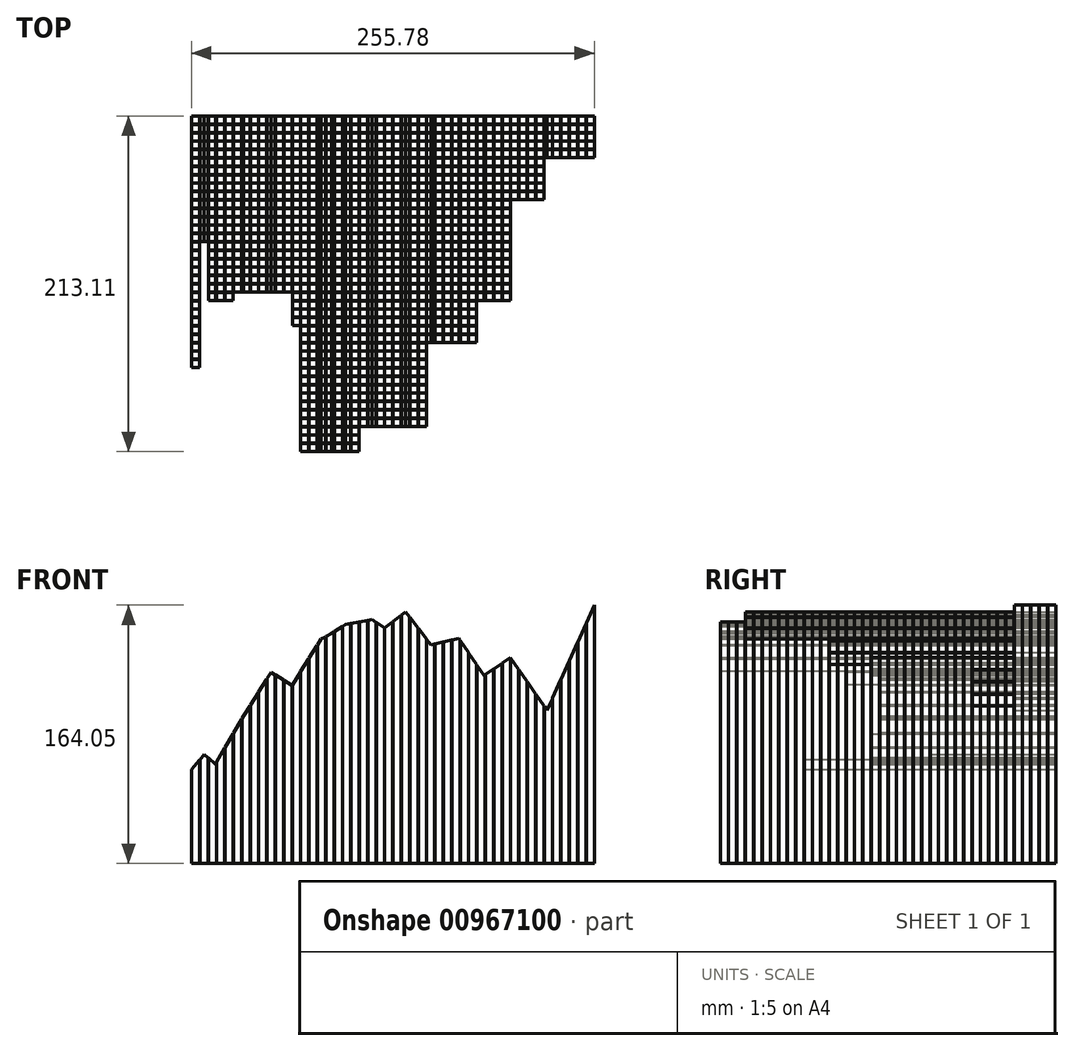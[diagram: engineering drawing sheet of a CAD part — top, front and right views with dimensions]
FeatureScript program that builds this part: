
annotation { "Feature Type Name" : "Feature", "Feature Type Description" : "" }
export const myFeature = defineFeature(function(context is Context, id is Id, definition is map)
    precondition{}
    {
        {
            var Q0;
            Q0=qCreatedBy(makeId("Top.planeOp"),FACE);
            var sketch = newSketch(context, id + "F0", { "sketchPlane" : qUnion([Q0])});
            skLineSegment(sketch, "E0.bottom", {"start": v(0, 0) * mm, "end": v(5.08, 0) * mm});
            skLineSegment(sketch, "E0.top", {"start": v(0, -5.08) * mm, "end": v(5.08, -5.08) * mm});
            skLineSegment(sketch, "E0.left", {"start": v(0, 0) * mm, "end": v(0, -5.08) * mm});
            skLineSegment(sketch, "E0.right", {"start": v(5.08, 0) * mm, "end": v(5.08, -5.08) * mm});
            skLineSegment(sketch, "E1.1.0.0", {"start": v(5.33, -5.08) * mm, "end": v(10.41, -5.08) * mm});
            skLineSegment(sketch, "E1.1.0.1", {"start": v(5.33, 0) * mm, "end": v(5.33, -5.08) * mm});
            skLineSegment(sketch, "E1.1.0.2", {"start": v(5.33, 0) * mm, "end": v(10.41, 0) * mm});
            skLineSegment(sketch, "E1.1.0.3", {"start": v(10.41, 0) * mm, "end": v(10.41, -5.08) * mm});
            skLineSegment(sketch, "E1.2.0.0", {"start": v(10.67, -5.08) * mm, "end": v(15.75, -5.08) * mm});
            skLineSegment(sketch, "E1.2.0.1", {"start": v(10.67, 0) * mm, "end": v(10.67, -5.08) * mm});
            skLineSegment(sketch, "E1.2.0.2", {"start": v(10.67, 0) * mm, "end": v(15.75, 0) * mm});
            skLineSegment(sketch, "E1.2.0.3", {"start": v(15.75, 0) * mm, "end": v(15.75, -5.08) * mm});
            skLineSegment(sketch, "E1.3.0.0", {"start": v(16, -5.08) * mm, "end": v(21.08, -5.08) * mm});
            skLineSegment(sketch, "E1.3.0.1", {"start": v(16, 0) * mm, "end": v(16, -5.08) * mm});
            skLineSegment(sketch, "E1.3.0.2", {"start": v(16, 0) * mm, "end": v(21.08, 0) * mm});
            skLineSegment(sketch, "E1.3.0.3", {"start": v(21.08, 0) * mm, "end": v(21.08, -5.08) * mm});
            skLineSegment(sketch, "E1.4.0.0", {"start": v(21.34, -5.08) * mm, "end": v(26.42, -5.08) * mm});
            skLineSegment(sketch, "E1.4.0.1", {"start": v(21.34, 0) * mm, "end": v(21.34, -5.08) * mm});
            skLineSegment(sketch, "E1.4.0.2", {"start": v(21.34, 0) * mm, "end": v(26.42, 0) * mm});
            skLineSegment(sketch, "E1.4.0.3", {"start": v(26.42, 0) * mm, "end": v(26.42, -5.08) * mm});
            skLineSegment(sketch, "E1.5.0.0", {"start": v(26.67, -5.08) * mm, "end": v(31.75, -5.08) * mm});
            skLineSegment(sketch, "E1.5.0.1", {"start": v(26.67, 0) * mm, "end": v(26.67, -5.08) * mm});
            skLineSegment(sketch, "E1.5.0.2", {"start": v(26.67, 0) * mm, "end": v(31.75, 0) * mm});
            skLineSegment(sketch, "E1.5.0.3", {"start": v(31.75, 0) * mm, "end": v(31.75, -5.08) * mm});
            skLineSegment(sketch, "E1.6.0.0", {"start": v(32, -5.08) * mm, "end": v(37.08, -5.08) * mm});
            skLineSegment(sketch, "E1.6.0.1", {"start": v(32, 0) * mm, "end": v(32, -5.08) * mm});
            skLineSegment(sketch, "E1.6.0.2", {"start": v(32, 0) * mm, "end": v(37.08, 0) * mm});
            skLineSegment(sketch, "E1.6.0.3", {"start": v(37.08, 0) * mm, "end": v(37.08, -5.08) * mm});
            skLineSegment(sketch, "E1.7.0.0", {"start": v(37.34, -5.08) * mm, "end": v(42.42, -5.08) * mm});
            skLineSegment(sketch, "E1.7.0.1", {"start": v(37.34, 0) * mm, "end": v(37.34, -5.08) * mm});
            skLineSegment(sketch, "E1.7.0.2", {"start": v(37.34, 0) * mm, "end": v(42.42, 0) * mm});
            skLineSegment(sketch, "E1.7.0.3", {"start": v(42.42, 0) * mm, "end": v(42.42, -5.08) * mm});
            skLineSegment(sketch, "E1.8.0.0", {"start": v(42.67, -5.08) * mm, "end": v(47.75, -5.08) * mm});
            skLineSegment(sketch, "E1.8.0.1", {"start": v(42.67, 0) * mm, "end": v(42.67, -5.08) * mm});
            skLineSegment(sketch, "E1.8.0.2", {"start": v(42.67, 0) * mm, "end": v(47.75, 0) * mm});
            skLineSegment(sketch, "E1.8.0.3", {"start": v(47.75, 0) * mm, "end": v(47.75, -5.08) * mm});
            skLineSegment(sketch, "E1.9.0.0", {"start": v(48, -5.08) * mm, "end": v(53.09, -5.08) * mm});
            skLineSegment(sketch, "E1.9.0.1", {"start": v(48, 0) * mm, "end": v(48, -5.08) * mm});
            skLineSegment(sketch, "E1.9.0.2", {"start": v(48, 0) * mm, "end": v(53.09, 0) * mm});
            skLineSegment(sketch, "E1.9.0.3", {"start": v(53.09, 0) * mm, "end": v(53.09, -5.08) * mm});
            skLineSegment(sketch, "E1.10.0.0", {"start": v(53.34, -5.08) * mm, "end": v(58.42, -5.08) * mm});
            skLineSegment(sketch, "E1.10.0.1", {"start": v(53.34, 0) * mm, "end": v(53.34, -5.08) * mm});
            skLineSegment(sketch, "E1.10.0.2", {"start": v(53.34, 0) * mm, "end": v(58.42, 0) * mm});
            skLineSegment(sketch, "E1.10.0.3", {"start": v(58.42, 0) * mm, "end": v(58.42, -5.08) * mm});
            skLineSegment(sketch, "E1.11.0.0", {"start": v(58.67, -5.08) * mm, "end": v(63.75, -5.08) * mm});
            skLineSegment(sketch, "E1.11.0.1", {"start": v(58.67, 0) * mm, "end": v(58.67, -5.08) * mm});
            skLineSegment(sketch, "E1.11.0.2", {"start": v(58.67, 0) * mm, "end": v(63.75, 0) * mm});
            skLineSegment(sketch, "E1.11.0.3", {"start": v(63.75, 0) * mm, "end": v(63.75, -5.08) * mm});
            skLineSegment(sketch, "E1.12.0.0", {"start": v(64, -5.08) * mm, "end": v(69.09, -5.08) * mm});
            skLineSegment(sketch, "E1.12.0.1", {"start": v(64, 0) * mm, "end": v(64, -5.08) * mm});
            skLineSegment(sketch, "E1.12.0.2", {"start": v(64, 0) * mm, "end": v(69.09, 0) * mm});
            skLineSegment(sketch, "E1.12.0.3", {"start": v(69.09, 0) * mm, "end": v(69.09, -5.08) * mm});
            skLineSegment(sketch, "E1.13.0.0", {"start": v(69.34, -5.08) * mm, "end": v(74.42, -5.08) * mm});
            skLineSegment(sketch, "E1.13.0.1", {"start": v(69.34, 0) * mm, "end": v(69.34, -5.08) * mm});
            skLineSegment(sketch, "E1.13.0.2", {"start": v(69.34, 0) * mm, "end": v(74.42, 0) * mm});
            skLineSegment(sketch, "E1.13.0.3", {"start": v(74.42, 0) * mm, "end": v(74.42, -5.08) * mm});
            skLineSegment(sketch, "E1.14.0.0", {"start": v(74.68, -5.08) * mm, "end": v(79.76, -5.08) * mm});
            skLineSegment(sketch, "E1.14.0.1", {"start": v(74.68, 0) * mm, "end": v(74.68, -5.08) * mm});
            skLineSegment(sketch, "E1.14.0.2", {"start": v(74.68, 0) * mm, "end": v(79.76, 0) * mm});
            skLineSegment(sketch, "E1.14.0.3", {"start": v(79.76, 0) * mm, "end": v(79.76, -5.08) * mm});
            skLineSegment(sketch, "E1.15.0.0", {"start": v(80, -5.08) * mm, "end": v(85.1, -5.08) * mm});
            skLineSegment(sketch, "E1.15.0.1", {"start": v(80, 0) * mm, "end": v(80, -5.08) * mm});
            skLineSegment(sketch, "E1.15.0.2", {"start": v(80, 0) * mm, "end": v(85.1, 0) * mm});
            skLineSegment(sketch, "E1.15.0.3", {"start": v(85.1, 0) * mm, "end": v(85.1, -5.08) * mm});
            skLineSegment(sketch, "E1.16.0.0", {"start": v(85.34, -5.08) * mm, "end": v(90.42, -5.08) * mm});
            skLineSegment(sketch, "E1.16.0.1", {"start": v(85.34, 0) * mm, "end": v(85.34, -5.08) * mm});
            skLineSegment(sketch, "E1.16.0.2", {"start": v(85.34, 0) * mm, "end": v(90.42, 0) * mm});
            skLineSegment(sketch, "E1.16.0.3", {"start": v(90.42, 0) * mm, "end": v(90.42, -5.08) * mm});
            skLineSegment(sketch, "E1.17.0.0", {"start": v(90.68, -5.08) * mm, "end": v(95.76, -5.08) * mm});
            skLineSegment(sketch, "E1.17.0.1", {"start": v(90.68, 0) * mm, "end": v(90.68, -5.08) * mm});
            skLineSegment(sketch, "E1.17.0.2", {"start": v(90.68, 0) * mm, "end": v(95.76, 0) * mm});
            skLineSegment(sketch, "E1.17.0.3", {"start": v(95.76, 0) * mm, "end": v(95.76, -5.08) * mm});
            skLineSegment(sketch, "E1.18.0.0", {"start": v(96.01, -5.08) * mm, "end": v(101.1, -5.08) * mm});
            skLineSegment(sketch, "E1.18.0.1", {"start": v(96.01, 0) * mm, "end": v(96.01, -5.08) * mm});
            skLineSegment(sketch, "E1.18.0.2", {"start": v(96.01, 0) * mm, "end": v(101.1, 0) * mm});
            skLineSegment(sketch, "E1.18.0.3", {"start": v(101.1, 0) * mm, "end": v(101.1, -5.08) * mm});
            skLineSegment(sketch, "E1.19.0.0", {"start": v(101.35, -5.08) * mm, "end": v(106.43, -5.08) * mm});
            skLineSegment(sketch, "E1.19.0.1", {"start": v(101.35, 0) * mm, "end": v(101.35, -5.08) * mm});
            skLineSegment(sketch, "E1.19.0.2", {"start": v(101.35, 0) * mm, "end": v(106.43, 0) * mm});
            skLineSegment(sketch, "E1.19.0.3", {"start": v(106.43, 0) * mm, "end": v(106.43, -5.08) * mm});
            skLineSegment(sketch, "E1.20.0.0", {"start": v(106.68, -5.08) * mm, "end": v(111.76, -5.08) * mm});
            skLineSegment(sketch, "E1.20.0.1", {"start": v(106.68, 0) * mm, "end": v(106.68, -5.08) * mm});
            skLineSegment(sketch, "E1.20.0.2", {"start": v(106.68, 0) * mm, "end": v(111.76, 0) * mm});
            skLineSegment(sketch, "E1.20.0.3", {"start": v(111.76, 0) * mm, "end": v(111.76, -5.08) * mm});
            skLineSegment(sketch, "E1.21.0.0", {"start": v(112.01, -5.08) * mm, "end": v(117.1, -5.08) * mm});
            skLineSegment(sketch, "E1.21.0.1", {"start": v(112.01, 0) * mm, "end": v(112.01, -5.08) * mm});
            skLineSegment(sketch, "E1.21.0.2", {"start": v(112.01, 0) * mm, "end": v(117.1, 0) * mm});
            skLineSegment(sketch, "E1.21.0.3", {"start": v(117.1, 0) * mm, "end": v(117.1, -5.08) * mm});
            skLineSegment(sketch, "E1.22.0.0", {"start": v(117.35, -5.08) * mm, "end": v(122.43, -5.08) * mm});
            skLineSegment(sketch, "E1.22.0.1", {"start": v(117.35, 0) * mm, "end": v(117.35, -5.08) * mm});
            skLineSegment(sketch, "E1.22.0.2", {"start": v(117.35, 0) * mm, "end": v(122.43, 0) * mm});
            skLineSegment(sketch, "E1.22.0.3", {"start": v(122.43, 0) * mm, "end": v(122.43, -5.08) * mm});
            skLineSegment(sketch, "E1.23.0.0", {"start": v(122.68, -5.08) * mm, "end": v(127.76, -5.08) * mm});
            skLineSegment(sketch, "E1.23.0.1", {"start": v(122.68, 0) * mm, "end": v(122.68, -5.08) * mm});
            skLineSegment(sketch, "E1.23.0.2", {"start": v(122.68, 0) * mm, "end": v(127.76, 0) * mm});
            skLineSegment(sketch, "E1.23.0.3", {"start": v(127.76, 0) * mm, "end": v(127.76, -5.08) * mm});
            skLineSegment(sketch, "E1.24.0.0", {"start": v(128.02, -5.08) * mm, "end": v(133.1, -5.08) * mm});
            skLineSegment(sketch, "E1.24.0.1", {"start": v(128.02, 0) * mm, "end": v(128.02, -5.08) * mm});
            skLineSegment(sketch, "E1.24.0.2", {"start": v(128.02, 0) * mm, "end": v(133.1, 0) * mm});
            skLineSegment(sketch, "E1.24.0.3", {"start": v(133.1, 0) * mm, "end": v(133.1, -5.08) * mm});
            skLineSegment(sketch, "E1.25.0.0", {"start": v(133.35, -5.08) * mm, "end": v(138.43, -5.08) * mm});
            skLineSegment(sketch, "E1.25.0.1", {"start": v(133.35, 0) * mm, "end": v(133.35, -5.08) * mm});
            skLineSegment(sketch, "E1.25.0.2", {"start": v(133.35, 0) * mm, "end": v(138.43, 0) * mm});
            skLineSegment(sketch, "E1.25.0.3", {"start": v(138.43, 0) * mm, "end": v(138.43, -5.08) * mm});
            skLineSegment(sketch, "E1.26.0.0", {"start": v(138.68, -5.08) * mm, "end": v(143.76, -5.08) * mm});
            skLineSegment(sketch, "E1.26.0.1", {"start": v(138.68, 0) * mm, "end": v(138.68, -5.08) * mm});
            skLineSegment(sketch, "E1.26.0.2", {"start": v(138.68, 0) * mm, "end": v(143.76, 0) * mm});
            skLineSegment(sketch, "E1.26.0.3", {"start": v(143.76, 0) * mm, "end": v(143.76, -5.08) * mm});
            skLineSegment(sketch, "E1.27.0.0", {"start": v(144.02, -5.08) * mm, "end": v(149.1, -5.08) * mm});
            skLineSegment(sketch, "E1.27.0.1", {"start": v(144.02, 0) * mm, "end": v(144.02, -5.08) * mm});
            skLineSegment(sketch, "E1.27.0.2", {"start": v(144.02, 0) * mm, "end": v(149.1, 0) * mm});
            skLineSegment(sketch, "E1.27.0.3", {"start": v(149.1, 0) * mm, "end": v(149.1, -5.08) * mm});
            skLineSegment(sketch, "E1.28.0.0", {"start": v(149.35, -5.08) * mm, "end": v(154.43, -5.08) * mm});
            skLineSegment(sketch, "E1.28.0.1", {"start": v(149.35, 0) * mm, "end": v(149.35, -5.08) * mm});
            skLineSegment(sketch, "E1.28.0.2", {"start": v(149.35, 0) * mm, "end": v(154.43, 0) * mm});
            skLineSegment(sketch, "E1.28.0.3", {"start": v(154.43, 0) * mm, "end": v(154.43, -5.08) * mm});
            skLineSegment(sketch, "E1.29.0.0", {"start": v(154.69, -5.08) * mm, "end": v(159.77, -5.08) * mm});
            skLineSegment(sketch, "E1.29.0.1", {"start": v(154.69, 0) * mm, "end": v(154.69, -5.08) * mm});
            skLineSegment(sketch, "E1.29.0.2", {"start": v(154.69, 0) * mm, "end": v(159.77, 0) * mm});
            skLineSegment(sketch, "E1.29.0.3", {"start": v(159.77, 0) * mm, "end": v(159.77, -5.08) * mm});
            skLineSegment(sketch, "E1.30.0.0", {"start": v(160.02, -5.08) * mm, "end": v(165.1, -5.08) * mm});
            skLineSegment(sketch, "E1.30.0.1", {"start": v(160.02, 0) * mm, "end": v(160.02, -5.08) * mm});
            skLineSegment(sketch, "E1.30.0.2", {"start": v(160.02, 0) * mm, "end": v(165.1, 0) * mm});
            skLineSegment(sketch, "E1.30.0.3", {"start": v(165.1, 0) * mm, "end": v(165.1, -5.08) * mm});
            skLineSegment(sketch, "E1.31.0.0", {"start": v(165.35, -5.08) * mm, "end": v(170.43, -5.08) * mm});
            skLineSegment(sketch, "E1.31.0.1", {"start": v(165.35, 0) * mm, "end": v(165.35, -5.08) * mm});
            skLineSegment(sketch, "E1.31.0.2", {"start": v(165.35, 0) * mm, "end": v(170.43, 0) * mm});
            skLineSegment(sketch, "E1.31.0.3", {"start": v(170.43, 0) * mm, "end": v(170.43, -5.08) * mm});
            skLineSegment(sketch, "E1.32.0.0", {"start": v(170.69, -5.08) * mm, "end": v(175.77, -5.08) * mm});
            skLineSegment(sketch, "E1.32.0.1", {"start": v(170.69, 0) * mm, "end": v(170.69, -5.08) * mm});
            skLineSegment(sketch, "E1.32.0.2", {"start": v(170.69, 0) * mm, "end": v(175.77, 0) * mm});
            skLineSegment(sketch, "E1.32.0.3", {"start": v(175.77, 0) * mm, "end": v(175.77, -5.08) * mm});
            skLineSegment(sketch, "E1.33.0.0", {"start": v(176.02, -5.08) * mm, "end": v(181.1, -5.08) * mm});
            skLineSegment(sketch, "E1.33.0.1", {"start": v(176.02, 0) * mm, "end": v(176.02, -5.08) * mm});
            skLineSegment(sketch, "E1.33.0.2", {"start": v(176.02, 0) * mm, "end": v(181.1, 0) * mm});
            skLineSegment(sketch, "E1.33.0.3", {"start": v(181.1, 0) * mm, "end": v(181.1, -5.08) * mm});
            skLineSegment(sketch, "E1.34.0.0", {"start": v(181.36, -5.08) * mm, "end": v(186.44, -5.08) * mm});
            skLineSegment(sketch, "E1.34.0.1", {"start": v(181.36, 0) * mm, "end": v(181.36, -5.08) * mm});
            skLineSegment(sketch, "E1.34.0.2", {"start": v(181.36, 0) * mm, "end": v(186.44, 0) * mm});
            skLineSegment(sketch, "E1.34.0.3", {"start": v(186.44, 0) * mm, "end": v(186.44, -5.08) * mm});
            skLineSegment(sketch, "E1.35.0.0", {"start": v(186.7, -5.08) * mm, "end": v(191.77, -5.08) * mm});
            skLineSegment(sketch, "E1.35.0.1", {"start": v(186.7, 0) * mm, "end": v(186.7, -5.08) * mm});
            skLineSegment(sketch, "E1.35.0.2", {"start": v(186.7, 0) * mm, "end": v(191.77, 0) * mm});
            skLineSegment(sketch, "E1.35.0.3", {"start": v(191.77, 0) * mm, "end": v(191.77, -5.08) * mm});
            skLineSegment(sketch, "E1.direction1", {"start": v(0, -5.08) * mm, "end": v(5.33, -5.08) * mm, "construction": true});
            skLineSegment(sketch, "E2.0.36.0", {"start": v(192.02, -5.08) * mm, "end": v(197.1, -5.08) * mm});
            skLineSegment(sketch, "E2.3.36.0", {"start": v(192.02, 0) * mm, "end": v(192.02, -5.08) * mm});
            skLineSegment(sketch, "E2.6.36.0", {"start": v(192.02, 0) * mm, "end": v(197.1, 0) * mm});
            skLineSegment(sketch, "E2.9.36.0", {"start": v(197.1, 0) * mm, "end": v(197.1, -5.08) * mm});
            skLineSegment(sketch, "E2.0.37.0", {"start": v(197.36, -5.08) * mm, "end": v(202.44, -5.08) * mm});
            skLineSegment(sketch, "E2.3.37.0", {"start": v(197.36, 0) * mm, "end": v(197.36, -5.08) * mm});
            skLineSegment(sketch, "E2.6.37.0", {"start": v(197.36, 0) * mm, "end": v(202.44, 0) * mm});
            skLineSegment(sketch, "E2.9.37.0", {"start": v(202.44, 0) * mm, "end": v(202.44, -5.08) * mm});
            skLineSegment(sketch, "E2.0.38.0", {"start": v(202.7, -5.08) * mm, "end": v(207.77, -5.08) * mm});
            skLineSegment(sketch, "E2.3.38.0", {"start": v(202.7, 0) * mm, "end": v(202.7, -5.08) * mm});
            skLineSegment(sketch, "E2.6.38.0", {"start": v(202.7, 0) * mm, "end": v(207.77, 0) * mm});
            skLineSegment(sketch, "E2.9.38.0", {"start": v(207.77, 0) * mm, "end": v(207.77, -5.08) * mm});
            skLineSegment(sketch, "E2.0.39.0", {"start": v(208.03, -5.08) * mm, "end": v(213.1, -5.08) * mm});
            skLineSegment(sketch, "E2.3.39.0", {"start": v(208.03, 0) * mm, "end": v(208.03, -5.08) * mm});
            skLineSegment(sketch, "E2.6.39.0", {"start": v(208.03, 0) * mm, "end": v(213.1, 0) * mm});
            skLineSegment(sketch, "E2.9.39.0", {"start": v(213.1, 0) * mm, "end": v(213.1, -5.08) * mm});
            skLineSegment(sketch, "E2.0.40.0", {"start": v(213.36, -5.08) * mm, "end": v(218.44, -5.08) * mm});
            skLineSegment(sketch, "E2.3.40.0", {"start": v(213.36, 0) * mm, "end": v(213.36, -5.08) * mm});
            skLineSegment(sketch, "E2.6.40.0", {"start": v(213.36, 0) * mm, "end": v(218.44, 0) * mm});
            skLineSegment(sketch, "E2.9.40.0", {"start": v(218.44, 0) * mm, "end": v(218.44, -5.08) * mm});
            skLineSegment(sketch, "E2.0.41.0", {"start": v(218.7, -5.08) * mm, "end": v(223.77, -5.08) * mm});
            skLineSegment(sketch, "E2.3.41.0", {"start": v(218.7, 0) * mm, "end": v(218.7, -5.08) * mm});
            skLineSegment(sketch, "E2.6.41.0", {"start": v(218.7, 0) * mm, "end": v(223.77, 0) * mm});
            skLineSegment(sketch, "E2.9.41.0", {"start": v(223.77, 0) * mm, "end": v(223.77, -5.08) * mm});
            skLineSegment(sketch, "E2.0.42.0", {"start": v(224.03, -5.08) * mm, "end": v(229.1, -5.08) * mm});
            skLineSegment(sketch, "E2.3.42.0", {"start": v(224.03, 0) * mm, "end": v(224.03, -5.08) * mm});
            skLineSegment(sketch, "E2.6.42.0", {"start": v(224.03, 0) * mm, "end": v(229.1, 0) * mm});
            skLineSegment(sketch, "E2.9.42.0", {"start": v(229.1, 0) * mm, "end": v(229.1, -5.08) * mm});
            skLineSegment(sketch, "E2.0.43.0", {"start": v(229.36, -5.08) * mm, "end": v(234.44, -5.08) * mm});
            skLineSegment(sketch, "E2.3.43.0", {"start": v(229.36, 0) * mm, "end": v(229.36, -5.08) * mm});
            skLineSegment(sketch, "E2.6.43.0", {"start": v(229.36, 0) * mm, "end": v(234.44, 0) * mm});
            skLineSegment(sketch, "E2.9.43.0", {"start": v(234.44, 0) * mm, "end": v(234.44, -5.08) * mm});
            skLineSegment(sketch, "E2.0.44.0", {"start": v(234.7, -5.08) * mm, "end": v(239.78, -5.08) * mm});
            skLineSegment(sketch, "E2.3.44.0", {"start": v(234.7, 0) * mm, "end": v(234.7, -5.08) * mm});
            skLineSegment(sketch, "E2.6.44.0", {"start": v(234.7, 0) * mm, "end": v(239.78, 0) * mm});
            skLineSegment(sketch, "E2.9.44.0", {"start": v(239.78, 0) * mm, "end": v(239.78, -5.08) * mm});
            skLineSegment(sketch, "E2.0.45.0", {"start": v(240.03, -5.08) * mm, "end": v(245.11, -5.08) * mm});
            skLineSegment(sketch, "E2.3.45.0", {"start": v(240.03, 0) * mm, "end": v(240.03, -5.08) * mm});
            skLineSegment(sketch, "E2.6.45.0", {"start": v(240.03, 0) * mm, "end": v(245.11, 0) * mm});
            skLineSegment(sketch, "E2.9.45.0", {"start": v(245.11, 0) * mm, "end": v(245.11, -5.08) * mm});
            skLineSegment(sketch, "E2.0.46.0", {"start": v(245.36, -5.08) * mm, "end": v(250.44, -5.08) * mm});
            skLineSegment(sketch, "E2.3.46.0", {"start": v(245.36, 0) * mm, "end": v(245.36, -5.08) * mm});
            skLineSegment(sketch, "E2.6.46.0", {"start": v(245.36, 0) * mm, "end": v(250.44, 0) * mm});
            skLineSegment(sketch, "E2.9.46.0", {"start": v(250.44, 0) * mm, "end": v(250.44, -5.08) * mm});
            skLineSegment(sketch, "E2.0.47.0", {"start": v(250.7, -5.08) * mm, "end": v(255.78, -5.08) * mm});
            skLineSegment(sketch, "E2.3.47.0", {"start": v(250.7, 0) * mm, "end": v(250.7, -5.08) * mm});
            skLineSegment(sketch, "E2.6.47.0", {"start": v(250.7, 0) * mm, "end": v(255.78, 0) * mm});
            skLineSegment(sketch, "E2.9.47.0", {"start": v(255.78, 0) * mm, "end": v(255.78, -5.08) * mm});
            skSolve(sketch);
        }
        {
            var Q0;
            Q0=qCreatedBy(makeId("Top.planeOp"),FACE);
            var sketch = newSketch(context, id + "F1", { "sketchPlane" : qUnion([Q0])});
            skLineSegment(sketch, "E3.0", {"start": v(5.08, 0) * mm, "end": v(5.08, -5.08) * mm});
            skLineSegment(sketch, "E3.1", {"start": v(0, 0) * mm, "end": v(5.08, 0) * mm});
            skLineSegment(sketch, "E3.2", {"start": v(0, -5.08) * mm, "end": v(5.08, -5.08) * mm});
            skLineSegment(sketch, "E3.3", {"start": v(0, 0) * mm, "end": v(0, -5.08) * mm});
            skLineSegment(sketch, "E4.0.1.0", {"start": v(5.08, -5.33) * mm, "end": v(5.08, -10.41) * mm});
            skLineSegment(sketch, "E4.0.1.1", {"start": v(0, -5.33) * mm, "end": v(0, -10.41) * mm});
            skLineSegment(sketch, "E4.0.1.2", {"start": v(0, -5.33) * mm, "end": v(5.08, -5.33) * mm});
            skLineSegment(sketch, "E4.0.1.3", {"start": v(0, -10.41) * mm, "end": v(5.08, -10.41) * mm});
            skLineSegment(sketch, "E4.0.2.0", {"start": v(5.08, -10.67) * mm, "end": v(5.08, -15.75) * mm});
            skLineSegment(sketch, "E4.0.2.1", {"start": v(0, -10.67) * mm, "end": v(0, -15.75) * mm});
            skLineSegment(sketch, "E4.0.2.2", {"start": v(0, -10.67) * mm, "end": v(5.08, -10.67) * mm});
            skLineSegment(sketch, "E4.0.2.3", {"start": v(0, -15.75) * mm, "end": v(5.08, -15.75) * mm});
            skLineSegment(sketch, "E4.0.3.0", {"start": v(5.08, -16) * mm, "end": v(5.08, -21.08) * mm});
            skLineSegment(sketch, "E4.0.3.1", {"start": v(0, -16) * mm, "end": v(0, -21.08) * mm});
            skLineSegment(sketch, "E4.0.3.2", {"start": v(0, -16) * mm, "end": v(5.08, -16) * mm});
            skLineSegment(sketch, "E4.0.3.3", {"start": v(0, -21.08) * mm, "end": v(5.08, -21.08) * mm});
            skLineSegment(sketch, "E4.0.4.0", {"start": v(5.08, -21.34) * mm, "end": v(5.08, -26.42) * mm});
            skLineSegment(sketch, "E4.0.4.1", {"start": v(0, -21.34) * mm, "end": v(0, -26.42) * mm});
            skLineSegment(sketch, "E4.0.4.2", {"start": v(0, -21.34) * mm, "end": v(5.08, -21.34) * mm});
            skLineSegment(sketch, "E4.0.4.3", {"start": v(0, -26.42) * mm, "end": v(5.08, -26.42) * mm});
            skLineSegment(sketch, "E4.0.5.0", {"start": v(5.08, -26.67) * mm, "end": v(5.08, -31.75) * mm});
            skLineSegment(sketch, "E4.0.5.1", {"start": v(0, -26.67) * mm, "end": v(0, -31.75) * mm});
            skLineSegment(sketch, "E4.0.5.2", {"start": v(0, -26.67) * mm, "end": v(5.08, -26.67) * mm});
            skLineSegment(sketch, "E4.0.5.3", {"start": v(0, -31.75) * mm, "end": v(5.08, -31.75) * mm});
            skLineSegment(sketch, "E4.0.6.0", {"start": v(5.08, -32) * mm, "end": v(5.08, -37.08) * mm});
            skLineSegment(sketch, "E4.0.6.1", {"start": v(0, -32) * mm, "end": v(0, -37.08) * mm});
            skLineSegment(sketch, "E4.0.6.2", {"start": v(0, -32) * mm, "end": v(5.08, -32) * mm});
            skLineSegment(sketch, "E4.0.6.3", {"start": v(0, -37.08) * mm, "end": v(5.08, -37.08) * mm});
            skLineSegment(sketch, "E4.0.7.0", {"start": v(5.08, -37.34) * mm, "end": v(5.08, -42.42) * mm});
            skLineSegment(sketch, "E4.0.7.1", {"start": v(0, -37.34) * mm, "end": v(0, -42.42) * mm});
            skLineSegment(sketch, "E4.0.7.2", {"start": v(0, -37.34) * mm, "end": v(5.08, -37.34) * mm});
            skLineSegment(sketch, "E4.0.7.3", {"start": v(0, -42.42) * mm, "end": v(5.08, -42.42) * mm});
            skLineSegment(sketch, "E4.0.8.0", {"start": v(5.08, -42.67) * mm, "end": v(5.08, -47.75) * mm});
            skLineSegment(sketch, "E4.0.8.1", {"start": v(0, -42.67) * mm, "end": v(0, -47.75) * mm});
            skLineSegment(sketch, "E4.0.8.2", {"start": v(0, -42.67) * mm, "end": v(5.08, -42.67) * mm});
            skLineSegment(sketch, "E4.0.8.3", {"start": v(0, -47.75) * mm, "end": v(5.08, -47.75) * mm});
            skLineSegment(sketch, "E4.0.9.0", {"start": v(5.08, -48) * mm, "end": v(5.08, -53.09) * mm});
            skLineSegment(sketch, "E4.0.9.1", {"start": v(0, -48) * mm, "end": v(0, -53.09) * mm});
            skLineSegment(sketch, "E4.0.9.2", {"start": v(0, -48) * mm, "end": v(5.08, -48) * mm});
            skLineSegment(sketch, "E4.0.9.3", {"start": v(0, -53.09) * mm, "end": v(5.08, -53.09) * mm});
            skLineSegment(sketch, "E4.0.10.0", {"start": v(5.08, -53.34) * mm, "end": v(5.08, -58.42) * mm});
            skLineSegment(sketch, "E4.0.10.1", {"start": v(0, -53.34) * mm, "end": v(0, -58.42) * mm});
            skLineSegment(sketch, "E4.0.10.2", {"start": v(0, -53.34) * mm, "end": v(5.08, -53.34) * mm});
            skLineSegment(sketch, "E4.0.10.3", {"start": v(0, -58.42) * mm, "end": v(5.08, -58.42) * mm});
            skLineSegment(sketch, "E4.0.11.0", {"start": v(5.08, -58.67) * mm, "end": v(5.08, -63.75) * mm});
            skLineSegment(sketch, "E4.0.11.1", {"start": v(0, -58.67) * mm, "end": v(0, -63.75) * mm});
            skLineSegment(sketch, "E4.0.11.2", {"start": v(0, -58.67) * mm, "end": v(5.08, -58.67) * mm});
            skLineSegment(sketch, "E4.0.11.3", {"start": v(0, -63.75) * mm, "end": v(5.08, -63.75) * mm});
            skLineSegment(sketch, "E4.0.12.0", {"start": v(5.08, -64) * mm, "end": v(5.08, -69.09) * mm});
            skLineSegment(sketch, "E4.0.12.1", {"start": v(0, -64) * mm, "end": v(0, -69.09) * mm});
            skLineSegment(sketch, "E4.0.12.2", {"start": v(0, -64) * mm, "end": v(5.08, -64) * mm});
            skLineSegment(sketch, "E4.0.12.3", {"start": v(0, -69.09) * mm, "end": v(5.08, -69.09) * mm});
            skLineSegment(sketch, "E4.0.13.0", {"start": v(5.08, -69.34) * mm, "end": v(5.08, -74.42) * mm});
            skLineSegment(sketch, "E4.0.13.1", {"start": v(0, -69.34) * mm, "end": v(0, -74.42) * mm});
            skLineSegment(sketch, "E4.0.13.2", {"start": v(0, -69.34) * mm, "end": v(5.08, -69.34) * mm});
            skLineSegment(sketch, "E4.0.13.3", {"start": v(0, -74.42) * mm, "end": v(5.08, -74.42) * mm});
            skLineSegment(sketch, "E4.0.14.0", {"start": v(5.08, -74.68) * mm, "end": v(5.08, -79.76) * mm});
            skLineSegment(sketch, "E4.0.14.1", {"start": v(0, -74.68) * mm, "end": v(0, -79.76) * mm});
            skLineSegment(sketch, "E4.0.14.2", {"start": v(0, -74.68) * mm, "end": v(5.08, -74.68) * mm});
            skLineSegment(sketch, "E4.0.14.3", {"start": v(0, -79.76) * mm, "end": v(5.08, -79.76) * mm});
            skLineSegment(sketch, "E4.0.15.0", {"start": v(5.08, -80.01) * mm, "end": v(5.08, -85.1) * mm});
            skLineSegment(sketch, "E4.0.15.1", {"start": v(0, -80.01) * mm, "end": v(0, -85.1) * mm});
            skLineSegment(sketch, "E4.0.15.2", {"start": v(0, -80.01) * mm, "end": v(5.08, -80.01) * mm});
            skLineSegment(sketch, "E4.0.15.3", {"start": v(0, -85.1) * mm, "end": v(5.08, -85.1) * mm});
            skLineSegment(sketch, "E4.0.16.0", {"start": v(5.08, -85.34) * mm, "end": v(5.08, -90.42) * mm});
            skLineSegment(sketch, "E4.0.16.1", {"start": v(0, -85.34) * mm, "end": v(0, -90.42) * mm});
            skLineSegment(sketch, "E4.0.16.2", {"start": v(0, -85.34) * mm, "end": v(5.08, -85.34) * mm});
            skLineSegment(sketch, "E4.0.16.3", {"start": v(0, -90.42) * mm, "end": v(5.08, -90.42) * mm});
            skLineSegment(sketch, "E4.0.17.0", {"start": v(5.08, -90.68) * mm, "end": v(5.08, -95.76) * mm});
            skLineSegment(sketch, "E4.0.17.1", {"start": v(0, -90.68) * mm, "end": v(0, -95.76) * mm});
            skLineSegment(sketch, "E4.0.17.2", {"start": v(0, -90.68) * mm, "end": v(5.08, -90.68) * mm});
            skLineSegment(sketch, "E4.0.17.3", {"start": v(0, -95.76) * mm, "end": v(5.08, -95.76) * mm});
            skLineSegment(sketch, "E4.0.18.0", {"start": v(5.08, -96.01) * mm, "end": v(5.08, -101.1) * mm});
            skLineSegment(sketch, "E4.0.18.1", {"start": v(0, -96.01) * mm, "end": v(0, -101.1) * mm});
            skLineSegment(sketch, "E4.0.18.2", {"start": v(0, -96.01) * mm, "end": v(5.08, -96.01) * mm});
            skLineSegment(sketch, "E4.0.18.3", {"start": v(0, -101.1) * mm, "end": v(5.08, -101.1) * mm});
            skLineSegment(sketch, "E4.0.19.0", {"start": v(5.08, -101.35) * mm, "end": v(5.08, -106.43) * mm});
            skLineSegment(sketch, "E4.0.19.1", {"start": v(0, -101.35) * mm, "end": v(0, -106.43) * mm});
            skLineSegment(sketch, "E4.0.19.2", {"start": v(0, -101.35) * mm, "end": v(5.08, -101.35) * mm});
            skLineSegment(sketch, "E4.0.19.3", {"start": v(0, -106.43) * mm, "end": v(5.08, -106.43) * mm});
            skLineSegment(sketch, "E4.0.20.0", {"start": v(5.08, -106.68) * mm, "end": v(5.08, -111.76) * mm});
            skLineSegment(sketch, "E4.0.20.1", {"start": v(0, -106.68) * mm, "end": v(0, -111.76) * mm});
            skLineSegment(sketch, "E4.0.20.2", {"start": v(0, -106.68) * mm, "end": v(5.08, -106.68) * mm});
            skLineSegment(sketch, "E4.0.20.3", {"start": v(0, -111.76) * mm, "end": v(5.08, -111.76) * mm});
            skLineSegment(sketch, "E4.0.21.0", {"start": v(5.08, -112.01) * mm, "end": v(5.08, -117.1) * mm});
            skLineSegment(sketch, "E4.0.21.1", {"start": v(0, -112.01) * mm, "end": v(0, -117.1) * mm});
            skLineSegment(sketch, "E4.0.21.2", {"start": v(0, -112.01) * mm, "end": v(5.08, -112.01) * mm});
            skLineSegment(sketch, "E4.0.21.3", {"start": v(0, -117.1) * mm, "end": v(5.08, -117.1) * mm});
            skLineSegment(sketch, "E4.0.22.0", {"start": v(5.08, -117.35) * mm, "end": v(5.08, -122.43) * mm});
            skLineSegment(sketch, "E4.0.22.1", {"start": v(0, -117.35) * mm, "end": v(0, -122.43) * mm});
            skLineSegment(sketch, "E4.0.22.2", {"start": v(0, -117.35) * mm, "end": v(5.08, -117.35) * mm});
            skLineSegment(sketch, "E4.0.22.3", {"start": v(0, -122.43) * mm, "end": v(5.08, -122.43) * mm});
            skLineSegment(sketch, "E4.0.23.0", {"start": v(5.08, -122.68) * mm, "end": v(5.08, -127.76) * mm});
            skLineSegment(sketch, "E4.0.23.1", {"start": v(0, -122.68) * mm, "end": v(0, -127.76) * mm});
            skLineSegment(sketch, "E4.0.23.2", {"start": v(0, -122.68) * mm, "end": v(5.08, -122.68) * mm});
            skLineSegment(sketch, "E4.0.23.3", {"start": v(0, -127.76) * mm, "end": v(5.08, -127.76) * mm});
            skLineSegment(sketch, "E4.0.24.0", {"start": v(5.08, -128.02) * mm, "end": v(5.08, -133.1) * mm});
            skLineSegment(sketch, "E4.0.24.1", {"start": v(0, -128.02) * mm, "end": v(0, -133.1) * mm});
            skLineSegment(sketch, "E4.0.24.2", {"start": v(0, -128.02) * mm, "end": v(5.08, -128.02) * mm});
            skLineSegment(sketch, "E4.0.24.3", {"start": v(0, -133.1) * mm, "end": v(5.08, -133.1) * mm});
            skLineSegment(sketch, "E4.0.25.0", {"start": v(5.08, -133.35) * mm, "end": v(5.08, -138.43) * mm});
            skLineSegment(sketch, "E4.0.25.1", {"start": v(0, -133.35) * mm, "end": v(0, -138.43) * mm});
            skLineSegment(sketch, "E4.0.25.2", {"start": v(0, -133.35) * mm, "end": v(5.08, -133.35) * mm});
            skLineSegment(sketch, "E4.0.25.3", {"start": v(0, -138.43) * mm, "end": v(5.08, -138.43) * mm});
            skLineSegment(sketch, "E4.0.26.0", {"start": v(5.08, -138.68) * mm, "end": v(5.08, -143.76) * mm});
            skLineSegment(sketch, "E4.0.26.1", {"start": v(0, -138.68) * mm, "end": v(0, -143.76) * mm});
            skLineSegment(sketch, "E4.0.26.2", {"start": v(0, -138.68) * mm, "end": v(5.08, -138.68) * mm});
            skLineSegment(sketch, "E4.0.26.3", {"start": v(0, -143.76) * mm, "end": v(5.08, -143.76) * mm});
            skLineSegment(sketch, "E4.0.27.0", {"start": v(5.08, -144.02) * mm, "end": v(5.08, -149.1) * mm});
            skLineSegment(sketch, "E4.0.27.1", {"start": v(0, -144.02) * mm, "end": v(0, -149.1) * mm});
            skLineSegment(sketch, "E4.0.27.2", {"start": v(0, -144.02) * mm, "end": v(5.08, -144.02) * mm});
            skLineSegment(sketch, "E4.0.27.3", {"start": v(0, -149.1) * mm, "end": v(5.08, -149.1) * mm});
            skLineSegment(sketch, "E4.0.28.0", {"start": v(5.08, -149.35) * mm, "end": v(5.08, -154.43) * mm});
            skLineSegment(sketch, "E4.0.28.1", {"start": v(0, -149.35) * mm, "end": v(0, -154.43) * mm});
            skLineSegment(sketch, "E4.0.28.2", {"start": v(0, -149.35) * mm, "end": v(5.08, -149.35) * mm});
            skLineSegment(sketch, "E4.0.28.3", {"start": v(0, -154.43) * mm, "end": v(5.08, -154.43) * mm});
            skLineSegment(sketch, "E4.0.29.0", {"start": v(5.08, -154.69) * mm, "end": v(5.08, -159.77) * mm});
            skLineSegment(sketch, "E4.0.29.1", {"start": v(0, -154.69) * mm, "end": v(0, -159.77) * mm});
            skLineSegment(sketch, "E4.0.29.2", {"start": v(0, -154.69) * mm, "end": v(5.08, -154.69) * mm});
            skLineSegment(sketch, "E4.0.29.3", {"start": v(0, -159.77) * mm, "end": v(5.08, -159.77) * mm});
            skLineSegment(sketch, "E4.direction1", {"start": v(0, -5.08) * mm, "end": v(25.4, -5.08) * mm, "construction": true});
            skLineSegment(sketch, "E4.direction2", {"start": v(0, -5.08) * mm, "end": v(0, -10.41) * mm, "construction": true});
            skSolve(sketch);
        }
        {
            var Q0;
            Q0=qCreatedBy(makeId("Top.planeOp"),FACE);
            var sketch = newSketch(context, id + "F2", { "sketchPlane" : qUnion([Q0])});
            skLineSegment(sketch, "E5.0", {"start": v(5.33, 0) * mm, "end": v(10.41, 0) * mm});
            skLineSegment(sketch, "E5.1", {"start": v(10.41, 0) * mm, "end": v(10.41, -5.08) * mm});
            skLineSegment(sketch, "E5.2", {"start": v(5.33, -5.08) * mm, "end": v(10.41, -5.08) * mm});
            skLineSegment(sketch, "E5.3", {"start": v(5.33, 0) * mm, "end": v(5.33, -5.08) * mm});
            skLineSegment(sketch, "E6.0.1.0", {"start": v(5.33, -5.33) * mm, "end": v(10.41, -5.33) * mm});
            skLineSegment(sketch, "E6.0.1.1", {"start": v(10.41, -5.33) * mm, "end": v(10.41, -10.41) * mm});
            skLineSegment(sketch, "E6.0.1.2", {"start": v(5.33, -10.41) * mm, "end": v(10.41, -10.41) * mm});
            skLineSegment(sketch, "E6.0.1.3", {"start": v(5.33, -5.33) * mm, "end": v(5.33, -10.41) * mm});
            skLineSegment(sketch, "E6.0.2.0", {"start": v(5.33, -10.67) * mm, "end": v(10.41, -10.67) * mm});
            skLineSegment(sketch, "E6.0.2.1", {"start": v(10.41, -10.67) * mm, "end": v(10.41, -15.75) * mm});
            skLineSegment(sketch, "E6.0.2.2", {"start": v(5.33, -15.75) * mm, "end": v(10.41, -15.75) * mm});
            skLineSegment(sketch, "E6.0.2.3", {"start": v(5.33, -10.67) * mm, "end": v(5.33, -15.75) * mm});
            skLineSegment(sketch, "E6.0.3.0", {"start": v(5.33, -16) * mm, "end": v(10.41, -16) * mm});
            skLineSegment(sketch, "E6.0.3.1", {"start": v(10.41, -16) * mm, "end": v(10.41, -21.08) * mm});
            skLineSegment(sketch, "E6.0.3.2", {"start": v(5.33, -21.08) * mm, "end": v(10.41, -21.08) * mm});
            skLineSegment(sketch, "E6.0.3.3", {"start": v(5.33, -16) * mm, "end": v(5.33, -21.08) * mm});
            skLineSegment(sketch, "E6.0.4.0", {"start": v(5.33, -21.34) * mm, "end": v(10.41, -21.34) * mm});
            skLineSegment(sketch, "E6.0.4.1", {"start": v(10.41, -21.34) * mm, "end": v(10.41, -26.42) * mm});
            skLineSegment(sketch, "E6.0.4.2", {"start": v(5.33, -26.42) * mm, "end": v(10.41, -26.42) * mm});
            skLineSegment(sketch, "E6.0.4.3", {"start": v(5.33, -21.34) * mm, "end": v(5.33, -26.42) * mm});
            skLineSegment(sketch, "E6.0.5.0", {"start": v(5.33, -26.67) * mm, "end": v(10.41, -26.67) * mm});
            skLineSegment(sketch, "E6.0.5.1", {"start": v(10.41, -26.67) * mm, "end": v(10.41, -31.75) * mm});
            skLineSegment(sketch, "E6.0.5.2", {"start": v(5.33, -31.75) * mm, "end": v(10.41, -31.75) * mm});
            skLineSegment(sketch, "E6.0.5.3", {"start": v(5.33, -26.67) * mm, "end": v(5.33, -31.75) * mm});
            skLineSegment(sketch, "E6.0.6.0", {"start": v(5.33, -32) * mm, "end": v(10.41, -32) * mm});
            skLineSegment(sketch, "E6.0.6.1", {"start": v(10.41, -32) * mm, "end": v(10.41, -37.08) * mm});
            skLineSegment(sketch, "E6.0.6.2", {"start": v(5.33, -37.08) * mm, "end": v(10.41, -37.08) * mm});
            skLineSegment(sketch, "E6.0.6.3", {"start": v(5.33, -32) * mm, "end": v(5.33, -37.08) * mm});
            skLineSegment(sketch, "E6.0.7.0", {"start": v(5.33, -37.34) * mm, "end": v(10.41, -37.34) * mm});
            skLineSegment(sketch, "E6.0.7.1", {"start": v(10.41, -37.34) * mm, "end": v(10.41, -42.42) * mm});
            skLineSegment(sketch, "E6.0.7.2", {"start": v(5.33, -42.42) * mm, "end": v(10.41, -42.42) * mm});
            skLineSegment(sketch, "E6.0.7.3", {"start": v(5.33, -37.34) * mm, "end": v(5.33, -42.42) * mm});
            skLineSegment(sketch, "E6.0.8.0", {"start": v(5.33, -42.67) * mm, "end": v(10.41, -42.67) * mm});
            skLineSegment(sketch, "E6.0.8.1", {"start": v(10.41, -42.67) * mm, "end": v(10.41, -47.75) * mm});
            skLineSegment(sketch, "E6.0.8.2", {"start": v(5.33, -47.75) * mm, "end": v(10.41, -47.75) * mm});
            skLineSegment(sketch, "E6.0.8.3", {"start": v(5.33, -42.67) * mm, "end": v(5.33, -47.75) * mm});
            skLineSegment(sketch, "E6.0.9.0", {"start": v(5.33, -48) * mm, "end": v(10.41, -48) * mm});
            skLineSegment(sketch, "E6.0.9.1", {"start": v(10.41, -48) * mm, "end": v(10.41, -53.09) * mm});
            skLineSegment(sketch, "E6.0.9.2", {"start": v(5.33, -53.09) * mm, "end": v(10.41, -53.09) * mm});
            skLineSegment(sketch, "E6.0.9.3", {"start": v(5.33, -48) * mm, "end": v(5.33, -53.09) * mm});
            skLineSegment(sketch, "E6.0.10.0", {"start": v(5.33, -53.34) * mm, "end": v(10.41, -53.34) * mm});
            skLineSegment(sketch, "E6.0.10.1", {"start": v(10.41, -53.34) * mm, "end": v(10.41, -58.42) * mm});
            skLineSegment(sketch, "E6.0.10.2", {"start": v(5.33, -58.42) * mm, "end": v(10.41, -58.42) * mm});
            skLineSegment(sketch, "E6.0.10.3", {"start": v(5.33, -53.34) * mm, "end": v(5.33, -58.42) * mm});
            skLineSegment(sketch, "E6.0.11.0", {"start": v(5.33, -58.67) * mm, "end": v(10.41, -58.67) * mm});
            skLineSegment(sketch, "E6.0.11.1", {"start": v(10.41, -58.67) * mm, "end": v(10.41, -63.75) * mm});
            skLineSegment(sketch, "E6.0.11.2", {"start": v(5.33, -63.75) * mm, "end": v(10.41, -63.75) * mm});
            skLineSegment(sketch, "E6.0.11.3", {"start": v(5.33, -58.67) * mm, "end": v(5.33, -63.75) * mm});
            skLineSegment(sketch, "E6.0.12.0", {"start": v(5.33, -64) * mm, "end": v(10.41, -64) * mm});
            skLineSegment(sketch, "E6.0.12.1", {"start": v(10.41, -64) * mm, "end": v(10.41, -69.09) * mm});
            skLineSegment(sketch, "E6.0.12.2", {"start": v(5.33, -69.09) * mm, "end": v(10.41, -69.09) * mm});
            skLineSegment(sketch, "E6.0.12.3", {"start": v(5.33, -64) * mm, "end": v(5.33, -69.09) * mm});
            skLineSegment(sketch, "E6.0.13.0", {"start": v(5.33, -69.34) * mm, "end": v(10.41, -69.34) * mm});
            skLineSegment(sketch, "E6.0.13.1", {"start": v(10.41, -69.34) * mm, "end": v(10.41, -74.42) * mm});
            skLineSegment(sketch, "E6.0.13.2", {"start": v(5.33, -74.42) * mm, "end": v(10.41, -74.42) * mm});
            skLineSegment(sketch, "E6.0.13.3", {"start": v(5.33, -69.34) * mm, "end": v(5.33, -74.42) * mm});
            skLineSegment(sketch, "E6.0.14.0", {"start": v(5.33, -74.68) * mm, "end": v(10.41, -74.68) * mm});
            skLineSegment(sketch, "E6.0.14.1", {"start": v(10.41, -74.68) * mm, "end": v(10.41, -79.76) * mm});
            skLineSegment(sketch, "E6.0.14.2", {"start": v(5.33, -79.76) * mm, "end": v(10.41, -79.76) * mm});
            skLineSegment(sketch, "E6.0.14.3", {"start": v(5.33, -74.68) * mm, "end": v(5.33, -79.76) * mm});
            skLineSegment(sketch, "E6.direction1", {"start": v(5.33, 0) * mm, "end": v(30.73, 0) * mm, "construction": true});
            skLineSegment(sketch, "E6.direction2", {"start": v(5.33, 0) * mm, "end": v(5.33, -5.33) * mm, "construction": true});
            skSolve(sketch);
        }
        {
            var Q0;
            Q0=qCreatedBy(makeId("Top.planeOp"),FACE);
            var sketch = newSketch(context, id + "F3", { "sketchPlane" : qUnion([Q0])});
            skLineSegment(sketch, "E7.0.0", {"start": v(15.75, -5.08) * mm, "end": v(15.75, 0) * mm});
            skLineSegment(sketch, "E7.0.1", {"start": v(15.75, 0) * mm, "end": v(10.67, 0) * mm});
            skLineSegment(sketch, "E7.0.2", {"start": v(10.67, 0) * mm, "end": v(10.67, -5.08) * mm});
            skLineSegment(sketch, "E7.0.3", {"start": v(10.67, -5.08) * mm, "end": v(15.75, -5.08) * mm});
            skLineSegment(sketch, "E8.0.0", {"start": v(21.08, -5.08) * mm, "end": v(21.08, 0) * mm});
            skLineSegment(sketch, "E8.0.1", {"start": v(21.08, 0) * mm, "end": v(16, 0) * mm});
            skLineSegment(sketch, "E8.0.2", {"start": v(16, 0) * mm, "end": v(16, -5.08) * mm});
            skLineSegment(sketch, "E8.0.3", {"start": v(16, -5.08) * mm, "end": v(21.08, -5.08) * mm});
            skLineSegment(sketch, "E9.0.0", {"start": v(26.42, -5.08) * mm, "end": v(26.42, 0) * mm});
            skLineSegment(sketch, "E9.0.1", {"start": v(26.42, 0) * mm, "end": v(21.34, 0) * mm});
            skLineSegment(sketch, "E9.0.2", {"start": v(21.34, 0) * mm, "end": v(21.34, -5.08) * mm});
            skLineSegment(sketch, "E9.0.3", {"start": v(21.34, -5.08) * mm, "end": v(26.42, -5.08) * mm});
            skLineSegment(sketch, "E10.0.1.0", {"start": v(21.08, -10.41) * mm, "end": v(21.08, -5.33) * mm});
            skLineSegment(sketch, "E10.0.1.1", {"start": v(21.34, -5.33) * mm, "end": v(21.34, -10.41) * mm});
            skLineSegment(sketch, "E10.0.1.2", {"start": v(16, -5.33) * mm, "end": v(16, -10.41) * mm});
            skLineSegment(sketch, "E10.0.1.3", {"start": v(15.75, -5.33) * mm, "end": v(10.67, -5.33) * mm});
            skLineSegment(sketch, "E10.0.1.4", {"start": v(15.75, -10.41) * mm, "end": v(15.75, -5.33) * mm});
            skLineSegment(sketch, "E10.0.1.5", {"start": v(10.67, -10.41) * mm, "end": v(15.75, -10.41) * mm});
            skLineSegment(sketch, "E10.0.1.6", {"start": v(26.42, -10.41) * mm, "end": v(26.42, -5.33) * mm});
            skLineSegment(sketch, "E10.0.1.7", {"start": v(10.67, -5.33) * mm, "end": v(10.67, -10.41) * mm});
            skLineSegment(sketch, "E10.0.1.8", {"start": v(21.34, -10.41) * mm, "end": v(26.42, -10.41) * mm});
            skLineSegment(sketch, "E10.0.1.9", {"start": v(16, -10.41) * mm, "end": v(21.08, -10.41) * mm});
            skLineSegment(sketch, "E10.0.1.10", {"start": v(21.08, -5.33) * mm, "end": v(16, -5.33) * mm});
            skLineSegment(sketch, "E10.0.1.11", {"start": v(26.42, -5.33) * mm, "end": v(21.34, -5.33) * mm});
            skLineSegment(sketch, "E10.0.2.0", {"start": v(21.08, -15.75) * mm, "end": v(21.08, -10.67) * mm});
            skLineSegment(sketch, "E10.0.2.1", {"start": v(21.34, -10.67) * mm, "end": v(21.34, -15.75) * mm});
            skLineSegment(sketch, "E10.0.2.2", {"start": v(16, -10.67) * mm, "end": v(16, -15.75) * mm});
            skLineSegment(sketch, "E10.0.2.3", {"start": v(15.75, -10.67) * mm, "end": v(10.67, -10.67) * mm});
            skLineSegment(sketch, "E10.0.2.4", {"start": v(15.75, -15.75) * mm, "end": v(15.75, -10.67) * mm});
            skLineSegment(sketch, "E10.0.2.5", {"start": v(10.67, -15.75) * mm, "end": v(15.75, -15.75) * mm});
            skLineSegment(sketch, "E10.0.2.6", {"start": v(26.42, -15.75) * mm, "end": v(26.42, -10.67) * mm});
            skLineSegment(sketch, "E10.0.2.7", {"start": v(10.67, -10.67) * mm, "end": v(10.67, -15.75) * mm});
            skLineSegment(sketch, "E10.0.2.8", {"start": v(21.34, -15.75) * mm, "end": v(26.42, -15.75) * mm});
            skLineSegment(sketch, "E10.0.2.9", {"start": v(16, -15.75) * mm, "end": v(21.08, -15.75) * mm});
            skLineSegment(sketch, "E10.0.2.10", {"start": v(21.08, -10.67) * mm, "end": v(16, -10.67) * mm});
            skLineSegment(sketch, "E10.0.2.11", {"start": v(26.42, -10.67) * mm, "end": v(21.34, -10.67) * mm});
            skLineSegment(sketch, "E10.0.3.0", {"start": v(21.08, -21.08) * mm, "end": v(21.08, -16) * mm});
            skLineSegment(sketch, "E10.0.3.1", {"start": v(21.34, -16) * mm, "end": v(21.34, -21.08) * mm});
            skLineSegment(sketch, "E10.0.3.2", {"start": v(16, -16) * mm, "end": v(16, -21.08) * mm});
            skLineSegment(sketch, "E10.0.3.3", {"start": v(15.75, -16) * mm, "end": v(10.67, -16) * mm});
            skLineSegment(sketch, "E10.0.3.4", {"start": v(15.75, -21.08) * mm, "end": v(15.75, -16) * mm});
            skLineSegment(sketch, "E10.0.3.5", {"start": v(10.67, -21.08) * mm, "end": v(15.75, -21.08) * mm});
            skLineSegment(sketch, "E10.0.3.6", {"start": v(26.42, -21.08) * mm, "end": v(26.42, -16) * mm});
            skLineSegment(sketch, "E10.0.3.7", {"start": v(10.67, -16) * mm, "end": v(10.67, -21.08) * mm});
            skLineSegment(sketch, "E10.0.3.8", {"start": v(21.34, -21.08) * mm, "end": v(26.42, -21.08) * mm});
            skLineSegment(sketch, "E10.0.3.9", {"start": v(16, -21.08) * mm, "end": v(21.08, -21.08) * mm});
            skLineSegment(sketch, "E10.0.3.10", {"start": v(21.08, -16) * mm, "end": v(16, -16) * mm});
            skLineSegment(sketch, "E10.0.3.11", {"start": v(26.42, -16) * mm, "end": v(21.34, -16) * mm});
            skLineSegment(sketch, "E10.0.4.0", {"start": v(21.08, -26.42) * mm, "end": v(21.08, -21.34) * mm});
            skLineSegment(sketch, "E10.0.4.1", {"start": v(21.34, -21.34) * mm, "end": v(21.34, -26.42) * mm});
            skLineSegment(sketch, "E10.0.4.2", {"start": v(16, -21.34) * mm, "end": v(16, -26.42) * mm});
            skLineSegment(sketch, "E10.0.4.3", {"start": v(15.75, -21.34) * mm, "end": v(10.67, -21.34) * mm});
            skLineSegment(sketch, "E10.0.4.4", {"start": v(15.75, -26.42) * mm, "end": v(15.75, -21.34) * mm});
            skLineSegment(sketch, "E10.0.4.5", {"start": v(10.67, -26.42) * mm, "end": v(15.75, -26.42) * mm});
            skLineSegment(sketch, "E10.0.4.6", {"start": v(26.42, -26.42) * mm, "end": v(26.42, -21.34) * mm});
            skLineSegment(sketch, "E10.0.4.7", {"start": v(10.67, -21.34) * mm, "end": v(10.67, -26.42) * mm});
            skLineSegment(sketch, "E10.0.4.8", {"start": v(21.34, -26.42) * mm, "end": v(26.42, -26.42) * mm});
            skLineSegment(sketch, "E10.0.4.9", {"start": v(16, -26.42) * mm, "end": v(21.08, -26.42) * mm});
            skLineSegment(sketch, "E10.0.4.10", {"start": v(21.08, -21.34) * mm, "end": v(16, -21.34) * mm});
            skLineSegment(sketch, "E10.0.4.11", {"start": v(26.42, -21.34) * mm, "end": v(21.34, -21.34) * mm});
            skLineSegment(sketch, "E10.0.5.0", {"start": v(21.08, -31.75) * mm, "end": v(21.08, -26.67) * mm});
            skLineSegment(sketch, "E10.0.5.1", {"start": v(21.34, -26.67) * mm, "end": v(21.34, -31.75) * mm});
            skLineSegment(sketch, "E10.0.5.2", {"start": v(16, -26.67) * mm, "end": v(16, -31.75) * mm});
            skLineSegment(sketch, "E10.0.5.3", {"start": v(15.75, -26.67) * mm, "end": v(10.67, -26.67) * mm});
            skLineSegment(sketch, "E10.0.5.4", {"start": v(15.75, -31.75) * mm, "end": v(15.75, -26.67) * mm});
            skLineSegment(sketch, "E10.0.5.5", {"start": v(10.67, -31.75) * mm, "end": v(15.75, -31.75) * mm});
            skLineSegment(sketch, "E10.0.5.6", {"start": v(26.42, -31.75) * mm, "end": v(26.42, -26.67) * mm});
            skLineSegment(sketch, "E10.0.5.7", {"start": v(10.67, -26.67) * mm, "end": v(10.67, -31.75) * mm});
            skLineSegment(sketch, "E10.0.5.8", {"start": v(21.34, -31.75) * mm, "end": v(26.42, -31.75) * mm});
            skLineSegment(sketch, "E10.0.5.9", {"start": v(16, -31.75) * mm, "end": v(21.08, -31.75) * mm});
            skLineSegment(sketch, "E10.0.5.10", {"start": v(21.08, -26.67) * mm, "end": v(16, -26.67) * mm});
            skLineSegment(sketch, "E10.0.5.11", {"start": v(26.42, -26.67) * mm, "end": v(21.34, -26.67) * mm});
            skLineSegment(sketch, "E10.0.6.0", {"start": v(21.08, -37.08) * mm, "end": v(21.08, -32) * mm});
            skLineSegment(sketch, "E10.0.6.1", {"start": v(21.34, -32) * mm, "end": v(21.34, -37.08) * mm});
            skLineSegment(sketch, "E10.0.6.2", {"start": v(16, -32) * mm, "end": v(16, -37.08) * mm});
            skLineSegment(sketch, "E10.0.6.3", {"start": v(15.75, -32) * mm, "end": v(10.67, -32) * mm});
            skLineSegment(sketch, "E10.0.6.4", {"start": v(15.75, -37.08) * mm, "end": v(15.75, -32) * mm});
            skLineSegment(sketch, "E10.0.6.5", {"start": v(10.67, -37.08) * mm, "end": v(15.75, -37.08) * mm});
            skLineSegment(sketch, "E10.0.6.6", {"start": v(26.42, -37.08) * mm, "end": v(26.42, -32) * mm});
            skLineSegment(sketch, "E10.0.6.7", {"start": v(10.67, -32) * mm, "end": v(10.67, -37.08) * mm});
            skLineSegment(sketch, "E10.0.6.8", {"start": v(21.34, -37.08) * mm, "end": v(26.42, -37.08) * mm});
            skLineSegment(sketch, "E10.0.6.9", {"start": v(16, -37.08) * mm, "end": v(21.08, -37.08) * mm});
            skLineSegment(sketch, "E10.0.6.10", {"start": v(21.08, -32) * mm, "end": v(16, -32) * mm});
            skLineSegment(sketch, "E10.0.6.11", {"start": v(26.42, -32) * mm, "end": v(21.34, -32) * mm});
            skLineSegment(sketch, "E10.0.7.0", {"start": v(21.08, -42.42) * mm, "end": v(21.08, -37.34) * mm});
            skLineSegment(sketch, "E10.0.7.1", {"start": v(21.34, -37.34) * mm, "end": v(21.34, -42.42) * mm});
            skLineSegment(sketch, "E10.0.7.2", {"start": v(16, -37.34) * mm, "end": v(16, -42.42) * mm});
            skLineSegment(sketch, "E10.0.7.3", {"start": v(15.75, -37.34) * mm, "end": v(10.67, -37.34) * mm});
            skLineSegment(sketch, "E10.0.7.4", {"start": v(15.75, -42.42) * mm, "end": v(15.75, -37.34) * mm});
            skLineSegment(sketch, "E10.0.7.5", {"start": v(10.67, -42.42) * mm, "end": v(15.75, -42.42) * mm});
            skLineSegment(sketch, "E10.0.7.6", {"start": v(26.42, -42.42) * mm, "end": v(26.42, -37.34) * mm});
            skLineSegment(sketch, "E10.0.7.7", {"start": v(10.67, -37.34) * mm, "end": v(10.67, -42.42) * mm});
            skLineSegment(sketch, "E10.0.7.8", {"start": v(21.34, -42.42) * mm, "end": v(26.42, -42.42) * mm});
            skLineSegment(sketch, "E10.0.7.9", {"start": v(16, -42.42) * mm, "end": v(21.08, -42.42) * mm});
            skLineSegment(sketch, "E10.0.7.10", {"start": v(21.08, -37.34) * mm, "end": v(16, -37.34) * mm});
            skLineSegment(sketch, "E10.0.7.11", {"start": v(26.42, -37.34) * mm, "end": v(21.34, -37.34) * mm});
            skLineSegment(sketch, "E10.0.8.0", {"start": v(21.08, -47.75) * mm, "end": v(21.08, -42.67) * mm});
            skLineSegment(sketch, "E10.0.8.1", {"start": v(21.34, -42.67) * mm, "end": v(21.34, -47.75) * mm});
            skLineSegment(sketch, "E10.0.8.2", {"start": v(16, -42.67) * mm, "end": v(16, -47.75) * mm});
            skLineSegment(sketch, "E10.0.8.3", {"start": v(15.75, -42.67) * mm, "end": v(10.67, -42.67) * mm});
            skLineSegment(sketch, "E10.0.8.4", {"start": v(15.75, -47.75) * mm, "end": v(15.75, -42.67) * mm});
            skLineSegment(sketch, "E10.0.8.5", {"start": v(10.67, -47.75) * mm, "end": v(15.75, -47.75) * mm});
            skLineSegment(sketch, "E10.0.8.6", {"start": v(26.42, -47.75) * mm, "end": v(26.42, -42.67) * mm});
            skLineSegment(sketch, "E10.0.8.7", {"start": v(10.67, -42.67) * mm, "end": v(10.67, -47.75) * mm});
            skLineSegment(sketch, "E10.0.8.8", {"start": v(21.34, -47.75) * mm, "end": v(26.42, -47.75) * mm});
            skLineSegment(sketch, "E10.0.8.9", {"start": v(16, -47.75) * mm, "end": v(21.08, -47.75) * mm});
            skLineSegment(sketch, "E10.0.8.10", {"start": v(21.08, -42.67) * mm, "end": v(16, -42.67) * mm});
            skLineSegment(sketch, "E10.0.8.11", {"start": v(26.42, -42.67) * mm, "end": v(21.34, -42.67) * mm});
            skLineSegment(sketch, "E10.0.9.0", {"start": v(21.08, -53.09) * mm, "end": v(21.08, -48) * mm});
            skLineSegment(sketch, "E10.0.9.1", {"start": v(21.34, -48) * mm, "end": v(21.34, -53.09) * mm});
            skLineSegment(sketch, "E10.0.9.2", {"start": v(16, -48) * mm, "end": v(16, -53.09) * mm});
            skLineSegment(sketch, "E10.0.9.3", {"start": v(15.75, -48) * mm, "end": v(10.67, -48) * mm});
            skLineSegment(sketch, "E10.0.9.4", {"start": v(15.75, -53.09) * mm, "end": v(15.75, -48) * mm});
            skLineSegment(sketch, "E10.0.9.5", {"start": v(10.67, -53.09) * mm, "end": v(15.75, -53.09) * mm});
            skLineSegment(sketch, "E10.0.9.6", {"start": v(26.42, -53.09) * mm, "end": v(26.42, -48) * mm});
            skLineSegment(sketch, "E10.0.9.7", {"start": v(10.67, -48) * mm, "end": v(10.67, -53.09) * mm});
            skLineSegment(sketch, "E10.0.9.8", {"start": v(21.34, -53.09) * mm, "end": v(26.42, -53.09) * mm});
            skLineSegment(sketch, "E10.0.9.9", {"start": v(16, -53.09) * mm, "end": v(21.08, -53.09) * mm});
            skLineSegment(sketch, "E10.0.9.10", {"start": v(21.08, -48) * mm, "end": v(16, -48) * mm});
            skLineSegment(sketch, "E10.0.9.11", {"start": v(26.42, -48) * mm, "end": v(21.34, -48) * mm});
            skLineSegment(sketch, "E10.0.10.0", {"start": v(21.08, -58.42) * mm, "end": v(21.08, -53.34) * mm});
            skLineSegment(sketch, "E10.0.10.1", {"start": v(21.34, -53.34) * mm, "end": v(21.34, -58.42) * mm});
            skLineSegment(sketch, "E10.0.10.2", {"start": v(16, -53.34) * mm, "end": v(16, -58.42) * mm});
            skLineSegment(sketch, "E10.0.10.3", {"start": v(15.75, -53.34) * mm, "end": v(10.67, -53.34) * mm});
            skLineSegment(sketch, "E10.0.10.4", {"start": v(15.75, -58.42) * mm, "end": v(15.75, -53.34) * mm});
            skLineSegment(sketch, "E10.0.10.5", {"start": v(10.67, -58.42) * mm, "end": v(15.75, -58.42) * mm});
            skLineSegment(sketch, "E10.0.10.6", {"start": v(26.42, -58.42) * mm, "end": v(26.42, -53.34) * mm});
            skLineSegment(sketch, "E10.0.10.7", {"start": v(10.67, -53.34) * mm, "end": v(10.67, -58.42) * mm});
            skLineSegment(sketch, "E10.0.10.8", {"start": v(21.34, -58.42) * mm, "end": v(26.42, -58.42) * mm});
            skLineSegment(sketch, "E10.0.10.9", {"start": v(16, -58.42) * mm, "end": v(21.08, -58.42) * mm});
            skLineSegment(sketch, "E10.0.10.10", {"start": v(21.08, -53.34) * mm, "end": v(16, -53.34) * mm});
            skLineSegment(sketch, "E10.0.10.11", {"start": v(26.42, -53.34) * mm, "end": v(21.34, -53.34) * mm});
            skLineSegment(sketch, "E10.0.11.0", {"start": v(21.08, -63.75) * mm, "end": v(21.08, -58.67) * mm});
            skLineSegment(sketch, "E10.0.11.1", {"start": v(21.34, -58.67) * mm, "end": v(21.34, -63.75) * mm});
            skLineSegment(sketch, "E10.0.11.2", {"start": v(16, -58.67) * mm, "end": v(16, -63.75) * mm});
            skLineSegment(sketch, "E10.0.11.3", {"start": v(15.75, -58.67) * mm, "end": v(10.67, -58.67) * mm});
            skLineSegment(sketch, "E10.0.11.4", {"start": v(15.75, -63.75) * mm, "end": v(15.75, -58.67) * mm});
            skLineSegment(sketch, "E10.0.11.5", {"start": v(10.67, -63.75) * mm, "end": v(15.75, -63.75) * mm});
            skLineSegment(sketch, "E10.0.11.6", {"start": v(26.42, -63.75) * mm, "end": v(26.42, -58.67) * mm});
            skLineSegment(sketch, "E10.0.11.7", {"start": v(10.67, -58.67) * mm, "end": v(10.67, -63.75) * mm});
            skLineSegment(sketch, "E10.0.11.8", {"start": v(21.34, -63.75) * mm, "end": v(26.42, -63.75) * mm});
            skLineSegment(sketch, "E10.0.11.9", {"start": v(16, -63.75) * mm, "end": v(21.08, -63.75) * mm});
            skLineSegment(sketch, "E10.0.11.10", {"start": v(21.08, -58.67) * mm, "end": v(16, -58.67) * mm});
            skLineSegment(sketch, "E10.0.11.11", {"start": v(26.42, -58.67) * mm, "end": v(21.34, -58.67) * mm});
            skLineSegment(sketch, "E10.0.12.0", {"start": v(21.08, -69.09) * mm, "end": v(21.08, -64) * mm});
            skLineSegment(sketch, "E10.0.12.1", {"start": v(21.34, -64) * mm, "end": v(21.34, -69.09) * mm});
            skLineSegment(sketch, "E10.0.12.2", {"start": v(16, -64) * mm, "end": v(16, -69.09) * mm});
            skLineSegment(sketch, "E10.0.12.3", {"start": v(15.75, -64) * mm, "end": v(10.67, -64) * mm});
            skLineSegment(sketch, "E10.0.12.4", {"start": v(15.75, -69.09) * mm, "end": v(15.75, -64) * mm});
            skLineSegment(sketch, "E10.0.12.5", {"start": v(10.67, -69.09) * mm, "end": v(15.75, -69.09) * mm});
            skLineSegment(sketch, "E10.0.12.6", {"start": v(26.42, -69.09) * mm, "end": v(26.42, -64) * mm});
            skLineSegment(sketch, "E10.0.12.7", {"start": v(10.67, -64) * mm, "end": v(10.67, -69.09) * mm});
            skLineSegment(sketch, "E10.0.12.8", {"start": v(21.34, -69.09) * mm, "end": v(26.42, -69.09) * mm});
            skLineSegment(sketch, "E10.0.12.9", {"start": v(16, -69.09) * mm, "end": v(21.08, -69.09) * mm});
            skLineSegment(sketch, "E10.0.12.10", {"start": v(21.08, -64) * mm, "end": v(16, -64) * mm});
            skLineSegment(sketch, "E10.0.12.11", {"start": v(26.42, -64) * mm, "end": v(21.34, -64) * mm});
            skLineSegment(sketch, "E10.0.13.0", {"start": v(21.08, -74.42) * mm, "end": v(21.08, -69.34) * mm});
            skLineSegment(sketch, "E10.0.13.1", {"start": v(21.34, -69.34) * mm, "end": v(21.34, -74.42) * mm});
            skLineSegment(sketch, "E10.0.13.2", {"start": v(16, -69.34) * mm, "end": v(16, -74.42) * mm});
            skLineSegment(sketch, "E10.0.13.3", {"start": v(15.75, -69.34) * mm, "end": v(10.67, -69.34) * mm});
            skLineSegment(sketch, "E10.0.13.4", {"start": v(15.75, -74.42) * mm, "end": v(15.75, -69.34) * mm});
            skLineSegment(sketch, "E10.0.13.5", {"start": v(10.67, -74.42) * mm, "end": v(15.75, -74.42) * mm});
            skLineSegment(sketch, "E10.0.13.6", {"start": v(26.42, -74.42) * mm, "end": v(26.42, -69.34) * mm});
            skLineSegment(sketch, "E10.0.13.7", {"start": v(10.67, -69.34) * mm, "end": v(10.67, -74.42) * mm});
            skLineSegment(sketch, "E10.0.13.8", {"start": v(21.34, -74.42) * mm, "end": v(26.42, -74.42) * mm});
            skLineSegment(sketch, "E10.0.13.9", {"start": v(16, -74.42) * mm, "end": v(21.08, -74.42) * mm});
            skLineSegment(sketch, "E10.0.13.10", {"start": v(21.08, -69.34) * mm, "end": v(16, -69.34) * mm});
            skLineSegment(sketch, "E10.0.13.11", {"start": v(26.42, -69.34) * mm, "end": v(21.34, -69.34) * mm});
            skLineSegment(sketch, "E10.0.14.0", {"start": v(21.08, -79.76) * mm, "end": v(21.08, -74.68) * mm});
            skLineSegment(sketch, "E10.0.14.1", {"start": v(21.34, -74.68) * mm, "end": v(21.34, -79.76) * mm});
            skLineSegment(sketch, "E10.0.14.2", {"start": v(16, -74.68) * mm, "end": v(16, -79.76) * mm});
            skLineSegment(sketch, "E10.0.14.3", {"start": v(15.75, -74.68) * mm, "end": v(10.67, -74.68) * mm});
            skLineSegment(sketch, "E10.0.14.4", {"start": v(15.75, -79.76) * mm, "end": v(15.75, -74.68) * mm});
            skLineSegment(sketch, "E10.0.14.5", {"start": v(10.67, -79.76) * mm, "end": v(15.75, -79.76) * mm});
            skLineSegment(sketch, "E10.0.14.6", {"start": v(26.42, -79.76) * mm, "end": v(26.42, -74.68) * mm});
            skLineSegment(sketch, "E10.0.14.7", {"start": v(10.67, -74.68) * mm, "end": v(10.67, -79.76) * mm});
            skLineSegment(sketch, "E10.0.14.8", {"start": v(21.34, -79.76) * mm, "end": v(26.42, -79.76) * mm});
            skLineSegment(sketch, "E10.0.14.9", {"start": v(16, -79.76) * mm, "end": v(21.08, -79.76) * mm});
            skLineSegment(sketch, "E10.0.14.10", {"start": v(21.08, -74.68) * mm, "end": v(16, -74.68) * mm});
            skLineSegment(sketch, "E10.0.14.11", {"start": v(26.42, -74.68) * mm, "end": v(21.34, -74.68) * mm});
            skLineSegment(sketch, "E10.0.15.0", {"start": v(21.08, -85.1) * mm, "end": v(21.08, -80.01) * mm});
            skLineSegment(sketch, "E10.0.15.1", {"start": v(21.34, -80.01) * mm, "end": v(21.34, -85.1) * mm});
            skLineSegment(sketch, "E10.0.15.2", {"start": v(16, -80.01) * mm, "end": v(16, -85.1) * mm});
            skLineSegment(sketch, "E10.0.15.3", {"start": v(15.75, -80.01) * mm, "end": v(10.67, -80.01) * mm});
            skLineSegment(sketch, "E10.0.15.4", {"start": v(15.75, -85.1) * mm, "end": v(15.75, -80.01) * mm});
            skLineSegment(sketch, "E10.0.15.5", {"start": v(10.67, -85.1) * mm, "end": v(15.75, -85.1) * mm});
            skLineSegment(sketch, "E10.0.15.6", {"start": v(26.42, -85.1) * mm, "end": v(26.42, -80.01) * mm});
            skLineSegment(sketch, "E10.0.15.7", {"start": v(10.67, -80.01) * mm, "end": v(10.67, -85.1) * mm});
            skLineSegment(sketch, "E10.0.15.8", {"start": v(21.34, -85.1) * mm, "end": v(26.42, -85.1) * mm});
            skLineSegment(sketch, "E10.0.15.9", {"start": v(16, -85.1) * mm, "end": v(21.08, -85.1) * mm});
            skLineSegment(sketch, "E10.0.15.10", {"start": v(21.08, -80.01) * mm, "end": v(16, -80.01) * mm});
            skLineSegment(sketch, "E10.0.15.11", {"start": v(26.42, -80.01) * mm, "end": v(21.34, -80.01) * mm});
            skLineSegment(sketch, "E10.0.16.0", {"start": v(21.08, -90.42) * mm, "end": v(21.08, -85.34) * mm});
            skLineSegment(sketch, "E10.0.16.1", {"start": v(21.34, -85.34) * mm, "end": v(21.34, -90.42) * mm});
            skLineSegment(sketch, "E10.0.16.2", {"start": v(16, -85.34) * mm, "end": v(16, -90.42) * mm});
            skLineSegment(sketch, "E10.0.16.3", {"start": v(15.75, -85.34) * mm, "end": v(10.67, -85.34) * mm});
            skLineSegment(sketch, "E10.0.16.4", {"start": v(15.75, -90.42) * mm, "end": v(15.75, -85.34) * mm});
            skLineSegment(sketch, "E10.0.16.5", {"start": v(10.67, -90.42) * mm, "end": v(15.75, -90.42) * mm});
            skLineSegment(sketch, "E10.0.16.6", {"start": v(26.42, -90.42) * mm, "end": v(26.42, -85.34) * mm});
            skLineSegment(sketch, "E10.0.16.7", {"start": v(10.67, -85.34) * mm, "end": v(10.67, -90.42) * mm});
            skLineSegment(sketch, "E10.0.16.8", {"start": v(21.34, -90.42) * mm, "end": v(26.42, -90.42) * mm});
            skLineSegment(sketch, "E10.0.16.9", {"start": v(16, -90.42) * mm, "end": v(21.08, -90.42) * mm});
            skLineSegment(sketch, "E10.0.16.10", {"start": v(21.08, -85.34) * mm, "end": v(16, -85.34) * mm});
            skLineSegment(sketch, "E10.0.16.11", {"start": v(26.42, -85.34) * mm, "end": v(21.34, -85.34) * mm});
            skLineSegment(sketch, "E10.0.17.0", {"start": v(21.08, -95.76) * mm, "end": v(21.08, -90.68) * mm});
            skLineSegment(sketch, "E10.0.17.1", {"start": v(21.34, -90.68) * mm, "end": v(21.34, -95.76) * mm});
            skLineSegment(sketch, "E10.0.17.2", {"start": v(16, -90.68) * mm, "end": v(16, -95.76) * mm});
            skLineSegment(sketch, "E10.0.17.3", {"start": v(15.75, -90.68) * mm, "end": v(10.67, -90.68) * mm});
            skLineSegment(sketch, "E10.0.17.4", {"start": v(15.75, -95.76) * mm, "end": v(15.75, -90.68) * mm});
            skLineSegment(sketch, "E10.0.17.5", {"start": v(10.67, -95.76) * mm, "end": v(15.75, -95.76) * mm});
            skLineSegment(sketch, "E10.0.17.6", {"start": v(26.42, -95.76) * mm, "end": v(26.42, -90.68) * mm});
            skLineSegment(sketch, "E10.0.17.7", {"start": v(10.67, -90.68) * mm, "end": v(10.67, -95.76) * mm});
            skLineSegment(sketch, "E10.0.17.8", {"start": v(21.34, -95.76) * mm, "end": v(26.42, -95.76) * mm});
            skLineSegment(sketch, "E10.0.17.9", {"start": v(16, -95.76) * mm, "end": v(21.08, -95.76) * mm});
            skLineSegment(sketch, "E10.0.17.10", {"start": v(21.08, -90.68) * mm, "end": v(16, -90.68) * mm});
            skLineSegment(sketch, "E10.0.17.11", {"start": v(26.42, -90.68) * mm, "end": v(21.34, -90.68) * mm});
            skLineSegment(sketch, "E10.0.18.0", {"start": v(21.08, -101.1) * mm, "end": v(21.08, -96.01) * mm});
            skLineSegment(sketch, "E10.0.18.1", {"start": v(21.34, -96.01) * mm, "end": v(21.34, -101.1) * mm});
            skLineSegment(sketch, "E10.0.18.2", {"start": v(16, -96.01) * mm, "end": v(16, -101.1) * mm});
            skLineSegment(sketch, "E10.0.18.3", {"start": v(15.75, -96.01) * mm, "end": v(10.67, -96.01) * mm});
            skLineSegment(sketch, "E10.0.18.4", {"start": v(15.75, -101.1) * mm, "end": v(15.75, -96.01) * mm});
            skLineSegment(sketch, "E10.0.18.5", {"start": v(10.67, -101.1) * mm, "end": v(15.75, -101.1) * mm});
            skLineSegment(sketch, "E10.0.18.6", {"start": v(26.42, -101.1) * mm, "end": v(26.42, -96.01) * mm});
            skLineSegment(sketch, "E10.0.18.7", {"start": v(10.67, -96.01) * mm, "end": v(10.67, -101.1) * mm});
            skLineSegment(sketch, "E10.0.18.8", {"start": v(21.34, -101.1) * mm, "end": v(26.42, -101.1) * mm});
            skLineSegment(sketch, "E10.0.18.9", {"start": v(16, -101.1) * mm, "end": v(21.08, -101.1) * mm});
            skLineSegment(sketch, "E10.0.18.10", {"start": v(21.08, -96.01) * mm, "end": v(16, -96.01) * mm});
            skLineSegment(sketch, "E10.0.18.11", {"start": v(26.42, -96.01) * mm, "end": v(21.34, -96.01) * mm});
            skLineSegment(sketch, "E10.0.19.0", {"start": v(21.08, -106.43) * mm, "end": v(21.08, -101.35) * mm});
            skLineSegment(sketch, "E10.0.19.1", {"start": v(21.34, -101.35) * mm, "end": v(21.34, -106.43) * mm});
            skLineSegment(sketch, "E10.0.19.2", {"start": v(16, -101.35) * mm, "end": v(16, -106.43) * mm});
            skLineSegment(sketch, "E10.0.19.3", {"start": v(15.75, -101.35) * mm, "end": v(10.67, -101.35) * mm});
            skLineSegment(sketch, "E10.0.19.4", {"start": v(15.75, -106.43) * mm, "end": v(15.75, -101.35) * mm});
            skLineSegment(sketch, "E10.0.19.5", {"start": v(10.67, -106.43) * mm, "end": v(15.75, -106.43) * mm});
            skLineSegment(sketch, "E10.0.19.6", {"start": v(26.42, -106.43) * mm, "end": v(26.42, -101.35) * mm});
            skLineSegment(sketch, "E10.0.19.7", {"start": v(10.67, -101.35) * mm, "end": v(10.67, -106.43) * mm});
            skLineSegment(sketch, "E10.0.19.8", {"start": v(21.34, -106.43) * mm, "end": v(26.42, -106.43) * mm});
            skLineSegment(sketch, "E10.0.19.9", {"start": v(16, -106.43) * mm, "end": v(21.08, -106.43) * mm});
            skLineSegment(sketch, "E10.0.19.10", {"start": v(21.08, -101.35) * mm, "end": v(16, -101.35) * mm});
            skLineSegment(sketch, "E10.0.19.11", {"start": v(26.42, -101.35) * mm, "end": v(21.34, -101.35) * mm});
            skLineSegment(sketch, "E10.0.20.0", {"start": v(21.08, -111.76) * mm, "end": v(21.08, -106.68) * mm});
            skLineSegment(sketch, "E10.0.20.1", {"start": v(21.34, -106.68) * mm, "end": v(21.34, -111.76) * mm});
            skLineSegment(sketch, "E10.0.20.2", {"start": v(16, -106.68) * mm, "end": v(16, -111.76) * mm});
            skLineSegment(sketch, "E10.0.20.3", {"start": v(15.75, -106.68) * mm, "end": v(10.67, -106.68) * mm});
            skLineSegment(sketch, "E10.0.20.4", {"start": v(15.75, -111.76) * mm, "end": v(15.75, -106.68) * mm});
            skLineSegment(sketch, "E10.0.20.5", {"start": v(10.67, -111.76) * mm, "end": v(15.75, -111.76) * mm});
            skLineSegment(sketch, "E10.0.20.6", {"start": v(26.42, -111.76) * mm, "end": v(26.42, -106.68) * mm});
            skLineSegment(sketch, "E10.0.20.7", {"start": v(10.67, -106.68) * mm, "end": v(10.67, -111.76) * mm});
            skLineSegment(sketch, "E10.0.20.8", {"start": v(21.34, -111.76) * mm, "end": v(26.42, -111.76) * mm});
            skLineSegment(sketch, "E10.0.20.9", {"start": v(16, -111.76) * mm, "end": v(21.08, -111.76) * mm});
            skLineSegment(sketch, "E10.0.20.10", {"start": v(21.08, -106.68) * mm, "end": v(16, -106.68) * mm});
            skLineSegment(sketch, "E10.0.20.11", {"start": v(26.42, -106.68) * mm, "end": v(21.34, -106.68) * mm});
            skLineSegment(sketch, "E10.0.21.0", {"start": v(21.08, -117.1) * mm, "end": v(21.08, -112.01) * mm});
            skLineSegment(sketch, "E10.0.21.1", {"start": v(21.34, -112.01) * mm, "end": v(21.34, -117.1) * mm});
            skLineSegment(sketch, "E10.0.21.2", {"start": v(16, -112.01) * mm, "end": v(16, -117.1) * mm});
            skLineSegment(sketch, "E10.0.21.3", {"start": v(15.75, -112.01) * mm, "end": v(10.67, -112.01) * mm});
            skLineSegment(sketch, "E10.0.21.4", {"start": v(15.75, -117.1) * mm, "end": v(15.75, -112.01) * mm});
            skLineSegment(sketch, "E10.0.21.5", {"start": v(10.67, -117.1) * mm, "end": v(15.75, -117.1) * mm});
            skLineSegment(sketch, "E10.0.21.6", {"start": v(26.42, -117.1) * mm, "end": v(26.42, -112.01) * mm});
            skLineSegment(sketch, "E10.0.21.7", {"start": v(10.67, -112.01) * mm, "end": v(10.67, -117.1) * mm});
            skLineSegment(sketch, "E10.0.21.8", {"start": v(21.34, -117.1) * mm, "end": v(26.42, -117.1) * mm});
            skLineSegment(sketch, "E10.0.21.9", {"start": v(16, -117.1) * mm, "end": v(21.08, -117.1) * mm});
            skLineSegment(sketch, "E10.0.21.10", {"start": v(21.08, -112.01) * mm, "end": v(16, -112.01) * mm});
            skLineSegment(sketch, "E10.0.21.11", {"start": v(26.42, -112.01) * mm, "end": v(21.34, -112.01) * mm});
            skLineSegment(sketch, "E10.direction1", {"start": v(10.67, -5.08) * mm, "end": v(36.07, -5.08) * mm, "construction": true});
            skLineSegment(sketch, "E10.direction2", {"start": v(10.67, -5.08) * mm, "end": v(10.67, -10.41) * mm, "construction": true});
            skSolve(sketch);
        }
        {
            var Q0;
            Q0=qCreatedBy(makeId("Top.planeOp"),FACE);
            var sketch = newSketch(context, id + "F4", { "sketchPlane" : qUnion([Q0])});
            skLineSegment(sketch, "E11.0.0", {"start": v(31.75, -5.08) * mm, "end": v(31.75, 0) * mm});
            skLineSegment(sketch, "E11.0.1", {"start": v(31.75, 0) * mm, "end": v(26.67, 0) * mm});
            skLineSegment(sketch, "E11.0.2", {"start": v(26.67, 0) * mm, "end": v(26.67, -5.08) * mm});
            skLineSegment(sketch, "E11.0.3", {"start": v(26.67, -5.08) * mm, "end": v(31.75, -5.08) * mm});
            skLineSegment(sketch, "E12.0.0", {"start": v(37.08, -5.08) * mm, "end": v(37.08, 0) * mm});
            skLineSegment(sketch, "E12.0.1", {"start": v(37.08, 0) * mm, "end": v(32, 0) * mm});
            skLineSegment(sketch, "E12.0.2", {"start": v(32, 0) * mm, "end": v(32, -5.08) * mm});
            skLineSegment(sketch, "E12.0.3", {"start": v(32, -5.08) * mm, "end": v(37.08, -5.08) * mm});
            skLineSegment(sketch, "E13.0.0", {"start": v(42.42, -5.08) * mm, "end": v(42.42, 0) * mm});
            skLineSegment(sketch, "E13.0.1", {"start": v(42.42, 0) * mm, "end": v(37.34, 0) * mm});
            skLineSegment(sketch, "E13.0.2", {"start": v(37.34, 0) * mm, "end": v(37.34, -5.08) * mm});
            skLineSegment(sketch, "E13.0.3", {"start": v(37.34, -5.08) * mm, "end": v(42.42, -5.08) * mm});
            skLineSegment(sketch, "E14.0.0", {"start": v(47.75, -5.08) * mm, "end": v(47.75, 0) * mm});
            skLineSegment(sketch, "E14.0.1", {"start": v(47.75, 0) * mm, "end": v(42.67, 0) * mm});
            skLineSegment(sketch, "E14.0.2", {"start": v(42.67, 0) * mm, "end": v(42.67, -5.08) * mm});
            skLineSegment(sketch, "E14.0.3", {"start": v(42.67, -5.08) * mm, "end": v(47.75, -5.08) * mm});
            skLineSegment(sketch, "E15.0.0", {"start": v(53.09, -5.08) * mm, "end": v(53.09, 0) * mm});
            skLineSegment(sketch, "E15.0.1", {"start": v(53.09, 0) * mm, "end": v(48, 0) * mm});
            skLineSegment(sketch, "E15.0.2", {"start": v(48, 0) * mm, "end": v(48, -5.08) * mm});
            skLineSegment(sketch, "E15.0.3", {"start": v(48, -5.08) * mm, "end": v(53.09, -5.08) * mm});
            skLineSegment(sketch, "E16.0.0", {"start": v(58.42, -5.08) * mm, "end": v(58.42, 0) * mm});
            skLineSegment(sketch, "E16.0.1", {"start": v(58.42, 0) * mm, "end": v(53.34, 0) * mm});
            skLineSegment(sketch, "E16.0.2", {"start": v(53.34, 0) * mm, "end": v(53.34, -5.08) * mm});
            skLineSegment(sketch, "E16.0.3", {"start": v(53.34, -5.08) * mm, "end": v(58.42, -5.08) * mm});
            skLineSegment(sketch, "E17.0.0", {"start": v(63.75, -5.08) * mm, "end": v(63.75, 0) * mm});
            skLineSegment(sketch, "E17.0.1", {"start": v(63.75, 0) * mm, "end": v(58.67, 0) * mm});
            skLineSegment(sketch, "E17.0.2", {"start": v(58.67, 0) * mm, "end": v(58.67, -5.08) * mm});
            skLineSegment(sketch, "E17.0.3", {"start": v(58.67, -5.08) * mm, "end": v(63.75, -5.08) * mm});
            skLineSegment(sketch, "E18.0.1.0", {"start": v(53.09, -10.41) * mm, "end": v(53.09, -5.33) * mm});
            skLineSegment(sketch, "E18.0.1.1", {"start": v(58.42, -10.41) * mm, "end": v(58.42, -5.33) * mm});
            skLineSegment(sketch, "E18.0.1.2", {"start": v(42.42, -10.41) * mm, "end": v(42.42, -5.33) * mm});
            skLineSegment(sketch, "E18.0.1.3", {"start": v(32, -5.33) * mm, "end": v(32, -10.41) * mm});
            skLineSegment(sketch, "E18.0.1.4", {"start": v(63.75, -5.33) * mm, "end": v(58.67, -5.33) * mm});
            skLineSegment(sketch, "E18.0.1.5", {"start": v(58.67, -5.33) * mm, "end": v(58.67, -10.41) * mm});
            skLineSegment(sketch, "E18.0.1.6", {"start": v(53.34, -10.41) * mm, "end": v(58.42, -10.41) * mm});
            skLineSegment(sketch, "E18.0.1.7", {"start": v(42.42, -5.33) * mm, "end": v(37.34, -5.33) * mm});
            skLineSegment(sketch, "E18.0.1.8", {"start": v(58.42, -5.33) * mm, "end": v(53.34, -5.33) * mm});
            skLineSegment(sketch, "E18.0.1.9", {"start": v(37.08, -10.41) * mm, "end": v(37.08, -5.33) * mm});
            skLineSegment(sketch, "E18.0.1.10", {"start": v(42.67, -5.33) * mm, "end": v(42.67, -10.41) * mm});
            skLineSegment(sketch, "E18.0.1.11", {"start": v(37.08, -5.33) * mm, "end": v(32, -5.33) * mm});
            skLineSegment(sketch, "E18.0.1.12", {"start": v(53.34, -5.33) * mm, "end": v(53.34, -10.41) * mm});
            skLineSegment(sketch, "E18.0.1.13", {"start": v(32, -10.41) * mm, "end": v(37.08, -10.41) * mm});
            skLineSegment(sketch, "E18.0.1.14", {"start": v(31.75, -5.33) * mm, "end": v(26.67, -5.33) * mm});
            skLineSegment(sketch, "E18.0.1.15", {"start": v(42.67, -10.41) * mm, "end": v(47.75, -10.41) * mm});
            skLineSegment(sketch, "E18.0.1.16", {"start": v(37.34, -5.33) * mm, "end": v(37.34, -10.41) * mm});
            skLineSegment(sketch, "E18.0.1.17", {"start": v(26.67, -10.41) * mm, "end": v(31.75, -10.41) * mm});
            skLineSegment(sketch, "E18.0.1.18", {"start": v(26.67, -5.33) * mm, "end": v(26.67, -10.41) * mm});
            skLineSegment(sketch, "E18.0.1.19", {"start": v(47.75, -5.33) * mm, "end": v(42.67, -5.33) * mm});
            skLineSegment(sketch, "E18.0.1.20", {"start": v(58.67, -10.41) * mm, "end": v(63.75, -10.41) * mm});
            skLineSegment(sketch, "E18.0.1.21", {"start": v(37.34, -10.41) * mm, "end": v(42.42, -10.41) * mm});
            skLineSegment(sketch, "E18.0.1.22", {"start": v(63.75, -10.41) * mm, "end": v(63.75, -5.33) * mm});
            skLineSegment(sketch, "E18.0.1.23", {"start": v(48, -10.41) * mm, "end": v(53.09, -10.41) * mm});
            skLineSegment(sketch, "E18.0.1.24", {"start": v(47.75, -10.41) * mm, "end": v(47.75, -5.33) * mm});
            skLineSegment(sketch, "E18.0.1.25", {"start": v(48, -5.33) * mm, "end": v(48, -10.41) * mm});
            skLineSegment(sketch, "E18.0.1.26", {"start": v(53.09, -5.33) * mm, "end": v(48, -5.33) * mm});
            skLineSegment(sketch, "E18.0.1.27", {"start": v(31.75, -10.41) * mm, "end": v(31.75, -5.33) * mm});
            skLineSegment(sketch, "E18.0.2.0", {"start": v(53.09, -15.75) * mm, "end": v(53.09, -10.67) * mm});
            skLineSegment(sketch, "E18.0.2.1", {"start": v(58.42, -15.75) * mm, "end": v(58.42, -10.67) * mm});
            skLineSegment(sketch, "E18.0.2.2", {"start": v(42.42, -15.75) * mm, "end": v(42.42, -10.67) * mm});
            skLineSegment(sketch, "E18.0.2.3", {"start": v(32, -10.67) * mm, "end": v(32, -15.75) * mm});
            skLineSegment(sketch, "E18.0.2.4", {"start": v(63.75, -10.67) * mm, "end": v(58.67, -10.67) * mm});
            skLineSegment(sketch, "E18.0.2.5", {"start": v(58.67, -10.67) * mm, "end": v(58.67, -15.75) * mm});
            skLineSegment(sketch, "E18.0.2.6", {"start": v(53.34, -15.75) * mm, "end": v(58.42, -15.75) * mm});
            skLineSegment(sketch, "E18.0.2.7", {"start": v(42.42, -10.67) * mm, "end": v(37.34, -10.67) * mm});
            skLineSegment(sketch, "E18.0.2.8", {"start": v(58.42, -10.67) * mm, "end": v(53.34, -10.67) * mm});
            skLineSegment(sketch, "E18.0.2.9", {"start": v(37.08, -15.75) * mm, "end": v(37.08, -10.67) * mm});
            skLineSegment(sketch, "E18.0.2.10", {"start": v(42.67, -10.67) * mm, "end": v(42.67, -15.75) * mm});
            skLineSegment(sketch, "E18.0.2.11", {"start": v(37.08, -10.67) * mm, "end": v(32, -10.67) * mm});
            skLineSegment(sketch, "E18.0.2.12", {"start": v(53.34, -10.67) * mm, "end": v(53.34, -15.75) * mm});
            skLineSegment(sketch, "E18.0.2.13", {"start": v(32, -15.75) * mm, "end": v(37.08, -15.75) * mm});
            skLineSegment(sketch, "E18.0.2.14", {"start": v(31.75, -10.67) * mm, "end": v(26.67, -10.67) * mm});
            skLineSegment(sketch, "E18.0.2.15", {"start": v(42.67, -15.75) * mm, "end": v(47.75, -15.75) * mm});
            skLineSegment(sketch, "E18.0.2.16", {"start": v(37.34, -10.67) * mm, "end": v(37.34, -15.75) * mm});
            skLineSegment(sketch, "E18.0.2.17", {"start": v(26.67, -15.75) * mm, "end": v(31.75, -15.75) * mm});
            skLineSegment(sketch, "E18.0.2.18", {"start": v(26.67, -10.67) * mm, "end": v(26.67, -15.75) * mm});
            skLineSegment(sketch, "E18.0.2.19", {"start": v(47.75, -10.67) * mm, "end": v(42.67, -10.67) * mm});
            skLineSegment(sketch, "E18.0.2.20", {"start": v(58.67, -15.75) * mm, "end": v(63.75, -15.75) * mm});
            skLineSegment(sketch, "E18.0.2.21", {"start": v(37.34, -15.75) * mm, "end": v(42.42, -15.75) * mm});
            skLineSegment(sketch, "E18.0.2.22", {"start": v(63.75, -15.75) * mm, "end": v(63.75, -10.67) * mm});
            skLineSegment(sketch, "E18.0.2.23", {"start": v(48, -15.75) * mm, "end": v(53.09, -15.75) * mm});
            skLineSegment(sketch, "E18.0.2.24", {"start": v(47.75, -15.75) * mm, "end": v(47.75, -10.67) * mm});
            skLineSegment(sketch, "E18.0.2.25", {"start": v(48, -10.67) * mm, "end": v(48, -15.75) * mm});
            skLineSegment(sketch, "E18.0.2.26", {"start": v(53.09, -10.67) * mm, "end": v(48, -10.67) * mm});
            skLineSegment(sketch, "E18.0.2.27", {"start": v(31.75, -15.75) * mm, "end": v(31.75, -10.67) * mm});
            skLineSegment(sketch, "E18.0.3.0", {"start": v(53.09, -21.08) * mm, "end": v(53.09, -16) * mm});
            skLineSegment(sketch, "E18.0.3.1", {"start": v(58.42, -21.08) * mm, "end": v(58.42, -16) * mm});
            skLineSegment(sketch, "E18.0.3.2", {"start": v(42.42, -21.08) * mm, "end": v(42.42, -16) * mm});
            skLineSegment(sketch, "E18.0.3.3", {"start": v(32, -16) * mm, "end": v(32, -21.08) * mm});
            skLineSegment(sketch, "E18.0.3.4", {"start": v(63.75, -16) * mm, "end": v(58.67, -16) * mm});
            skLineSegment(sketch, "E18.0.3.5", {"start": v(58.67, -16) * mm, "end": v(58.67, -21.08) * mm});
            skLineSegment(sketch, "E18.0.3.6", {"start": v(53.34, -21.08) * mm, "end": v(58.42, -21.08) * mm});
            skLineSegment(sketch, "E18.0.3.7", {"start": v(42.42, -16) * mm, "end": v(37.34, -16) * mm});
            skLineSegment(sketch, "E18.0.3.8", {"start": v(58.42, -16) * mm, "end": v(53.34, -16) * mm});
            skLineSegment(sketch, "E18.0.3.9", {"start": v(37.08, -21.08) * mm, "end": v(37.08, -16) * mm});
            skLineSegment(sketch, "E18.0.3.10", {"start": v(42.67, -16) * mm, "end": v(42.67, -21.08) * mm});
            skLineSegment(sketch, "E18.0.3.11", {"start": v(37.08, -16) * mm, "end": v(32, -16) * mm});
            skLineSegment(sketch, "E18.0.3.12", {"start": v(53.34, -16) * mm, "end": v(53.34, -21.08) * mm});
            skLineSegment(sketch, "E18.0.3.13", {"start": v(32, -21.08) * mm, "end": v(37.08, -21.08) * mm});
            skLineSegment(sketch, "E18.0.3.14", {"start": v(31.75, -16) * mm, "end": v(26.67, -16) * mm});
            skLineSegment(sketch, "E18.0.3.15", {"start": v(42.67, -21.08) * mm, "end": v(47.75, -21.08) * mm});
            skLineSegment(sketch, "E18.0.3.16", {"start": v(37.34, -16) * mm, "end": v(37.34, -21.08) * mm});
            skLineSegment(sketch, "E18.0.3.17", {"start": v(26.67, -21.08) * mm, "end": v(31.75, -21.08) * mm});
            skLineSegment(sketch, "E18.0.3.18", {"start": v(26.67, -16) * mm, "end": v(26.67, -21.08) * mm});
            skLineSegment(sketch, "E18.0.3.19", {"start": v(47.75, -16) * mm, "end": v(42.67, -16) * mm});
            skLineSegment(sketch, "E18.0.3.20", {"start": v(58.67, -21.08) * mm, "end": v(63.75, -21.08) * mm});
            skLineSegment(sketch, "E18.0.3.21", {"start": v(37.34, -21.08) * mm, "end": v(42.42, -21.08) * mm});
            skLineSegment(sketch, "E18.0.3.22", {"start": v(63.75, -21.08) * mm, "end": v(63.75, -16) * mm});
            skLineSegment(sketch, "E18.0.3.23", {"start": v(48, -21.08) * mm, "end": v(53.09, -21.08) * mm});
            skLineSegment(sketch, "E18.0.3.24", {"start": v(47.75, -21.08) * mm, "end": v(47.75, -16) * mm});
            skLineSegment(sketch, "E18.0.3.25", {"start": v(48, -16) * mm, "end": v(48, -21.08) * mm});
            skLineSegment(sketch, "E18.0.3.26", {"start": v(53.09, -16) * mm, "end": v(48, -16) * mm});
            skLineSegment(sketch, "E18.0.3.27", {"start": v(31.75, -21.08) * mm, "end": v(31.75, -16) * mm});
            skLineSegment(sketch, "E18.0.4.0", {"start": v(53.09, -26.42) * mm, "end": v(53.09, -21.34) * mm});
            skLineSegment(sketch, "E18.0.4.1", {"start": v(58.42, -26.42) * mm, "end": v(58.42, -21.34) * mm});
            skLineSegment(sketch, "E18.0.4.2", {"start": v(42.42, -26.42) * mm, "end": v(42.42, -21.34) * mm});
            skLineSegment(sketch, "E18.0.4.3", {"start": v(32, -21.34) * mm, "end": v(32, -26.42) * mm});
            skLineSegment(sketch, "E18.0.4.4", {"start": v(63.75, -21.34) * mm, "end": v(58.67, -21.34) * mm});
            skLineSegment(sketch, "E18.0.4.5", {"start": v(58.67, -21.34) * mm, "end": v(58.67, -26.42) * mm});
            skLineSegment(sketch, "E18.0.4.6", {"start": v(53.34, -26.42) * mm, "end": v(58.42, -26.42) * mm});
            skLineSegment(sketch, "E18.0.4.7", {"start": v(42.42, -21.34) * mm, "end": v(37.34, -21.34) * mm});
            skLineSegment(sketch, "E18.0.4.8", {"start": v(58.42, -21.34) * mm, "end": v(53.34, -21.34) * mm});
            skLineSegment(sketch, "E18.0.4.9", {"start": v(37.08, -26.42) * mm, "end": v(37.08, -21.34) * mm});
            skLineSegment(sketch, "E18.0.4.10", {"start": v(42.67, -21.34) * mm, "end": v(42.67, -26.42) * mm});
            skLineSegment(sketch, "E18.0.4.11", {"start": v(37.08, -21.34) * mm, "end": v(32, -21.34) * mm});
            skLineSegment(sketch, "E18.0.4.12", {"start": v(53.34, -21.34) * mm, "end": v(53.34, -26.42) * mm});
            skLineSegment(sketch, "E18.0.4.13", {"start": v(32, -26.42) * mm, "end": v(37.08, -26.42) * mm});
            skLineSegment(sketch, "E18.0.4.14", {"start": v(31.75, -21.34) * mm, "end": v(26.67, -21.34) * mm});
            skLineSegment(sketch, "E18.0.4.15", {"start": v(42.67, -26.42) * mm, "end": v(47.75, -26.42) * mm});
            skLineSegment(sketch, "E18.0.4.16", {"start": v(37.34, -21.34) * mm, "end": v(37.34, -26.42) * mm});
            skLineSegment(sketch, "E18.0.4.17", {"start": v(26.67, -26.42) * mm, "end": v(31.75, -26.42) * mm});
            skLineSegment(sketch, "E18.0.4.18", {"start": v(26.67, -21.34) * mm, "end": v(26.67, -26.42) * mm});
            skLineSegment(sketch, "E18.0.4.19", {"start": v(47.75, -21.34) * mm, "end": v(42.67, -21.34) * mm});
            skLineSegment(sketch, "E18.0.4.20", {"start": v(58.67, -26.42) * mm, "end": v(63.75, -26.42) * mm});
            skLineSegment(sketch, "E18.0.4.21", {"start": v(37.34, -26.42) * mm, "end": v(42.42, -26.42) * mm});
            skLineSegment(sketch, "E18.0.4.22", {"start": v(63.75, -26.42) * mm, "end": v(63.75, -21.34) * mm});
            skLineSegment(sketch, "E18.0.4.23", {"start": v(48, -26.42) * mm, "end": v(53.09, -26.42) * mm});
            skLineSegment(sketch, "E18.0.4.24", {"start": v(47.75, -26.42) * mm, "end": v(47.75, -21.34) * mm});
            skLineSegment(sketch, "E18.0.4.25", {"start": v(48, -21.34) * mm, "end": v(48, -26.42) * mm});
            skLineSegment(sketch, "E18.0.4.26", {"start": v(53.09, -21.34) * mm, "end": v(48, -21.34) * mm});
            skLineSegment(sketch, "E18.0.4.27", {"start": v(31.75, -26.42) * mm, "end": v(31.75, -21.34) * mm});
            skLineSegment(sketch, "E18.0.5.0", {"start": v(53.09, -31.75) * mm, "end": v(53.09, -26.67) * mm});
            skLineSegment(sketch, "E18.0.5.1", {"start": v(58.42, -31.75) * mm, "end": v(58.42, -26.67) * mm});
            skLineSegment(sketch, "E18.0.5.2", {"start": v(42.42, -31.75) * mm, "end": v(42.42, -26.67) * mm});
            skLineSegment(sketch, "E18.0.5.3", {"start": v(32, -26.67) * mm, "end": v(32, -31.75) * mm});
            skLineSegment(sketch, "E18.0.5.4", {"start": v(63.75, -26.67) * mm, "end": v(58.67, -26.67) * mm});
            skLineSegment(sketch, "E18.0.5.5", {"start": v(58.67, -26.67) * mm, "end": v(58.67, -31.75) * mm});
            skLineSegment(sketch, "E18.0.5.6", {"start": v(53.34, -31.75) * mm, "end": v(58.42, -31.75) * mm});
            skLineSegment(sketch, "E18.0.5.7", {"start": v(42.42, -26.67) * mm, "end": v(37.34, -26.67) * mm});
            skLineSegment(sketch, "E18.0.5.8", {"start": v(58.42, -26.67) * mm, "end": v(53.34, -26.67) * mm});
            skLineSegment(sketch, "E18.0.5.9", {"start": v(37.08, -31.75) * mm, "end": v(37.08, -26.67) * mm});
            skLineSegment(sketch, "E18.0.5.10", {"start": v(42.67, -26.67) * mm, "end": v(42.67, -31.75) * mm});
            skLineSegment(sketch, "E18.0.5.11", {"start": v(37.08, -26.67) * mm, "end": v(32, -26.67) * mm});
            skLineSegment(sketch, "E18.0.5.12", {"start": v(53.34, -26.67) * mm, "end": v(53.34, -31.75) * mm});
            skLineSegment(sketch, "E18.0.5.13", {"start": v(32, -31.75) * mm, "end": v(37.08, -31.75) * mm});
            skLineSegment(sketch, "E18.0.5.14", {"start": v(31.75, -26.67) * mm, "end": v(26.67, -26.67) * mm});
            skLineSegment(sketch, "E18.0.5.15", {"start": v(42.67, -31.75) * mm, "end": v(47.75, -31.75) * mm});
            skLineSegment(sketch, "E18.0.5.16", {"start": v(37.34, -26.67) * mm, "end": v(37.34, -31.75) * mm});
            skLineSegment(sketch, "E18.0.5.17", {"start": v(26.67, -31.75) * mm, "end": v(31.75, -31.75) * mm});
            skLineSegment(sketch, "E18.0.5.18", {"start": v(26.67, -26.67) * mm, "end": v(26.67, -31.75) * mm});
            skLineSegment(sketch, "E18.0.5.19", {"start": v(47.75, -26.67) * mm, "end": v(42.67, -26.67) * mm});
            skLineSegment(sketch, "E18.0.5.20", {"start": v(58.67, -31.75) * mm, "end": v(63.75, -31.75) * mm});
            skLineSegment(sketch, "E18.0.5.21", {"start": v(37.34, -31.75) * mm, "end": v(42.42, -31.75) * mm});
            skLineSegment(sketch, "E18.0.5.22", {"start": v(63.75, -31.75) * mm, "end": v(63.75, -26.67) * mm});
            skLineSegment(sketch, "E18.0.5.23", {"start": v(48, -31.75) * mm, "end": v(53.09, -31.75) * mm});
            skLineSegment(sketch, "E18.0.5.24", {"start": v(47.75, -31.75) * mm, "end": v(47.75, -26.67) * mm});
            skLineSegment(sketch, "E18.0.5.25", {"start": v(48, -26.67) * mm, "end": v(48, -31.75) * mm});
            skLineSegment(sketch, "E18.0.5.26", {"start": v(53.09, -26.67) * mm, "end": v(48, -26.67) * mm});
            skLineSegment(sketch, "E18.0.5.27", {"start": v(31.75, -31.75) * mm, "end": v(31.75, -26.67) * mm});
            skLineSegment(sketch, "E18.0.6.0", {"start": v(53.09, -37.08) * mm, "end": v(53.09, -32) * mm});
            skLineSegment(sketch, "E18.0.6.1", {"start": v(58.42, -37.08) * mm, "end": v(58.42, -32) * mm});
            skLineSegment(sketch, "E18.0.6.2", {"start": v(42.42, -37.08) * mm, "end": v(42.42, -32) * mm});
            skLineSegment(sketch, "E18.0.6.3", {"start": v(32, -32) * mm, "end": v(32, -37.08) * mm});
            skLineSegment(sketch, "E18.0.6.4", {"start": v(63.75, -32) * mm, "end": v(58.67, -32) * mm});
            skLineSegment(sketch, "E18.0.6.5", {"start": v(58.67, -32) * mm, "end": v(58.67, -37.08) * mm});
            skLineSegment(sketch, "E18.0.6.6", {"start": v(53.34, -37.08) * mm, "end": v(58.42, -37.08) * mm});
            skLineSegment(sketch, "E18.0.6.7", {"start": v(42.42, -32) * mm, "end": v(37.34, -32) * mm});
            skLineSegment(sketch, "E18.0.6.8", {"start": v(58.42, -32) * mm, "end": v(53.34, -32) * mm});
            skLineSegment(sketch, "E18.0.6.9", {"start": v(37.08, -37.08) * mm, "end": v(37.08, -32) * mm});
            skLineSegment(sketch, "E18.0.6.10", {"start": v(42.67, -32) * mm, "end": v(42.67, -37.08) * mm});
            skLineSegment(sketch, "E18.0.6.11", {"start": v(37.08, -32) * mm, "end": v(32, -32) * mm});
            skLineSegment(sketch, "E18.0.6.12", {"start": v(53.34, -32) * mm, "end": v(53.34, -37.08) * mm});
            skLineSegment(sketch, "E18.0.6.13", {"start": v(32, -37.08) * mm, "end": v(37.08, -37.08) * mm});
            skLineSegment(sketch, "E18.0.6.14", {"start": v(31.75, -32) * mm, "end": v(26.67, -32) * mm});
            skLineSegment(sketch, "E18.0.6.15", {"start": v(42.67, -37.08) * mm, "end": v(47.75, -37.08) * mm});
            skLineSegment(sketch, "E18.0.6.16", {"start": v(37.34, -32) * mm, "end": v(37.34, -37.08) * mm});
            skLineSegment(sketch, "E18.0.6.17", {"start": v(26.67, -37.08) * mm, "end": v(31.75, -37.08) * mm});
            skLineSegment(sketch, "E18.0.6.18", {"start": v(26.67, -32) * mm, "end": v(26.67, -37.08) * mm});
            skLineSegment(sketch, "E18.0.6.19", {"start": v(47.75, -32) * mm, "end": v(42.67, -32) * mm});
            skLineSegment(sketch, "E18.0.6.20", {"start": v(58.67, -37.08) * mm, "end": v(63.75, -37.08) * mm});
            skLineSegment(sketch, "E18.0.6.21", {"start": v(37.34, -37.08) * mm, "end": v(42.42, -37.08) * mm});
            skLineSegment(sketch, "E18.0.6.22", {"start": v(63.75, -37.08) * mm, "end": v(63.75, -32) * mm});
            skLineSegment(sketch, "E18.0.6.23", {"start": v(48, -37.08) * mm, "end": v(53.09, -37.08) * mm});
            skLineSegment(sketch, "E18.0.6.24", {"start": v(47.75, -37.08) * mm, "end": v(47.75, -32) * mm});
            skLineSegment(sketch, "E18.0.6.25", {"start": v(48, -32) * mm, "end": v(48, -37.08) * mm});
            skLineSegment(sketch, "E18.0.6.26", {"start": v(53.09, -32) * mm, "end": v(48, -32) * mm});
            skLineSegment(sketch, "E18.0.6.27", {"start": v(31.75, -37.08) * mm, "end": v(31.75, -32) * mm});
            skLineSegment(sketch, "E18.0.7.0", {"start": v(53.09, -42.42) * mm, "end": v(53.09, -37.34) * mm});
            skLineSegment(sketch, "E18.0.7.1", {"start": v(58.42, -42.42) * mm, "end": v(58.42, -37.34) * mm});
            skLineSegment(sketch, "E18.0.7.2", {"start": v(42.42, -42.42) * mm, "end": v(42.42, -37.34) * mm});
            skLineSegment(sketch, "E18.0.7.3", {"start": v(32, -37.34) * mm, "end": v(32, -42.42) * mm});
            skLineSegment(sketch, "E18.0.7.4", {"start": v(63.75, -37.34) * mm, "end": v(58.67, -37.34) * mm});
            skLineSegment(sketch, "E18.0.7.5", {"start": v(58.67, -37.34) * mm, "end": v(58.67, -42.42) * mm});
            skLineSegment(sketch, "E18.0.7.6", {"start": v(53.34, -42.42) * mm, "end": v(58.42, -42.42) * mm});
            skLineSegment(sketch, "E18.0.7.7", {"start": v(42.42, -37.34) * mm, "end": v(37.34, -37.34) * mm});
            skLineSegment(sketch, "E18.0.7.8", {"start": v(58.42, -37.34) * mm, "end": v(53.34, -37.34) * mm});
            skLineSegment(sketch, "E18.0.7.9", {"start": v(37.08, -42.42) * mm, "end": v(37.08, -37.34) * mm});
            skLineSegment(sketch, "E18.0.7.10", {"start": v(42.67, -37.34) * mm, "end": v(42.67, -42.42) * mm});
            skLineSegment(sketch, "E18.0.7.11", {"start": v(37.08, -37.34) * mm, "end": v(32, -37.34) * mm});
            skLineSegment(sketch, "E18.0.7.12", {"start": v(53.34, -37.34) * mm, "end": v(53.34, -42.42) * mm});
            skLineSegment(sketch, "E18.0.7.13", {"start": v(32, -42.42) * mm, "end": v(37.08, -42.42) * mm});
            skLineSegment(sketch, "E18.0.7.14", {"start": v(31.75, -37.34) * mm, "end": v(26.67, -37.34) * mm});
            skLineSegment(sketch, "E18.0.7.15", {"start": v(42.67, -42.42) * mm, "end": v(47.75, -42.42) * mm});
            skLineSegment(sketch, "E18.0.7.16", {"start": v(37.34, -37.34) * mm, "end": v(37.34, -42.42) * mm});
            skLineSegment(sketch, "E18.0.7.17", {"start": v(26.67, -42.42) * mm, "end": v(31.75, -42.42) * mm});
            skLineSegment(sketch, "E18.0.7.18", {"start": v(26.67, -37.34) * mm, "end": v(26.67, -42.42) * mm});
            skLineSegment(sketch, "E18.0.7.19", {"start": v(47.75, -37.34) * mm, "end": v(42.67, -37.34) * mm});
            skLineSegment(sketch, "E18.0.7.20", {"start": v(58.67, -42.42) * mm, "end": v(63.75, -42.42) * mm});
            skLineSegment(sketch, "E18.0.7.21", {"start": v(37.34, -42.42) * mm, "end": v(42.42, -42.42) * mm});
            skLineSegment(sketch, "E18.0.7.22", {"start": v(63.75, -42.42) * mm, "end": v(63.75, -37.34) * mm});
            skLineSegment(sketch, "E18.0.7.23", {"start": v(48, -42.42) * mm, "end": v(53.09, -42.42) * mm});
            skLineSegment(sketch, "E18.0.7.24", {"start": v(47.75, -42.42) * mm, "end": v(47.75, -37.34) * mm});
            skLineSegment(sketch, "E18.0.7.25", {"start": v(48, -37.34) * mm, "end": v(48, -42.42) * mm});
            skLineSegment(sketch, "E18.0.7.26", {"start": v(53.09, -37.34) * mm, "end": v(48, -37.34) * mm});
            skLineSegment(sketch, "E18.0.7.27", {"start": v(31.75, -42.42) * mm, "end": v(31.75, -37.34) * mm});
            skLineSegment(sketch, "E18.0.8.0", {"start": v(53.09, -47.75) * mm, "end": v(53.09, -42.67) * mm});
            skLineSegment(sketch, "E18.0.8.1", {"start": v(58.42, -47.75) * mm, "end": v(58.42, -42.67) * mm});
            skLineSegment(sketch, "E18.0.8.2", {"start": v(42.42, -47.75) * mm, "end": v(42.42, -42.67) * mm});
            skLineSegment(sketch, "E18.0.8.3", {"start": v(32, -42.67) * mm, "end": v(32, -47.75) * mm});
            skLineSegment(sketch, "E18.0.8.4", {"start": v(63.75, -42.67) * mm, "end": v(58.67, -42.67) * mm});
            skLineSegment(sketch, "E18.0.8.5", {"start": v(58.67, -42.67) * mm, "end": v(58.67, -47.75) * mm});
            skLineSegment(sketch, "E18.0.8.6", {"start": v(53.34, -47.75) * mm, "end": v(58.42, -47.75) * mm});
            skLineSegment(sketch, "E18.0.8.7", {"start": v(42.42, -42.67) * mm, "end": v(37.34, -42.67) * mm});
            skLineSegment(sketch, "E18.0.8.8", {"start": v(58.42, -42.67) * mm, "end": v(53.34, -42.67) * mm});
            skLineSegment(sketch, "E18.0.8.9", {"start": v(37.08, -47.75) * mm, "end": v(37.08, -42.67) * mm});
            skLineSegment(sketch, "E18.0.8.10", {"start": v(42.67, -42.67) * mm, "end": v(42.67, -47.75) * mm});
            skLineSegment(sketch, "E18.0.8.11", {"start": v(37.08, -42.67) * mm, "end": v(32, -42.67) * mm});
            skLineSegment(sketch, "E18.0.8.12", {"start": v(53.34, -42.67) * mm, "end": v(53.34, -47.75) * mm});
            skLineSegment(sketch, "E18.0.8.13", {"start": v(32, -47.75) * mm, "end": v(37.08, -47.75) * mm});
            skLineSegment(sketch, "E18.0.8.14", {"start": v(31.75, -42.67) * mm, "end": v(26.67, -42.67) * mm});
            skLineSegment(sketch, "E18.0.8.15", {"start": v(42.67, -47.75) * mm, "end": v(47.75, -47.75) * mm});
            skLineSegment(sketch, "E18.0.8.16", {"start": v(37.34, -42.67) * mm, "end": v(37.34, -47.75) * mm});
            skLineSegment(sketch, "E18.0.8.17", {"start": v(26.67, -47.75) * mm, "end": v(31.75, -47.75) * mm});
            skLineSegment(sketch, "E18.0.8.18", {"start": v(26.67, -42.67) * mm, "end": v(26.67, -47.75) * mm});
            skLineSegment(sketch, "E18.0.8.19", {"start": v(47.75, -42.67) * mm, "end": v(42.67, -42.67) * mm});
            skLineSegment(sketch, "E18.0.8.20", {"start": v(58.67, -47.75) * mm, "end": v(63.75, -47.75) * mm});
            skLineSegment(sketch, "E18.0.8.21", {"start": v(37.34, -47.75) * mm, "end": v(42.42, -47.75) * mm});
            skLineSegment(sketch, "E18.0.8.22", {"start": v(63.75, -47.75) * mm, "end": v(63.75, -42.67) * mm});
            skLineSegment(sketch, "E18.0.8.23", {"start": v(48, -47.75) * mm, "end": v(53.09, -47.75) * mm});
            skLineSegment(sketch, "E18.0.8.24", {"start": v(47.75, -47.75) * mm, "end": v(47.75, -42.67) * mm});
            skLineSegment(sketch, "E18.0.8.25", {"start": v(48, -42.67) * mm, "end": v(48, -47.75) * mm});
            skLineSegment(sketch, "E18.0.8.26", {"start": v(53.09, -42.67) * mm, "end": v(48, -42.67) * mm});
            skLineSegment(sketch, "E18.0.8.27", {"start": v(31.75, -47.75) * mm, "end": v(31.75, -42.67) * mm});
            skLineSegment(sketch, "E18.0.9.0", {"start": v(53.09, -53.09) * mm, "end": v(53.09, -48) * mm});
            skLineSegment(sketch, "E18.0.9.1", {"start": v(58.42, -53.09) * mm, "end": v(58.42, -48) * mm});
            skLineSegment(sketch, "E18.0.9.2", {"start": v(42.42, -53.09) * mm, "end": v(42.42, -48) * mm});
            skLineSegment(sketch, "E18.0.9.3", {"start": v(32, -48) * mm, "end": v(32, -53.09) * mm});
            skLineSegment(sketch, "E18.0.9.4", {"start": v(63.75, -48) * mm, "end": v(58.67, -48) * mm});
            skLineSegment(sketch, "E18.0.9.5", {"start": v(58.67, -48) * mm, "end": v(58.67, -53.09) * mm});
            skLineSegment(sketch, "E18.0.9.6", {"start": v(53.34, -53.09) * mm, "end": v(58.42, -53.09) * mm});
            skLineSegment(sketch, "E18.0.9.7", {"start": v(42.42, -48) * mm, "end": v(37.34, -48) * mm});
            skLineSegment(sketch, "E18.0.9.8", {"start": v(58.42, -48) * mm, "end": v(53.34, -48) * mm});
            skLineSegment(sketch, "E18.0.9.9", {"start": v(37.08, -53.09) * mm, "end": v(37.08, -48) * mm});
            skLineSegment(sketch, "E18.0.9.10", {"start": v(42.67, -48) * mm, "end": v(42.67, -53.09) * mm});
            skLineSegment(sketch, "E18.0.9.11", {"start": v(37.08, -48) * mm, "end": v(32, -48) * mm});
            skLineSegment(sketch, "E18.0.9.12", {"start": v(53.34, -48) * mm, "end": v(53.34, -53.09) * mm});
            skLineSegment(sketch, "E18.0.9.13", {"start": v(32, -53.09) * mm, "end": v(37.08, -53.09) * mm});
            skLineSegment(sketch, "E18.0.9.14", {"start": v(31.75, -48) * mm, "end": v(26.67, -48) * mm});
            skLineSegment(sketch, "E18.0.9.15", {"start": v(42.67, -53.09) * mm, "end": v(47.75, -53.09) * mm});
            skLineSegment(sketch, "E18.0.9.16", {"start": v(37.34, -48) * mm, "end": v(37.34, -53.09) * mm});
            skLineSegment(sketch, "E18.0.9.17", {"start": v(26.67, -53.09) * mm, "end": v(31.75, -53.09) * mm});
            skLineSegment(sketch, "E18.0.9.18", {"start": v(26.67, -48) * mm, "end": v(26.67, -53.09) * mm});
            skLineSegment(sketch, "E18.0.9.19", {"start": v(47.75, -48) * mm, "end": v(42.67, -48) * mm});
            skLineSegment(sketch, "E18.0.9.20", {"start": v(58.67, -53.09) * mm, "end": v(63.75, -53.09) * mm});
            skLineSegment(sketch, "E18.0.9.21", {"start": v(37.34, -53.09) * mm, "end": v(42.42, -53.09) * mm});
            skLineSegment(sketch, "E18.0.9.22", {"start": v(63.75, -53.09) * mm, "end": v(63.75, -48) * mm});
            skLineSegment(sketch, "E18.0.9.23", {"start": v(48, -53.09) * mm, "end": v(53.09, -53.09) * mm});
            skLineSegment(sketch, "E18.0.9.24", {"start": v(47.75, -53.09) * mm, "end": v(47.75, -48) * mm});
            skLineSegment(sketch, "E18.0.9.25", {"start": v(48, -48) * mm, "end": v(48, -53.09) * mm});
            skLineSegment(sketch, "E18.0.9.26", {"start": v(53.09, -48) * mm, "end": v(48, -48) * mm});
            skLineSegment(sketch, "E18.0.9.27", {"start": v(31.75, -53.09) * mm, "end": v(31.75, -48) * mm});
            skLineSegment(sketch, "E18.0.10.0", {"start": v(53.09, -58.42) * mm, "end": v(53.09, -53.34) * mm});
            skLineSegment(sketch, "E18.0.10.1", {"start": v(58.42, -58.42) * mm, "end": v(58.42, -53.34) * mm});
            skLineSegment(sketch, "E18.0.10.2", {"start": v(42.42, -58.42) * mm, "end": v(42.42, -53.34) * mm});
            skLineSegment(sketch, "E18.0.10.3", {"start": v(32, -53.34) * mm, "end": v(32, -58.42) * mm});
            skLineSegment(sketch, "E18.0.10.4", {"start": v(63.75, -53.34) * mm, "end": v(58.67, -53.34) * mm});
            skLineSegment(sketch, "E18.0.10.5", {"start": v(58.67, -53.34) * mm, "end": v(58.67, -58.42) * mm});
            skLineSegment(sketch, "E18.0.10.6", {"start": v(53.34, -58.42) * mm, "end": v(58.42, -58.42) * mm});
            skLineSegment(sketch, "E18.0.10.7", {"start": v(42.42, -53.34) * mm, "end": v(37.34, -53.34) * mm});
            skLineSegment(sketch, "E18.0.10.8", {"start": v(58.42, -53.34) * mm, "end": v(53.34, -53.34) * mm});
            skLineSegment(sketch, "E18.0.10.9", {"start": v(37.08, -58.42) * mm, "end": v(37.08, -53.34) * mm});
            skLineSegment(sketch, "E18.0.10.10", {"start": v(42.67, -53.34) * mm, "end": v(42.67, -58.42) * mm});
            skLineSegment(sketch, "E18.0.10.11", {"start": v(37.08, -53.34) * mm, "end": v(32, -53.34) * mm});
            skLineSegment(sketch, "E18.0.10.12", {"start": v(53.34, -53.34) * mm, "end": v(53.34, -58.42) * mm});
            skLineSegment(sketch, "E18.0.10.13", {"start": v(32, -58.42) * mm, "end": v(37.08, -58.42) * mm});
            skLineSegment(sketch, "E18.0.10.14", {"start": v(31.75, -53.34) * mm, "end": v(26.67, -53.34) * mm});
            skLineSegment(sketch, "E18.0.10.15", {"start": v(42.67, -58.42) * mm, "end": v(47.75, -58.42) * mm});
            skLineSegment(sketch, "E18.0.10.16", {"start": v(37.34, -53.34) * mm, "end": v(37.34, -58.42) * mm});
            skLineSegment(sketch, "E18.0.10.17", {"start": v(26.67, -58.42) * mm, "end": v(31.75, -58.42) * mm});
            skLineSegment(sketch, "E18.0.10.18", {"start": v(26.67, -53.34) * mm, "end": v(26.67, -58.42) * mm});
            skLineSegment(sketch, "E18.0.10.19", {"start": v(47.75, -53.34) * mm, "end": v(42.67, -53.34) * mm});
            skLineSegment(sketch, "E18.0.10.20", {"start": v(58.67, -58.42) * mm, "end": v(63.75, -58.42) * mm});
            skLineSegment(sketch, "E18.0.10.21", {"start": v(37.34, -58.42) * mm, "end": v(42.42, -58.42) * mm});
            skLineSegment(sketch, "E18.0.10.22", {"start": v(63.75, -58.42) * mm, "end": v(63.75, -53.34) * mm});
            skLineSegment(sketch, "E18.0.10.23", {"start": v(48, -58.42) * mm, "end": v(53.09, -58.42) * mm});
            skLineSegment(sketch, "E18.0.10.24", {"start": v(47.75, -58.42) * mm, "end": v(47.75, -53.34) * mm});
            skLineSegment(sketch, "E18.0.10.25", {"start": v(48, -53.34) * mm, "end": v(48, -58.42) * mm});
            skLineSegment(sketch, "E18.0.10.26", {"start": v(53.09, -53.34) * mm, "end": v(48, -53.34) * mm});
            skLineSegment(sketch, "E18.0.10.27", {"start": v(31.75, -58.42) * mm, "end": v(31.75, -53.34) * mm});
            skLineSegment(sketch, "E18.0.11.0", {"start": v(53.09, -63.75) * mm, "end": v(53.09, -58.67) * mm});
            skLineSegment(sketch, "E18.0.11.1", {"start": v(58.42, -63.75) * mm, "end": v(58.42, -58.67) * mm});
            skLineSegment(sketch, "E18.0.11.2", {"start": v(42.42, -63.75) * mm, "end": v(42.42, -58.67) * mm});
            skLineSegment(sketch, "E18.0.11.3", {"start": v(32, -58.67) * mm, "end": v(32, -63.75) * mm});
            skLineSegment(sketch, "E18.0.11.4", {"start": v(63.75, -58.67) * mm, "end": v(58.67, -58.67) * mm});
            skLineSegment(sketch, "E18.0.11.5", {"start": v(58.67, -58.67) * mm, "end": v(58.67, -63.75) * mm});
            skLineSegment(sketch, "E18.0.11.6", {"start": v(53.34, -63.75) * mm, "end": v(58.42, -63.75) * mm});
            skLineSegment(sketch, "E18.0.11.7", {"start": v(42.42, -58.67) * mm, "end": v(37.34, -58.67) * mm});
            skLineSegment(sketch, "E18.0.11.8", {"start": v(58.42, -58.67) * mm, "end": v(53.34, -58.67) * mm});
            skLineSegment(sketch, "E18.0.11.9", {"start": v(37.08, -63.75) * mm, "end": v(37.08, -58.67) * mm});
            skLineSegment(sketch, "E18.0.11.10", {"start": v(42.67, -58.67) * mm, "end": v(42.67, -63.75) * mm});
            skLineSegment(sketch, "E18.0.11.11", {"start": v(37.08, -58.67) * mm, "end": v(32, -58.67) * mm});
            skLineSegment(sketch, "E18.0.11.12", {"start": v(53.34, -58.67) * mm, "end": v(53.34, -63.75) * mm});
            skLineSegment(sketch, "E18.0.11.13", {"start": v(32, -63.75) * mm, "end": v(37.08, -63.75) * mm});
            skLineSegment(sketch, "E18.0.11.14", {"start": v(31.75, -58.67) * mm, "end": v(26.67, -58.67) * mm});
            skLineSegment(sketch, "E18.0.11.15", {"start": v(42.67, -63.75) * mm, "end": v(47.75, -63.75) * mm});
            skLineSegment(sketch, "E18.0.11.16", {"start": v(37.34, -58.67) * mm, "end": v(37.34, -63.75) * mm});
            skLineSegment(sketch, "E18.0.11.17", {"start": v(26.67, -63.75) * mm, "end": v(31.75, -63.75) * mm});
            skLineSegment(sketch, "E18.0.11.18", {"start": v(26.67, -58.67) * mm, "end": v(26.67, -63.75) * mm});
            skLineSegment(sketch, "E18.0.11.19", {"start": v(47.75, -58.67) * mm, "end": v(42.67, -58.67) * mm});
            skLineSegment(sketch, "E18.0.11.20", {"start": v(58.67, -63.75) * mm, "end": v(63.75, -63.75) * mm});
            skLineSegment(sketch, "E18.0.11.21", {"start": v(37.34, -63.75) * mm, "end": v(42.42, -63.75) * mm});
            skLineSegment(sketch, "E18.0.11.22", {"start": v(63.75, -63.75) * mm, "end": v(63.75, -58.67) * mm});
            skLineSegment(sketch, "E18.0.11.23", {"start": v(48, -63.75) * mm, "end": v(53.09, -63.75) * mm});
            skLineSegment(sketch, "E18.0.11.24", {"start": v(47.75, -63.75) * mm, "end": v(47.75, -58.67) * mm});
            skLineSegment(sketch, "E18.0.11.25", {"start": v(48, -58.67) * mm, "end": v(48, -63.75) * mm});
            skLineSegment(sketch, "E18.0.11.26", {"start": v(53.09, -58.67) * mm, "end": v(48, -58.67) * mm});
            skLineSegment(sketch, "E18.0.11.27", {"start": v(31.75, -63.75) * mm, "end": v(31.75, -58.67) * mm});
            skLineSegment(sketch, "E18.0.12.0", {"start": v(53.09, -69.09) * mm, "end": v(53.09, -64) * mm});
            skLineSegment(sketch, "E18.0.12.1", {"start": v(58.42, -69.09) * mm, "end": v(58.42, -64) * mm});
            skLineSegment(sketch, "E18.0.12.2", {"start": v(42.42, -69.09) * mm, "end": v(42.42, -64) * mm});
            skLineSegment(sketch, "E18.0.12.3", {"start": v(32, -64) * mm, "end": v(32, -69.09) * mm});
            skLineSegment(sketch, "E18.0.12.4", {"start": v(63.75, -64) * mm, "end": v(58.67, -64) * mm});
            skLineSegment(sketch, "E18.0.12.5", {"start": v(58.67, -64) * mm, "end": v(58.67, -69.09) * mm});
            skLineSegment(sketch, "E18.0.12.6", {"start": v(53.34, -69.09) * mm, "end": v(58.42, -69.09) * mm});
            skLineSegment(sketch, "E18.0.12.7", {"start": v(42.42, -64) * mm, "end": v(37.34, -64) * mm});
            skLineSegment(sketch, "E18.0.12.8", {"start": v(58.42, -64) * mm, "end": v(53.34, -64) * mm});
            skLineSegment(sketch, "E18.0.12.9", {"start": v(37.08, -69.09) * mm, "end": v(37.08, -64) * mm});
            skLineSegment(sketch, "E18.0.12.10", {"start": v(42.67, -64) * mm, "end": v(42.67, -69.09) * mm});
            skLineSegment(sketch, "E18.0.12.11", {"start": v(37.08, -64) * mm, "end": v(32, -64) * mm});
            skLineSegment(sketch, "E18.0.12.12", {"start": v(53.34, -64) * mm, "end": v(53.34, -69.09) * mm});
            skLineSegment(sketch, "E18.0.12.13", {"start": v(32, -69.09) * mm, "end": v(37.08, -69.09) * mm});
            skLineSegment(sketch, "E18.0.12.14", {"start": v(31.75, -64) * mm, "end": v(26.67, -64) * mm});
            skLineSegment(sketch, "E18.0.12.15", {"start": v(42.67, -69.09) * mm, "end": v(47.75, -69.09) * mm});
            skLineSegment(sketch, "E18.0.12.16", {"start": v(37.34, -64) * mm, "end": v(37.34, -69.09) * mm});
            skLineSegment(sketch, "E18.0.12.17", {"start": v(26.67, -69.09) * mm, "end": v(31.75, -69.09) * mm});
            skLineSegment(sketch, "E18.0.12.18", {"start": v(26.67, -64) * mm, "end": v(26.67, -69.09) * mm});
            skLineSegment(sketch, "E18.0.12.19", {"start": v(47.75, -64) * mm, "end": v(42.67, -64) * mm});
            skLineSegment(sketch, "E18.0.12.20", {"start": v(58.67, -69.09) * mm, "end": v(63.75, -69.09) * mm});
            skLineSegment(sketch, "E18.0.12.21", {"start": v(37.34, -69.09) * mm, "end": v(42.42, -69.09) * mm});
            skLineSegment(sketch, "E18.0.12.22", {"start": v(63.75, -69.09) * mm, "end": v(63.75, -64) * mm});
            skLineSegment(sketch, "E18.0.12.23", {"start": v(48, -69.09) * mm, "end": v(53.09, -69.09) * mm});
            skLineSegment(sketch, "E18.0.12.24", {"start": v(47.75, -69.09) * mm, "end": v(47.75, -64) * mm});
            skLineSegment(sketch, "E18.0.12.25", {"start": v(48, -64) * mm, "end": v(48, -69.09) * mm});
            skLineSegment(sketch, "E18.0.12.26", {"start": v(53.09, -64) * mm, "end": v(48, -64) * mm});
            skLineSegment(sketch, "E18.0.12.27", {"start": v(31.75, -69.09) * mm, "end": v(31.75, -64) * mm});
            skLineSegment(sketch, "E18.0.13.0", {"start": v(53.09, -74.42) * mm, "end": v(53.09, -69.34) * mm});
            skLineSegment(sketch, "E18.0.13.1", {"start": v(58.42, -74.42) * mm, "end": v(58.42, -69.34) * mm});
            skLineSegment(sketch, "E18.0.13.2", {"start": v(42.42, -74.42) * mm, "end": v(42.42, -69.34) * mm});
            skLineSegment(sketch, "E18.0.13.3", {"start": v(32, -69.34) * mm, "end": v(32, -74.42) * mm});
            skLineSegment(sketch, "E18.0.13.4", {"start": v(63.75, -69.34) * mm, "end": v(58.67, -69.34) * mm});
            skLineSegment(sketch, "E18.0.13.5", {"start": v(58.67, -69.34) * mm, "end": v(58.67, -74.42) * mm});
            skLineSegment(sketch, "E18.0.13.6", {"start": v(53.34, -74.42) * mm, "end": v(58.42, -74.42) * mm});
            skLineSegment(sketch, "E18.0.13.7", {"start": v(42.42, -69.34) * mm, "end": v(37.34, -69.34) * mm});
            skLineSegment(sketch, "E18.0.13.8", {"start": v(58.42, -69.34) * mm, "end": v(53.34, -69.34) * mm});
            skLineSegment(sketch, "E18.0.13.9", {"start": v(37.08, -74.42) * mm, "end": v(37.08, -69.34) * mm});
            skLineSegment(sketch, "E18.0.13.10", {"start": v(42.67, -69.34) * mm, "end": v(42.67, -74.42) * mm});
            skLineSegment(sketch, "E18.0.13.11", {"start": v(37.08, -69.34) * mm, "end": v(32, -69.34) * mm});
            skLineSegment(sketch, "E18.0.13.12", {"start": v(53.34, -69.34) * mm, "end": v(53.34, -74.42) * mm});
            skLineSegment(sketch, "E18.0.13.13", {"start": v(32, -74.42) * mm, "end": v(37.08, -74.42) * mm});
            skLineSegment(sketch, "E18.0.13.14", {"start": v(31.75, -69.34) * mm, "end": v(26.67, -69.34) * mm});
            skLineSegment(sketch, "E18.0.13.15", {"start": v(42.67, -74.42) * mm, "end": v(47.75, -74.42) * mm});
            skLineSegment(sketch, "E18.0.13.16", {"start": v(37.34, -69.34) * mm, "end": v(37.34, -74.42) * mm});
            skLineSegment(sketch, "E18.0.13.17", {"start": v(26.67, -74.42) * mm, "end": v(31.75, -74.42) * mm});
            skLineSegment(sketch, "E18.0.13.18", {"start": v(26.67, -69.34) * mm, "end": v(26.67, -74.42) * mm});
            skLineSegment(sketch, "E18.0.13.19", {"start": v(47.75, -69.34) * mm, "end": v(42.67, -69.34) * mm});
            skLineSegment(sketch, "E18.0.13.20", {"start": v(58.67, -74.42) * mm, "end": v(63.75, -74.42) * mm});
            skLineSegment(sketch, "E18.0.13.21", {"start": v(37.34, -74.42) * mm, "end": v(42.42, -74.42) * mm});
            skLineSegment(sketch, "E18.0.13.22", {"start": v(63.75, -74.42) * mm, "end": v(63.75, -69.34) * mm});
            skLineSegment(sketch, "E18.0.13.23", {"start": v(48, -74.42) * mm, "end": v(53.09, -74.42) * mm});
            skLineSegment(sketch, "E18.0.13.24", {"start": v(47.75, -74.42) * mm, "end": v(47.75, -69.34) * mm});
            skLineSegment(sketch, "E18.0.13.25", {"start": v(48, -69.34) * mm, "end": v(48, -74.42) * mm});
            skLineSegment(sketch, "E18.0.13.26", {"start": v(53.09, -69.34) * mm, "end": v(48, -69.34) * mm});
            skLineSegment(sketch, "E18.0.13.27", {"start": v(31.75, -74.42) * mm, "end": v(31.75, -69.34) * mm});
            skLineSegment(sketch, "E18.0.14.0", {"start": v(53.09, -79.76) * mm, "end": v(53.09, -74.68) * mm});
            skLineSegment(sketch, "E18.0.14.1", {"start": v(58.42, -79.76) * mm, "end": v(58.42, -74.68) * mm});
            skLineSegment(sketch, "E18.0.14.2", {"start": v(42.42, -79.76) * mm, "end": v(42.42, -74.68) * mm});
            skLineSegment(sketch, "E18.0.14.3", {"start": v(32, -74.68) * mm, "end": v(32, -79.76) * mm});
            skLineSegment(sketch, "E18.0.14.4", {"start": v(63.75, -74.68) * mm, "end": v(58.67, -74.68) * mm});
            skLineSegment(sketch, "E18.0.14.5", {"start": v(58.67, -74.68) * mm, "end": v(58.67, -79.76) * mm});
            skLineSegment(sketch, "E18.0.14.6", {"start": v(53.34, -79.76) * mm, "end": v(58.42, -79.76) * mm});
            skLineSegment(sketch, "E18.0.14.7", {"start": v(42.42, -74.68) * mm, "end": v(37.34, -74.68) * mm});
            skLineSegment(sketch, "E18.0.14.8", {"start": v(58.42, -74.68) * mm, "end": v(53.34, -74.68) * mm});
            skLineSegment(sketch, "E18.0.14.9", {"start": v(37.08, -79.76) * mm, "end": v(37.08, -74.68) * mm});
            skLineSegment(sketch, "E18.0.14.10", {"start": v(42.67, -74.68) * mm, "end": v(42.67, -79.76) * mm});
            skLineSegment(sketch, "E18.0.14.11", {"start": v(37.08, -74.68) * mm, "end": v(32, -74.68) * mm});
            skLineSegment(sketch, "E18.0.14.12", {"start": v(53.34, -74.68) * mm, "end": v(53.34, -79.76) * mm});
            skLineSegment(sketch, "E18.0.14.13", {"start": v(32, -79.76) * mm, "end": v(37.08, -79.76) * mm});
            skLineSegment(sketch, "E18.0.14.14", {"start": v(31.75, -74.68) * mm, "end": v(26.67, -74.68) * mm});
            skLineSegment(sketch, "E18.0.14.15", {"start": v(42.67, -79.76) * mm, "end": v(47.75, -79.76) * mm});
            skLineSegment(sketch, "E18.0.14.16", {"start": v(37.34, -74.68) * mm, "end": v(37.34, -79.76) * mm});
            skLineSegment(sketch, "E18.0.14.17", {"start": v(26.67, -79.76) * mm, "end": v(31.75, -79.76) * mm});
            skLineSegment(sketch, "E18.0.14.18", {"start": v(26.67, -74.68) * mm, "end": v(26.67, -79.76) * mm});
            skLineSegment(sketch, "E18.0.14.19", {"start": v(47.75, -74.68) * mm, "end": v(42.67, -74.68) * mm});
            skLineSegment(sketch, "E18.0.14.20", {"start": v(58.67, -79.76) * mm, "end": v(63.75, -79.76) * mm});
            skLineSegment(sketch, "E18.0.14.21", {"start": v(37.34, -79.76) * mm, "end": v(42.42, -79.76) * mm});
            skLineSegment(sketch, "E18.0.14.22", {"start": v(63.75, -79.76) * mm, "end": v(63.75, -74.68) * mm});
            skLineSegment(sketch, "E18.0.14.23", {"start": v(48, -79.76) * mm, "end": v(53.09, -79.76) * mm});
            skLineSegment(sketch, "E18.0.14.24", {"start": v(47.75, -79.76) * mm, "end": v(47.75, -74.68) * mm});
            skLineSegment(sketch, "E18.0.14.25", {"start": v(48, -74.68) * mm, "end": v(48, -79.76) * mm});
            skLineSegment(sketch, "E18.0.14.26", {"start": v(53.09, -74.68) * mm, "end": v(48, -74.68) * mm});
            skLineSegment(sketch, "E18.0.14.27", {"start": v(31.75, -79.76) * mm, "end": v(31.75, -74.68) * mm});
            skLineSegment(sketch, "E18.0.15.0", {"start": v(53.09, -85.1) * mm, "end": v(53.09, -80.01) * mm});
            skLineSegment(sketch, "E18.0.15.1", {"start": v(58.42, -85.1) * mm, "end": v(58.42, -80.01) * mm});
            skLineSegment(sketch, "E18.0.15.2", {"start": v(42.42, -85.1) * mm, "end": v(42.42, -80.01) * mm});
            skLineSegment(sketch, "E18.0.15.3", {"start": v(32, -80.01) * mm, "end": v(32, -85.1) * mm});
            skLineSegment(sketch, "E18.0.15.4", {"start": v(63.75, -80.01) * mm, "end": v(58.67, -80.01) * mm});
            skLineSegment(sketch, "E18.0.15.5", {"start": v(58.67, -80.01) * mm, "end": v(58.67, -85.1) * mm});
            skLineSegment(sketch, "E18.0.15.6", {"start": v(53.34, -85.1) * mm, "end": v(58.42, -85.1) * mm});
            skLineSegment(sketch, "E18.0.15.7", {"start": v(42.42, -80.01) * mm, "end": v(37.34, -80.01) * mm});
            skLineSegment(sketch, "E18.0.15.8", {"start": v(58.42, -80.01) * mm, "end": v(53.34, -80.01) * mm});
            skLineSegment(sketch, "E18.0.15.9", {"start": v(37.08, -85.1) * mm, "end": v(37.08, -80.01) * mm});
            skLineSegment(sketch, "E18.0.15.10", {"start": v(42.67, -80.01) * mm, "end": v(42.67, -85.1) * mm});
            skLineSegment(sketch, "E18.0.15.11", {"start": v(37.08, -80.01) * mm, "end": v(32, -80.01) * mm});
            skLineSegment(sketch, "E18.0.15.12", {"start": v(53.34, -80.01) * mm, "end": v(53.34, -85.1) * mm});
            skLineSegment(sketch, "E18.0.15.13", {"start": v(32, -85.1) * mm, "end": v(37.08, -85.1) * mm});
            skLineSegment(sketch, "E18.0.15.14", {"start": v(31.75, -80.01) * mm, "end": v(26.67, -80.01) * mm});
            skLineSegment(sketch, "E18.0.15.15", {"start": v(42.67, -85.1) * mm, "end": v(47.75, -85.1) * mm});
            skLineSegment(sketch, "E18.0.15.16", {"start": v(37.34, -80.01) * mm, "end": v(37.34, -85.1) * mm});
            skLineSegment(sketch, "E18.0.15.17", {"start": v(26.67, -85.1) * mm, "end": v(31.75, -85.1) * mm});
            skLineSegment(sketch, "E18.0.15.18", {"start": v(26.67, -80.01) * mm, "end": v(26.67, -85.1) * mm});
            skLineSegment(sketch, "E18.0.15.19", {"start": v(47.75, -80.01) * mm, "end": v(42.67, -80.01) * mm});
            skLineSegment(sketch, "E18.0.15.20", {"start": v(58.67, -85.1) * mm, "end": v(63.75, -85.1) * mm});
            skLineSegment(sketch, "E18.0.15.21", {"start": v(37.34, -85.1) * mm, "end": v(42.42, -85.1) * mm});
            skLineSegment(sketch, "E18.0.15.22", {"start": v(63.75, -85.1) * mm, "end": v(63.75, -80.01) * mm});
            skLineSegment(sketch, "E18.0.15.23", {"start": v(48, -85.1) * mm, "end": v(53.09, -85.1) * mm});
            skLineSegment(sketch, "E18.0.15.24", {"start": v(47.75, -85.1) * mm, "end": v(47.75, -80.01) * mm});
            skLineSegment(sketch, "E18.0.15.25", {"start": v(48, -80.01) * mm, "end": v(48, -85.1) * mm});
            skLineSegment(sketch, "E18.0.15.26", {"start": v(53.09, -80.01) * mm, "end": v(48, -80.01) * mm});
            skLineSegment(sketch, "E18.0.15.27", {"start": v(31.75, -85.1) * mm, "end": v(31.75, -80.01) * mm});
            skLineSegment(sketch, "E18.0.16.0", {"start": v(53.09, -90.42) * mm, "end": v(53.09, -85.34) * mm});
            skLineSegment(sketch, "E18.0.16.1", {"start": v(58.42, -90.42) * mm, "end": v(58.42, -85.34) * mm});
            skLineSegment(sketch, "E18.0.16.2", {"start": v(42.42, -90.42) * mm, "end": v(42.42, -85.34) * mm});
            skLineSegment(sketch, "E18.0.16.3", {"start": v(32, -85.34) * mm, "end": v(32, -90.42) * mm});
            skLineSegment(sketch, "E18.0.16.4", {"start": v(63.75, -85.34) * mm, "end": v(58.67, -85.34) * mm});
            skLineSegment(sketch, "E18.0.16.5", {"start": v(58.67, -85.34) * mm, "end": v(58.67, -90.42) * mm});
            skLineSegment(sketch, "E18.0.16.6", {"start": v(53.34, -90.42) * mm, "end": v(58.42, -90.42) * mm});
            skLineSegment(sketch, "E18.0.16.7", {"start": v(42.42, -85.34) * mm, "end": v(37.34, -85.34) * mm});
            skLineSegment(sketch, "E18.0.16.8", {"start": v(58.42, -85.34) * mm, "end": v(53.34, -85.34) * mm});
            skLineSegment(sketch, "E18.0.16.9", {"start": v(37.08, -90.42) * mm, "end": v(37.08, -85.34) * mm});
            skLineSegment(sketch, "E18.0.16.10", {"start": v(42.67, -85.34) * mm, "end": v(42.67, -90.42) * mm});
            skLineSegment(sketch, "E18.0.16.11", {"start": v(37.08, -85.34) * mm, "end": v(32, -85.34) * mm});
            skLineSegment(sketch, "E18.0.16.12", {"start": v(53.34, -85.34) * mm, "end": v(53.34, -90.42) * mm});
            skLineSegment(sketch, "E18.0.16.13", {"start": v(32, -90.42) * mm, "end": v(37.08, -90.42) * mm});
            skLineSegment(sketch, "E18.0.16.14", {"start": v(31.75, -85.34) * mm, "end": v(26.67, -85.34) * mm});
            skLineSegment(sketch, "E18.0.16.15", {"start": v(42.67, -90.42) * mm, "end": v(47.75, -90.42) * mm});
            skLineSegment(sketch, "E18.0.16.16", {"start": v(37.34, -85.34) * mm, "end": v(37.34, -90.42) * mm});
            skLineSegment(sketch, "E18.0.16.17", {"start": v(26.67, -90.42) * mm, "end": v(31.75, -90.42) * mm});
            skLineSegment(sketch, "E18.0.16.18", {"start": v(26.67, -85.34) * mm, "end": v(26.67, -90.42) * mm});
            skLineSegment(sketch, "E18.0.16.19", {"start": v(47.75, -85.34) * mm, "end": v(42.67, -85.34) * mm});
            skLineSegment(sketch, "E18.0.16.20", {"start": v(58.67, -90.42) * mm, "end": v(63.75, -90.42) * mm});
            skLineSegment(sketch, "E18.0.16.21", {"start": v(37.34, -90.42) * mm, "end": v(42.42, -90.42) * mm});
            skLineSegment(sketch, "E18.0.16.22", {"start": v(63.75, -90.42) * mm, "end": v(63.75, -85.34) * mm});
            skLineSegment(sketch, "E18.0.16.23", {"start": v(48, -90.42) * mm, "end": v(53.09, -90.42) * mm});
            skLineSegment(sketch, "E18.0.16.24", {"start": v(47.75, -90.42) * mm, "end": v(47.75, -85.34) * mm});
            skLineSegment(sketch, "E18.0.16.25", {"start": v(48, -85.34) * mm, "end": v(48, -90.42) * mm});
            skLineSegment(sketch, "E18.0.16.26", {"start": v(53.09, -85.34) * mm, "end": v(48, -85.34) * mm});
            skLineSegment(sketch, "E18.0.16.27", {"start": v(31.75, -90.42) * mm, "end": v(31.75, -85.34) * mm});
            skLineSegment(sketch, "E18.0.17.0", {"start": v(53.09, -95.76) * mm, "end": v(53.09, -90.68) * mm});
            skLineSegment(sketch, "E18.0.17.1", {"start": v(58.42, -95.76) * mm, "end": v(58.42, -90.68) * mm});
            skLineSegment(sketch, "E18.0.17.2", {"start": v(42.42, -95.76) * mm, "end": v(42.42, -90.68) * mm});
            skLineSegment(sketch, "E18.0.17.3", {"start": v(32, -90.68) * mm, "end": v(32, -95.76) * mm});
            skLineSegment(sketch, "E18.0.17.4", {"start": v(63.75, -90.68) * mm, "end": v(58.67, -90.68) * mm});
            skLineSegment(sketch, "E18.0.17.5", {"start": v(58.67, -90.68) * mm, "end": v(58.67, -95.76) * mm});
            skLineSegment(sketch, "E18.0.17.6", {"start": v(53.34, -95.76) * mm, "end": v(58.42, -95.76) * mm});
            skLineSegment(sketch, "E18.0.17.7", {"start": v(42.42, -90.68) * mm, "end": v(37.34, -90.68) * mm});
            skLineSegment(sketch, "E18.0.17.8", {"start": v(58.42, -90.68) * mm, "end": v(53.34, -90.68) * mm});
            skLineSegment(sketch, "E18.0.17.9", {"start": v(37.08, -95.76) * mm, "end": v(37.08, -90.68) * mm});
            skLineSegment(sketch, "E18.0.17.10", {"start": v(42.67, -90.68) * mm, "end": v(42.67, -95.76) * mm});
            skLineSegment(sketch, "E18.0.17.11", {"start": v(37.08, -90.68) * mm, "end": v(32, -90.68) * mm});
            skLineSegment(sketch, "E18.0.17.12", {"start": v(53.34, -90.68) * mm, "end": v(53.34, -95.76) * mm});
            skLineSegment(sketch, "E18.0.17.13", {"start": v(32, -95.76) * mm, "end": v(37.08, -95.76) * mm});
            skLineSegment(sketch, "E18.0.17.14", {"start": v(31.75, -90.68) * mm, "end": v(26.67, -90.68) * mm});
            skLineSegment(sketch, "E18.0.17.15", {"start": v(42.67, -95.76) * mm, "end": v(47.75, -95.76) * mm});
            skLineSegment(sketch, "E18.0.17.16", {"start": v(37.34, -90.68) * mm, "end": v(37.34, -95.76) * mm});
            skLineSegment(sketch, "E18.0.17.17", {"start": v(26.67, -95.76) * mm, "end": v(31.75, -95.76) * mm});
            skLineSegment(sketch, "E18.0.17.18", {"start": v(26.67, -90.68) * mm, "end": v(26.67, -95.76) * mm});
            skLineSegment(sketch, "E18.0.17.19", {"start": v(47.75, -90.68) * mm, "end": v(42.67, -90.68) * mm});
            skLineSegment(sketch, "E18.0.17.20", {"start": v(58.67, -95.76) * mm, "end": v(63.75, -95.76) * mm});
            skLineSegment(sketch, "E18.0.17.21", {"start": v(37.34, -95.76) * mm, "end": v(42.42, -95.76) * mm});
            skLineSegment(sketch, "E18.0.17.22", {"start": v(63.75, -95.76) * mm, "end": v(63.75, -90.68) * mm});
            skLineSegment(sketch, "E18.0.17.23", {"start": v(48, -95.76) * mm, "end": v(53.09, -95.76) * mm});
            skLineSegment(sketch, "E18.0.17.24", {"start": v(47.75, -95.76) * mm, "end": v(47.75, -90.68) * mm});
            skLineSegment(sketch, "E18.0.17.25", {"start": v(48, -90.68) * mm, "end": v(48, -95.76) * mm});
            skLineSegment(sketch, "E18.0.17.26", {"start": v(53.09, -90.68) * mm, "end": v(48, -90.68) * mm});
            skLineSegment(sketch, "E18.0.17.27", {"start": v(31.75, -95.76) * mm, "end": v(31.75, -90.68) * mm});
            skLineSegment(sketch, "E18.0.18.0", {"start": v(53.09, -101.1) * mm, "end": v(53.09, -96.01) * mm});
            skLineSegment(sketch, "E18.0.18.1", {"start": v(58.42, -101.1) * mm, "end": v(58.42, -96.01) * mm});
            skLineSegment(sketch, "E18.0.18.2", {"start": v(42.42, -101.1) * mm, "end": v(42.42, -96.01) * mm});
            skLineSegment(sketch, "E18.0.18.3", {"start": v(32, -96.01) * mm, "end": v(32, -101.1) * mm});
            skLineSegment(sketch, "E18.0.18.4", {"start": v(63.75, -96.01) * mm, "end": v(58.67, -96.01) * mm});
            skLineSegment(sketch, "E18.0.18.5", {"start": v(58.67, -96.01) * mm, "end": v(58.67, -101.1) * mm});
            skLineSegment(sketch, "E18.0.18.6", {"start": v(53.34, -101.1) * mm, "end": v(58.42, -101.1) * mm});
            skLineSegment(sketch, "E18.0.18.7", {"start": v(42.42, -96.01) * mm, "end": v(37.34, -96.01) * mm});
            skLineSegment(sketch, "E18.0.18.8", {"start": v(58.42, -96.01) * mm, "end": v(53.34, -96.01) * mm});
            skLineSegment(sketch, "E18.0.18.9", {"start": v(37.08, -101.1) * mm, "end": v(37.08, -96.01) * mm});
            skLineSegment(sketch, "E18.0.18.10", {"start": v(42.67, -96.01) * mm, "end": v(42.67, -101.1) * mm});
            skLineSegment(sketch, "E18.0.18.11", {"start": v(37.08, -96.01) * mm, "end": v(32, -96.01) * mm});
            skLineSegment(sketch, "E18.0.18.12", {"start": v(53.34, -96.01) * mm, "end": v(53.34, -101.1) * mm});
            skLineSegment(sketch, "E18.0.18.13", {"start": v(32, -101.1) * mm, "end": v(37.08, -101.1) * mm});
            skLineSegment(sketch, "E18.0.18.14", {"start": v(31.75, -96.01) * mm, "end": v(26.67, -96.01) * mm});
            skLineSegment(sketch, "E18.0.18.15", {"start": v(42.67, -101.1) * mm, "end": v(47.75, -101.1) * mm});
            skLineSegment(sketch, "E18.0.18.16", {"start": v(37.34, -96.01) * mm, "end": v(37.34, -101.1) * mm});
            skLineSegment(sketch, "E18.0.18.17", {"start": v(26.67, -101.1) * mm, "end": v(31.75, -101.1) * mm});
            skLineSegment(sketch, "E18.0.18.18", {"start": v(26.67, -96.01) * mm, "end": v(26.67, -101.1) * mm});
            skLineSegment(sketch, "E18.0.18.19", {"start": v(47.75, -96.01) * mm, "end": v(42.67, -96.01) * mm});
            skLineSegment(sketch, "E18.0.18.20", {"start": v(58.67, -101.1) * mm, "end": v(63.75, -101.1) * mm});
            skLineSegment(sketch, "E18.0.18.21", {"start": v(37.34, -101.1) * mm, "end": v(42.42, -101.1) * mm});
            skLineSegment(sketch, "E18.0.18.22", {"start": v(63.75, -101.1) * mm, "end": v(63.75, -96.01) * mm});
            skLineSegment(sketch, "E18.0.18.23", {"start": v(48, -101.1) * mm, "end": v(53.09, -101.1) * mm});
            skLineSegment(sketch, "E18.0.18.24", {"start": v(47.75, -101.1) * mm, "end": v(47.75, -96.01) * mm});
            skLineSegment(sketch, "E18.0.18.25", {"start": v(48, -96.01) * mm, "end": v(48, -101.1) * mm});
            skLineSegment(sketch, "E18.0.18.26", {"start": v(53.09, -96.01) * mm, "end": v(48, -96.01) * mm});
            skLineSegment(sketch, "E18.0.18.27", {"start": v(31.75, -101.1) * mm, "end": v(31.75, -96.01) * mm});
            skLineSegment(sketch, "E18.0.19.0", {"start": v(53.09, -106.43) * mm, "end": v(53.09, -101.35) * mm});
            skLineSegment(sketch, "E18.0.19.1", {"start": v(58.42, -106.43) * mm, "end": v(58.42, -101.35) * mm});
            skLineSegment(sketch, "E18.0.19.2", {"start": v(42.42, -106.43) * mm, "end": v(42.42, -101.35) * mm});
            skLineSegment(sketch, "E18.0.19.3", {"start": v(32, -101.35) * mm, "end": v(32, -106.43) * mm});
            skLineSegment(sketch, "E18.0.19.4", {"start": v(63.75, -101.35) * mm, "end": v(58.67, -101.35) * mm});
            skLineSegment(sketch, "E18.0.19.5", {"start": v(58.67, -101.35) * mm, "end": v(58.67, -106.43) * mm});
            skLineSegment(sketch, "E18.0.19.6", {"start": v(53.34, -106.43) * mm, "end": v(58.42, -106.43) * mm});
            skLineSegment(sketch, "E18.0.19.7", {"start": v(42.42, -101.35) * mm, "end": v(37.34, -101.35) * mm});
            skLineSegment(sketch, "E18.0.19.8", {"start": v(58.42, -101.35) * mm, "end": v(53.34, -101.35) * mm});
            skLineSegment(sketch, "E18.0.19.9", {"start": v(37.08, -106.43) * mm, "end": v(37.08, -101.35) * mm});
            skLineSegment(sketch, "E18.0.19.10", {"start": v(42.67, -101.35) * mm, "end": v(42.67, -106.43) * mm});
            skLineSegment(sketch, "E18.0.19.11", {"start": v(37.08, -101.35) * mm, "end": v(32, -101.35) * mm});
            skLineSegment(sketch, "E18.0.19.12", {"start": v(53.34, -101.35) * mm, "end": v(53.34, -106.43) * mm});
            skLineSegment(sketch, "E18.0.19.13", {"start": v(32, -106.43) * mm, "end": v(37.08, -106.43) * mm});
            skLineSegment(sketch, "E18.0.19.14", {"start": v(31.75, -101.35) * mm, "end": v(26.67, -101.35) * mm});
            skLineSegment(sketch, "E18.0.19.15", {"start": v(42.67, -106.43) * mm, "end": v(47.75, -106.43) * mm});
            skLineSegment(sketch, "E18.0.19.16", {"start": v(37.34, -101.35) * mm, "end": v(37.34, -106.43) * mm});
            skLineSegment(sketch, "E18.0.19.17", {"start": v(26.67, -106.43) * mm, "end": v(31.75, -106.43) * mm});
            skLineSegment(sketch, "E18.0.19.18", {"start": v(26.67, -101.35) * mm, "end": v(26.67, -106.43) * mm});
            skLineSegment(sketch, "E18.0.19.19", {"start": v(47.75, -101.35) * mm, "end": v(42.67, -101.35) * mm});
            skLineSegment(sketch, "E18.0.19.20", {"start": v(58.67, -106.43) * mm, "end": v(63.75, -106.43) * mm});
            skLineSegment(sketch, "E18.0.19.21", {"start": v(37.34, -106.43) * mm, "end": v(42.42, -106.43) * mm});
            skLineSegment(sketch, "E18.0.19.22", {"start": v(63.75, -106.43) * mm, "end": v(63.75, -101.35) * mm});
            skLineSegment(sketch, "E18.0.19.23", {"start": v(48, -106.43) * mm, "end": v(53.09, -106.43) * mm});
            skLineSegment(sketch, "E18.0.19.24", {"start": v(47.75, -106.43) * mm, "end": v(47.75, -101.35) * mm});
            skLineSegment(sketch, "E18.0.19.25", {"start": v(48, -101.35) * mm, "end": v(48, -106.43) * mm});
            skLineSegment(sketch, "E18.0.19.26", {"start": v(53.09, -101.35) * mm, "end": v(48, -101.35) * mm});
            skLineSegment(sketch, "E18.0.19.27", {"start": v(31.75, -106.43) * mm, "end": v(31.75, -101.35) * mm});
            skLineSegment(sketch, "E18.0.20.0", {"start": v(53.09, -111.76) * mm, "end": v(53.09, -106.68) * mm});
            skLineSegment(sketch, "E18.0.20.1", {"start": v(58.42, -111.76) * mm, "end": v(58.42, -106.68) * mm});
            skLineSegment(sketch, "E18.0.20.2", {"start": v(42.42, -111.76) * mm, "end": v(42.42, -106.68) * mm});
            skLineSegment(sketch, "E18.0.20.3", {"start": v(32, -106.68) * mm, "end": v(32, -111.76) * mm});
            skLineSegment(sketch, "E18.0.20.4", {"start": v(63.75, -106.68) * mm, "end": v(58.67, -106.68) * mm});
            skLineSegment(sketch, "E18.0.20.5", {"start": v(58.67, -106.68) * mm, "end": v(58.67, -111.76) * mm});
            skLineSegment(sketch, "E18.0.20.6", {"start": v(53.34, -111.76) * mm, "end": v(58.42, -111.76) * mm});
            skLineSegment(sketch, "E18.0.20.7", {"start": v(42.42, -106.68) * mm, "end": v(37.34, -106.68) * mm});
            skLineSegment(sketch, "E18.0.20.8", {"start": v(58.42, -106.68) * mm, "end": v(53.34, -106.68) * mm});
            skLineSegment(sketch, "E18.0.20.9", {"start": v(37.08, -111.76) * mm, "end": v(37.08, -106.68) * mm});
            skLineSegment(sketch, "E18.0.20.10", {"start": v(42.67, -106.68) * mm, "end": v(42.67, -111.76) * mm});
            skLineSegment(sketch, "E18.0.20.11", {"start": v(37.08, -106.68) * mm, "end": v(32, -106.68) * mm});
            skLineSegment(sketch, "E18.0.20.12", {"start": v(53.34, -106.68) * mm, "end": v(53.34, -111.76) * mm});
            skLineSegment(sketch, "E18.0.20.13", {"start": v(32, -111.76) * mm, "end": v(37.08, -111.76) * mm});
            skLineSegment(sketch, "E18.0.20.14", {"start": v(31.75, -106.68) * mm, "end": v(26.67, -106.68) * mm});
            skLineSegment(sketch, "E18.0.20.15", {"start": v(42.67, -111.76) * mm, "end": v(47.75, -111.76) * mm});
            skLineSegment(sketch, "E18.0.20.16", {"start": v(37.34, -106.68) * mm, "end": v(37.34, -111.76) * mm});
            skLineSegment(sketch, "E18.0.20.17", {"start": v(26.67, -111.76) * mm, "end": v(31.75, -111.76) * mm});
            skLineSegment(sketch, "E18.0.20.18", {"start": v(26.67, -106.68) * mm, "end": v(26.67, -111.76) * mm});
            skLineSegment(sketch, "E18.0.20.19", {"start": v(47.75, -106.68) * mm, "end": v(42.67, -106.68) * mm});
            skLineSegment(sketch, "E18.0.20.20", {"start": v(58.67, -111.76) * mm, "end": v(63.75, -111.76) * mm});
            skLineSegment(sketch, "E18.0.20.21", {"start": v(37.34, -111.76) * mm, "end": v(42.42, -111.76) * mm});
            skLineSegment(sketch, "E18.0.20.22", {"start": v(63.75, -111.76) * mm, "end": v(63.75, -106.68) * mm});
            skLineSegment(sketch, "E18.0.20.23", {"start": v(48, -111.76) * mm, "end": v(53.09, -111.76) * mm});
            skLineSegment(sketch, "E18.0.20.24", {"start": v(47.75, -111.76) * mm, "end": v(47.75, -106.68) * mm});
            skLineSegment(sketch, "E18.0.20.25", {"start": v(48, -106.68) * mm, "end": v(48, -111.76) * mm});
            skLineSegment(sketch, "E18.0.20.26", {"start": v(53.09, -106.68) * mm, "end": v(48, -106.68) * mm});
            skLineSegment(sketch, "E18.0.20.27", {"start": v(31.75, -111.76) * mm, "end": v(31.75, -106.68) * mm});
            skLineSegment(sketch, "E18.direction1", {"start": v(26.67, -5.08) * mm, "end": v(52.07, -5.08) * mm, "construction": true});
            skLineSegment(sketch, "E18.direction2", {"start": v(26.67, -5.08) * mm, "end": v(26.67, -10.41) * mm, "construction": true});
            skSolve(sketch);
        }
        {
            var Q0;
            Q0=qCreatedBy(makeId("Top.planeOp"),FACE);
            var sketch = newSketch(context, id + "F5", { "sketchPlane" : qUnion([Q0])});
            skLineSegment(sketch, "E19.0.0", {"start": v(69.09, -5.08) * mm, "end": v(69.09, 0) * mm});
            skLineSegment(sketch, "E19.0.1", {"start": v(69.09, 0) * mm, "end": v(64, 0) * mm});
            skLineSegment(sketch, "E19.0.2", {"start": v(64, 0) * mm, "end": v(64, -5.08) * mm});
            skLineSegment(sketch, "E19.0.3", {"start": v(64, -5.08) * mm, "end": v(69.09, -5.08) * mm});
            skLineSegment(sketch, "E20.0.1.0", {"start": v(69.09, -5.33) * mm, "end": v(64, -5.33) * mm});
            skLineSegment(sketch, "E20.0.1.1", {"start": v(64, -10.41) * mm, "end": v(69.09, -10.41) * mm});
            skLineSegment(sketch, "E20.0.1.2", {"start": v(64, -5.33) * mm, "end": v(64, -10.41) * mm});
            skLineSegment(sketch, "E20.0.1.3", {"start": v(69.09, -10.41) * mm, "end": v(69.09, -5.33) * mm});
            skLineSegment(sketch, "E20.0.2.0", {"start": v(69.09, -10.67) * mm, "end": v(64, -10.67) * mm});
            skLineSegment(sketch, "E20.0.2.1", {"start": v(64, -15.75) * mm, "end": v(69.09, -15.75) * mm});
            skLineSegment(sketch, "E20.0.2.2", {"start": v(64, -10.67) * mm, "end": v(64, -15.75) * mm});
            skLineSegment(sketch, "E20.0.2.3", {"start": v(69.09, -15.75) * mm, "end": v(69.09, -10.67) * mm});
            skLineSegment(sketch, "E20.0.3.0", {"start": v(69.09, -16) * mm, "end": v(64, -16) * mm});
            skLineSegment(sketch, "E20.0.3.1", {"start": v(64, -21.08) * mm, "end": v(69.09, -21.08) * mm});
            skLineSegment(sketch, "E20.0.3.2", {"start": v(64, -16) * mm, "end": v(64, -21.08) * mm});
            skLineSegment(sketch, "E20.0.3.3", {"start": v(69.09, -21.08) * mm, "end": v(69.09, -16) * mm});
            skLineSegment(sketch, "E20.0.4.0", {"start": v(69.09, -21.34) * mm, "end": v(64, -21.34) * mm});
            skLineSegment(sketch, "E20.0.4.1", {"start": v(64, -26.42) * mm, "end": v(69.09, -26.42) * mm});
            skLineSegment(sketch, "E20.0.4.2", {"start": v(64, -21.34) * mm, "end": v(64, -26.42) * mm});
            skLineSegment(sketch, "E20.0.4.3", {"start": v(69.09, -26.42) * mm, "end": v(69.09, -21.34) * mm});
            skLineSegment(sketch, "E20.0.5.0", {"start": v(69.09, -26.67) * mm, "end": v(64, -26.67) * mm});
            skLineSegment(sketch, "E20.0.5.1", {"start": v(64, -31.75) * mm, "end": v(69.09, -31.75) * mm});
            skLineSegment(sketch, "E20.0.5.2", {"start": v(64, -26.67) * mm, "end": v(64, -31.75) * mm});
            skLineSegment(sketch, "E20.0.5.3", {"start": v(69.09, -31.75) * mm, "end": v(69.09, -26.67) * mm});
            skLineSegment(sketch, "E20.0.6.0", {"start": v(69.09, -32) * mm, "end": v(64, -32) * mm});
            skLineSegment(sketch, "E20.0.6.1", {"start": v(64, -37.08) * mm, "end": v(69.09, -37.08) * mm});
            skLineSegment(sketch, "E20.0.6.2", {"start": v(64, -32) * mm, "end": v(64, -37.08) * mm});
            skLineSegment(sketch, "E20.0.6.3", {"start": v(69.09, -37.08) * mm, "end": v(69.09, -32) * mm});
            skLineSegment(sketch, "E20.0.7.0", {"start": v(69.09, -37.34) * mm, "end": v(64, -37.34) * mm});
            skLineSegment(sketch, "E20.0.7.1", {"start": v(64, -42.42) * mm, "end": v(69.09, -42.42) * mm});
            skLineSegment(sketch, "E20.0.7.2", {"start": v(64, -37.34) * mm, "end": v(64, -42.42) * mm});
            skLineSegment(sketch, "E20.0.7.3", {"start": v(69.09, -42.42) * mm, "end": v(69.09, -37.34) * mm});
            skLineSegment(sketch, "E20.0.8.0", {"start": v(69.09, -42.67) * mm, "end": v(64, -42.67) * mm});
            skLineSegment(sketch, "E20.0.8.1", {"start": v(64, -47.75) * mm, "end": v(69.09, -47.75) * mm});
            skLineSegment(sketch, "E20.0.8.2", {"start": v(64, -42.67) * mm, "end": v(64, -47.75) * mm});
            skLineSegment(sketch, "E20.0.8.3", {"start": v(69.09, -47.75) * mm, "end": v(69.09, -42.67) * mm});
            skLineSegment(sketch, "E20.0.9.0", {"start": v(69.09, -48) * mm, "end": v(64, -48) * mm});
            skLineSegment(sketch, "E20.0.9.1", {"start": v(64, -53.09) * mm, "end": v(69.09, -53.09) * mm});
            skLineSegment(sketch, "E20.0.9.2", {"start": v(64, -48) * mm, "end": v(64, -53.09) * mm});
            skLineSegment(sketch, "E20.0.9.3", {"start": v(69.09, -53.09) * mm, "end": v(69.09, -48) * mm});
            skLineSegment(sketch, "E20.0.10.0", {"start": v(69.09, -53.34) * mm, "end": v(64, -53.34) * mm});
            skLineSegment(sketch, "E20.0.10.1", {"start": v(64, -58.42) * mm, "end": v(69.09, -58.42) * mm});
            skLineSegment(sketch, "E20.0.10.2", {"start": v(64, -53.34) * mm, "end": v(64, -58.42) * mm});
            skLineSegment(sketch, "E20.0.10.3", {"start": v(69.09, -58.42) * mm, "end": v(69.09, -53.34) * mm});
            skLineSegment(sketch, "E20.0.11.0", {"start": v(69.09, -58.67) * mm, "end": v(64, -58.67) * mm});
            skLineSegment(sketch, "E20.0.11.1", {"start": v(64, -63.75) * mm, "end": v(69.09, -63.75) * mm});
            skLineSegment(sketch, "E20.0.11.2", {"start": v(64, -58.67) * mm, "end": v(64, -63.75) * mm});
            skLineSegment(sketch, "E20.0.11.3", {"start": v(69.09, -63.75) * mm, "end": v(69.09, -58.67) * mm});
            skLineSegment(sketch, "E20.0.12.0", {"start": v(69.09, -64) * mm, "end": v(64, -64) * mm});
            skLineSegment(sketch, "E20.0.12.1", {"start": v(64, -69.09) * mm, "end": v(69.09, -69.09) * mm});
            skLineSegment(sketch, "E20.0.12.2", {"start": v(64, -64) * mm, "end": v(64, -69.09) * mm});
            skLineSegment(sketch, "E20.0.12.3", {"start": v(69.09, -69.09) * mm, "end": v(69.09, -64) * mm});
            skLineSegment(sketch, "E20.0.13.0", {"start": v(69.09, -69.34) * mm, "end": v(64, -69.34) * mm});
            skLineSegment(sketch, "E20.0.13.1", {"start": v(64, -74.42) * mm, "end": v(69.09, -74.42) * mm});
            skLineSegment(sketch, "E20.0.13.2", {"start": v(64, -69.34) * mm, "end": v(64, -74.42) * mm});
            skLineSegment(sketch, "E20.0.13.3", {"start": v(69.09, -74.42) * mm, "end": v(69.09, -69.34) * mm});
            skLineSegment(sketch, "E20.0.14.0", {"start": v(69.09, -74.68) * mm, "end": v(64, -74.68) * mm});
            skLineSegment(sketch, "E20.0.14.1", {"start": v(64, -79.76) * mm, "end": v(69.09, -79.76) * mm});
            skLineSegment(sketch, "E20.0.14.2", {"start": v(64, -74.68) * mm, "end": v(64, -79.76) * mm});
            skLineSegment(sketch, "E20.0.14.3", {"start": v(69.09, -79.76) * mm, "end": v(69.09, -74.68) * mm});
            skLineSegment(sketch, "E20.0.15.0", {"start": v(69.09, -80.01) * mm, "end": v(64, -80.01) * mm});
            skLineSegment(sketch, "E20.0.15.1", {"start": v(64, -85.1) * mm, "end": v(69.09, -85.1) * mm});
            skLineSegment(sketch, "E20.0.15.2", {"start": v(64, -80.01) * mm, "end": v(64, -85.1) * mm});
            skLineSegment(sketch, "E20.0.15.3", {"start": v(69.09, -85.1) * mm, "end": v(69.09, -80.01) * mm});
            skLineSegment(sketch, "E20.0.16.0", {"start": v(69.09, -85.34) * mm, "end": v(64, -85.34) * mm});
            skLineSegment(sketch, "E20.0.16.1", {"start": v(64, -90.42) * mm, "end": v(69.09, -90.42) * mm});
            skLineSegment(sketch, "E20.0.16.2", {"start": v(64, -85.34) * mm, "end": v(64, -90.42) * mm});
            skLineSegment(sketch, "E20.0.16.3", {"start": v(69.09, -90.42) * mm, "end": v(69.09, -85.34) * mm});
            skLineSegment(sketch, "E20.0.17.0", {"start": v(69.09, -90.68) * mm, "end": v(64, -90.68) * mm});
            skLineSegment(sketch, "E20.0.17.1", {"start": v(64, -95.76) * mm, "end": v(69.09, -95.76) * mm});
            skLineSegment(sketch, "E20.0.17.2", {"start": v(64, -90.68) * mm, "end": v(64, -95.76) * mm});
            skLineSegment(sketch, "E20.0.17.3", {"start": v(69.09, -95.76) * mm, "end": v(69.09, -90.68) * mm});
            skLineSegment(sketch, "E20.0.18.0", {"start": v(69.09, -96.01) * mm, "end": v(64, -96.01) * mm});
            skLineSegment(sketch, "E20.0.18.1", {"start": v(64, -101.1) * mm, "end": v(69.09, -101.1) * mm});
            skLineSegment(sketch, "E20.0.18.2", {"start": v(64, -96.01) * mm, "end": v(64, -101.1) * mm});
            skLineSegment(sketch, "E20.0.18.3", {"start": v(69.09, -101.1) * mm, "end": v(69.09, -96.01) * mm});
            skLineSegment(sketch, "E20.0.19.0", {"start": v(69.09, -101.35) * mm, "end": v(64, -101.35) * mm});
            skLineSegment(sketch, "E20.0.19.1", {"start": v(64, -106.43) * mm, "end": v(69.09, -106.43) * mm});
            skLineSegment(sketch, "E20.0.19.2", {"start": v(64, -101.35) * mm, "end": v(64, -106.43) * mm});
            skLineSegment(sketch, "E20.0.19.3", {"start": v(69.09, -106.43) * mm, "end": v(69.09, -101.35) * mm});
            skLineSegment(sketch, "E20.0.20.0", {"start": v(69.09, -106.68) * mm, "end": v(64, -106.68) * mm});
            skLineSegment(sketch, "E20.0.20.1", {"start": v(64, -111.76) * mm, "end": v(69.09, -111.76) * mm});
            skLineSegment(sketch, "E20.0.20.2", {"start": v(64, -106.68) * mm, "end": v(64, -111.76) * mm});
            skLineSegment(sketch, "E20.0.20.3", {"start": v(69.09, -111.76) * mm, "end": v(69.09, -106.68) * mm});
            skLineSegment(sketch, "E20.0.21.0", {"start": v(69.09, -112.01) * mm, "end": v(64, -112.01) * mm});
            skLineSegment(sketch, "E20.0.21.1", {"start": v(64, -117.1) * mm, "end": v(69.09, -117.1) * mm});
            skLineSegment(sketch, "E20.0.21.2", {"start": v(64, -112.01) * mm, "end": v(64, -117.1) * mm});
            skLineSegment(sketch, "E20.0.21.3", {"start": v(69.09, -117.1) * mm, "end": v(69.09, -112.01) * mm});
            skLineSegment(sketch, "E20.0.22.0", {"start": v(69.09, -117.35) * mm, "end": v(64, -117.35) * mm});
            skLineSegment(sketch, "E20.0.22.1", {"start": v(64, -122.43) * mm, "end": v(69.09, -122.43) * mm});
            skLineSegment(sketch, "E20.0.22.2", {"start": v(64, -117.35) * mm, "end": v(64, -122.43) * mm});
            skLineSegment(sketch, "E20.0.22.3", {"start": v(69.09, -122.43) * mm, "end": v(69.09, -117.35) * mm});
            skLineSegment(sketch, "E20.0.23.0", {"start": v(69.09, -122.68) * mm, "end": v(64, -122.68) * mm});
            skLineSegment(sketch, "E20.0.23.1", {"start": v(64, -127.76) * mm, "end": v(69.09, -127.76) * mm});
            skLineSegment(sketch, "E20.0.23.2", {"start": v(64, -122.68) * mm, "end": v(64, -127.76) * mm});
            skLineSegment(sketch, "E20.0.23.3", {"start": v(69.09, -127.76) * mm, "end": v(69.09, -122.68) * mm});
            skLineSegment(sketch, "E20.0.24.0", {"start": v(69.09, -128.02) * mm, "end": v(64, -128.02) * mm});
            skLineSegment(sketch, "E20.0.24.1", {"start": v(64, -133.1) * mm, "end": v(69.09, -133.1) * mm});
            skLineSegment(sketch, "E20.0.24.2", {"start": v(64, -128.02) * mm, "end": v(64, -133.1) * mm});
            skLineSegment(sketch, "E20.0.24.3", {"start": v(69.09, -133.1) * mm, "end": v(69.09, -128.02) * mm});
            skLineSegment(sketch, "E20.direction1", {"start": v(64, -5.08) * mm, "end": v(89.4, -5.08) * mm, "construction": true});
            skLineSegment(sketch, "E20.direction2", {"start": v(64, -5.08) * mm, "end": v(64, -10.41) * mm, "construction": true});
            skSolve(sketch);
        }
        {
            var Q0;
            Q0=qCreatedBy(makeId("Top.planeOp"),FACE);
            var sketch = newSketch(context, id + "F6", { "sketchPlane" : qUnion([Q0])});
            skLineSegment(sketch, "E21.0.0", {"start": v(74.42, -5.08) * mm, "end": v(74.42, 0) * mm});
            skLineSegment(sketch, "E21.0.1", {"start": v(74.42, 0) * mm, "end": v(69.34, 0) * mm});
            skLineSegment(sketch, "E21.0.2", {"start": v(69.34, 0) * mm, "end": v(69.34, -5.08) * mm});
            skLineSegment(sketch, "E21.0.3", {"start": v(69.34, -5.08) * mm, "end": v(74.42, -5.08) * mm});
            skLineSegment(sketch, "E21.1.0", {"start": v(79.76, -5.08) * mm, "end": v(79.76, 0) * mm});
            skLineSegment(sketch, "E21.1.1", {"start": v(79.76, 0) * mm, "end": v(74.68, 0) * mm});
            skLineSegment(sketch, "E21.1.2", {"start": v(74.68, 0) * mm, "end": v(74.68, -5.08) * mm});
            skLineSegment(sketch, "E21.1.3", {"start": v(74.68, -5.08) * mm, "end": v(79.76, -5.08) * mm});
            skLineSegment(sketch, "E21.2.0", {"start": v(85.1, -5.08) * mm, "end": v(85.1, 0) * mm});
            skLineSegment(sketch, "E21.2.1", {"start": v(85.1, 0) * mm, "end": v(80, 0) * mm});
            skLineSegment(sketch, "E21.2.2", {"start": v(80, 0) * mm, "end": v(80, -5.08) * mm});
            skLineSegment(sketch, "E21.2.3", {"start": v(80, -5.08) * mm, "end": v(85.1, -5.08) * mm});
            skLineSegment(sketch, "E21.3.0", {"start": v(90.42, -5.08) * mm, "end": v(90.42, 0) * mm});
            skLineSegment(sketch, "E21.3.1", {"start": v(90.42, 0) * mm, "end": v(85.34, 0) * mm});
            skLineSegment(sketch, "E21.3.2", {"start": v(85.34, 0) * mm, "end": v(85.34, -5.08) * mm});
            skLineSegment(sketch, "E21.3.3", {"start": v(85.34, -5.08) * mm, "end": v(90.42, -5.08) * mm});
            skLineSegment(sketch, "E21.4.0", {"start": v(95.76, -5.08) * mm, "end": v(95.76, 0) * mm});
            skLineSegment(sketch, "E21.4.1", {"start": v(95.76, 0) * mm, "end": v(90.68, 0) * mm});
            skLineSegment(sketch, "E21.4.2", {"start": v(90.68, 0) * mm, "end": v(90.68, -5.08) * mm});
            skLineSegment(sketch, "E21.4.3", {"start": v(90.68, -5.08) * mm, "end": v(95.76, -5.08) * mm});
            skLineSegment(sketch, "E21.5.0", {"start": v(101.1, -5.08) * mm, "end": v(101.1, 0) * mm});
            skLineSegment(sketch, "E21.5.1", {"start": v(101.1, 0) * mm, "end": v(96.01, 0) * mm});
            skLineSegment(sketch, "E21.5.2", {"start": v(96.01, 0) * mm, "end": v(96.01, -5.08) * mm});
            skLineSegment(sketch, "E21.5.3", {"start": v(96.01, -5.08) * mm, "end": v(101.1, -5.08) * mm});
            skLineSegment(sketch, "E21.6.0", {"start": v(106.43, -5.08) * mm, "end": v(106.43, 0) * mm});
            skLineSegment(sketch, "E21.6.1", {"start": v(106.43, 0) * mm, "end": v(101.35, 0) * mm});
            skLineSegment(sketch, "E21.6.2", {"start": v(101.35, 0) * mm, "end": v(101.35, -5.08) * mm});
            skLineSegment(sketch, "E21.6.3", {"start": v(101.35, -5.08) * mm, "end": v(106.43, -5.08) * mm});
            skLineSegment(sketch, "E22.0.1.0", {"start": v(74.42, -5.33) * mm, "end": v(69.34, -5.33) * mm});
            skLineSegment(sketch, "E22.0.1.1", {"start": v(95.76, -5.33) * mm, "end": v(90.68, -5.33) * mm});
            skLineSegment(sketch, "E22.0.1.2", {"start": v(69.34, -5.33) * mm, "end": v(69.34, -10.41) * mm});
            skLineSegment(sketch, "E22.0.1.3", {"start": v(69.34, -10.41) * mm, "end": v(74.42, -10.41) * mm});
            skLineSegment(sketch, "E22.0.1.4", {"start": v(79.76, -10.41) * mm, "end": v(79.76, -5.33) * mm});
            skLineSegment(sketch, "E22.0.1.5", {"start": v(101.35, -10.41) * mm, "end": v(106.43, -10.41) * mm});
            skLineSegment(sketch, "E22.0.1.6", {"start": v(79.76, -5.33) * mm, "end": v(74.68, -5.33) * mm});
            skLineSegment(sketch, "E22.0.1.7", {"start": v(101.35, -5.33) * mm, "end": v(101.35, -10.41) * mm});
            skLineSegment(sketch, "E22.0.1.8", {"start": v(106.43, -5.33) * mm, "end": v(101.35, -5.33) * mm});
            skLineSegment(sketch, "E22.0.1.9", {"start": v(106.43, -10.41) * mm, "end": v(106.43, -5.33) * mm});
            skLineSegment(sketch, "E22.0.1.10", {"start": v(74.68, -10.41) * mm, "end": v(79.76, -10.41) * mm});
            skLineSegment(sketch, "E22.0.1.11", {"start": v(96.01, -10.41) * mm, "end": v(101.1, -10.41) * mm});
            skLineSegment(sketch, "E22.0.1.12", {"start": v(96.01, -5.33) * mm, "end": v(96.01, -10.41) * mm});
            skLineSegment(sketch, "E22.0.1.13", {"start": v(85.34, -10.41) * mm, "end": v(90.42, -10.41) * mm});
            skLineSegment(sketch, "E22.0.1.14", {"start": v(85.1, -5.33) * mm, "end": v(80, -5.33) * mm});
            skLineSegment(sketch, "E22.0.1.15", {"start": v(90.42, -5.33) * mm, "end": v(85.34, -5.33) * mm});
            skLineSegment(sketch, "E22.0.1.16", {"start": v(80, -5.33) * mm, "end": v(80, -10.41) * mm});
            skLineSegment(sketch, "E22.0.1.17", {"start": v(85.34, -5.33) * mm, "end": v(85.34, -10.41) * mm});
            skLineSegment(sketch, "E22.0.1.18", {"start": v(80, -10.41) * mm, "end": v(85.1, -10.41) * mm});
            skLineSegment(sketch, "E22.0.1.19", {"start": v(101.1, -5.33) * mm, "end": v(96.01, -5.33) * mm});
            skLineSegment(sketch, "E22.0.1.20", {"start": v(90.42, -10.41) * mm, "end": v(90.42, -5.33) * mm});
            skLineSegment(sketch, "E22.0.1.21", {"start": v(101.1, -10.41) * mm, "end": v(101.1, -5.33) * mm});
            skLineSegment(sketch, "E22.0.1.22", {"start": v(90.68, -10.41) * mm, "end": v(95.76, -10.41) * mm});
            skLineSegment(sketch, "E22.0.1.23", {"start": v(74.42, -10.41) * mm, "end": v(74.42, -5.33) * mm});
            skLineSegment(sketch, "E22.0.1.24", {"start": v(90.68, -5.33) * mm, "end": v(90.68, -10.41) * mm});
            skLineSegment(sketch, "E22.0.1.25", {"start": v(95.76, -10.41) * mm, "end": v(95.76, -5.33) * mm});
            skLineSegment(sketch, "E22.0.1.26", {"start": v(74.68, -5.33) * mm, "end": v(74.68, -10.41) * mm});
            skLineSegment(sketch, "E22.0.1.27", {"start": v(85.1, -10.41) * mm, "end": v(85.1, -5.33) * mm});
            skLineSegment(sketch, "E22.0.2.0", {"start": v(74.42, -10.67) * mm, "end": v(69.34, -10.67) * mm});
            skLineSegment(sketch, "E22.0.2.1", {"start": v(95.76, -10.67) * mm, "end": v(90.68, -10.67) * mm});
            skLineSegment(sketch, "E22.0.2.2", {"start": v(69.34, -10.67) * mm, "end": v(69.34, -15.75) * mm});
            skLineSegment(sketch, "E22.0.2.3", {"start": v(69.34, -15.75) * mm, "end": v(74.42, -15.75) * mm});
            skLineSegment(sketch, "E22.0.2.4", {"start": v(79.76, -15.75) * mm, "end": v(79.76, -10.67) * mm});
            skLineSegment(sketch, "E22.0.2.5", {"start": v(101.35, -15.75) * mm, "end": v(106.43, -15.75) * mm});
            skLineSegment(sketch, "E22.0.2.6", {"start": v(79.76, -10.67) * mm, "end": v(74.68, -10.67) * mm});
            skLineSegment(sketch, "E22.0.2.7", {"start": v(101.35, -10.67) * mm, "end": v(101.35, -15.75) * mm});
            skLineSegment(sketch, "E22.0.2.8", {"start": v(106.43, -10.67) * mm, "end": v(101.35, -10.67) * mm});
            skLineSegment(sketch, "E22.0.2.9", {"start": v(106.43, -15.75) * mm, "end": v(106.43, -10.67) * mm});
            skLineSegment(sketch, "E22.0.2.10", {"start": v(74.68, -15.75) * mm, "end": v(79.76, -15.75) * mm});
            skLineSegment(sketch, "E22.0.2.11", {"start": v(96.01, -15.75) * mm, "end": v(101.1, -15.75) * mm});
            skLineSegment(sketch, "E22.0.2.12", {"start": v(96.01, -10.67) * mm, "end": v(96.01, -15.75) * mm});
            skLineSegment(sketch, "E22.0.2.13", {"start": v(85.34, -15.75) * mm, "end": v(90.42, -15.75) * mm});
            skLineSegment(sketch, "E22.0.2.14", {"start": v(85.1, -10.67) * mm, "end": v(80, -10.67) * mm});
            skLineSegment(sketch, "E22.0.2.15", {"start": v(90.42, -10.67) * mm, "end": v(85.34, -10.67) * mm});
            skLineSegment(sketch, "E22.0.2.16", {"start": v(80, -10.67) * mm, "end": v(80, -15.75) * mm});
            skLineSegment(sketch, "E22.0.2.17", {"start": v(85.34, -10.67) * mm, "end": v(85.34, -15.75) * mm});
            skLineSegment(sketch, "E22.0.2.18", {"start": v(80, -15.75) * mm, "end": v(85.1, -15.75) * mm});
            skLineSegment(sketch, "E22.0.2.19", {"start": v(101.1, -10.67) * mm, "end": v(96.01, -10.67) * mm});
            skLineSegment(sketch, "E22.0.2.20", {"start": v(90.42, -15.75) * mm, "end": v(90.42, -10.67) * mm});
            skLineSegment(sketch, "E22.0.2.21", {"start": v(101.1, -15.75) * mm, "end": v(101.1, -10.67) * mm});
            skLineSegment(sketch, "E22.0.2.22", {"start": v(90.68, -15.75) * mm, "end": v(95.76, -15.75) * mm});
            skLineSegment(sketch, "E22.0.2.23", {"start": v(74.42, -15.75) * mm, "end": v(74.42, -10.67) * mm});
            skLineSegment(sketch, "E22.0.2.24", {"start": v(90.68, -10.67) * mm, "end": v(90.68, -15.75) * mm});
            skLineSegment(sketch, "E22.0.2.25", {"start": v(95.76, -15.75) * mm, "end": v(95.76, -10.67) * mm});
            skLineSegment(sketch, "E22.0.2.26", {"start": v(74.68, -10.67) * mm, "end": v(74.68, -15.75) * mm});
            skLineSegment(sketch, "E22.0.2.27", {"start": v(85.1, -15.75) * mm, "end": v(85.1, -10.67) * mm});
            skLineSegment(sketch, "E22.0.3.0", {"start": v(74.42, -16) * mm, "end": v(69.34, -16) * mm});
            skLineSegment(sketch, "E22.0.3.1", {"start": v(95.76, -16) * mm, "end": v(90.68, -16) * mm});
            skLineSegment(sketch, "E22.0.3.2", {"start": v(69.34, -16) * mm, "end": v(69.34, -21.08) * mm});
            skLineSegment(sketch, "E22.0.3.3", {"start": v(69.34, -21.08) * mm, "end": v(74.42, -21.08) * mm});
            skLineSegment(sketch, "E22.0.3.4", {"start": v(79.76, -21.08) * mm, "end": v(79.76, -16) * mm});
            skLineSegment(sketch, "E22.0.3.5", {"start": v(101.35, -21.08) * mm, "end": v(106.43, -21.08) * mm});
            skLineSegment(sketch, "E22.0.3.6", {"start": v(79.76, -16) * mm, "end": v(74.68, -16) * mm});
            skLineSegment(sketch, "E22.0.3.7", {"start": v(101.35, -16) * mm, "end": v(101.35, -21.08) * mm});
            skLineSegment(sketch, "E22.0.3.8", {"start": v(106.43, -16) * mm, "end": v(101.35, -16) * mm});
            skLineSegment(sketch, "E22.0.3.9", {"start": v(106.43, -21.08) * mm, "end": v(106.43, -16) * mm});
            skLineSegment(sketch, "E22.0.3.10", {"start": v(74.68, -21.08) * mm, "end": v(79.76, -21.08) * mm});
            skLineSegment(sketch, "E22.0.3.11", {"start": v(96.01, -21.08) * mm, "end": v(101.1, -21.08) * mm});
            skLineSegment(sketch, "E22.0.3.12", {"start": v(96.01, -16) * mm, "end": v(96.01, -21.08) * mm});
            skLineSegment(sketch, "E22.0.3.13", {"start": v(85.34, -21.08) * mm, "end": v(90.42, -21.08) * mm});
            skLineSegment(sketch, "E22.0.3.14", {"start": v(85.1, -16) * mm, "end": v(80, -16) * mm});
            skLineSegment(sketch, "E22.0.3.15", {"start": v(90.42, -16) * mm, "end": v(85.34, -16) * mm});
            skLineSegment(sketch, "E22.0.3.16", {"start": v(80, -16) * mm, "end": v(80, -21.08) * mm});
            skLineSegment(sketch, "E22.0.3.17", {"start": v(85.34, -16) * mm, "end": v(85.34, -21.08) * mm});
            skLineSegment(sketch, "E22.0.3.18", {"start": v(80, -21.08) * mm, "end": v(85.1, -21.08) * mm});
            skLineSegment(sketch, "E22.0.3.19", {"start": v(101.1, -16) * mm, "end": v(96.01, -16) * mm});
            skLineSegment(sketch, "E22.0.3.20", {"start": v(90.42, -21.08) * mm, "end": v(90.42, -16) * mm});
            skLineSegment(sketch, "E22.0.3.21", {"start": v(101.1, -21.08) * mm, "end": v(101.1, -16) * mm});
            skLineSegment(sketch, "E22.0.3.22", {"start": v(90.68, -21.08) * mm, "end": v(95.76, -21.08) * mm});
            skLineSegment(sketch, "E22.0.3.23", {"start": v(74.42, -21.08) * mm, "end": v(74.42, -16) * mm});
            skLineSegment(sketch, "E22.0.3.24", {"start": v(90.68, -16) * mm, "end": v(90.68, -21.08) * mm});
            skLineSegment(sketch, "E22.0.3.25", {"start": v(95.76, -21.08) * mm, "end": v(95.76, -16) * mm});
            skLineSegment(sketch, "E22.0.3.26", {"start": v(74.68, -16) * mm, "end": v(74.68, -21.08) * mm});
            skLineSegment(sketch, "E22.0.3.27", {"start": v(85.1, -21.08) * mm, "end": v(85.1, -16) * mm});
            skLineSegment(sketch, "E22.0.4.0", {"start": v(74.42, -21.34) * mm, "end": v(69.34, -21.34) * mm});
            skLineSegment(sketch, "E22.0.4.1", {"start": v(95.76, -21.34) * mm, "end": v(90.68, -21.34) * mm});
            skLineSegment(sketch, "E22.0.4.2", {"start": v(69.34, -21.34) * mm, "end": v(69.34, -26.42) * mm});
            skLineSegment(sketch, "E22.0.4.3", {"start": v(69.34, -26.42) * mm, "end": v(74.42, -26.42) * mm});
            skLineSegment(sketch, "E22.0.4.4", {"start": v(79.76, -26.42) * mm, "end": v(79.76, -21.34) * mm});
            skLineSegment(sketch, "E22.0.4.5", {"start": v(101.35, -26.42) * mm, "end": v(106.43, -26.42) * mm});
            skLineSegment(sketch, "E22.0.4.6", {"start": v(79.76, -21.34) * mm, "end": v(74.68, -21.34) * mm});
            skLineSegment(sketch, "E22.0.4.7", {"start": v(101.35, -21.34) * mm, "end": v(101.35, -26.42) * mm});
            skLineSegment(sketch, "E22.0.4.8", {"start": v(106.43, -21.34) * mm, "end": v(101.35, -21.34) * mm});
            skLineSegment(sketch, "E22.0.4.9", {"start": v(106.43, -26.42) * mm, "end": v(106.43, -21.34) * mm});
            skLineSegment(sketch, "E22.0.4.10", {"start": v(74.68, -26.42) * mm, "end": v(79.76, -26.42) * mm});
            skLineSegment(sketch, "E22.0.4.11", {"start": v(96.01, -26.42) * mm, "end": v(101.1, -26.42) * mm});
            skLineSegment(sketch, "E22.0.4.12", {"start": v(96.01, -21.34) * mm, "end": v(96.01, -26.42) * mm});
            skLineSegment(sketch, "E22.0.4.13", {"start": v(85.34, -26.42) * mm, "end": v(90.42, -26.42) * mm});
            skLineSegment(sketch, "E22.0.4.14", {"start": v(85.1, -21.34) * mm, "end": v(80, -21.34) * mm});
            skLineSegment(sketch, "E22.0.4.15", {"start": v(90.42, -21.34) * mm, "end": v(85.34, -21.34) * mm});
            skLineSegment(sketch, "E22.0.4.16", {"start": v(80, -21.34) * mm, "end": v(80, -26.42) * mm});
            skLineSegment(sketch, "E22.0.4.17", {"start": v(85.34, -21.34) * mm, "end": v(85.34, -26.42) * mm});
            skLineSegment(sketch, "E22.0.4.18", {"start": v(80, -26.42) * mm, "end": v(85.1, -26.42) * mm});
            skLineSegment(sketch, "E22.0.4.19", {"start": v(101.1, -21.34) * mm, "end": v(96.01, -21.34) * mm});
            skLineSegment(sketch, "E22.0.4.20", {"start": v(90.42, -26.42) * mm, "end": v(90.42, -21.34) * mm});
            skLineSegment(sketch, "E22.0.4.21", {"start": v(101.1, -26.42) * mm, "end": v(101.1, -21.34) * mm});
            skLineSegment(sketch, "E22.0.4.22", {"start": v(90.68, -26.42) * mm, "end": v(95.76, -26.42) * mm});
            skLineSegment(sketch, "E22.0.4.23", {"start": v(74.42, -26.42) * mm, "end": v(74.42, -21.34) * mm});
            skLineSegment(sketch, "E22.0.4.24", {"start": v(90.68, -21.34) * mm, "end": v(90.68, -26.42) * mm});
            skLineSegment(sketch, "E22.0.4.25", {"start": v(95.76, -26.42) * mm, "end": v(95.76, -21.34) * mm});
            skLineSegment(sketch, "E22.0.4.26", {"start": v(74.68, -21.34) * mm, "end": v(74.68, -26.42) * mm});
            skLineSegment(sketch, "E22.0.4.27", {"start": v(85.1, -26.42) * mm, "end": v(85.1, -21.34) * mm});
            skLineSegment(sketch, "E22.0.5.0", {"start": v(74.42, -26.67) * mm, "end": v(69.34, -26.67) * mm});
            skLineSegment(sketch, "E22.0.5.1", {"start": v(95.76, -26.67) * mm, "end": v(90.68, -26.67) * mm});
            skLineSegment(sketch, "E22.0.5.2", {"start": v(69.34, -26.67) * mm, "end": v(69.34, -31.75) * mm});
            skLineSegment(sketch, "E22.0.5.3", {"start": v(69.34, -31.75) * mm, "end": v(74.42, -31.75) * mm});
            skLineSegment(sketch, "E22.0.5.4", {"start": v(79.76, -31.75) * mm, "end": v(79.76, -26.67) * mm});
            skLineSegment(sketch, "E22.0.5.5", {"start": v(101.35, -31.75) * mm, "end": v(106.43, -31.75) * mm});
            skLineSegment(sketch, "E22.0.5.6", {"start": v(79.76, -26.67) * mm, "end": v(74.68, -26.67) * mm});
            skLineSegment(sketch, "E22.0.5.7", {"start": v(101.35, -26.67) * mm, "end": v(101.35, -31.75) * mm});
            skLineSegment(sketch, "E22.0.5.8", {"start": v(106.43, -26.67) * mm, "end": v(101.35, -26.67) * mm});
            skLineSegment(sketch, "E22.0.5.9", {"start": v(106.43, -31.75) * mm, "end": v(106.43, -26.67) * mm});
            skLineSegment(sketch, "E22.0.5.10", {"start": v(74.68, -31.75) * mm, "end": v(79.76, -31.75) * mm});
            skLineSegment(sketch, "E22.0.5.11", {"start": v(96.01, -31.75) * mm, "end": v(101.1, -31.75) * mm});
            skLineSegment(sketch, "E22.0.5.12", {"start": v(96.01, -26.67) * mm, "end": v(96.01, -31.75) * mm});
            skLineSegment(sketch, "E22.0.5.13", {"start": v(85.34, -31.75) * mm, "end": v(90.42, -31.75) * mm});
            skLineSegment(sketch, "E22.0.5.14", {"start": v(85.1, -26.67) * mm, "end": v(80, -26.67) * mm});
            skLineSegment(sketch, "E22.0.5.15", {"start": v(90.42, -26.67) * mm, "end": v(85.34, -26.67) * mm});
            skLineSegment(sketch, "E22.0.5.16", {"start": v(80, -26.67) * mm, "end": v(80, -31.75) * mm});
            skLineSegment(sketch, "E22.0.5.17", {"start": v(85.34, -26.67) * mm, "end": v(85.34, -31.75) * mm});
            skLineSegment(sketch, "E22.0.5.18", {"start": v(80, -31.75) * mm, "end": v(85.1, -31.75) * mm});
            skLineSegment(sketch, "E22.0.5.19", {"start": v(101.1, -26.67) * mm, "end": v(96.01, -26.67) * mm});
            skLineSegment(sketch, "E22.0.5.20", {"start": v(90.42, -31.75) * mm, "end": v(90.42, -26.67) * mm});
            skLineSegment(sketch, "E22.0.5.21", {"start": v(101.1, -31.75) * mm, "end": v(101.1, -26.67) * mm});
            skLineSegment(sketch, "E22.0.5.22", {"start": v(90.68, -31.75) * mm, "end": v(95.76, -31.75) * mm});
            skLineSegment(sketch, "E22.0.5.23", {"start": v(74.42, -31.75) * mm, "end": v(74.42, -26.67) * mm});
            skLineSegment(sketch, "E22.0.5.24", {"start": v(90.68, -26.67) * mm, "end": v(90.68, -31.75) * mm});
            skLineSegment(sketch, "E22.0.5.25", {"start": v(95.76, -31.75) * mm, "end": v(95.76, -26.67) * mm});
            skLineSegment(sketch, "E22.0.5.26", {"start": v(74.68, -26.67) * mm, "end": v(74.68, -31.75) * mm});
            skLineSegment(sketch, "E22.0.5.27", {"start": v(85.1, -31.75) * mm, "end": v(85.1, -26.67) * mm});
            skLineSegment(sketch, "E22.0.6.0", {"start": v(74.42, -32) * mm, "end": v(69.34, -32) * mm});
            skLineSegment(sketch, "E22.0.6.1", {"start": v(95.76, -32) * mm, "end": v(90.68, -32) * mm});
            skLineSegment(sketch, "E22.0.6.2", {"start": v(69.34, -32) * mm, "end": v(69.34, -37.08) * mm});
            skLineSegment(sketch, "E22.0.6.3", {"start": v(69.34, -37.08) * mm, "end": v(74.42, -37.08) * mm});
            skLineSegment(sketch, "E22.0.6.4", {"start": v(79.76, -37.08) * mm, "end": v(79.76, -32) * mm});
            skLineSegment(sketch, "E22.0.6.5", {"start": v(101.35, -37.08) * mm, "end": v(106.43, -37.08) * mm});
            skLineSegment(sketch, "E22.0.6.6", {"start": v(79.76, -32) * mm, "end": v(74.68, -32) * mm});
            skLineSegment(sketch, "E22.0.6.7", {"start": v(101.35, -32) * mm, "end": v(101.35, -37.08) * mm});
            skLineSegment(sketch, "E22.0.6.8", {"start": v(106.43, -32) * mm, "end": v(101.35, -32) * mm});
            skLineSegment(sketch, "E22.0.6.9", {"start": v(106.43, -37.08) * mm, "end": v(106.43, -32) * mm});
            skLineSegment(sketch, "E22.0.6.10", {"start": v(74.68, -37.08) * mm, "end": v(79.76, -37.08) * mm});
            skLineSegment(sketch, "E22.0.6.11", {"start": v(96.01, -37.08) * mm, "end": v(101.1, -37.08) * mm});
            skLineSegment(sketch, "E22.0.6.12", {"start": v(96.01, -32) * mm, "end": v(96.01, -37.08) * mm});
            skLineSegment(sketch, "E22.0.6.13", {"start": v(85.34, -37.08) * mm, "end": v(90.42, -37.08) * mm});
            skLineSegment(sketch, "E22.0.6.14", {"start": v(85.1, -32) * mm, "end": v(80, -32) * mm});
            skLineSegment(sketch, "E22.0.6.15", {"start": v(90.42, -32) * mm, "end": v(85.34, -32) * mm});
            skLineSegment(sketch, "E22.0.6.16", {"start": v(80, -32) * mm, "end": v(80, -37.08) * mm});
            skLineSegment(sketch, "E22.0.6.17", {"start": v(85.34, -32) * mm, "end": v(85.34, -37.08) * mm});
            skLineSegment(sketch, "E22.0.6.18", {"start": v(80, -37.08) * mm, "end": v(85.1, -37.08) * mm});
            skLineSegment(sketch, "E22.0.6.19", {"start": v(101.1, -32) * mm, "end": v(96.01, -32) * mm});
            skLineSegment(sketch, "E22.0.6.20", {"start": v(90.42, -37.08) * mm, "end": v(90.42, -32) * mm});
            skLineSegment(sketch, "E22.0.6.21", {"start": v(101.1, -37.08) * mm, "end": v(101.1, -32) * mm});
            skLineSegment(sketch, "E22.0.6.22", {"start": v(90.68, -37.08) * mm, "end": v(95.76, -37.08) * mm});
            skLineSegment(sketch, "E22.0.6.23", {"start": v(74.42, -37.08) * mm, "end": v(74.42, -32) * mm});
            skLineSegment(sketch, "E22.0.6.24", {"start": v(90.68, -32) * mm, "end": v(90.68, -37.08) * mm});
            skLineSegment(sketch, "E22.0.6.25", {"start": v(95.76, -37.08) * mm, "end": v(95.76, -32) * mm});
            skLineSegment(sketch, "E22.0.6.26", {"start": v(74.68, -32) * mm, "end": v(74.68, -37.08) * mm});
            skLineSegment(sketch, "E22.0.6.27", {"start": v(85.1, -37.08) * mm, "end": v(85.1, -32) * mm});
            skLineSegment(sketch, "E22.0.7.0", {"start": v(74.42, -37.34) * mm, "end": v(69.34, -37.34) * mm});
            skLineSegment(sketch, "E22.0.7.1", {"start": v(95.76, -37.34) * mm, "end": v(90.68, -37.34) * mm});
            skLineSegment(sketch, "E22.0.7.2", {"start": v(69.34, -37.34) * mm, "end": v(69.34, -42.42) * mm});
            skLineSegment(sketch, "E22.0.7.3", {"start": v(69.34, -42.42) * mm, "end": v(74.42, -42.42) * mm});
            skLineSegment(sketch, "E22.0.7.4", {"start": v(79.76, -42.42) * mm, "end": v(79.76, -37.34) * mm});
            skLineSegment(sketch, "E22.0.7.5", {"start": v(101.35, -42.42) * mm, "end": v(106.43, -42.42) * mm});
            skLineSegment(sketch, "E22.0.7.6", {"start": v(79.76, -37.34) * mm, "end": v(74.68, -37.34) * mm});
            skLineSegment(sketch, "E22.0.7.7", {"start": v(101.35, -37.34) * mm, "end": v(101.35, -42.42) * mm});
            skLineSegment(sketch, "E22.0.7.8", {"start": v(106.43, -37.34) * mm, "end": v(101.35, -37.34) * mm});
            skLineSegment(sketch, "E22.0.7.9", {"start": v(106.43, -42.42) * mm, "end": v(106.43, -37.34) * mm});
            skLineSegment(sketch, "E22.0.7.10", {"start": v(74.68, -42.42) * mm, "end": v(79.76, -42.42) * mm});
            skLineSegment(sketch, "E22.0.7.11", {"start": v(96.01, -42.42) * mm, "end": v(101.1, -42.42) * mm});
            skLineSegment(sketch, "E22.0.7.12", {"start": v(96.01, -37.34) * mm, "end": v(96.01, -42.42) * mm});
            skLineSegment(sketch, "E22.0.7.13", {"start": v(85.34, -42.42) * mm, "end": v(90.42, -42.42) * mm});
            skLineSegment(sketch, "E22.0.7.14", {"start": v(85.1, -37.34) * mm, "end": v(80, -37.34) * mm});
            skLineSegment(sketch, "E22.0.7.15", {"start": v(90.42, -37.34) * mm, "end": v(85.34, -37.34) * mm});
            skLineSegment(sketch, "E22.0.7.16", {"start": v(80, -37.34) * mm, "end": v(80, -42.42) * mm});
            skLineSegment(sketch, "E22.0.7.17", {"start": v(85.34, -37.34) * mm, "end": v(85.34, -42.42) * mm});
            skLineSegment(sketch, "E22.0.7.18", {"start": v(80, -42.42) * mm, "end": v(85.1, -42.42) * mm});
            skLineSegment(sketch, "E22.0.7.19", {"start": v(101.1, -37.34) * mm, "end": v(96.01, -37.34) * mm});
            skLineSegment(sketch, "E22.0.7.20", {"start": v(90.42, -42.42) * mm, "end": v(90.42, -37.34) * mm});
            skLineSegment(sketch, "E22.0.7.21", {"start": v(101.1, -42.42) * mm, "end": v(101.1, -37.34) * mm});
            skLineSegment(sketch, "E22.0.7.22", {"start": v(90.68, -42.42) * mm, "end": v(95.76, -42.42) * mm});
            skLineSegment(sketch, "E22.0.7.23", {"start": v(74.42, -42.42) * mm, "end": v(74.42, -37.34) * mm});
            skLineSegment(sketch, "E22.0.7.24", {"start": v(90.68, -37.34) * mm, "end": v(90.68, -42.42) * mm});
            skLineSegment(sketch, "E22.0.7.25", {"start": v(95.76, -42.42) * mm, "end": v(95.76, -37.34) * mm});
            skLineSegment(sketch, "E22.0.7.26", {"start": v(74.68, -37.34) * mm, "end": v(74.68, -42.42) * mm});
            skLineSegment(sketch, "E22.0.7.27", {"start": v(85.1, -42.42) * mm, "end": v(85.1, -37.34) * mm});
            skLineSegment(sketch, "E22.0.8.0", {"start": v(74.42, -42.67) * mm, "end": v(69.34, -42.67) * mm});
            skLineSegment(sketch, "E22.0.8.1", {"start": v(95.76, -42.67) * mm, "end": v(90.68, -42.67) * mm});
            skLineSegment(sketch, "E22.0.8.2", {"start": v(69.34, -42.67) * mm, "end": v(69.34, -47.75) * mm});
            skLineSegment(sketch, "E22.0.8.3", {"start": v(69.34, -47.75) * mm, "end": v(74.42, -47.75) * mm});
            skLineSegment(sketch, "E22.0.8.4", {"start": v(79.76, -47.75) * mm, "end": v(79.76, -42.67) * mm});
            skLineSegment(sketch, "E22.0.8.5", {"start": v(101.35, -47.75) * mm, "end": v(106.43, -47.75) * mm});
            skLineSegment(sketch, "E22.0.8.6", {"start": v(79.76, -42.67) * mm, "end": v(74.68, -42.67) * mm});
            skLineSegment(sketch, "E22.0.8.7", {"start": v(101.35, -42.67) * mm, "end": v(101.35, -47.75) * mm});
            skLineSegment(sketch, "E22.0.8.8", {"start": v(106.43, -42.67) * mm, "end": v(101.35, -42.67) * mm});
            skLineSegment(sketch, "E22.0.8.9", {"start": v(106.43, -47.75) * mm, "end": v(106.43, -42.67) * mm});
            skLineSegment(sketch, "E22.0.8.10", {"start": v(74.68, -47.75) * mm, "end": v(79.76, -47.75) * mm});
            skLineSegment(sketch, "E22.0.8.11", {"start": v(96.01, -47.75) * mm, "end": v(101.1, -47.75) * mm});
            skLineSegment(sketch, "E22.0.8.12", {"start": v(96.01, -42.67) * mm, "end": v(96.01, -47.75) * mm});
            skLineSegment(sketch, "E22.0.8.13", {"start": v(85.34, -47.75) * mm, "end": v(90.42, -47.75) * mm});
            skLineSegment(sketch, "E22.0.8.14", {"start": v(85.1, -42.67) * mm, "end": v(80, -42.67) * mm});
            skLineSegment(sketch, "E22.0.8.15", {"start": v(90.42, -42.67) * mm, "end": v(85.34, -42.67) * mm});
            skLineSegment(sketch, "E22.0.8.16", {"start": v(80, -42.67) * mm, "end": v(80, -47.75) * mm});
            skLineSegment(sketch, "E22.0.8.17", {"start": v(85.34, -42.67) * mm, "end": v(85.34, -47.75) * mm});
            skLineSegment(sketch, "E22.0.8.18", {"start": v(80, -47.75) * mm, "end": v(85.1, -47.75) * mm});
            skLineSegment(sketch, "E22.0.8.19", {"start": v(101.1, -42.67) * mm, "end": v(96.01, -42.67) * mm});
            skLineSegment(sketch, "E22.0.8.20", {"start": v(90.42, -47.75) * mm, "end": v(90.42, -42.67) * mm});
            skLineSegment(sketch, "E22.0.8.21", {"start": v(101.1, -47.75) * mm, "end": v(101.1, -42.67) * mm});
            skLineSegment(sketch, "E22.0.8.22", {"start": v(90.68, -47.75) * mm, "end": v(95.76, -47.75) * mm});
            skLineSegment(sketch, "E22.0.8.23", {"start": v(74.42, -47.75) * mm, "end": v(74.42, -42.67) * mm});
            skLineSegment(sketch, "E22.0.8.24", {"start": v(90.68, -42.67) * mm, "end": v(90.68, -47.75) * mm});
            skLineSegment(sketch, "E22.0.8.25", {"start": v(95.76, -47.75) * mm, "end": v(95.76, -42.67) * mm});
            skLineSegment(sketch, "E22.0.8.26", {"start": v(74.68, -42.67) * mm, "end": v(74.68, -47.75) * mm});
            skLineSegment(sketch, "E22.0.8.27", {"start": v(85.1, -47.75) * mm, "end": v(85.1, -42.67) * mm});
            skLineSegment(sketch, "E22.0.9.0", {"start": v(74.42, -48) * mm, "end": v(69.34, -48) * mm});
            skLineSegment(sketch, "E22.0.9.1", {"start": v(95.76, -48) * mm, "end": v(90.68, -48) * mm});
            skLineSegment(sketch, "E22.0.9.2", {"start": v(69.34, -48) * mm, "end": v(69.34, -53.09) * mm});
            skLineSegment(sketch, "E22.0.9.3", {"start": v(69.34, -53.09) * mm, "end": v(74.42, -53.09) * mm});
            skLineSegment(sketch, "E22.0.9.4", {"start": v(79.76, -53.09) * mm, "end": v(79.76, -48) * mm});
            skLineSegment(sketch, "E22.0.9.5", {"start": v(101.35, -53.09) * mm, "end": v(106.43, -53.09) * mm});
            skLineSegment(sketch, "E22.0.9.6", {"start": v(79.76, -48) * mm, "end": v(74.68, -48) * mm});
            skLineSegment(sketch, "E22.0.9.7", {"start": v(101.35, -48) * mm, "end": v(101.35, -53.09) * mm});
            skLineSegment(sketch, "E22.0.9.8", {"start": v(106.43, -48) * mm, "end": v(101.35, -48) * mm});
            skLineSegment(sketch, "E22.0.9.9", {"start": v(106.43, -53.09) * mm, "end": v(106.43, -48) * mm});
            skLineSegment(sketch, "E22.0.9.10", {"start": v(74.68, -53.09) * mm, "end": v(79.76, -53.09) * mm});
            skLineSegment(sketch, "E22.0.9.11", {"start": v(96.01, -53.09) * mm, "end": v(101.1, -53.09) * mm});
            skLineSegment(sketch, "E22.0.9.12", {"start": v(96.01, -48) * mm, "end": v(96.01, -53.09) * mm});
            skLineSegment(sketch, "E22.0.9.13", {"start": v(85.34, -53.09) * mm, "end": v(90.42, -53.09) * mm});
            skLineSegment(sketch, "E22.0.9.14", {"start": v(85.1, -48) * mm, "end": v(80, -48) * mm});
            skLineSegment(sketch, "E22.0.9.15", {"start": v(90.42, -48) * mm, "end": v(85.34, -48) * mm});
            skLineSegment(sketch, "E22.0.9.16", {"start": v(80, -48) * mm, "end": v(80, -53.09) * mm});
            skLineSegment(sketch, "E22.0.9.17", {"start": v(85.34, -48) * mm, "end": v(85.34, -53.09) * mm});
            skLineSegment(sketch, "E22.0.9.18", {"start": v(80, -53.09) * mm, "end": v(85.1, -53.09) * mm});
            skLineSegment(sketch, "E22.0.9.19", {"start": v(101.1, -48) * mm, "end": v(96.01, -48) * mm});
            skLineSegment(sketch, "E22.0.9.20", {"start": v(90.42, -53.09) * mm, "end": v(90.42, -48) * mm});
            skLineSegment(sketch, "E22.0.9.21", {"start": v(101.1, -53.09) * mm, "end": v(101.1, -48) * mm});
            skLineSegment(sketch, "E22.0.9.22", {"start": v(90.68, -53.09) * mm, "end": v(95.76, -53.09) * mm});
            skLineSegment(sketch, "E22.0.9.23", {"start": v(74.42, -53.09) * mm, "end": v(74.42, -48) * mm});
            skLineSegment(sketch, "E22.0.9.24", {"start": v(90.68, -48) * mm, "end": v(90.68, -53.09) * mm});
            skLineSegment(sketch, "E22.0.9.25", {"start": v(95.76, -53.09) * mm, "end": v(95.76, -48) * mm});
            skLineSegment(sketch, "E22.0.9.26", {"start": v(74.68, -48) * mm, "end": v(74.68, -53.09) * mm});
            skLineSegment(sketch, "E22.0.9.27", {"start": v(85.1, -53.09) * mm, "end": v(85.1, -48) * mm});
            skLineSegment(sketch, "E22.0.10.0", {"start": v(74.42, -53.34) * mm, "end": v(69.34, -53.34) * mm});
            skLineSegment(sketch, "E22.0.10.1", {"start": v(95.76, -53.34) * mm, "end": v(90.68, -53.34) * mm});
            skLineSegment(sketch, "E22.0.10.2", {"start": v(69.34, -53.34) * mm, "end": v(69.34, -58.42) * mm});
            skLineSegment(sketch, "E22.0.10.3", {"start": v(69.34, -58.42) * mm, "end": v(74.42, -58.42) * mm});
            skLineSegment(sketch, "E22.0.10.4", {"start": v(79.76, -58.42) * mm, "end": v(79.76, -53.34) * mm});
            skLineSegment(sketch, "E22.0.10.5", {"start": v(101.35, -58.42) * mm, "end": v(106.43, -58.42) * mm});
            skLineSegment(sketch, "E22.0.10.6", {"start": v(79.76, -53.34) * mm, "end": v(74.68, -53.34) * mm});
            skLineSegment(sketch, "E22.0.10.7", {"start": v(101.35, -53.34) * mm, "end": v(101.35, -58.42) * mm});
            skLineSegment(sketch, "E22.0.10.8", {"start": v(106.43, -53.34) * mm, "end": v(101.35, -53.34) * mm});
            skLineSegment(sketch, "E22.0.10.9", {"start": v(106.43, -58.42) * mm, "end": v(106.43, -53.34) * mm});
            skLineSegment(sketch, "E22.0.10.10", {"start": v(74.68, -58.42) * mm, "end": v(79.76, -58.42) * mm});
            skLineSegment(sketch, "E22.0.10.11", {"start": v(96.01, -58.42) * mm, "end": v(101.1, -58.42) * mm});
            skLineSegment(sketch, "E22.0.10.12", {"start": v(96.01, -53.34) * mm, "end": v(96.01, -58.42) * mm});
            skLineSegment(sketch, "E22.0.10.13", {"start": v(85.34, -58.42) * mm, "end": v(90.42, -58.42) * mm});
            skLineSegment(sketch, "E22.0.10.14", {"start": v(85.1, -53.34) * mm, "end": v(80, -53.34) * mm});
            skLineSegment(sketch, "E22.0.10.15", {"start": v(90.42, -53.34) * mm, "end": v(85.34, -53.34) * mm});
            skLineSegment(sketch, "E22.0.10.16", {"start": v(80, -53.34) * mm, "end": v(80, -58.42) * mm});
            skLineSegment(sketch, "E22.0.10.17", {"start": v(85.34, -53.34) * mm, "end": v(85.34, -58.42) * mm});
            skLineSegment(sketch, "E22.0.10.18", {"start": v(80, -58.42) * mm, "end": v(85.1, -58.42) * mm});
            skLineSegment(sketch, "E22.0.10.19", {"start": v(101.1, -53.34) * mm, "end": v(96.01, -53.34) * mm});
            skLineSegment(sketch, "E22.0.10.20", {"start": v(90.42, -58.42) * mm, "end": v(90.42, -53.34) * mm});
            skLineSegment(sketch, "E22.0.10.21", {"start": v(101.1, -58.42) * mm, "end": v(101.1, -53.34) * mm});
            skLineSegment(sketch, "E22.0.10.22", {"start": v(90.68, -58.42) * mm, "end": v(95.76, -58.42) * mm});
            skLineSegment(sketch, "E22.0.10.23", {"start": v(74.42, -58.42) * mm, "end": v(74.42, -53.34) * mm});
            skLineSegment(sketch, "E22.0.10.24", {"start": v(90.68, -53.34) * mm, "end": v(90.68, -58.42) * mm});
            skLineSegment(sketch, "E22.0.10.25", {"start": v(95.76, -58.42) * mm, "end": v(95.76, -53.34) * mm});
            skLineSegment(sketch, "E22.0.10.26", {"start": v(74.68, -53.34) * mm, "end": v(74.68, -58.42) * mm});
            skLineSegment(sketch, "E22.0.10.27", {"start": v(85.1, -58.42) * mm, "end": v(85.1, -53.34) * mm});
            skLineSegment(sketch, "E22.0.11.0", {"start": v(74.42, -58.67) * mm, "end": v(69.34, -58.67) * mm});
            skLineSegment(sketch, "E22.0.11.1", {"start": v(95.76, -58.67) * mm, "end": v(90.68, -58.67) * mm});
            skLineSegment(sketch, "E22.0.11.2", {"start": v(69.34, -58.67) * mm, "end": v(69.34, -63.75) * mm});
            skLineSegment(sketch, "E22.0.11.3", {"start": v(69.34, -63.75) * mm, "end": v(74.42, -63.75) * mm});
            skLineSegment(sketch, "E22.0.11.4", {"start": v(79.76, -63.75) * mm, "end": v(79.76, -58.67) * mm});
            skLineSegment(sketch, "E22.0.11.5", {"start": v(101.35, -63.75) * mm, "end": v(106.43, -63.75) * mm});
            skLineSegment(sketch, "E22.0.11.6", {"start": v(79.76, -58.67) * mm, "end": v(74.68, -58.67) * mm});
            skLineSegment(sketch, "E22.0.11.7", {"start": v(101.35, -58.67) * mm, "end": v(101.35, -63.75) * mm});
            skLineSegment(sketch, "E22.0.11.8", {"start": v(106.43, -58.67) * mm, "end": v(101.35, -58.67) * mm});
            skLineSegment(sketch, "E22.0.11.9", {"start": v(106.43, -63.75) * mm, "end": v(106.43, -58.67) * mm});
            skLineSegment(sketch, "E22.0.11.10", {"start": v(74.68, -63.75) * mm, "end": v(79.76, -63.75) * mm});
            skLineSegment(sketch, "E22.0.11.11", {"start": v(96.01, -63.75) * mm, "end": v(101.1, -63.75) * mm});
            skLineSegment(sketch, "E22.0.11.12", {"start": v(96.01, -58.67) * mm, "end": v(96.01, -63.75) * mm});
            skLineSegment(sketch, "E22.0.11.13", {"start": v(85.34, -63.75) * mm, "end": v(90.42, -63.75) * mm});
            skLineSegment(sketch, "E22.0.11.14", {"start": v(85.1, -58.67) * mm, "end": v(80, -58.67) * mm});
            skLineSegment(sketch, "E22.0.11.15", {"start": v(90.42, -58.67) * mm, "end": v(85.34, -58.67) * mm});
            skLineSegment(sketch, "E22.0.11.16", {"start": v(80, -58.67) * mm, "end": v(80, -63.75) * mm});
            skLineSegment(sketch, "E22.0.11.17", {"start": v(85.34, -58.67) * mm, "end": v(85.34, -63.75) * mm});
            skLineSegment(sketch, "E22.0.11.18", {"start": v(80, -63.75) * mm, "end": v(85.1, -63.75) * mm});
            skLineSegment(sketch, "E22.0.11.19", {"start": v(101.1, -58.67) * mm, "end": v(96.01, -58.67) * mm});
            skLineSegment(sketch, "E22.0.11.20", {"start": v(90.42, -63.75) * mm, "end": v(90.42, -58.67) * mm});
            skLineSegment(sketch, "E22.0.11.21", {"start": v(101.1, -63.75) * mm, "end": v(101.1, -58.67) * mm});
            skLineSegment(sketch, "E22.0.11.22", {"start": v(90.68, -63.75) * mm, "end": v(95.76, -63.75) * mm});
            skLineSegment(sketch, "E22.0.11.23", {"start": v(74.42, -63.75) * mm, "end": v(74.42, -58.67) * mm});
            skLineSegment(sketch, "E22.0.11.24", {"start": v(90.68, -58.67) * mm, "end": v(90.68, -63.75) * mm});
            skLineSegment(sketch, "E22.0.11.25", {"start": v(95.76, -63.75) * mm, "end": v(95.76, -58.67) * mm});
            skLineSegment(sketch, "E22.0.11.26", {"start": v(74.68, -58.67) * mm, "end": v(74.68, -63.75) * mm});
            skLineSegment(sketch, "E22.0.11.27", {"start": v(85.1, -63.75) * mm, "end": v(85.1, -58.67) * mm});
            skLineSegment(sketch, "E22.0.12.0", {"start": v(74.42, -64) * mm, "end": v(69.34, -64) * mm});
            skLineSegment(sketch, "E22.0.12.1", {"start": v(95.76, -64) * mm, "end": v(90.68, -64) * mm});
            skLineSegment(sketch, "E22.0.12.2", {"start": v(69.34, -64) * mm, "end": v(69.34, -69.09) * mm});
            skLineSegment(sketch, "E22.0.12.3", {"start": v(69.34, -69.09) * mm, "end": v(74.42, -69.09) * mm});
            skLineSegment(sketch, "E22.0.12.4", {"start": v(79.76, -69.09) * mm, "end": v(79.76, -64) * mm});
            skLineSegment(sketch, "E22.0.12.5", {"start": v(101.35, -69.09) * mm, "end": v(106.43, -69.09) * mm});
            skLineSegment(sketch, "E22.0.12.6", {"start": v(79.76, -64) * mm, "end": v(74.68, -64) * mm});
            skLineSegment(sketch, "E22.0.12.7", {"start": v(101.35, -64) * mm, "end": v(101.35, -69.09) * mm});
            skLineSegment(sketch, "E22.0.12.8", {"start": v(106.43, -64) * mm, "end": v(101.35, -64) * mm});
            skLineSegment(sketch, "E22.0.12.9", {"start": v(106.43, -69.09) * mm, "end": v(106.43, -64) * mm});
            skLineSegment(sketch, "E22.0.12.10", {"start": v(74.68, -69.09) * mm, "end": v(79.76, -69.09) * mm});
            skLineSegment(sketch, "E22.0.12.11", {"start": v(96.01, -69.09) * mm, "end": v(101.1, -69.09) * mm});
            skLineSegment(sketch, "E22.0.12.12", {"start": v(96.01, -64) * mm, "end": v(96.01, -69.09) * mm});
            skLineSegment(sketch, "E22.0.12.13", {"start": v(85.34, -69.09) * mm, "end": v(90.42, -69.09) * mm});
            skLineSegment(sketch, "E22.0.12.14", {"start": v(85.1, -64) * mm, "end": v(80, -64) * mm});
            skLineSegment(sketch, "E22.0.12.15", {"start": v(90.42, -64) * mm, "end": v(85.34, -64) * mm});
            skLineSegment(sketch, "E22.0.12.16", {"start": v(80, -64) * mm, "end": v(80, -69.09) * mm});
            skLineSegment(sketch, "E22.0.12.17", {"start": v(85.34, -64) * mm, "end": v(85.34, -69.09) * mm});
            skLineSegment(sketch, "E22.0.12.18", {"start": v(80, -69.09) * mm, "end": v(85.1, -69.09) * mm});
            skLineSegment(sketch, "E22.0.12.19", {"start": v(101.1, -64) * mm, "end": v(96.01, -64) * mm});
            skLineSegment(sketch, "E22.0.12.20", {"start": v(90.42, -69.09) * mm, "end": v(90.42, -64) * mm});
            skLineSegment(sketch, "E22.0.12.21", {"start": v(101.1, -69.09) * mm, "end": v(101.1, -64) * mm});
            skLineSegment(sketch, "E22.0.12.22", {"start": v(90.68, -69.09) * mm, "end": v(95.76, -69.09) * mm});
            skLineSegment(sketch, "E22.0.12.23", {"start": v(74.42, -69.09) * mm, "end": v(74.42, -64) * mm});
            skLineSegment(sketch, "E22.0.12.24", {"start": v(90.68, -64) * mm, "end": v(90.68, -69.09) * mm});
            skLineSegment(sketch, "E22.0.12.25", {"start": v(95.76, -69.09) * mm, "end": v(95.76, -64) * mm});
            skLineSegment(sketch, "E22.0.12.26", {"start": v(74.68, -64) * mm, "end": v(74.68, -69.09) * mm});
            skLineSegment(sketch, "E22.0.12.27", {"start": v(85.1, -69.09) * mm, "end": v(85.1, -64) * mm});
            skLineSegment(sketch, "E22.0.13.0", {"start": v(74.42, -69.34) * mm, "end": v(69.34, -69.34) * mm});
            skLineSegment(sketch, "E22.0.13.1", {"start": v(95.76, -69.34) * mm, "end": v(90.68, -69.34) * mm});
            skLineSegment(sketch, "E22.0.13.2", {"start": v(69.34, -69.34) * mm, "end": v(69.34, -74.42) * mm});
            skLineSegment(sketch, "E22.0.13.3", {"start": v(69.34, -74.42) * mm, "end": v(74.42, -74.42) * mm});
            skLineSegment(sketch, "E22.0.13.4", {"start": v(79.76, -74.42) * mm, "end": v(79.76, -69.34) * mm});
            skLineSegment(sketch, "E22.0.13.5", {"start": v(101.35, -74.42) * mm, "end": v(106.43, -74.42) * mm});
            skLineSegment(sketch, "E22.0.13.6", {"start": v(79.76, -69.34) * mm, "end": v(74.68, -69.34) * mm});
            skLineSegment(sketch, "E22.0.13.7", {"start": v(101.35, -69.34) * mm, "end": v(101.35, -74.42) * mm});
            skLineSegment(sketch, "E22.0.13.8", {"start": v(106.43, -69.34) * mm, "end": v(101.35, -69.34) * mm});
            skLineSegment(sketch, "E22.0.13.9", {"start": v(106.43, -74.42) * mm, "end": v(106.43, -69.34) * mm});
            skLineSegment(sketch, "E22.0.13.10", {"start": v(74.68, -74.42) * mm, "end": v(79.76, -74.42) * mm});
            skLineSegment(sketch, "E22.0.13.11", {"start": v(96.01, -74.42) * mm, "end": v(101.1, -74.42) * mm});
            skLineSegment(sketch, "E22.0.13.12", {"start": v(96.01, -69.34) * mm, "end": v(96.01, -74.42) * mm});
            skLineSegment(sketch, "E22.0.13.13", {"start": v(85.34, -74.42) * mm, "end": v(90.42, -74.42) * mm});
            skLineSegment(sketch, "E22.0.13.14", {"start": v(85.1, -69.34) * mm, "end": v(80, -69.34) * mm});
            skLineSegment(sketch, "E22.0.13.15", {"start": v(90.42, -69.34) * mm, "end": v(85.34, -69.34) * mm});
            skLineSegment(sketch, "E22.0.13.16", {"start": v(80, -69.34) * mm, "end": v(80, -74.42) * mm});
            skLineSegment(sketch, "E22.0.13.17", {"start": v(85.34, -69.34) * mm, "end": v(85.34, -74.42) * mm});
            skLineSegment(sketch, "E22.0.13.18", {"start": v(80, -74.42) * mm, "end": v(85.1, -74.42) * mm});
            skLineSegment(sketch, "E22.0.13.19", {"start": v(101.1, -69.34) * mm, "end": v(96.01, -69.34) * mm});
            skLineSegment(sketch, "E22.0.13.20", {"start": v(90.42, -74.42) * mm, "end": v(90.42, -69.34) * mm});
            skLineSegment(sketch, "E22.0.13.21", {"start": v(101.1, -74.42) * mm, "end": v(101.1, -69.34) * mm});
            skLineSegment(sketch, "E22.0.13.22", {"start": v(90.68, -74.42) * mm, "end": v(95.76, -74.42) * mm});
            skLineSegment(sketch, "E22.0.13.23", {"start": v(74.42, -74.42) * mm, "end": v(74.42, -69.34) * mm});
            skLineSegment(sketch, "E22.0.13.24", {"start": v(90.68, -69.34) * mm, "end": v(90.68, -74.42) * mm});
            skLineSegment(sketch, "E22.0.13.25", {"start": v(95.76, -74.42) * mm, "end": v(95.76, -69.34) * mm});
            skLineSegment(sketch, "E22.0.13.26", {"start": v(74.68, -69.34) * mm, "end": v(74.68, -74.42) * mm});
            skLineSegment(sketch, "E22.0.13.27", {"start": v(85.1, -74.42) * mm, "end": v(85.1, -69.34) * mm});
            skLineSegment(sketch, "E22.0.14.0", {"start": v(74.42, -74.68) * mm, "end": v(69.34, -74.68) * mm});
            skLineSegment(sketch, "E22.0.14.1", {"start": v(95.76, -74.68) * mm, "end": v(90.68, -74.68) * mm});
            skLineSegment(sketch, "E22.0.14.2", {"start": v(69.34, -74.68) * mm, "end": v(69.34, -79.76) * mm});
            skLineSegment(sketch, "E22.0.14.3", {"start": v(69.34, -79.76) * mm, "end": v(74.42, -79.76) * mm});
            skLineSegment(sketch, "E22.0.14.4", {"start": v(79.76, -79.76) * mm, "end": v(79.76, -74.68) * mm});
            skLineSegment(sketch, "E22.0.14.5", {"start": v(101.35, -79.76) * mm, "end": v(106.43, -79.76) * mm});
            skLineSegment(sketch, "E22.0.14.6", {"start": v(79.76, -74.68) * mm, "end": v(74.68, -74.68) * mm});
            skLineSegment(sketch, "E22.0.14.7", {"start": v(101.35, -74.68) * mm, "end": v(101.35, -79.76) * mm});
            skLineSegment(sketch, "E22.0.14.8", {"start": v(106.43, -74.68) * mm, "end": v(101.35, -74.68) * mm});
            skLineSegment(sketch, "E22.0.14.9", {"start": v(106.43, -79.76) * mm, "end": v(106.43, -74.68) * mm});
            skLineSegment(sketch, "E22.0.14.10", {"start": v(74.68, -79.76) * mm, "end": v(79.76, -79.76) * mm});
            skLineSegment(sketch, "E22.0.14.11", {"start": v(96.01, -79.76) * mm, "end": v(101.1, -79.76) * mm});
            skLineSegment(sketch, "E22.0.14.12", {"start": v(96.01, -74.68) * mm, "end": v(96.01, -79.76) * mm});
            skLineSegment(sketch, "E22.0.14.13", {"start": v(85.34, -79.76) * mm, "end": v(90.42, -79.76) * mm});
            skLineSegment(sketch, "E22.0.14.14", {"start": v(85.1, -74.68) * mm, "end": v(80, -74.68) * mm});
            skLineSegment(sketch, "E22.0.14.15", {"start": v(90.42, -74.68) * mm, "end": v(85.34, -74.68) * mm});
            skLineSegment(sketch, "E22.0.14.16", {"start": v(80, -74.68) * mm, "end": v(80, -79.76) * mm});
            skLineSegment(sketch, "E22.0.14.17", {"start": v(85.34, -74.68) * mm, "end": v(85.34, -79.76) * mm});
            skLineSegment(sketch, "E22.0.14.18", {"start": v(80, -79.76) * mm, "end": v(85.1, -79.76) * mm});
            skLineSegment(sketch, "E22.0.14.19", {"start": v(101.1, -74.68) * mm, "end": v(96.01, -74.68) * mm});
            skLineSegment(sketch, "E22.0.14.20", {"start": v(90.42, -79.76) * mm, "end": v(90.42, -74.68) * mm});
            skLineSegment(sketch, "E22.0.14.21", {"start": v(101.1, -79.76) * mm, "end": v(101.1, -74.68) * mm});
            skLineSegment(sketch, "E22.0.14.22", {"start": v(90.68, -79.76) * mm, "end": v(95.76, -79.76) * mm});
            skLineSegment(sketch, "E22.0.14.23", {"start": v(74.42, -79.76) * mm, "end": v(74.42, -74.68) * mm});
            skLineSegment(sketch, "E22.0.14.24", {"start": v(90.68, -74.68) * mm, "end": v(90.68, -79.76) * mm});
            skLineSegment(sketch, "E22.0.14.25", {"start": v(95.76, -79.76) * mm, "end": v(95.76, -74.68) * mm});
            skLineSegment(sketch, "E22.0.14.26", {"start": v(74.68, -74.68) * mm, "end": v(74.68, -79.76) * mm});
            skLineSegment(sketch, "E22.0.14.27", {"start": v(85.1, -79.76) * mm, "end": v(85.1, -74.68) * mm});
            skLineSegment(sketch, "E22.0.15.0", {"start": v(74.42, -80.01) * mm, "end": v(69.34, -80.01) * mm});
            skLineSegment(sketch, "E22.0.15.1", {"start": v(95.76, -80.01) * mm, "end": v(90.68, -80.01) * mm});
            skLineSegment(sketch, "E22.0.15.2", {"start": v(69.34, -80.01) * mm, "end": v(69.34, -85.1) * mm});
            skLineSegment(sketch, "E22.0.15.3", {"start": v(69.34, -85.1) * mm, "end": v(74.42, -85.1) * mm});
            skLineSegment(sketch, "E22.0.15.4", {"start": v(79.76, -85.1) * mm, "end": v(79.76, -80.01) * mm});
            skLineSegment(sketch, "E22.0.15.5", {"start": v(101.35, -85.1) * mm, "end": v(106.43, -85.1) * mm});
            skLineSegment(sketch, "E22.0.15.6", {"start": v(79.76, -80.01) * mm, "end": v(74.68, -80.01) * mm});
            skLineSegment(sketch, "E22.0.15.7", {"start": v(101.35, -80.01) * mm, "end": v(101.35, -85.1) * mm});
            skLineSegment(sketch, "E22.0.15.8", {"start": v(106.43, -80.01) * mm, "end": v(101.35, -80.01) * mm});
            skLineSegment(sketch, "E22.0.15.9", {"start": v(106.43, -85.1) * mm, "end": v(106.43, -80.01) * mm});
            skLineSegment(sketch, "E22.0.15.10", {"start": v(74.68, -85.1) * mm, "end": v(79.76, -85.1) * mm});
            skLineSegment(sketch, "E22.0.15.11", {"start": v(96.01, -85.1) * mm, "end": v(101.1, -85.1) * mm});
            skLineSegment(sketch, "E22.0.15.12", {"start": v(96.01, -80.01) * mm, "end": v(96.01, -85.1) * mm});
            skLineSegment(sketch, "E22.0.15.13", {"start": v(85.34, -85.1) * mm, "end": v(90.42, -85.1) * mm});
            skLineSegment(sketch, "E22.0.15.14", {"start": v(85.1, -80.01) * mm, "end": v(80, -80.01) * mm});
            skLineSegment(sketch, "E22.0.15.15", {"start": v(90.42, -80.01) * mm, "end": v(85.34, -80.01) * mm});
            skLineSegment(sketch, "E22.0.15.16", {"start": v(80, -80.01) * mm, "end": v(80, -85.1) * mm});
            skLineSegment(sketch, "E22.0.15.17", {"start": v(85.34, -80.01) * mm, "end": v(85.34, -85.1) * mm});
            skLineSegment(sketch, "E22.0.15.18", {"start": v(80, -85.1) * mm, "end": v(85.1, -85.1) * mm});
            skLineSegment(sketch, "E22.0.15.19", {"start": v(101.1, -80.01) * mm, "end": v(96.01, -80.01) * mm});
            skLineSegment(sketch, "E22.0.15.20", {"start": v(90.42, -85.1) * mm, "end": v(90.42, -80.01) * mm});
            skLineSegment(sketch, "E22.0.15.21", {"start": v(101.1, -85.1) * mm, "end": v(101.1, -80.01) * mm});
            skLineSegment(sketch, "E22.0.15.22", {"start": v(90.68, -85.1) * mm, "end": v(95.76, -85.1) * mm});
            skLineSegment(sketch, "E22.0.15.23", {"start": v(74.42, -85.1) * mm, "end": v(74.42, -80.01) * mm});
            skLineSegment(sketch, "E22.0.15.24", {"start": v(90.68, -80.01) * mm, "end": v(90.68, -85.1) * mm});
            skLineSegment(sketch, "E22.0.15.25", {"start": v(95.76, -85.1) * mm, "end": v(95.76, -80.01) * mm});
            skLineSegment(sketch, "E22.0.15.26", {"start": v(74.68, -80.01) * mm, "end": v(74.68, -85.1) * mm});
            skLineSegment(sketch, "E22.0.15.27", {"start": v(85.1, -85.1) * mm, "end": v(85.1, -80.01) * mm});
            skLineSegment(sketch, "E22.0.16.0", {"start": v(74.42, -85.34) * mm, "end": v(69.34, -85.34) * mm});
            skLineSegment(sketch, "E22.0.16.1", {"start": v(95.76, -85.34) * mm, "end": v(90.68, -85.34) * mm});
            skLineSegment(sketch, "E22.0.16.2", {"start": v(69.34, -85.34) * mm, "end": v(69.34, -90.42) * mm});
            skLineSegment(sketch, "E22.0.16.3", {"start": v(69.34, -90.42) * mm, "end": v(74.42, -90.42) * mm});
            skLineSegment(sketch, "E22.0.16.4", {"start": v(79.76, -90.42) * mm, "end": v(79.76, -85.34) * mm});
            skLineSegment(sketch, "E22.0.16.5", {"start": v(101.35, -90.42) * mm, "end": v(106.43, -90.42) * mm});
            skLineSegment(sketch, "E22.0.16.6", {"start": v(79.76, -85.34) * mm, "end": v(74.68, -85.34) * mm});
            skLineSegment(sketch, "E22.0.16.7", {"start": v(101.35, -85.34) * mm, "end": v(101.35, -90.42) * mm});
            skLineSegment(sketch, "E22.0.16.8", {"start": v(106.43, -85.34) * mm, "end": v(101.35, -85.34) * mm});
            skLineSegment(sketch, "E22.0.16.9", {"start": v(106.43, -90.42) * mm, "end": v(106.43, -85.34) * mm});
            skLineSegment(sketch, "E22.0.16.10", {"start": v(74.68, -90.42) * mm, "end": v(79.76, -90.42) * mm});
            skLineSegment(sketch, "E22.0.16.11", {"start": v(96.01, -90.42) * mm, "end": v(101.1, -90.42) * mm});
            skLineSegment(sketch, "E22.0.16.12", {"start": v(96.01, -85.34) * mm, "end": v(96.01, -90.42) * mm});
            skLineSegment(sketch, "E22.0.16.13", {"start": v(85.34, -90.42) * mm, "end": v(90.42, -90.42) * mm});
            skLineSegment(sketch, "E22.0.16.14", {"start": v(85.1, -85.34) * mm, "end": v(80, -85.34) * mm});
            skLineSegment(sketch, "E22.0.16.15", {"start": v(90.42, -85.34) * mm, "end": v(85.34, -85.34) * mm});
            skLineSegment(sketch, "E22.0.16.16", {"start": v(80, -85.34) * mm, "end": v(80, -90.42) * mm});
            skLineSegment(sketch, "E22.0.16.17", {"start": v(85.34, -85.34) * mm, "end": v(85.34, -90.42) * mm});
            skLineSegment(sketch, "E22.0.16.18", {"start": v(80, -90.42) * mm, "end": v(85.1, -90.42) * mm});
            skLineSegment(sketch, "E22.0.16.19", {"start": v(101.1, -85.34) * mm, "end": v(96.01, -85.34) * mm});
            skLineSegment(sketch, "E22.0.16.20", {"start": v(90.42, -90.42) * mm, "end": v(90.42, -85.34) * mm});
            skLineSegment(sketch, "E22.0.16.21", {"start": v(101.1, -90.42) * mm, "end": v(101.1, -85.34) * mm});
            skLineSegment(sketch, "E22.0.16.22", {"start": v(90.68, -90.42) * mm, "end": v(95.76, -90.42) * mm});
            skLineSegment(sketch, "E22.0.16.23", {"start": v(74.42, -90.42) * mm, "end": v(74.42, -85.34) * mm});
            skLineSegment(sketch, "E22.0.16.24", {"start": v(90.68, -85.34) * mm, "end": v(90.68, -90.42) * mm});
            skLineSegment(sketch, "E22.0.16.25", {"start": v(95.76, -90.42) * mm, "end": v(95.76, -85.34) * mm});
            skLineSegment(sketch, "E22.0.16.26", {"start": v(74.68, -85.34) * mm, "end": v(74.68, -90.42) * mm});
            skLineSegment(sketch, "E22.0.16.27", {"start": v(85.1, -90.42) * mm, "end": v(85.1, -85.34) * mm});
            skLineSegment(sketch, "E22.0.17.0", {"start": v(74.42, -90.68) * mm, "end": v(69.34, -90.68) * mm});
            skLineSegment(sketch, "E22.0.17.1", {"start": v(95.76, -90.68) * mm, "end": v(90.68, -90.68) * mm});
            skLineSegment(sketch, "E22.0.17.2", {"start": v(69.34, -90.68) * mm, "end": v(69.34, -95.76) * mm});
            skLineSegment(sketch, "E22.0.17.3", {"start": v(69.34, -95.76) * mm, "end": v(74.42, -95.76) * mm});
            skLineSegment(sketch, "E22.0.17.4", {"start": v(79.76, -95.76) * mm, "end": v(79.76, -90.68) * mm});
            skLineSegment(sketch, "E22.0.17.5", {"start": v(101.35, -95.76) * mm, "end": v(106.43, -95.76) * mm});
            skLineSegment(sketch, "E22.0.17.6", {"start": v(79.76, -90.68) * mm, "end": v(74.68, -90.68) * mm});
            skLineSegment(sketch, "E22.0.17.7", {"start": v(101.35, -90.68) * mm, "end": v(101.35, -95.76) * mm});
            skLineSegment(sketch, "E22.0.17.8", {"start": v(106.43, -90.68) * mm, "end": v(101.35, -90.68) * mm});
            skLineSegment(sketch, "E22.0.17.9", {"start": v(106.43, -95.76) * mm, "end": v(106.43, -90.68) * mm});
            skLineSegment(sketch, "E22.0.17.10", {"start": v(74.68, -95.76) * mm, "end": v(79.76, -95.76) * mm});
            skLineSegment(sketch, "E22.0.17.11", {"start": v(96.01, -95.76) * mm, "end": v(101.1, -95.76) * mm});
            skLineSegment(sketch, "E22.0.17.12", {"start": v(96.01, -90.68) * mm, "end": v(96.01, -95.76) * mm});
            skLineSegment(sketch, "E22.0.17.13", {"start": v(85.34, -95.76) * mm, "end": v(90.42, -95.76) * mm});
            skLineSegment(sketch, "E22.0.17.14", {"start": v(85.1, -90.68) * mm, "end": v(80, -90.68) * mm});
            skLineSegment(sketch, "E22.0.17.15", {"start": v(90.42, -90.68) * mm, "end": v(85.34, -90.68) * mm});
            skLineSegment(sketch, "E22.0.17.16", {"start": v(80, -90.68) * mm, "end": v(80, -95.76) * mm});
            skLineSegment(sketch, "E22.0.17.17", {"start": v(85.34, -90.68) * mm, "end": v(85.34, -95.76) * mm});
            skLineSegment(sketch, "E22.0.17.18", {"start": v(80, -95.76) * mm, "end": v(85.1, -95.76) * mm});
            skLineSegment(sketch, "E22.0.17.19", {"start": v(101.1, -90.68) * mm, "end": v(96.01, -90.68) * mm});
            skLineSegment(sketch, "E22.0.17.20", {"start": v(90.42, -95.76) * mm, "end": v(90.42, -90.68) * mm});
            skLineSegment(sketch, "E22.0.17.21", {"start": v(101.1, -95.76) * mm, "end": v(101.1, -90.68) * mm});
            skLineSegment(sketch, "E22.0.17.22", {"start": v(90.68, -95.76) * mm, "end": v(95.76, -95.76) * mm});
            skLineSegment(sketch, "E22.0.17.23", {"start": v(74.42, -95.76) * mm, "end": v(74.42, -90.68) * mm});
            skLineSegment(sketch, "E22.0.17.24", {"start": v(90.68, -90.68) * mm, "end": v(90.68, -95.76) * mm});
            skLineSegment(sketch, "E22.0.17.25", {"start": v(95.76, -95.76) * mm, "end": v(95.76, -90.68) * mm});
            skLineSegment(sketch, "E22.0.17.26", {"start": v(74.68, -90.68) * mm, "end": v(74.68, -95.76) * mm});
            skLineSegment(sketch, "E22.0.17.27", {"start": v(85.1, -95.76) * mm, "end": v(85.1, -90.68) * mm});
            skLineSegment(sketch, "E22.0.18.0", {"start": v(74.42, -96.01) * mm, "end": v(69.34, -96.01) * mm});
            skLineSegment(sketch, "E22.0.18.1", {"start": v(95.76, -96.01) * mm, "end": v(90.68, -96.01) * mm});
            skLineSegment(sketch, "E22.0.18.2", {"start": v(69.34, -96.01) * mm, "end": v(69.34, -101.1) * mm});
            skLineSegment(sketch, "E22.0.18.3", {"start": v(69.34, -101.1) * mm, "end": v(74.42, -101.1) * mm});
            skLineSegment(sketch, "E22.0.18.4", {"start": v(79.76, -101.1) * mm, "end": v(79.76, -96.01) * mm});
            skLineSegment(sketch, "E22.0.18.5", {"start": v(101.35, -101.1) * mm, "end": v(106.43, -101.1) * mm});
            skLineSegment(sketch, "E22.0.18.6", {"start": v(79.76, -96.01) * mm, "end": v(74.68, -96.01) * mm});
            skLineSegment(sketch, "E22.0.18.7", {"start": v(101.35, -96.01) * mm, "end": v(101.35, -101.1) * mm});
            skLineSegment(sketch, "E22.0.18.8", {"start": v(106.43, -96.01) * mm, "end": v(101.35, -96.01) * mm});
            skLineSegment(sketch, "E22.0.18.9", {"start": v(106.43, -101.1) * mm, "end": v(106.43, -96.01) * mm});
            skLineSegment(sketch, "E22.0.18.10", {"start": v(74.68, -101.1) * mm, "end": v(79.76, -101.1) * mm});
            skLineSegment(sketch, "E22.0.18.11", {"start": v(96.01, -101.1) * mm, "end": v(101.1, -101.1) * mm});
            skLineSegment(sketch, "E22.0.18.12", {"start": v(96.01, -96.01) * mm, "end": v(96.01, -101.1) * mm});
            skLineSegment(sketch, "E22.0.18.13", {"start": v(85.34, -101.1) * mm, "end": v(90.42, -101.1) * mm});
            skLineSegment(sketch, "E22.0.18.14", {"start": v(85.1, -96.01) * mm, "end": v(80, -96.01) * mm});
            skLineSegment(sketch, "E22.0.18.15", {"start": v(90.42, -96.01) * mm, "end": v(85.34, -96.01) * mm});
            skLineSegment(sketch, "E22.0.18.16", {"start": v(80, -96.01) * mm, "end": v(80, -101.1) * mm});
            skLineSegment(sketch, "E22.0.18.17", {"start": v(85.34, -96.01) * mm, "end": v(85.34, -101.1) * mm});
            skLineSegment(sketch, "E22.0.18.18", {"start": v(80, -101.1) * mm, "end": v(85.1, -101.1) * mm});
            skLineSegment(sketch, "E22.0.18.19", {"start": v(101.1, -96.01) * mm, "end": v(96.01, -96.01) * mm});
            skLineSegment(sketch, "E22.0.18.20", {"start": v(90.42, -101.1) * mm, "end": v(90.42, -96.01) * mm});
            skLineSegment(sketch, "E22.0.18.21", {"start": v(101.1, -101.1) * mm, "end": v(101.1, -96.01) * mm});
            skLineSegment(sketch, "E22.0.18.22", {"start": v(90.68, -101.1) * mm, "end": v(95.76, -101.1) * mm});
            skLineSegment(sketch, "E22.0.18.23", {"start": v(74.42, -101.1) * mm, "end": v(74.42, -96.01) * mm});
            skLineSegment(sketch, "E22.0.18.24", {"start": v(90.68, -96.01) * mm, "end": v(90.68, -101.1) * mm});
            skLineSegment(sketch, "E22.0.18.25", {"start": v(95.76, -101.1) * mm, "end": v(95.76, -96.01) * mm});
            skLineSegment(sketch, "E22.0.18.26", {"start": v(74.68, -96.01) * mm, "end": v(74.68, -101.1) * mm});
            skLineSegment(sketch, "E22.0.18.27", {"start": v(85.1, -101.1) * mm, "end": v(85.1, -96.01) * mm});
            skLineSegment(sketch, "E22.0.19.0", {"start": v(74.42, -101.35) * mm, "end": v(69.34, -101.35) * mm});
            skLineSegment(sketch, "E22.0.19.1", {"start": v(95.76, -101.35) * mm, "end": v(90.68, -101.35) * mm});
            skLineSegment(sketch, "E22.0.19.2", {"start": v(69.34, -101.35) * mm, "end": v(69.34, -106.43) * mm});
            skLineSegment(sketch, "E22.0.19.3", {"start": v(69.34, -106.43) * mm, "end": v(74.42, -106.43) * mm});
            skLineSegment(sketch, "E22.0.19.4", {"start": v(79.76, -106.43) * mm, "end": v(79.76, -101.35) * mm});
            skLineSegment(sketch, "E22.0.19.5", {"start": v(101.35, -106.43) * mm, "end": v(106.43, -106.43) * mm});
            skLineSegment(sketch, "E22.0.19.6", {"start": v(79.76, -101.35) * mm, "end": v(74.68, -101.35) * mm});
            skLineSegment(sketch, "E22.0.19.7", {"start": v(101.35, -101.35) * mm, "end": v(101.35, -106.43) * mm});
            skLineSegment(sketch, "E22.0.19.8", {"start": v(106.43, -101.35) * mm, "end": v(101.35, -101.35) * mm});
            skLineSegment(sketch, "E22.0.19.9", {"start": v(106.43, -106.43) * mm, "end": v(106.43, -101.35) * mm});
            skLineSegment(sketch, "E22.0.19.10", {"start": v(74.68, -106.43) * mm, "end": v(79.76, -106.43) * mm});
            skLineSegment(sketch, "E22.0.19.11", {"start": v(96.01, -106.43) * mm, "end": v(101.1, -106.43) * mm});
            skLineSegment(sketch, "E22.0.19.12", {"start": v(96.01, -101.35) * mm, "end": v(96.01, -106.43) * mm});
            skLineSegment(sketch, "E22.0.19.13", {"start": v(85.34, -106.43) * mm, "end": v(90.42, -106.43) * mm});
            skLineSegment(sketch, "E22.0.19.14", {"start": v(85.1, -101.35) * mm, "end": v(80, -101.35) * mm});
            skLineSegment(sketch, "E22.0.19.15", {"start": v(90.42, -101.35) * mm, "end": v(85.34, -101.35) * mm});
            skLineSegment(sketch, "E22.0.19.16", {"start": v(80, -101.35) * mm, "end": v(80, -106.43) * mm});
            skLineSegment(sketch, "E22.0.19.17", {"start": v(85.34, -101.35) * mm, "end": v(85.34, -106.43) * mm});
            skLineSegment(sketch, "E22.0.19.18", {"start": v(80, -106.43) * mm, "end": v(85.1, -106.43) * mm});
            skLineSegment(sketch, "E22.0.19.19", {"start": v(101.1, -101.35) * mm, "end": v(96.01, -101.35) * mm});
            skLineSegment(sketch, "E22.0.19.20", {"start": v(90.42, -106.43) * mm, "end": v(90.42, -101.35) * mm});
            skLineSegment(sketch, "E22.0.19.21", {"start": v(101.1, -106.43) * mm, "end": v(101.1, -101.35) * mm});
            skLineSegment(sketch, "E22.0.19.22", {"start": v(90.68, -106.43) * mm, "end": v(95.76, -106.43) * mm});
            skLineSegment(sketch, "E22.0.19.23", {"start": v(74.42, -106.43) * mm, "end": v(74.42, -101.35) * mm});
            skLineSegment(sketch, "E22.0.19.24", {"start": v(90.68, -101.35) * mm, "end": v(90.68, -106.43) * mm});
            skLineSegment(sketch, "E22.0.19.25", {"start": v(95.76, -106.43) * mm, "end": v(95.76, -101.35) * mm});
            skLineSegment(sketch, "E22.0.19.26", {"start": v(74.68, -101.35) * mm, "end": v(74.68, -106.43) * mm});
            skLineSegment(sketch, "E22.0.19.27", {"start": v(85.1, -106.43) * mm, "end": v(85.1, -101.35) * mm});
            skLineSegment(sketch, "E22.0.20.0", {"start": v(74.42, -106.68) * mm, "end": v(69.34, -106.68) * mm});
            skLineSegment(sketch, "E22.0.20.1", {"start": v(95.76, -106.68) * mm, "end": v(90.68, -106.68) * mm});
            skLineSegment(sketch, "E22.0.20.2", {"start": v(69.34, -106.68) * mm, "end": v(69.34, -111.76) * mm});
            skLineSegment(sketch, "E22.0.20.3", {"start": v(69.34, -111.76) * mm, "end": v(74.42, -111.76) * mm});
            skLineSegment(sketch, "E22.0.20.4", {"start": v(79.76, -111.76) * mm, "end": v(79.76, -106.68) * mm});
            skLineSegment(sketch, "E22.0.20.5", {"start": v(101.35, -111.76) * mm, "end": v(106.43, -111.76) * mm});
            skLineSegment(sketch, "E22.0.20.6", {"start": v(79.76, -106.68) * mm, "end": v(74.68, -106.68) * mm});
            skLineSegment(sketch, "E22.0.20.7", {"start": v(101.35, -106.68) * mm, "end": v(101.35, -111.76) * mm});
            skLineSegment(sketch, "E22.0.20.8", {"start": v(106.43, -106.68) * mm, "end": v(101.35, -106.68) * mm});
            skLineSegment(sketch, "E22.0.20.9", {"start": v(106.43, -111.76) * mm, "end": v(106.43, -106.68) * mm});
            skLineSegment(sketch, "E22.0.20.10", {"start": v(74.68, -111.76) * mm, "end": v(79.76, -111.76) * mm});
            skLineSegment(sketch, "E22.0.20.11", {"start": v(96.01, -111.76) * mm, "end": v(101.1, -111.76) * mm});
            skLineSegment(sketch, "E22.0.20.12", {"start": v(96.01, -106.68) * mm, "end": v(96.01, -111.76) * mm});
            skLineSegment(sketch, "E22.0.20.13", {"start": v(85.34, -111.76) * mm, "end": v(90.42, -111.76) * mm});
            skLineSegment(sketch, "E22.0.20.14", {"start": v(85.1, -106.68) * mm, "end": v(80, -106.68) * mm});
            skLineSegment(sketch, "E22.0.20.15", {"start": v(90.42, -106.68) * mm, "end": v(85.34, -106.68) * mm});
            skLineSegment(sketch, "E22.0.20.16", {"start": v(80, -106.68) * mm, "end": v(80, -111.76) * mm});
            skLineSegment(sketch, "E22.0.20.17", {"start": v(85.34, -106.68) * mm, "end": v(85.34, -111.76) * mm});
            skLineSegment(sketch, "E22.0.20.18", {"start": v(80, -111.76) * mm, "end": v(85.1, -111.76) * mm});
            skLineSegment(sketch, "E22.0.20.19", {"start": v(101.1, -106.68) * mm, "end": v(96.01, -106.68) * mm});
            skLineSegment(sketch, "E22.0.20.20", {"start": v(90.42, -111.76) * mm, "end": v(90.42, -106.68) * mm});
            skLineSegment(sketch, "E22.0.20.21", {"start": v(101.1, -111.76) * mm, "end": v(101.1, -106.68) * mm});
            skLineSegment(sketch, "E22.0.20.22", {"start": v(90.68, -111.76) * mm, "end": v(95.76, -111.76) * mm});
            skLineSegment(sketch, "E22.0.20.23", {"start": v(74.42, -111.76) * mm, "end": v(74.42, -106.68) * mm});
            skLineSegment(sketch, "E22.0.20.24", {"start": v(90.68, -106.68) * mm, "end": v(90.68, -111.76) * mm});
            skLineSegment(sketch, "E22.0.20.25", {"start": v(95.76, -111.76) * mm, "end": v(95.76, -106.68) * mm});
            skLineSegment(sketch, "E22.0.20.26", {"start": v(74.68, -106.68) * mm, "end": v(74.68, -111.76) * mm});
            skLineSegment(sketch, "E22.0.20.27", {"start": v(85.1, -111.76) * mm, "end": v(85.1, -106.68) * mm});
            skLineSegment(sketch, "E22.0.21.0", {"start": v(74.42, -112.01) * mm, "end": v(69.34, -112.01) * mm});
            skLineSegment(sketch, "E22.0.21.1", {"start": v(95.76, -112.01) * mm, "end": v(90.68, -112.01) * mm});
            skLineSegment(sketch, "E22.0.21.2", {"start": v(69.34, -112.01) * mm, "end": v(69.34, -117.1) * mm});
            skLineSegment(sketch, "E22.0.21.3", {"start": v(69.34, -117.1) * mm, "end": v(74.42, -117.1) * mm});
            skLineSegment(sketch, "E22.0.21.4", {"start": v(79.76, -117.1) * mm, "end": v(79.76, -112.01) * mm});
            skLineSegment(sketch, "E22.0.21.5", {"start": v(101.35, -117.1) * mm, "end": v(106.43, -117.1) * mm});
            skLineSegment(sketch, "E22.0.21.6", {"start": v(79.76, -112.01) * mm, "end": v(74.68, -112.01) * mm});
            skLineSegment(sketch, "E22.0.21.7", {"start": v(101.35, -112.01) * mm, "end": v(101.35, -117.1) * mm});
            skLineSegment(sketch, "E22.0.21.8", {"start": v(106.43, -112.01) * mm, "end": v(101.35, -112.01) * mm});
            skLineSegment(sketch, "E22.0.21.9", {"start": v(106.43, -117.1) * mm, "end": v(106.43, -112.01) * mm});
            skLineSegment(sketch, "E22.0.21.10", {"start": v(74.68, -117.1) * mm, "end": v(79.76, -117.1) * mm});
            skLineSegment(sketch, "E22.0.21.11", {"start": v(96.01, -117.1) * mm, "end": v(101.1, -117.1) * mm});
            skLineSegment(sketch, "E22.0.21.12", {"start": v(96.01, -112.01) * mm, "end": v(96.01, -117.1) * mm});
            skLineSegment(sketch, "E22.0.21.13", {"start": v(85.34, -117.1) * mm, "end": v(90.42, -117.1) * mm});
            skLineSegment(sketch, "E22.0.21.14", {"start": v(85.1, -112.01) * mm, "end": v(80, -112.01) * mm});
            skLineSegment(sketch, "E22.0.21.15", {"start": v(90.42, -112.01) * mm, "end": v(85.34, -112.01) * mm});
            skLineSegment(sketch, "E22.0.21.16", {"start": v(80, -112.01) * mm, "end": v(80, -117.1) * mm});
            skLineSegment(sketch, "E22.0.21.17", {"start": v(85.34, -112.01) * mm, "end": v(85.34, -117.1) * mm});
            skLineSegment(sketch, "E22.0.21.18", {"start": v(80, -117.1) * mm, "end": v(85.1, -117.1) * mm});
            skLineSegment(sketch, "E22.0.21.19", {"start": v(101.1, -112.01) * mm, "end": v(96.01, -112.01) * mm});
            skLineSegment(sketch, "E22.0.21.20", {"start": v(90.42, -117.1) * mm, "end": v(90.42, -112.01) * mm});
            skLineSegment(sketch, "E22.0.21.21", {"start": v(101.1, -117.1) * mm, "end": v(101.1, -112.01) * mm});
            skLineSegment(sketch, "E22.0.21.22", {"start": v(90.68, -117.1) * mm, "end": v(95.76, -117.1) * mm});
            skLineSegment(sketch, "E22.0.21.23", {"start": v(74.42, -117.1) * mm, "end": v(74.42, -112.01) * mm});
            skLineSegment(sketch, "E22.0.21.24", {"start": v(90.68, -112.01) * mm, "end": v(90.68, -117.1) * mm});
            skLineSegment(sketch, "E22.0.21.25", {"start": v(95.76, -117.1) * mm, "end": v(95.76, -112.01) * mm});
            skLineSegment(sketch, "E22.0.21.26", {"start": v(74.68, -112.01) * mm, "end": v(74.68, -117.1) * mm});
            skLineSegment(sketch, "E22.0.21.27", {"start": v(85.1, -117.1) * mm, "end": v(85.1, -112.01) * mm});
            skLineSegment(sketch, "E22.0.22.0", {"start": v(74.42, -117.35) * mm, "end": v(69.34, -117.35) * mm});
            skLineSegment(sketch, "E22.0.22.1", {"start": v(95.76, -117.35) * mm, "end": v(90.68, -117.35) * mm});
            skLineSegment(sketch, "E22.0.22.2", {"start": v(69.34, -117.35) * mm, "end": v(69.34, -122.43) * mm});
            skLineSegment(sketch, "E22.0.22.3", {"start": v(69.34, -122.43) * mm, "end": v(74.42, -122.43) * mm});
            skLineSegment(sketch, "E22.0.22.4", {"start": v(79.76, -122.43) * mm, "end": v(79.76, -117.35) * mm});
            skLineSegment(sketch, "E22.0.22.5", {"start": v(101.35, -122.43) * mm, "end": v(106.43, -122.43) * mm});
            skLineSegment(sketch, "E22.0.22.6", {"start": v(79.76, -117.35) * mm, "end": v(74.68, -117.35) * mm});
            skLineSegment(sketch, "E22.0.22.7", {"start": v(101.35, -117.35) * mm, "end": v(101.35, -122.43) * mm});
            skLineSegment(sketch, "E22.0.22.8", {"start": v(106.43, -117.35) * mm, "end": v(101.35, -117.35) * mm});
            skLineSegment(sketch, "E22.0.22.9", {"start": v(106.43, -122.43) * mm, "end": v(106.43, -117.35) * mm});
            skLineSegment(sketch, "E22.0.22.10", {"start": v(74.68, -122.43) * mm, "end": v(79.76, -122.43) * mm});
            skLineSegment(sketch, "E22.0.22.11", {"start": v(96.01, -122.43) * mm, "end": v(101.1, -122.43) * mm});
            skLineSegment(sketch, "E22.0.22.12", {"start": v(96.01, -117.35) * mm, "end": v(96.01, -122.43) * mm});
            skLineSegment(sketch, "E22.0.22.13", {"start": v(85.34, -122.43) * mm, "end": v(90.42, -122.43) * mm});
            skLineSegment(sketch, "E22.0.22.14", {"start": v(85.1, -117.35) * mm, "end": v(80, -117.35) * mm});
            skLineSegment(sketch, "E22.0.22.15", {"start": v(90.42, -117.35) * mm, "end": v(85.34, -117.35) * mm});
            skLineSegment(sketch, "E22.0.22.16", {"start": v(80, -117.35) * mm, "end": v(80, -122.43) * mm});
            skLineSegment(sketch, "E22.0.22.17", {"start": v(85.34, -117.35) * mm, "end": v(85.34, -122.43) * mm});
            skLineSegment(sketch, "E22.0.22.18", {"start": v(80, -122.43) * mm, "end": v(85.1, -122.43) * mm});
            skLineSegment(sketch, "E22.0.22.19", {"start": v(101.1, -117.35) * mm, "end": v(96.01, -117.35) * mm});
            skLineSegment(sketch, "E22.0.22.20", {"start": v(90.42, -122.43) * mm, "end": v(90.42, -117.35) * mm});
            skLineSegment(sketch, "E22.0.22.21", {"start": v(101.1, -122.43) * mm, "end": v(101.1, -117.35) * mm});
            skLineSegment(sketch, "E22.0.22.22", {"start": v(90.68, -122.43) * mm, "end": v(95.76, -122.43) * mm});
            skLineSegment(sketch, "E22.0.22.23", {"start": v(74.42, -122.43) * mm, "end": v(74.42, -117.35) * mm});
            skLineSegment(sketch, "E22.0.22.24", {"start": v(90.68, -117.35) * mm, "end": v(90.68, -122.43) * mm});
            skLineSegment(sketch, "E22.0.22.25", {"start": v(95.76, -122.43) * mm, "end": v(95.76, -117.35) * mm});
            skLineSegment(sketch, "E22.0.22.26", {"start": v(74.68, -117.35) * mm, "end": v(74.68, -122.43) * mm});
            skLineSegment(sketch, "E22.0.22.27", {"start": v(85.1, -122.43) * mm, "end": v(85.1, -117.35) * mm});
            skLineSegment(sketch, "E22.0.23.0", {"start": v(74.42, -122.68) * mm, "end": v(69.34, -122.68) * mm});
            skLineSegment(sketch, "E22.0.23.1", {"start": v(95.76, -122.68) * mm, "end": v(90.68, -122.68) * mm});
            skLineSegment(sketch, "E22.0.23.2", {"start": v(69.34, -122.68) * mm, "end": v(69.34, -127.76) * mm});
            skLineSegment(sketch, "E22.0.23.3", {"start": v(69.34, -127.76) * mm, "end": v(74.42, -127.76) * mm});
            skLineSegment(sketch, "E22.0.23.4", {"start": v(79.76, -127.76) * mm, "end": v(79.76, -122.68) * mm});
            skLineSegment(sketch, "E22.0.23.5", {"start": v(101.35, -127.76) * mm, "end": v(106.43, -127.76) * mm});
            skLineSegment(sketch, "E22.0.23.6", {"start": v(79.76, -122.68) * mm, "end": v(74.68, -122.68) * mm});
            skLineSegment(sketch, "E22.0.23.7", {"start": v(101.35, -122.68) * mm, "end": v(101.35, -127.76) * mm});
            skLineSegment(sketch, "E22.0.23.8", {"start": v(106.43, -122.68) * mm, "end": v(101.35, -122.68) * mm});
            skLineSegment(sketch, "E22.0.23.9", {"start": v(106.43, -127.76) * mm, "end": v(106.43, -122.68) * mm});
            skLineSegment(sketch, "E22.0.23.10", {"start": v(74.68, -127.76) * mm, "end": v(79.76, -127.76) * mm});
            skLineSegment(sketch, "E22.0.23.11", {"start": v(96.01, -127.76) * mm, "end": v(101.1, -127.76) * mm});
            skLineSegment(sketch, "E22.0.23.12", {"start": v(96.01, -122.68) * mm, "end": v(96.01, -127.76) * mm});
            skLineSegment(sketch, "E22.0.23.13", {"start": v(85.34, -127.76) * mm, "end": v(90.42, -127.76) * mm});
            skLineSegment(sketch, "E22.0.23.14", {"start": v(85.1, -122.68) * mm, "end": v(80, -122.68) * mm});
            skLineSegment(sketch, "E22.0.23.15", {"start": v(90.42, -122.68) * mm, "end": v(85.34, -122.68) * mm});
            skLineSegment(sketch, "E22.0.23.16", {"start": v(80, -122.68) * mm, "end": v(80, -127.76) * mm});
            skLineSegment(sketch, "E22.0.23.17", {"start": v(85.34, -122.68) * mm, "end": v(85.34, -127.76) * mm});
            skLineSegment(sketch, "E22.0.23.18", {"start": v(80, -127.76) * mm, "end": v(85.1, -127.76) * mm});
            skLineSegment(sketch, "E22.0.23.19", {"start": v(101.1, -122.68) * mm, "end": v(96.01, -122.68) * mm});
            skLineSegment(sketch, "E22.0.23.20", {"start": v(90.42, -127.76) * mm, "end": v(90.42, -122.68) * mm});
            skLineSegment(sketch, "E22.0.23.21", {"start": v(101.1, -127.76) * mm, "end": v(101.1, -122.68) * mm});
            skLineSegment(sketch, "E22.0.23.22", {"start": v(90.68, -127.76) * mm, "end": v(95.76, -127.76) * mm});
            skLineSegment(sketch, "E22.0.23.23", {"start": v(74.42, -127.76) * mm, "end": v(74.42, -122.68) * mm});
            skLineSegment(sketch, "E22.0.23.24", {"start": v(90.68, -122.68) * mm, "end": v(90.68, -127.76) * mm});
            skLineSegment(sketch, "E22.0.23.25", {"start": v(95.76, -127.76) * mm, "end": v(95.76, -122.68) * mm});
            skLineSegment(sketch, "E22.0.23.26", {"start": v(74.68, -122.68) * mm, "end": v(74.68, -127.76) * mm});
            skLineSegment(sketch, "E22.0.23.27", {"start": v(85.1, -127.76) * mm, "end": v(85.1, -122.68) * mm});
            skLineSegment(sketch, "E22.0.24.0", {"start": v(74.42, -128.02) * mm, "end": v(69.34, -128.02) * mm});
            skLineSegment(sketch, "E22.0.24.1", {"start": v(95.76, -128.02) * mm, "end": v(90.68, -128.02) * mm});
            skLineSegment(sketch, "E22.0.24.2", {"start": v(69.34, -128.02) * mm, "end": v(69.34, -133.1) * mm});
            skLineSegment(sketch, "E22.0.24.3", {"start": v(69.34, -133.1) * mm, "end": v(74.42, -133.1) * mm});
            skLineSegment(sketch, "E22.0.24.4", {"start": v(79.76, -133.1) * mm, "end": v(79.76, -128.02) * mm});
            skLineSegment(sketch, "E22.0.24.5", {"start": v(101.35, -133.1) * mm, "end": v(106.43, -133.1) * mm});
            skLineSegment(sketch, "E22.0.24.6", {"start": v(79.76, -128.02) * mm, "end": v(74.68, -128.02) * mm});
            skLineSegment(sketch, "E22.0.24.7", {"start": v(101.35, -128.02) * mm, "end": v(101.35, -133.1) * mm});
            skLineSegment(sketch, "E22.0.24.8", {"start": v(106.43, -128.02) * mm, "end": v(101.35, -128.02) * mm});
            skLineSegment(sketch, "E22.0.24.9", {"start": v(106.43, -133.1) * mm, "end": v(106.43, -128.02) * mm});
            skLineSegment(sketch, "E22.0.24.10", {"start": v(74.68, -133.1) * mm, "end": v(79.76, -133.1) * mm});
            skLineSegment(sketch, "E22.0.24.11", {"start": v(96.01, -133.1) * mm, "end": v(101.1, -133.1) * mm});
            skLineSegment(sketch, "E22.0.24.12", {"start": v(96.01, -128.02) * mm, "end": v(96.01, -133.1) * mm});
            skLineSegment(sketch, "E22.0.24.13", {"start": v(85.34, -133.1) * mm, "end": v(90.42, -133.1) * mm});
            skLineSegment(sketch, "E22.0.24.14", {"start": v(85.1, -128.02) * mm, "end": v(80, -128.02) * mm});
            skLineSegment(sketch, "E22.0.24.15", {"start": v(90.42, -128.02) * mm, "end": v(85.34, -128.02) * mm});
            skLineSegment(sketch, "E22.0.24.16", {"start": v(80, -128.02) * mm, "end": v(80, -133.1) * mm});
            skLineSegment(sketch, "E22.0.24.17", {"start": v(85.34, -128.02) * mm, "end": v(85.34, -133.1) * mm});
            skLineSegment(sketch, "E22.0.24.18", {"start": v(80, -133.1) * mm, "end": v(85.1, -133.1) * mm});
            skLineSegment(sketch, "E22.0.24.19", {"start": v(101.1, -128.02) * mm, "end": v(96.01, -128.02) * mm});
            skLineSegment(sketch, "E22.0.24.20", {"start": v(90.42, -133.1) * mm, "end": v(90.42, -128.02) * mm});
            skLineSegment(sketch, "E22.0.24.21", {"start": v(101.1, -133.1) * mm, "end": v(101.1, -128.02) * mm});
            skLineSegment(sketch, "E22.0.24.22", {"start": v(90.68, -133.1) * mm, "end": v(95.76, -133.1) * mm});
            skLineSegment(sketch, "E22.0.24.23", {"start": v(74.42, -133.1) * mm, "end": v(74.42, -128.02) * mm});
            skLineSegment(sketch, "E22.0.24.24", {"start": v(90.68, -128.02) * mm, "end": v(90.68, -133.1) * mm});
            skLineSegment(sketch, "E22.0.24.25", {"start": v(95.76, -133.1) * mm, "end": v(95.76, -128.02) * mm});
            skLineSegment(sketch, "E22.0.24.26", {"start": v(74.68, -128.02) * mm, "end": v(74.68, -133.1) * mm});
            skLineSegment(sketch, "E22.0.24.27", {"start": v(85.1, -133.1) * mm, "end": v(85.1, -128.02) * mm});
            skLineSegment(sketch, "E22.0.25.0", {"start": v(74.42, -133.35) * mm, "end": v(69.34, -133.35) * mm});
            skLineSegment(sketch, "E22.0.25.1", {"start": v(95.76, -133.35) * mm, "end": v(90.68, -133.35) * mm});
            skLineSegment(sketch, "E22.0.25.2", {"start": v(69.34, -133.35) * mm, "end": v(69.34, -138.43) * mm});
            skLineSegment(sketch, "E22.0.25.3", {"start": v(69.34, -138.43) * mm, "end": v(74.42, -138.43) * mm});
            skLineSegment(sketch, "E22.0.25.4", {"start": v(79.76, -138.43) * mm, "end": v(79.76, -133.35) * mm});
            skLineSegment(sketch, "E22.0.25.5", {"start": v(101.35, -138.43) * mm, "end": v(106.43, -138.43) * mm});
            skLineSegment(sketch, "E22.0.25.6", {"start": v(79.76, -133.35) * mm, "end": v(74.68, -133.35) * mm});
            skLineSegment(sketch, "E22.0.25.7", {"start": v(101.35, -133.35) * mm, "end": v(101.35, -138.43) * mm});
            skLineSegment(sketch, "E22.0.25.8", {"start": v(106.43, -133.35) * mm, "end": v(101.35, -133.35) * mm});
            skLineSegment(sketch, "E22.0.25.9", {"start": v(106.43, -138.43) * mm, "end": v(106.43, -133.35) * mm});
            skLineSegment(sketch, "E22.0.25.10", {"start": v(74.68, -138.43) * mm, "end": v(79.76, -138.43) * mm});
            skLineSegment(sketch, "E22.0.25.11", {"start": v(96.01, -138.43) * mm, "end": v(101.1, -138.43) * mm});
            skLineSegment(sketch, "E22.0.25.12", {"start": v(96.01, -133.35) * mm, "end": v(96.01, -138.43) * mm});
            skLineSegment(sketch, "E22.0.25.13", {"start": v(85.34, -138.43) * mm, "end": v(90.42, -138.43) * mm});
            skLineSegment(sketch, "E22.0.25.14", {"start": v(85.1, -133.35) * mm, "end": v(80, -133.35) * mm});
            skLineSegment(sketch, "E22.0.25.15", {"start": v(90.42, -133.35) * mm, "end": v(85.34, -133.35) * mm});
            skLineSegment(sketch, "E22.0.25.16", {"start": v(80, -133.35) * mm, "end": v(80, -138.43) * mm});
            skLineSegment(sketch, "E22.0.25.17", {"start": v(85.34, -133.35) * mm, "end": v(85.34, -138.43) * mm});
            skLineSegment(sketch, "E22.0.25.18", {"start": v(80, -138.43) * mm, "end": v(85.1, -138.43) * mm});
            skLineSegment(sketch, "E22.0.25.19", {"start": v(101.1, -133.35) * mm, "end": v(96.01, -133.35) * mm});
            skLineSegment(sketch, "E22.0.25.20", {"start": v(90.42, -138.43) * mm, "end": v(90.42, -133.35) * mm});
            skLineSegment(sketch, "E22.0.25.21", {"start": v(101.1, -138.43) * mm, "end": v(101.1, -133.35) * mm});
            skLineSegment(sketch, "E22.0.25.22", {"start": v(90.68, -138.43) * mm, "end": v(95.76, -138.43) * mm});
            skLineSegment(sketch, "E22.0.25.23", {"start": v(74.42, -138.43) * mm, "end": v(74.42, -133.35) * mm});
            skLineSegment(sketch, "E22.0.25.24", {"start": v(90.68, -133.35) * mm, "end": v(90.68, -138.43) * mm});
            skLineSegment(sketch, "E22.0.25.25", {"start": v(95.76, -138.43) * mm, "end": v(95.76, -133.35) * mm});
            skLineSegment(sketch, "E22.0.25.26", {"start": v(74.68, -133.35) * mm, "end": v(74.68, -138.43) * mm});
            skLineSegment(sketch, "E22.0.25.27", {"start": v(85.1, -138.43) * mm, "end": v(85.1, -133.35) * mm});
            skLineSegment(sketch, "E22.0.26.0", {"start": v(74.42, -138.68) * mm, "end": v(69.34, -138.68) * mm});
            skLineSegment(sketch, "E22.0.26.1", {"start": v(95.76, -138.68) * mm, "end": v(90.68, -138.68) * mm});
            skLineSegment(sketch, "E22.0.26.2", {"start": v(69.34, -138.68) * mm, "end": v(69.34, -143.76) * mm});
            skLineSegment(sketch, "E22.0.26.3", {"start": v(69.34, -143.76) * mm, "end": v(74.42, -143.76) * mm});
            skLineSegment(sketch, "E22.0.26.4", {"start": v(79.76, -143.76) * mm, "end": v(79.76, -138.68) * mm});
            skLineSegment(sketch, "E22.0.26.5", {"start": v(101.35, -143.76) * mm, "end": v(106.43, -143.76) * mm});
            skLineSegment(sketch, "E22.0.26.6", {"start": v(79.76, -138.68) * mm, "end": v(74.68, -138.68) * mm});
            skLineSegment(sketch, "E22.0.26.7", {"start": v(101.35, -138.68) * mm, "end": v(101.35, -143.76) * mm});
            skLineSegment(sketch, "E22.0.26.8", {"start": v(106.43, -138.68) * mm, "end": v(101.35, -138.68) * mm});
            skLineSegment(sketch, "E22.0.26.9", {"start": v(106.43, -143.76) * mm, "end": v(106.43, -138.68) * mm});
            skLineSegment(sketch, "E22.0.26.10", {"start": v(74.68, -143.76) * mm, "end": v(79.76, -143.76) * mm});
            skLineSegment(sketch, "E22.0.26.11", {"start": v(96.01, -143.76) * mm, "end": v(101.1, -143.76) * mm});
            skLineSegment(sketch, "E22.0.26.12", {"start": v(96.01, -138.68) * mm, "end": v(96.01, -143.76) * mm});
            skLineSegment(sketch, "E22.0.26.13", {"start": v(85.34, -143.76) * mm, "end": v(90.42, -143.76) * mm});
            skLineSegment(sketch, "E22.0.26.14", {"start": v(85.1, -138.68) * mm, "end": v(80, -138.68) * mm});
            skLineSegment(sketch, "E22.0.26.15", {"start": v(90.42, -138.68) * mm, "end": v(85.34, -138.68) * mm});
            skLineSegment(sketch, "E22.0.26.16", {"start": v(80, -138.68) * mm, "end": v(80, -143.76) * mm});
            skLineSegment(sketch, "E22.0.26.17", {"start": v(85.34, -138.68) * mm, "end": v(85.34, -143.76) * mm});
            skLineSegment(sketch, "E22.0.26.18", {"start": v(80, -143.76) * mm, "end": v(85.1, -143.76) * mm});
            skLineSegment(sketch, "E22.0.26.19", {"start": v(101.1, -138.68) * mm, "end": v(96.01, -138.68) * mm});
            skLineSegment(sketch, "E22.0.26.20", {"start": v(90.42, -143.76) * mm, "end": v(90.42, -138.68) * mm});
            skLineSegment(sketch, "E22.0.26.21", {"start": v(101.1, -143.76) * mm, "end": v(101.1, -138.68) * mm});
            skLineSegment(sketch, "E22.0.26.22", {"start": v(90.68, -143.76) * mm, "end": v(95.76, -143.76) * mm});
            skLineSegment(sketch, "E22.0.26.23", {"start": v(74.42, -143.76) * mm, "end": v(74.42, -138.68) * mm});
            skLineSegment(sketch, "E22.0.26.24", {"start": v(90.68, -138.68) * mm, "end": v(90.68, -143.76) * mm});
            skLineSegment(sketch, "E22.0.26.25", {"start": v(95.76, -143.76) * mm, "end": v(95.76, -138.68) * mm});
            skLineSegment(sketch, "E22.0.26.26", {"start": v(74.68, -138.68) * mm, "end": v(74.68, -143.76) * mm});
            skLineSegment(sketch, "E22.0.26.27", {"start": v(85.1, -143.76) * mm, "end": v(85.1, -138.68) * mm});
            skLineSegment(sketch, "E22.0.27.0", {"start": v(74.42, -144.02) * mm, "end": v(69.34, -144.02) * mm});
            skLineSegment(sketch, "E22.0.27.1", {"start": v(95.76, -144.02) * mm, "end": v(90.68, -144.02) * mm});
            skLineSegment(sketch, "E22.0.27.2", {"start": v(69.34, -144.02) * mm, "end": v(69.34, -149.1) * mm});
            skLineSegment(sketch, "E22.0.27.3", {"start": v(69.34, -149.1) * mm, "end": v(74.42, -149.1) * mm});
            skLineSegment(sketch, "E22.0.27.4", {"start": v(79.76, -149.1) * mm, "end": v(79.76, -144.02) * mm});
            skLineSegment(sketch, "E22.0.27.5", {"start": v(101.35, -149.1) * mm, "end": v(106.43, -149.1) * mm});
            skLineSegment(sketch, "E22.0.27.6", {"start": v(79.76, -144.02) * mm, "end": v(74.68, -144.02) * mm});
            skLineSegment(sketch, "E22.0.27.7", {"start": v(101.35, -144.02) * mm, "end": v(101.35, -149.1) * mm});
            skLineSegment(sketch, "E22.0.27.8", {"start": v(106.43, -144.02) * mm, "end": v(101.35, -144.02) * mm});
            skLineSegment(sketch, "E22.0.27.9", {"start": v(106.43, -149.1) * mm, "end": v(106.43, -144.02) * mm});
            skLineSegment(sketch, "E22.0.27.10", {"start": v(74.68, -149.1) * mm, "end": v(79.76, -149.1) * mm});
            skLineSegment(sketch, "E22.0.27.11", {"start": v(96.01, -149.1) * mm, "end": v(101.1, -149.1) * mm});
            skLineSegment(sketch, "E22.0.27.12", {"start": v(96.01, -144.02) * mm, "end": v(96.01, -149.1) * mm});
            skLineSegment(sketch, "E22.0.27.13", {"start": v(85.34, -149.1) * mm, "end": v(90.42, -149.1) * mm});
            skLineSegment(sketch, "E22.0.27.14", {"start": v(85.1, -144.02) * mm, "end": v(80, -144.02) * mm});
            skLineSegment(sketch, "E22.0.27.15", {"start": v(90.42, -144.02) * mm, "end": v(85.34, -144.02) * mm});
            skLineSegment(sketch, "E22.0.27.16", {"start": v(80, -144.02) * mm, "end": v(80, -149.1) * mm});
            skLineSegment(sketch, "E22.0.27.17", {"start": v(85.34, -144.02) * mm, "end": v(85.34, -149.1) * mm});
            skLineSegment(sketch, "E22.0.27.18", {"start": v(80, -149.1) * mm, "end": v(85.1, -149.1) * mm});
            skLineSegment(sketch, "E22.0.27.19", {"start": v(101.1, -144.02) * mm, "end": v(96.01, -144.02) * mm});
            skLineSegment(sketch, "E22.0.27.20", {"start": v(90.42, -149.1) * mm, "end": v(90.42, -144.02) * mm});
            skLineSegment(sketch, "E22.0.27.21", {"start": v(101.1, -149.1) * mm, "end": v(101.1, -144.02) * mm});
            skLineSegment(sketch, "E22.0.27.22", {"start": v(90.68, -149.1) * mm, "end": v(95.76, -149.1) * mm});
            skLineSegment(sketch, "E22.0.27.23", {"start": v(74.42, -149.1) * mm, "end": v(74.42, -144.02) * mm});
            skLineSegment(sketch, "E22.0.27.24", {"start": v(90.68, -144.02) * mm, "end": v(90.68, -149.1) * mm});
            skLineSegment(sketch, "E22.0.27.25", {"start": v(95.76, -149.1) * mm, "end": v(95.76, -144.02) * mm});
            skLineSegment(sketch, "E22.0.27.26", {"start": v(74.68, -144.02) * mm, "end": v(74.68, -149.1) * mm});
            skLineSegment(sketch, "E22.0.27.27", {"start": v(85.1, -149.1) * mm, "end": v(85.1, -144.02) * mm});
            skLineSegment(sketch, "E22.0.28.0", {"start": v(74.42, -149.35) * mm, "end": v(69.34, -149.35) * mm});
            skLineSegment(sketch, "E22.0.28.1", {"start": v(95.76, -149.35) * mm, "end": v(90.68, -149.35) * mm});
            skLineSegment(sketch, "E22.0.28.2", {"start": v(69.34, -149.35) * mm, "end": v(69.34, -154.43) * mm});
            skLineSegment(sketch, "E22.0.28.3", {"start": v(69.34, -154.43) * mm, "end": v(74.42, -154.43) * mm});
            skLineSegment(sketch, "E22.0.28.4", {"start": v(79.76, -154.43) * mm, "end": v(79.76, -149.35) * mm});
            skLineSegment(sketch, "E22.0.28.5", {"start": v(101.35, -154.43) * mm, "end": v(106.43, -154.43) * mm});
            skLineSegment(sketch, "E22.0.28.6", {"start": v(79.76, -149.35) * mm, "end": v(74.68, -149.35) * mm});
            skLineSegment(sketch, "E22.0.28.7", {"start": v(101.35, -149.35) * mm, "end": v(101.35, -154.43) * mm});
            skLineSegment(sketch, "E22.0.28.8", {"start": v(106.43, -149.35) * mm, "end": v(101.35, -149.35) * mm});
            skLineSegment(sketch, "E22.0.28.9", {"start": v(106.43, -154.43) * mm, "end": v(106.43, -149.35) * mm});
            skLineSegment(sketch, "E22.0.28.10", {"start": v(74.68, -154.43) * mm, "end": v(79.76, -154.43) * mm});
            skLineSegment(sketch, "E22.0.28.11", {"start": v(96.01, -154.43) * mm, "end": v(101.1, -154.43) * mm});
            skLineSegment(sketch, "E22.0.28.12", {"start": v(96.01, -149.35) * mm, "end": v(96.01, -154.43) * mm});
            skLineSegment(sketch, "E22.0.28.13", {"start": v(85.34, -154.43) * mm, "end": v(90.42, -154.43) * mm});
            skLineSegment(sketch, "E22.0.28.14", {"start": v(85.1, -149.35) * mm, "end": v(80, -149.35) * mm});
            skLineSegment(sketch, "E22.0.28.15", {"start": v(90.42, -149.35) * mm, "end": v(85.34, -149.35) * mm});
            skLineSegment(sketch, "E22.0.28.16", {"start": v(80, -149.35) * mm, "end": v(80, -154.43) * mm});
            skLineSegment(sketch, "E22.0.28.17", {"start": v(85.34, -149.35) * mm, "end": v(85.34, -154.43) * mm});
            skLineSegment(sketch, "E22.0.28.18", {"start": v(80, -154.43) * mm, "end": v(85.1, -154.43) * mm});
            skLineSegment(sketch, "E22.0.28.19", {"start": v(101.1, -149.35) * mm, "end": v(96.01, -149.35) * mm});
            skLineSegment(sketch, "E22.0.28.20", {"start": v(90.42, -154.43) * mm, "end": v(90.42, -149.35) * mm});
            skLineSegment(sketch, "E22.0.28.21", {"start": v(101.1, -154.43) * mm, "end": v(101.1, -149.35) * mm});
            skLineSegment(sketch, "E22.0.28.22", {"start": v(90.68, -154.43) * mm, "end": v(95.76, -154.43) * mm});
            skLineSegment(sketch, "E22.0.28.23", {"start": v(74.42, -154.43) * mm, "end": v(74.42, -149.35) * mm});
            skLineSegment(sketch, "E22.0.28.24", {"start": v(90.68, -149.35) * mm, "end": v(90.68, -154.43) * mm});
            skLineSegment(sketch, "E22.0.28.25", {"start": v(95.76, -154.43) * mm, "end": v(95.76, -149.35) * mm});
            skLineSegment(sketch, "E22.0.28.26", {"start": v(74.68, -149.35) * mm, "end": v(74.68, -154.43) * mm});
            skLineSegment(sketch, "E22.0.28.27", {"start": v(85.1, -154.43) * mm, "end": v(85.1, -149.35) * mm});
            skLineSegment(sketch, "E22.0.29.0", {"start": v(74.42, -154.69) * mm, "end": v(69.34, -154.69) * mm});
            skLineSegment(sketch, "E22.0.29.1", {"start": v(95.76, -154.69) * mm, "end": v(90.68, -154.69) * mm});
            skLineSegment(sketch, "E22.0.29.2", {"start": v(69.34, -154.69) * mm, "end": v(69.34, -159.77) * mm});
            skLineSegment(sketch, "E22.0.29.3", {"start": v(69.34, -159.77) * mm, "end": v(74.42, -159.77) * mm});
            skLineSegment(sketch, "E22.0.29.4", {"start": v(79.76, -159.77) * mm, "end": v(79.76, -154.69) * mm});
            skLineSegment(sketch, "E22.0.29.5", {"start": v(101.35, -159.77) * mm, "end": v(106.43, -159.77) * mm});
            skLineSegment(sketch, "E22.0.29.6", {"start": v(79.76, -154.69) * mm, "end": v(74.68, -154.69) * mm});
            skLineSegment(sketch, "E22.0.29.7", {"start": v(101.35, -154.69) * mm, "end": v(101.35, -159.77) * mm});
            skLineSegment(sketch, "E22.0.29.8", {"start": v(106.43, -154.69) * mm, "end": v(101.35, -154.69) * mm});
            skLineSegment(sketch, "E22.0.29.9", {"start": v(106.43, -159.77) * mm, "end": v(106.43, -154.69) * mm});
            skLineSegment(sketch, "E22.0.29.10", {"start": v(74.68, -159.77) * mm, "end": v(79.76, -159.77) * mm});
            skLineSegment(sketch, "E22.0.29.11", {"start": v(96.01, -159.77) * mm, "end": v(101.1, -159.77) * mm});
            skLineSegment(sketch, "E22.0.29.12", {"start": v(96.01, -154.69) * mm, "end": v(96.01, -159.77) * mm});
            skLineSegment(sketch, "E22.0.29.13", {"start": v(85.34, -159.77) * mm, "end": v(90.42, -159.77) * mm});
            skLineSegment(sketch, "E22.0.29.14", {"start": v(85.1, -154.69) * mm, "end": v(80, -154.69) * mm});
            skLineSegment(sketch, "E22.0.29.15", {"start": v(90.42, -154.69) * mm, "end": v(85.34, -154.69) * mm});
            skLineSegment(sketch, "E22.0.29.16", {"start": v(80, -154.69) * mm, "end": v(80, -159.77) * mm});
            skLineSegment(sketch, "E22.0.29.17", {"start": v(85.34, -154.69) * mm, "end": v(85.34, -159.77) * mm});
            skLineSegment(sketch, "E22.0.29.18", {"start": v(80, -159.77) * mm, "end": v(85.1, -159.77) * mm});
            skLineSegment(sketch, "E22.0.29.19", {"start": v(101.1, -154.69) * mm, "end": v(96.01, -154.69) * mm});
            skLineSegment(sketch, "E22.0.29.20", {"start": v(90.42, -159.77) * mm, "end": v(90.42, -154.69) * mm});
            skLineSegment(sketch, "E22.0.29.21", {"start": v(101.1, -159.77) * mm, "end": v(101.1, -154.69) * mm});
            skLineSegment(sketch, "E22.0.29.22", {"start": v(90.68, -159.77) * mm, "end": v(95.76, -159.77) * mm});
            skLineSegment(sketch, "E22.0.29.23", {"start": v(74.42, -159.77) * mm, "end": v(74.42, -154.69) * mm});
            skLineSegment(sketch, "E22.0.29.24", {"start": v(90.68, -154.69) * mm, "end": v(90.68, -159.77) * mm});
            skLineSegment(sketch, "E22.0.29.25", {"start": v(95.76, -159.77) * mm, "end": v(95.76, -154.69) * mm});
            skLineSegment(sketch, "E22.0.29.26", {"start": v(74.68, -154.69) * mm, "end": v(74.68, -159.77) * mm});
            skLineSegment(sketch, "E22.0.29.27", {"start": v(85.1, -159.77) * mm, "end": v(85.1, -154.69) * mm});
            skLineSegment(sketch, "E22.0.30.0", {"start": v(74.42, -160.02) * mm, "end": v(69.34, -160.02) * mm});
            skLineSegment(sketch, "E22.0.30.1", {"start": v(95.76, -160.02) * mm, "end": v(90.68, -160.02) * mm});
            skLineSegment(sketch, "E22.0.30.2", {"start": v(69.34, -160.02) * mm, "end": v(69.34, -165.1) * mm});
            skLineSegment(sketch, "E22.0.30.3", {"start": v(69.34, -165.1) * mm, "end": v(74.42, -165.1) * mm});
            skLineSegment(sketch, "E22.0.30.4", {"start": v(79.76, -165.1) * mm, "end": v(79.76, -160.02) * mm});
            skLineSegment(sketch, "E22.0.30.5", {"start": v(101.35, -165.1) * mm, "end": v(106.43, -165.1) * mm});
            skLineSegment(sketch, "E22.0.30.6", {"start": v(79.76, -160.02) * mm, "end": v(74.68, -160.02) * mm});
            skLineSegment(sketch, "E22.0.30.7", {"start": v(101.35, -160.02) * mm, "end": v(101.35, -165.1) * mm});
            skLineSegment(sketch, "E22.0.30.8", {"start": v(106.43, -160.02) * mm, "end": v(101.35, -160.02) * mm});
            skLineSegment(sketch, "E22.0.30.9", {"start": v(106.43, -165.1) * mm, "end": v(106.43, -160.02) * mm});
            skLineSegment(sketch, "E22.0.30.10", {"start": v(74.68, -165.1) * mm, "end": v(79.76, -165.1) * mm});
            skLineSegment(sketch, "E22.0.30.11", {"start": v(96.01, -165.1) * mm, "end": v(101.1, -165.1) * mm});
            skLineSegment(sketch, "E22.0.30.12", {"start": v(96.01, -160.02) * mm, "end": v(96.01, -165.1) * mm});
            skLineSegment(sketch, "E22.0.30.13", {"start": v(85.34, -165.1) * mm, "end": v(90.42, -165.1) * mm});
            skLineSegment(sketch, "E22.0.30.14", {"start": v(85.1, -160.02) * mm, "end": v(80, -160.02) * mm});
            skLineSegment(sketch, "E22.0.30.15", {"start": v(90.42, -160.02) * mm, "end": v(85.34, -160.02) * mm});
            skLineSegment(sketch, "E22.0.30.16", {"start": v(80, -160.02) * mm, "end": v(80, -165.1) * mm});
            skLineSegment(sketch, "E22.0.30.17", {"start": v(85.34, -160.02) * mm, "end": v(85.34, -165.1) * mm});
            skLineSegment(sketch, "E22.0.30.18", {"start": v(80, -165.1) * mm, "end": v(85.1, -165.1) * mm});
            skLineSegment(sketch, "E22.0.30.19", {"start": v(101.1, -160.02) * mm, "end": v(96.01, -160.02) * mm});
            skLineSegment(sketch, "E22.0.30.20", {"start": v(90.42, -165.1) * mm, "end": v(90.42, -160.02) * mm});
            skLineSegment(sketch, "E22.0.30.21", {"start": v(101.1, -165.1) * mm, "end": v(101.1, -160.02) * mm});
            skLineSegment(sketch, "E22.0.30.22", {"start": v(90.68, -165.1) * mm, "end": v(95.76, -165.1) * mm});
            skLineSegment(sketch, "E22.0.30.23", {"start": v(74.42, -165.1) * mm, "end": v(74.42, -160.02) * mm});
            skLineSegment(sketch, "E22.0.30.24", {"start": v(90.68, -160.02) * mm, "end": v(90.68, -165.1) * mm});
            skLineSegment(sketch, "E22.0.30.25", {"start": v(95.76, -165.1) * mm, "end": v(95.76, -160.02) * mm});
            skLineSegment(sketch, "E22.0.30.26", {"start": v(74.68, -160.02) * mm, "end": v(74.68, -165.1) * mm});
            skLineSegment(sketch, "E22.0.30.27", {"start": v(85.1, -165.1) * mm, "end": v(85.1, -160.02) * mm});
            skLineSegment(sketch, "E22.0.31.0", {"start": v(74.42, -165.35) * mm, "end": v(69.34, -165.35) * mm});
            skLineSegment(sketch, "E22.0.31.1", {"start": v(95.76, -165.35) * mm, "end": v(90.68, -165.35) * mm});
            skLineSegment(sketch, "E22.0.31.2", {"start": v(69.34, -165.35) * mm, "end": v(69.34, -170.43) * mm});
            skLineSegment(sketch, "E22.0.31.3", {"start": v(69.34, -170.43) * mm, "end": v(74.42, -170.43) * mm});
            skLineSegment(sketch, "E22.0.31.4", {"start": v(79.76, -170.43) * mm, "end": v(79.76, -165.35) * mm});
            skLineSegment(sketch, "E22.0.31.5", {"start": v(101.35, -170.43) * mm, "end": v(106.43, -170.43) * mm});
            skLineSegment(sketch, "E22.0.31.6", {"start": v(79.76, -165.35) * mm, "end": v(74.68, -165.35) * mm});
            skLineSegment(sketch, "E22.0.31.7", {"start": v(101.35, -165.35) * mm, "end": v(101.35, -170.43) * mm});
            skLineSegment(sketch, "E22.0.31.8", {"start": v(106.43, -165.35) * mm, "end": v(101.35, -165.35) * mm});
            skLineSegment(sketch, "E22.0.31.9", {"start": v(106.43, -170.43) * mm, "end": v(106.43, -165.35) * mm});
            skLineSegment(sketch, "E22.0.31.10", {"start": v(74.68, -170.43) * mm, "end": v(79.76, -170.43) * mm});
            skLineSegment(sketch, "E22.0.31.11", {"start": v(96.01, -170.43) * mm, "end": v(101.1, -170.43) * mm});
            skLineSegment(sketch, "E22.0.31.12", {"start": v(96.01, -165.35) * mm, "end": v(96.01, -170.43) * mm});
            skLineSegment(sketch, "E22.0.31.13", {"start": v(85.34, -170.43) * mm, "end": v(90.42, -170.43) * mm});
            skLineSegment(sketch, "E22.0.31.14", {"start": v(85.1, -165.35) * mm, "end": v(80, -165.35) * mm});
            skLineSegment(sketch, "E22.0.31.15", {"start": v(90.42, -165.35) * mm, "end": v(85.34, -165.35) * mm});
            skLineSegment(sketch, "E22.0.31.16", {"start": v(80, -165.35) * mm, "end": v(80, -170.43) * mm});
            skLineSegment(sketch, "E22.0.31.17", {"start": v(85.34, -165.35) * mm, "end": v(85.34, -170.43) * mm});
            skLineSegment(sketch, "E22.0.31.18", {"start": v(80, -170.43) * mm, "end": v(85.1, -170.43) * mm});
            skLineSegment(sketch, "E22.0.31.19", {"start": v(101.1, -165.35) * mm, "end": v(96.01, -165.35) * mm});
            skLineSegment(sketch, "E22.0.31.20", {"start": v(90.42, -170.43) * mm, "end": v(90.42, -165.35) * mm});
            skLineSegment(sketch, "E22.0.31.21", {"start": v(101.1, -170.43) * mm, "end": v(101.1, -165.35) * mm});
            skLineSegment(sketch, "E22.0.31.22", {"start": v(90.68, -170.43) * mm, "end": v(95.76, -170.43) * mm});
            skLineSegment(sketch, "E22.0.31.23", {"start": v(74.42, -170.43) * mm, "end": v(74.42, -165.35) * mm});
            skLineSegment(sketch, "E22.0.31.24", {"start": v(90.68, -165.35) * mm, "end": v(90.68, -170.43) * mm});
            skLineSegment(sketch, "E22.0.31.25", {"start": v(95.76, -170.43) * mm, "end": v(95.76, -165.35) * mm});
            skLineSegment(sketch, "E22.0.31.26", {"start": v(74.68, -165.35) * mm, "end": v(74.68, -170.43) * mm});
            skLineSegment(sketch, "E22.0.31.27", {"start": v(85.1, -170.43) * mm, "end": v(85.1, -165.35) * mm});
            skLineSegment(sketch, "E22.0.32.0", {"start": v(74.42, -170.69) * mm, "end": v(69.34, -170.69) * mm});
            skLineSegment(sketch, "E22.0.32.1", {"start": v(95.76, -170.69) * mm, "end": v(90.68, -170.69) * mm});
            skLineSegment(sketch, "E22.0.32.2", {"start": v(69.34, -170.69) * mm, "end": v(69.34, -175.77) * mm});
            skLineSegment(sketch, "E22.0.32.3", {"start": v(69.34, -175.77) * mm, "end": v(74.42, -175.77) * mm});
            skLineSegment(sketch, "E22.0.32.4", {"start": v(79.76, -175.77) * mm, "end": v(79.76, -170.69) * mm});
            skLineSegment(sketch, "E22.0.32.5", {"start": v(101.35, -175.77) * mm, "end": v(106.43, -175.77) * mm});
            skLineSegment(sketch, "E22.0.32.6", {"start": v(79.76, -170.69) * mm, "end": v(74.68, -170.69) * mm});
            skLineSegment(sketch, "E22.0.32.7", {"start": v(101.35, -170.69) * mm, "end": v(101.35, -175.77) * mm});
            skLineSegment(sketch, "E22.0.32.8", {"start": v(106.43, -170.69) * mm, "end": v(101.35, -170.69) * mm});
            skLineSegment(sketch, "E22.0.32.9", {"start": v(106.43, -175.77) * mm, "end": v(106.43, -170.69) * mm});
            skLineSegment(sketch, "E22.0.32.10", {"start": v(74.68, -175.77) * mm, "end": v(79.76, -175.77) * mm});
            skLineSegment(sketch, "E22.0.32.11", {"start": v(96.01, -175.77) * mm, "end": v(101.1, -175.77) * mm});
            skLineSegment(sketch, "E22.0.32.12", {"start": v(96.01, -170.69) * mm, "end": v(96.01, -175.77) * mm});
            skLineSegment(sketch, "E22.0.32.13", {"start": v(85.34, -175.77) * mm, "end": v(90.42, -175.77) * mm});
            skLineSegment(sketch, "E22.0.32.14", {"start": v(85.1, -170.69) * mm, "end": v(80, -170.69) * mm});
            skLineSegment(sketch, "E22.0.32.15", {"start": v(90.42, -170.69) * mm, "end": v(85.34, -170.69) * mm});
            skLineSegment(sketch, "E22.0.32.16", {"start": v(80, -170.69) * mm, "end": v(80, -175.77) * mm});
            skLineSegment(sketch, "E22.0.32.17", {"start": v(85.34, -170.69) * mm, "end": v(85.34, -175.77) * mm});
            skLineSegment(sketch, "E22.0.32.18", {"start": v(80, -175.77) * mm, "end": v(85.1, -175.77) * mm});
            skLineSegment(sketch, "E22.0.32.19", {"start": v(101.1, -170.69) * mm, "end": v(96.01, -170.69) * mm});
            skLineSegment(sketch, "E22.0.32.20", {"start": v(90.42, -175.77) * mm, "end": v(90.42, -170.69) * mm});
            skLineSegment(sketch, "E22.0.32.21", {"start": v(101.1, -175.77) * mm, "end": v(101.1, -170.69) * mm});
            skLineSegment(sketch, "E22.0.32.22", {"start": v(90.68, -175.77) * mm, "end": v(95.76, -175.77) * mm});
            skLineSegment(sketch, "E22.0.32.23", {"start": v(74.42, -175.77) * mm, "end": v(74.42, -170.69) * mm});
            skLineSegment(sketch, "E22.0.32.24", {"start": v(90.68, -170.69) * mm, "end": v(90.68, -175.77) * mm});
            skLineSegment(sketch, "E22.0.32.25", {"start": v(95.76, -175.77) * mm, "end": v(95.76, -170.69) * mm});
            skLineSegment(sketch, "E22.0.32.26", {"start": v(74.68, -170.69) * mm, "end": v(74.68, -175.77) * mm});
            skLineSegment(sketch, "E22.0.32.27", {"start": v(85.1, -175.77) * mm, "end": v(85.1, -170.69) * mm});
            skLineSegment(sketch, "E22.0.33.0", {"start": v(74.42, -176.02) * mm, "end": v(69.34, -176.02) * mm});
            skLineSegment(sketch, "E22.0.33.1", {"start": v(95.76, -176.02) * mm, "end": v(90.68, -176.02) * mm});
            skLineSegment(sketch, "E22.0.33.2", {"start": v(69.34, -176.02) * mm, "end": v(69.34, -181.1) * mm});
            skLineSegment(sketch, "E22.0.33.3", {"start": v(69.34, -181.1) * mm, "end": v(74.42, -181.1) * mm});
            skLineSegment(sketch, "E22.0.33.4", {"start": v(79.76, -181.1) * mm, "end": v(79.76, -176.02) * mm});
            skLineSegment(sketch, "E22.0.33.5", {"start": v(101.35, -181.1) * mm, "end": v(106.43, -181.1) * mm});
            skLineSegment(sketch, "E22.0.33.6", {"start": v(79.76, -176.02) * mm, "end": v(74.68, -176.02) * mm});
            skLineSegment(sketch, "E22.0.33.7", {"start": v(101.35, -176.02) * mm, "end": v(101.35, -181.1) * mm});
            skLineSegment(sketch, "E22.0.33.8", {"start": v(106.43, -176.02) * mm, "end": v(101.35, -176.02) * mm});
            skLineSegment(sketch, "E22.0.33.9", {"start": v(106.43, -181.1) * mm, "end": v(106.43, -176.02) * mm});
            skLineSegment(sketch, "E22.0.33.10", {"start": v(74.68, -181.1) * mm, "end": v(79.76, -181.1) * mm});
            skLineSegment(sketch, "E22.0.33.11", {"start": v(96.01, -181.1) * mm, "end": v(101.1, -181.1) * mm});
            skLineSegment(sketch, "E22.0.33.12", {"start": v(96.01, -176.02) * mm, "end": v(96.01, -181.1) * mm});
            skLineSegment(sketch, "E22.0.33.13", {"start": v(85.34, -181.1) * mm, "end": v(90.42, -181.1) * mm});
            skLineSegment(sketch, "E22.0.33.14", {"start": v(85.1, -176.02) * mm, "end": v(80, -176.02) * mm});
            skLineSegment(sketch, "E22.0.33.15", {"start": v(90.42, -176.02) * mm, "end": v(85.34, -176.02) * mm});
            skLineSegment(sketch, "E22.0.33.16", {"start": v(80, -176.02) * mm, "end": v(80, -181.1) * mm});
            skLineSegment(sketch, "E22.0.33.17", {"start": v(85.34, -176.02) * mm, "end": v(85.34, -181.1) * mm});
            skLineSegment(sketch, "E22.0.33.18", {"start": v(80, -181.1) * mm, "end": v(85.1, -181.1) * mm});
            skLineSegment(sketch, "E22.0.33.19", {"start": v(101.1, -176.02) * mm, "end": v(96.01, -176.02) * mm});
            skLineSegment(sketch, "E22.0.33.20", {"start": v(90.42, -181.1) * mm, "end": v(90.42, -176.02) * mm});
            skLineSegment(sketch, "E22.0.33.21", {"start": v(101.1, -181.1) * mm, "end": v(101.1, -176.02) * mm});
            skLineSegment(sketch, "E22.0.33.22", {"start": v(90.68, -181.1) * mm, "end": v(95.76, -181.1) * mm});
            skLineSegment(sketch, "E22.0.33.23", {"start": v(74.42, -181.1) * mm, "end": v(74.42, -176.02) * mm});
            skLineSegment(sketch, "E22.0.33.24", {"start": v(90.68, -176.02) * mm, "end": v(90.68, -181.1) * mm});
            skLineSegment(sketch, "E22.0.33.25", {"start": v(95.76, -181.1) * mm, "end": v(95.76, -176.02) * mm});
            skLineSegment(sketch, "E22.0.33.26", {"start": v(74.68, -176.02) * mm, "end": v(74.68, -181.1) * mm});
            skLineSegment(sketch, "E22.0.33.27", {"start": v(85.1, -181.1) * mm, "end": v(85.1, -176.02) * mm});
            skLineSegment(sketch, "E22.0.34.0", {"start": v(74.42, -181.36) * mm, "end": v(69.34, -181.36) * mm});
            skLineSegment(sketch, "E22.0.34.1", {"start": v(95.76, -181.36) * mm, "end": v(90.68, -181.36) * mm});
            skLineSegment(sketch, "E22.0.34.2", {"start": v(69.34, -181.36) * mm, "end": v(69.34, -186.44) * mm});
            skLineSegment(sketch, "E22.0.34.3", {"start": v(69.34, -186.44) * mm, "end": v(74.42, -186.44) * mm});
            skLineSegment(sketch, "E22.0.34.4", {"start": v(79.76, -186.44) * mm, "end": v(79.76, -181.36) * mm});
            skLineSegment(sketch, "E22.0.34.5", {"start": v(101.35, -186.44) * mm, "end": v(106.43, -186.44) * mm});
            skLineSegment(sketch, "E22.0.34.6", {"start": v(79.76, -181.36) * mm, "end": v(74.68, -181.36) * mm});
            skLineSegment(sketch, "E22.0.34.7", {"start": v(101.35, -181.36) * mm, "end": v(101.35, -186.44) * mm});
            skLineSegment(sketch, "E22.0.34.8", {"start": v(106.43, -181.36) * mm, "end": v(101.35, -181.36) * mm});
            skLineSegment(sketch, "E22.0.34.9", {"start": v(106.43, -186.44) * mm, "end": v(106.43, -181.36) * mm});
            skLineSegment(sketch, "E22.0.34.10", {"start": v(74.68, -186.44) * mm, "end": v(79.76, -186.44) * mm});
            skLineSegment(sketch, "E22.0.34.11", {"start": v(96.01, -186.44) * mm, "end": v(101.1, -186.44) * mm});
            skLineSegment(sketch, "E22.0.34.12", {"start": v(96.01, -181.36) * mm, "end": v(96.01, -186.44) * mm});
            skLineSegment(sketch, "E22.0.34.13", {"start": v(85.34, -186.44) * mm, "end": v(90.42, -186.44) * mm});
            skLineSegment(sketch, "E22.0.34.14", {"start": v(85.1, -181.36) * mm, "end": v(80, -181.36) * mm});
            skLineSegment(sketch, "E22.0.34.15", {"start": v(90.42, -181.36) * mm, "end": v(85.34, -181.36) * mm});
            skLineSegment(sketch, "E22.0.34.16", {"start": v(80, -181.36) * mm, "end": v(80, -186.44) * mm});
            skLineSegment(sketch, "E22.0.34.17", {"start": v(85.34, -181.36) * mm, "end": v(85.34, -186.44) * mm});
            skLineSegment(sketch, "E22.0.34.18", {"start": v(80, -186.44) * mm, "end": v(85.1, -186.44) * mm});
            skLineSegment(sketch, "E22.0.34.19", {"start": v(101.1, -181.36) * mm, "end": v(96.01, -181.36) * mm});
            skLineSegment(sketch, "E22.0.34.20", {"start": v(90.42, -186.44) * mm, "end": v(90.42, -181.36) * mm});
            skLineSegment(sketch, "E22.0.34.21", {"start": v(101.1, -186.44) * mm, "end": v(101.1, -181.36) * mm});
            skLineSegment(sketch, "E22.0.34.22", {"start": v(90.68, -186.44) * mm, "end": v(95.76, -186.44) * mm});
            skLineSegment(sketch, "E22.0.34.23", {"start": v(74.42, -186.44) * mm, "end": v(74.42, -181.36) * mm});
            skLineSegment(sketch, "E22.0.34.24", {"start": v(90.68, -181.36) * mm, "end": v(90.68, -186.44) * mm});
            skLineSegment(sketch, "E22.0.34.25", {"start": v(95.76, -186.44) * mm, "end": v(95.76, -181.36) * mm});
            skLineSegment(sketch, "E22.0.34.26", {"start": v(74.68, -181.36) * mm, "end": v(74.68, -186.44) * mm});
            skLineSegment(sketch, "E22.0.34.27", {"start": v(85.1, -186.44) * mm, "end": v(85.1, -181.36) * mm});
            skLineSegment(sketch, "E22.0.35.0", {"start": v(74.42, -186.7) * mm, "end": v(69.34, -186.7) * mm});
            skLineSegment(sketch, "E22.0.35.1", {"start": v(95.76, -186.7) * mm, "end": v(90.68, -186.7) * mm});
            skLineSegment(sketch, "E22.0.35.2", {"start": v(69.34, -186.7) * mm, "end": v(69.34, -191.77) * mm});
            skLineSegment(sketch, "E22.0.35.3", {"start": v(69.34, -191.77) * mm, "end": v(74.42, -191.77) * mm});
            skLineSegment(sketch, "E22.0.35.4", {"start": v(79.76, -191.77) * mm, "end": v(79.76, -186.7) * mm});
            skLineSegment(sketch, "E22.0.35.5", {"start": v(101.35, -191.77) * mm, "end": v(106.43, -191.77) * mm});
            skLineSegment(sketch, "E22.0.35.6", {"start": v(79.76, -186.7) * mm, "end": v(74.68, -186.7) * mm});
            skLineSegment(sketch, "E22.0.35.7", {"start": v(101.35, -186.7) * mm, "end": v(101.35, -191.77) * mm});
            skLineSegment(sketch, "E22.0.35.8", {"start": v(106.43, -186.7) * mm, "end": v(101.35, -186.7) * mm});
            skLineSegment(sketch, "E22.0.35.9", {"start": v(106.43, -191.77) * mm, "end": v(106.43, -186.7) * mm});
            skLineSegment(sketch, "E22.0.35.10", {"start": v(74.68, -191.77) * mm, "end": v(79.76, -191.77) * mm});
            skLineSegment(sketch, "E22.0.35.11", {"start": v(96.01, -191.77) * mm, "end": v(101.1, -191.77) * mm});
            skLineSegment(sketch, "E22.0.35.12", {"start": v(96.01, -186.7) * mm, "end": v(96.01, -191.77) * mm});
            skLineSegment(sketch, "E22.0.35.13", {"start": v(85.34, -191.77) * mm, "end": v(90.42, -191.77) * mm});
            skLineSegment(sketch, "E22.0.35.14", {"start": v(85.1, -186.7) * mm, "end": v(80, -186.7) * mm});
            skLineSegment(sketch, "E22.0.35.15", {"start": v(90.42, -186.7) * mm, "end": v(85.34, -186.7) * mm});
            skLineSegment(sketch, "E22.0.35.16", {"start": v(80, -186.7) * mm, "end": v(80, -191.77) * mm});
            skLineSegment(sketch, "E22.0.35.17", {"start": v(85.34, -186.7) * mm, "end": v(85.34, -191.77) * mm});
            skLineSegment(sketch, "E22.0.35.18", {"start": v(80, -191.77) * mm, "end": v(85.1, -191.77) * mm});
            skLineSegment(sketch, "E22.0.35.19", {"start": v(101.1, -186.7) * mm, "end": v(96.01, -186.7) * mm});
            skLineSegment(sketch, "E22.0.35.20", {"start": v(90.42, -191.77) * mm, "end": v(90.42, -186.7) * mm});
            skLineSegment(sketch, "E22.0.35.21", {"start": v(101.1, -191.77) * mm, "end": v(101.1, -186.7) * mm});
            skLineSegment(sketch, "E22.0.35.22", {"start": v(90.68, -191.77) * mm, "end": v(95.76, -191.77) * mm});
            skLineSegment(sketch, "E22.0.35.23", {"start": v(74.42, -191.77) * mm, "end": v(74.42, -186.7) * mm});
            skLineSegment(sketch, "E22.0.35.24", {"start": v(90.68, -186.7) * mm, "end": v(90.68, -191.77) * mm});
            skLineSegment(sketch, "E22.0.35.25", {"start": v(95.76, -191.77) * mm, "end": v(95.76, -186.7) * mm});
            skLineSegment(sketch, "E22.0.35.26", {"start": v(74.68, -186.7) * mm, "end": v(74.68, -191.77) * mm});
            skLineSegment(sketch, "E22.0.35.27", {"start": v(85.1, -191.77) * mm, "end": v(85.1, -186.7) * mm});
            skLineSegment(sketch, "E22.0.36.0", {"start": v(74.42, -192.02) * mm, "end": v(69.34, -192.02) * mm});
            skLineSegment(sketch, "E22.0.36.1", {"start": v(95.76, -192.02) * mm, "end": v(90.68, -192.02) * mm});
            skLineSegment(sketch, "E22.0.36.2", {"start": v(69.34, -192.02) * mm, "end": v(69.34, -197.1) * mm});
            skLineSegment(sketch, "E22.0.36.3", {"start": v(69.34, -197.1) * mm, "end": v(74.42, -197.1) * mm});
            skLineSegment(sketch, "E22.0.36.4", {"start": v(79.76, -197.1) * mm, "end": v(79.76, -192.02) * mm});
            skLineSegment(sketch, "E22.0.36.5", {"start": v(101.35, -197.1) * mm, "end": v(106.43, -197.1) * mm});
            skLineSegment(sketch, "E22.0.36.6", {"start": v(79.76, -192.02) * mm, "end": v(74.68, -192.02) * mm});
            skLineSegment(sketch, "E22.0.36.7", {"start": v(101.35, -192.02) * mm, "end": v(101.35, -197.1) * mm});
            skLineSegment(sketch, "E22.0.36.8", {"start": v(106.43, -192.02) * mm, "end": v(101.35, -192.02) * mm});
            skLineSegment(sketch, "E22.0.36.9", {"start": v(106.43, -197.1) * mm, "end": v(106.43, -192.02) * mm});
            skLineSegment(sketch, "E22.0.36.10", {"start": v(74.68, -197.1) * mm, "end": v(79.76, -197.1) * mm});
            skLineSegment(sketch, "E22.0.36.11", {"start": v(96.01, -197.1) * mm, "end": v(101.1, -197.1) * mm});
            skLineSegment(sketch, "E22.0.36.12", {"start": v(96.01, -192.02) * mm, "end": v(96.01, -197.1) * mm});
            skLineSegment(sketch, "E22.0.36.13", {"start": v(85.34, -197.1) * mm, "end": v(90.42, -197.1) * mm});
            skLineSegment(sketch, "E22.0.36.14", {"start": v(85.1, -192.02) * mm, "end": v(80, -192.02) * mm});
            skLineSegment(sketch, "E22.0.36.15", {"start": v(90.42, -192.02) * mm, "end": v(85.34, -192.02) * mm});
            skLineSegment(sketch, "E22.0.36.16", {"start": v(80, -192.02) * mm, "end": v(80, -197.1) * mm});
            skLineSegment(sketch, "E22.0.36.17", {"start": v(85.34, -192.02) * mm, "end": v(85.34, -197.1) * mm});
            skLineSegment(sketch, "E22.0.36.18", {"start": v(80, -197.1) * mm, "end": v(85.1, -197.1) * mm});
            skLineSegment(sketch, "E22.0.36.19", {"start": v(101.1, -192.02) * mm, "end": v(96.01, -192.02) * mm});
            skLineSegment(sketch, "E22.0.36.20", {"start": v(90.42, -197.1) * mm, "end": v(90.42, -192.02) * mm});
            skLineSegment(sketch, "E22.0.36.21", {"start": v(101.1, -197.1) * mm, "end": v(101.1, -192.02) * mm});
            skLineSegment(sketch, "E22.0.36.22", {"start": v(90.68, -197.1) * mm, "end": v(95.76, -197.1) * mm});
            skLineSegment(sketch, "E22.0.36.23", {"start": v(74.42, -197.1) * mm, "end": v(74.42, -192.02) * mm});
            skLineSegment(sketch, "E22.0.36.24", {"start": v(90.68, -192.02) * mm, "end": v(90.68, -197.1) * mm});
            skLineSegment(sketch, "E22.0.36.25", {"start": v(95.76, -197.1) * mm, "end": v(95.76, -192.02) * mm});
            skLineSegment(sketch, "E22.0.36.26", {"start": v(74.68, -192.02) * mm, "end": v(74.68, -197.1) * mm});
            skLineSegment(sketch, "E22.0.36.27", {"start": v(85.1, -197.1) * mm, "end": v(85.1, -192.02) * mm});
            skLineSegment(sketch, "E22.0.37.0", {"start": v(74.42, -197.36) * mm, "end": v(69.34, -197.36) * mm});
            skLineSegment(sketch, "E22.0.37.1", {"start": v(95.76, -197.36) * mm, "end": v(90.68, -197.36) * mm});
            skLineSegment(sketch, "E22.0.37.2", {"start": v(69.34, -197.36) * mm, "end": v(69.34, -202.44) * mm});
            skLineSegment(sketch, "E22.0.37.3", {"start": v(69.34, -202.44) * mm, "end": v(74.42, -202.44) * mm});
            skLineSegment(sketch, "E22.0.37.4", {"start": v(79.76, -202.44) * mm, "end": v(79.76, -197.36) * mm});
            skLineSegment(sketch, "E22.0.37.5", {"start": v(101.35, -202.44) * mm, "end": v(106.43, -202.44) * mm});
            skLineSegment(sketch, "E22.0.37.6", {"start": v(79.76, -197.36) * mm, "end": v(74.68, -197.36) * mm});
            skLineSegment(sketch, "E22.0.37.7", {"start": v(101.35, -197.36) * mm, "end": v(101.35, -202.44) * mm});
            skLineSegment(sketch, "E22.0.37.8", {"start": v(106.43, -197.36) * mm, "end": v(101.35, -197.36) * mm});
            skLineSegment(sketch, "E22.0.37.9", {"start": v(106.43, -202.44) * mm, "end": v(106.43, -197.36) * mm});
            skLineSegment(sketch, "E22.0.37.10", {"start": v(74.68, -202.44) * mm, "end": v(79.76, -202.44) * mm});
            skLineSegment(sketch, "E22.0.37.11", {"start": v(96.01, -202.44) * mm, "end": v(101.1, -202.44) * mm});
            skLineSegment(sketch, "E22.0.37.12", {"start": v(96.01, -197.36) * mm, "end": v(96.01, -202.44) * mm});
            skLineSegment(sketch, "E22.0.37.13", {"start": v(85.34, -202.44) * mm, "end": v(90.42, -202.44) * mm});
            skLineSegment(sketch, "E22.0.37.14", {"start": v(85.1, -197.36) * mm, "end": v(80, -197.36) * mm});
            skLineSegment(sketch, "E22.0.37.15", {"start": v(90.42, -197.36) * mm, "end": v(85.34, -197.36) * mm});
            skLineSegment(sketch, "E22.0.37.16", {"start": v(80, -197.36) * mm, "end": v(80, -202.44) * mm});
            skLineSegment(sketch, "E22.0.37.17", {"start": v(85.34, -197.36) * mm, "end": v(85.34, -202.44) * mm});
            skLineSegment(sketch, "E22.0.37.18", {"start": v(80, -202.44) * mm, "end": v(85.1, -202.44) * mm});
            skLineSegment(sketch, "E22.0.37.19", {"start": v(101.1, -197.36) * mm, "end": v(96.01, -197.36) * mm});
            skLineSegment(sketch, "E22.0.37.20", {"start": v(90.42, -202.44) * mm, "end": v(90.42, -197.36) * mm});
            skLineSegment(sketch, "E22.0.37.21", {"start": v(101.1, -202.44) * mm, "end": v(101.1, -197.36) * mm});
            skLineSegment(sketch, "E22.0.37.22", {"start": v(90.68, -202.44) * mm, "end": v(95.76, -202.44) * mm});
            skLineSegment(sketch, "E22.0.37.23", {"start": v(74.42, -202.44) * mm, "end": v(74.42, -197.36) * mm});
            skLineSegment(sketch, "E22.0.37.24", {"start": v(90.68, -197.36) * mm, "end": v(90.68, -202.44) * mm});
            skLineSegment(sketch, "E22.0.37.25", {"start": v(95.76, -202.44) * mm, "end": v(95.76, -197.36) * mm});
            skLineSegment(sketch, "E22.0.37.26", {"start": v(74.68, -197.36) * mm, "end": v(74.68, -202.44) * mm});
            skLineSegment(sketch, "E22.0.37.27", {"start": v(85.1, -202.44) * mm, "end": v(85.1, -197.36) * mm});
            skLineSegment(sketch, "E22.0.38.0", {"start": v(74.42, -202.7) * mm, "end": v(69.34, -202.7) * mm});
            skLineSegment(sketch, "E22.0.38.1", {"start": v(95.76, -202.7) * mm, "end": v(90.68, -202.7) * mm});
            skLineSegment(sketch, "E22.0.38.2", {"start": v(69.34, -202.7) * mm, "end": v(69.34, -207.77) * mm});
            skLineSegment(sketch, "E22.0.38.3", {"start": v(69.34, -207.77) * mm, "end": v(74.42, -207.77) * mm});
            skLineSegment(sketch, "E22.0.38.4", {"start": v(79.76, -207.77) * mm, "end": v(79.76, -202.7) * mm});
            skLineSegment(sketch, "E22.0.38.5", {"start": v(101.35, -207.77) * mm, "end": v(106.43, -207.77) * mm});
            skLineSegment(sketch, "E22.0.38.6", {"start": v(79.76, -202.7) * mm, "end": v(74.68, -202.7) * mm});
            skLineSegment(sketch, "E22.0.38.7", {"start": v(101.35, -202.7) * mm, "end": v(101.35, -207.77) * mm});
            skLineSegment(sketch, "E22.0.38.8", {"start": v(106.43, -202.7) * mm, "end": v(101.35, -202.7) * mm});
            skLineSegment(sketch, "E22.0.38.9", {"start": v(106.43, -207.77) * mm, "end": v(106.43, -202.7) * mm});
            skLineSegment(sketch, "E22.0.38.10", {"start": v(74.68, -207.77) * mm, "end": v(79.76, -207.77) * mm});
            skLineSegment(sketch, "E22.0.38.11", {"start": v(96.01, -207.77) * mm, "end": v(101.1, -207.77) * mm});
            skLineSegment(sketch, "E22.0.38.12", {"start": v(96.01, -202.7) * mm, "end": v(96.01, -207.77) * mm});
            skLineSegment(sketch, "E22.0.38.13", {"start": v(85.34, -207.77) * mm, "end": v(90.42, -207.77) * mm});
            skLineSegment(sketch, "E22.0.38.14", {"start": v(85.1, -202.7) * mm, "end": v(80, -202.7) * mm});
            skLineSegment(sketch, "E22.0.38.15", {"start": v(90.42, -202.7) * mm, "end": v(85.34, -202.7) * mm});
            skLineSegment(sketch, "E22.0.38.16", {"start": v(80, -202.7) * mm, "end": v(80, -207.77) * mm});
            skLineSegment(sketch, "E22.0.38.17", {"start": v(85.34, -202.7) * mm, "end": v(85.34, -207.77) * mm});
            skLineSegment(sketch, "E22.0.38.18", {"start": v(80, -207.77) * mm, "end": v(85.1, -207.77) * mm});
            skLineSegment(sketch, "E22.0.38.19", {"start": v(101.1, -202.7) * mm, "end": v(96.01, -202.7) * mm});
            skLineSegment(sketch, "E22.0.38.20", {"start": v(90.42, -207.77) * mm, "end": v(90.42, -202.7) * mm});
            skLineSegment(sketch, "E22.0.38.21", {"start": v(101.1, -207.77) * mm, "end": v(101.1, -202.7) * mm});
            skLineSegment(sketch, "E22.0.38.22", {"start": v(90.68, -207.77) * mm, "end": v(95.76, -207.77) * mm});
            skLineSegment(sketch, "E22.0.38.23", {"start": v(74.42, -207.77) * mm, "end": v(74.42, -202.7) * mm});
            skLineSegment(sketch, "E22.0.38.24", {"start": v(90.68, -202.7) * mm, "end": v(90.68, -207.77) * mm});
            skLineSegment(sketch, "E22.0.38.25", {"start": v(95.76, -207.77) * mm, "end": v(95.76, -202.7) * mm});
            skLineSegment(sketch, "E22.0.38.26", {"start": v(74.68, -202.7) * mm, "end": v(74.68, -207.77) * mm});
            skLineSegment(sketch, "E22.0.38.27", {"start": v(85.1, -207.77) * mm, "end": v(85.1, -202.7) * mm});
            skLineSegment(sketch, "E22.0.39.0", {"start": v(74.42, -208.03) * mm, "end": v(69.34, -208.03) * mm});
            skLineSegment(sketch, "E22.0.39.1", {"start": v(95.76, -208.03) * mm, "end": v(90.68, -208.03) * mm});
            skLineSegment(sketch, "E22.0.39.2", {"start": v(69.34, -208.03) * mm, "end": v(69.34, -213.1) * mm});
            skLineSegment(sketch, "E22.0.39.3", {"start": v(69.34, -213.1) * mm, "end": v(74.42, -213.1) * mm});
            skLineSegment(sketch, "E22.0.39.4", {"start": v(79.76, -213.1) * mm, "end": v(79.76, -208.03) * mm});
            skLineSegment(sketch, "E22.0.39.5", {"start": v(101.35, -213.1) * mm, "end": v(106.43, -213.1) * mm});
            skLineSegment(sketch, "E22.0.39.6", {"start": v(79.76, -208.03) * mm, "end": v(74.68, -208.03) * mm});
            skLineSegment(sketch, "E22.0.39.7", {"start": v(101.35, -208.03) * mm, "end": v(101.35, -213.1) * mm});
            skLineSegment(sketch, "E22.0.39.8", {"start": v(106.43, -208.03) * mm, "end": v(101.35, -208.03) * mm});
            skLineSegment(sketch, "E22.0.39.9", {"start": v(106.43, -213.1) * mm, "end": v(106.43, -208.03) * mm});
            skLineSegment(sketch, "E22.0.39.10", {"start": v(74.68, -213.1) * mm, "end": v(79.76, -213.1) * mm});
            skLineSegment(sketch, "E22.0.39.11", {"start": v(96.01, -213.1) * mm, "end": v(101.1, -213.1) * mm});
            skLineSegment(sketch, "E22.0.39.12", {"start": v(96.01, -208.03) * mm, "end": v(96.01, -213.1) * mm});
            skLineSegment(sketch, "E22.0.39.13", {"start": v(85.34, -213.1) * mm, "end": v(90.42, -213.1) * mm});
            skLineSegment(sketch, "E22.0.39.14", {"start": v(85.1, -208.03) * mm, "end": v(80, -208.03) * mm});
            skLineSegment(sketch, "E22.0.39.15", {"start": v(90.42, -208.03) * mm, "end": v(85.34, -208.03) * mm});
            skLineSegment(sketch, "E22.0.39.16", {"start": v(80, -208.03) * mm, "end": v(80, -213.1) * mm});
            skLineSegment(sketch, "E22.0.39.17", {"start": v(85.34, -208.03) * mm, "end": v(85.34, -213.1) * mm});
            skLineSegment(sketch, "E22.0.39.18", {"start": v(80, -213.1) * mm, "end": v(85.1, -213.1) * mm});
            skLineSegment(sketch, "E22.0.39.19", {"start": v(101.1, -208.03) * mm, "end": v(96.01, -208.03) * mm});
            skLineSegment(sketch, "E22.0.39.20", {"start": v(90.42, -213.1) * mm, "end": v(90.42, -208.03) * mm});
            skLineSegment(sketch, "E22.0.39.21", {"start": v(101.1, -213.1) * mm, "end": v(101.1, -208.03) * mm});
            skLineSegment(sketch, "E22.0.39.22", {"start": v(90.68, -213.1) * mm, "end": v(95.76, -213.1) * mm});
            skLineSegment(sketch, "E22.0.39.23", {"start": v(74.42, -213.1) * mm, "end": v(74.42, -208.03) * mm});
            skLineSegment(sketch, "E22.0.39.24", {"start": v(90.68, -208.03) * mm, "end": v(90.68, -213.1) * mm});
            skLineSegment(sketch, "E22.0.39.25", {"start": v(95.76, -213.1) * mm, "end": v(95.76, -208.03) * mm});
            skLineSegment(sketch, "E22.0.39.26", {"start": v(74.68, -208.03) * mm, "end": v(74.68, -213.1) * mm});
            skLineSegment(sketch, "E22.0.39.27", {"start": v(85.1, -213.1) * mm, "end": v(85.1, -208.03) * mm});
            skLineSegment(sketch, "E22.direction1", {"start": v(69.34, -5.08) * mm, "end": v(94.74, -5.08) * mm, "construction": true});
            skLineSegment(sketch, "E22.direction2", {"start": v(69.34, -5.08) * mm, "end": v(69.34, -10.41) * mm, "construction": true});
            skSolve(sketch);
        }
        {
            var Q0;
            Q0=qCreatedBy(makeId("Top.planeOp"),FACE);
            var sketch = newSketch(context, id + "F7", { "sketchPlane" : qUnion([Q0])});
            skLineSegment(sketch, "E23.0.0", {"start": v(111.76, -5.08) * mm, "end": v(111.76, 0) * mm});
            skLineSegment(sketch, "E23.0.1", {"start": v(111.76, 0) * mm, "end": v(106.68, 0) * mm});
            skLineSegment(sketch, "E23.0.2", {"start": v(106.68, 0) * mm, "end": v(106.68, -5.08) * mm});
            skLineSegment(sketch, "E23.0.3", {"start": v(106.68, -5.08) * mm, "end": v(111.76, -5.08) * mm});
            skLineSegment(sketch, "E23.1.0", {"start": v(117.1, -5.08) * mm, "end": v(117.1, 0) * mm});
            skLineSegment(sketch, "E23.1.1", {"start": v(117.1, 0) * mm, "end": v(112.01, 0) * mm});
            skLineSegment(sketch, "E23.1.2", {"start": v(112.01, 0) * mm, "end": v(112.01, -5.08) * mm});
            skLineSegment(sketch, "E23.1.3", {"start": v(112.01, -5.08) * mm, "end": v(117.1, -5.08) * mm});
            skLineSegment(sketch, "E23.2.0", {"start": v(122.43, -5.08) * mm, "end": v(122.43, 0) * mm});
            skLineSegment(sketch, "E23.2.1", {"start": v(122.43, 0) * mm, "end": v(117.35, 0) * mm});
            skLineSegment(sketch, "E23.2.2", {"start": v(117.35, 0) * mm, "end": v(117.35, -5.08) * mm});
            skLineSegment(sketch, "E23.2.3", {"start": v(117.35, -5.08) * mm, "end": v(122.43, -5.08) * mm});
            skLineSegment(sketch, "E23.3.0", {"start": v(127.76, -5.08) * mm, "end": v(127.76, 0) * mm});
            skLineSegment(sketch, "E23.3.1", {"start": v(127.76, 0) * mm, "end": v(122.68, 0) * mm});
            skLineSegment(sketch, "E23.3.2", {"start": v(122.68, 0) * mm, "end": v(122.68, -5.08) * mm});
            skLineSegment(sketch, "E23.3.3", {"start": v(122.68, -5.08) * mm, "end": v(127.76, -5.08) * mm});
            skLineSegment(sketch, "E23.4.0", {"start": v(133.1, -5.08) * mm, "end": v(133.1, 0) * mm});
            skLineSegment(sketch, "E23.4.1", {"start": v(133.1, 0) * mm, "end": v(128.02, 0) * mm});
            skLineSegment(sketch, "E23.4.2", {"start": v(128.02, 0) * mm, "end": v(128.02, -5.08) * mm});
            skLineSegment(sketch, "E23.4.3", {"start": v(128.02, -5.08) * mm, "end": v(133.1, -5.08) * mm});
            skLineSegment(sketch, "E23.5.0", {"start": v(138.43, -5.08) * mm, "end": v(138.43, 0) * mm});
            skLineSegment(sketch, "E23.5.1", {"start": v(138.43, 0) * mm, "end": v(133.35, 0) * mm});
            skLineSegment(sketch, "E23.5.2", {"start": v(133.35, 0) * mm, "end": v(133.35, -5.08) * mm});
            skLineSegment(sketch, "E23.5.3", {"start": v(133.35, -5.08) * mm, "end": v(138.43, -5.08) * mm});
            skLineSegment(sketch, "E23.6.0", {"start": v(143.76, -5.08) * mm, "end": v(143.76, 0) * mm});
            skLineSegment(sketch, "E23.6.1", {"start": v(143.76, 0) * mm, "end": v(138.68, 0) * mm});
            skLineSegment(sketch, "E23.6.2", {"start": v(138.68, 0) * mm, "end": v(138.68, -5.08) * mm});
            skLineSegment(sketch, "E23.6.3", {"start": v(138.68, -5.08) * mm, "end": v(143.76, -5.08) * mm});
            skLineSegment(sketch, "E23.7.0", {"start": v(149.1, -5.08) * mm, "end": v(149.1, 0) * mm});
            skLineSegment(sketch, "E23.7.1", {"start": v(149.1, 0) * mm, "end": v(144.02, 0) * mm});
            skLineSegment(sketch, "E23.7.2", {"start": v(144.02, 0) * mm, "end": v(144.02, -5.08) * mm});
            skLineSegment(sketch, "E23.7.3", {"start": v(144.02, -5.08) * mm, "end": v(149.1, -5.08) * mm});
            skLineSegment(sketch, "E24.0.1.0", {"start": v(133.1, -5.33) * mm, "end": v(128.02, -5.33) * mm});
            skLineSegment(sketch, "E24.0.1.1", {"start": v(106.68, -5.33) * mm, "end": v(106.68, -10.41) * mm});
            skLineSegment(sketch, "E24.0.1.2", {"start": v(133.1, -10.41) * mm, "end": v(133.1, -5.33) * mm});
            skLineSegment(sketch, "E24.0.1.3", {"start": v(106.68, -10.41) * mm, "end": v(111.76, -10.41) * mm});
            skLineSegment(sketch, "E24.0.1.4", {"start": v(117.1, -10.41) * mm, "end": v(117.1, -5.33) * mm});
            skLineSegment(sketch, "E24.0.1.5", {"start": v(117.1, -5.33) * mm, "end": v(112.01, -5.33) * mm});
            skLineSegment(sketch, "E24.0.1.6", {"start": v(149.1, -10.41) * mm, "end": v(149.1, -5.33) * mm});
            skLineSegment(sketch, "E24.0.1.7", {"start": v(138.68, -10.41) * mm, "end": v(143.76, -10.41) * mm});
            skLineSegment(sketch, "E24.0.1.8", {"start": v(112.01, -5.33) * mm, "end": v(112.01, -10.41) * mm});
            skLineSegment(sketch, "E24.0.1.9", {"start": v(138.68, -5.33) * mm, "end": v(138.68, -10.41) * mm});
            skLineSegment(sketch, "E24.0.1.10", {"start": v(112.01, -10.41) * mm, "end": v(117.1, -10.41) * mm});
            skLineSegment(sketch, "E24.0.1.11", {"start": v(143.76, -5.33) * mm, "end": v(138.68, -5.33) * mm});
            skLineSegment(sketch, "E24.0.1.12", {"start": v(122.43, -10.41) * mm, "end": v(122.43, -5.33) * mm});
            skLineSegment(sketch, "E24.0.1.13", {"start": v(143.76, -10.41) * mm, "end": v(143.76, -5.33) * mm});
            skLineSegment(sketch, "E24.0.1.14", {"start": v(122.68, -10.41) * mm, "end": v(127.76, -10.41) * mm});
            skLineSegment(sketch, "E24.0.1.15", {"start": v(122.43, -5.33) * mm, "end": v(117.35, -5.33) * mm});
            skLineSegment(sketch, "E24.0.1.16", {"start": v(133.35, -10.41) * mm, "end": v(138.43, -10.41) * mm});
            skLineSegment(sketch, "E24.0.1.17", {"start": v(127.76, -5.33) * mm, "end": v(122.68, -5.33) * mm});
            skLineSegment(sketch, "E24.0.1.18", {"start": v(117.35, -5.33) * mm, "end": v(117.35, -10.41) * mm});
            skLineSegment(sketch, "E24.0.1.19", {"start": v(133.35, -5.33) * mm, "end": v(133.35, -10.41) * mm});
            skLineSegment(sketch, "E24.0.1.20", {"start": v(122.68, -5.33) * mm, "end": v(122.68, -10.41) * mm});
            skLineSegment(sketch, "E24.0.1.21", {"start": v(117.35, -10.41) * mm, "end": v(122.43, -10.41) * mm});
            skLineSegment(sketch, "E24.0.1.22", {"start": v(138.43, -5.33) * mm, "end": v(133.35, -5.33) * mm});
            skLineSegment(sketch, "E24.0.1.23", {"start": v(127.76, -10.41) * mm, "end": v(127.76, -5.33) * mm});
            skLineSegment(sketch, "E24.0.1.24", {"start": v(138.43, -10.41) * mm, "end": v(138.43, -5.33) * mm});
            skLineSegment(sketch, "E24.0.1.25", {"start": v(144.02, -5.33) * mm, "end": v(144.02, -10.41) * mm});
            skLineSegment(sketch, "E24.0.1.26", {"start": v(128.02, -10.41) * mm, "end": v(133.1, -10.41) * mm});
            skLineSegment(sketch, "E24.0.1.27", {"start": v(111.76, -10.41) * mm, "end": v(111.76, -5.33) * mm});
            skLineSegment(sketch, "E24.0.1.28", {"start": v(149.1, -5.33) * mm, "end": v(144.02, -5.33) * mm});
            skLineSegment(sketch, "E24.0.1.29", {"start": v(128.02, -5.33) * mm, "end": v(128.02, -10.41) * mm});
            skLineSegment(sketch, "E24.0.1.30", {"start": v(144.02, -10.41) * mm, "end": v(149.1, -10.41) * mm});
            skLineSegment(sketch, "E24.0.1.31", {"start": v(111.76, -5.33) * mm, "end": v(106.68, -5.33) * mm});
            skLineSegment(sketch, "E24.0.2.0", {"start": v(133.1, -10.67) * mm, "end": v(128.02, -10.67) * mm});
            skLineSegment(sketch, "E24.0.2.1", {"start": v(106.68, -10.67) * mm, "end": v(106.68, -15.75) * mm});
            skLineSegment(sketch, "E24.0.2.2", {"start": v(133.1, -15.75) * mm, "end": v(133.1, -10.67) * mm});
            skLineSegment(sketch, "E24.0.2.3", {"start": v(106.68, -15.75) * mm, "end": v(111.76, -15.75) * mm});
            skLineSegment(sketch, "E24.0.2.4", {"start": v(117.1, -15.75) * mm, "end": v(117.1, -10.67) * mm});
            skLineSegment(sketch, "E24.0.2.5", {"start": v(117.1, -10.67) * mm, "end": v(112.01, -10.67) * mm});
            skLineSegment(sketch, "E24.0.2.6", {"start": v(149.1, -15.75) * mm, "end": v(149.1, -10.67) * mm});
            skLineSegment(sketch, "E24.0.2.7", {"start": v(138.68, -15.75) * mm, "end": v(143.76, -15.75) * mm});
            skLineSegment(sketch, "E24.0.2.8", {"start": v(112.01, -10.67) * mm, "end": v(112.01, -15.75) * mm});
            skLineSegment(sketch, "E24.0.2.9", {"start": v(138.68, -10.67) * mm, "end": v(138.68, -15.75) * mm});
            skLineSegment(sketch, "E24.0.2.10", {"start": v(112.01, -15.75) * mm, "end": v(117.1, -15.75) * mm});
            skLineSegment(sketch, "E24.0.2.11", {"start": v(143.76, -10.67) * mm, "end": v(138.68, -10.67) * mm});
            skLineSegment(sketch, "E24.0.2.12", {"start": v(122.43, -15.75) * mm, "end": v(122.43, -10.67) * mm});
            skLineSegment(sketch, "E24.0.2.13", {"start": v(143.76, -15.75) * mm, "end": v(143.76, -10.67) * mm});
            skLineSegment(sketch, "E24.0.2.14", {"start": v(122.68, -15.75) * mm, "end": v(127.76, -15.75) * mm});
            skLineSegment(sketch, "E24.0.2.15", {"start": v(122.43, -10.67) * mm, "end": v(117.35, -10.67) * mm});
            skLineSegment(sketch, "E24.0.2.16", {"start": v(133.35, -15.75) * mm, "end": v(138.43, -15.75) * mm});
            skLineSegment(sketch, "E24.0.2.17", {"start": v(127.76, -10.67) * mm, "end": v(122.68, -10.67) * mm});
            skLineSegment(sketch, "E24.0.2.18", {"start": v(117.35, -10.67) * mm, "end": v(117.35, -15.75) * mm});
            skLineSegment(sketch, "E24.0.2.19", {"start": v(133.35, -10.67) * mm, "end": v(133.35, -15.75) * mm});
            skLineSegment(sketch, "E24.0.2.20", {"start": v(122.68, -10.67) * mm, "end": v(122.68, -15.75) * mm});
            skLineSegment(sketch, "E24.0.2.21", {"start": v(117.35, -15.75) * mm, "end": v(122.43, -15.75) * mm});
            skLineSegment(sketch, "E24.0.2.22", {"start": v(138.43, -10.67) * mm, "end": v(133.35, -10.67) * mm});
            skLineSegment(sketch, "E24.0.2.23", {"start": v(127.76, -15.75) * mm, "end": v(127.76, -10.67) * mm});
            skLineSegment(sketch, "E24.0.2.24", {"start": v(138.43, -15.75) * mm, "end": v(138.43, -10.67) * mm});
            skLineSegment(sketch, "E24.0.2.25", {"start": v(144.02, -10.67) * mm, "end": v(144.02, -15.75) * mm});
            skLineSegment(sketch, "E24.0.2.26", {"start": v(128.02, -15.75) * mm, "end": v(133.1, -15.75) * mm});
            skLineSegment(sketch, "E24.0.2.27", {"start": v(111.76, -15.75) * mm, "end": v(111.76, -10.67) * mm});
            skLineSegment(sketch, "E24.0.2.28", {"start": v(149.1, -10.67) * mm, "end": v(144.02, -10.67) * mm});
            skLineSegment(sketch, "E24.0.2.29", {"start": v(128.02, -10.67) * mm, "end": v(128.02, -15.75) * mm});
            skLineSegment(sketch, "E24.0.2.30", {"start": v(144.02, -15.75) * mm, "end": v(149.1, -15.75) * mm});
            skLineSegment(sketch, "E24.0.2.31", {"start": v(111.76, -10.67) * mm, "end": v(106.68, -10.67) * mm});
            skLineSegment(sketch, "E24.0.3.0", {"start": v(133.1, -16) * mm, "end": v(128.02, -16) * mm});
            skLineSegment(sketch, "E24.0.3.1", {"start": v(106.68, -16) * mm, "end": v(106.68, -21.08) * mm});
            skLineSegment(sketch, "E24.0.3.2", {"start": v(133.1, -21.08) * mm, "end": v(133.1, -16) * mm});
            skLineSegment(sketch, "E24.0.3.3", {"start": v(106.68, -21.08) * mm, "end": v(111.76, -21.08) * mm});
            skLineSegment(sketch, "E24.0.3.4", {"start": v(117.1, -21.08) * mm, "end": v(117.1, -16) * mm});
            skLineSegment(sketch, "E24.0.3.5", {"start": v(117.1, -16) * mm, "end": v(112.01, -16) * mm});
            skLineSegment(sketch, "E24.0.3.6", {"start": v(149.1, -21.08) * mm, "end": v(149.1, -16) * mm});
            skLineSegment(sketch, "E24.0.3.7", {"start": v(138.68, -21.08) * mm, "end": v(143.76, -21.08) * mm});
            skLineSegment(sketch, "E24.0.3.8", {"start": v(112.01, -16) * mm, "end": v(112.01, -21.08) * mm});
            skLineSegment(sketch, "E24.0.3.9", {"start": v(138.68, -16) * mm, "end": v(138.68, -21.08) * mm});
            skLineSegment(sketch, "E24.0.3.10", {"start": v(112.01, -21.08) * mm, "end": v(117.1, -21.08) * mm});
            skLineSegment(sketch, "E24.0.3.11", {"start": v(143.76, -16) * mm, "end": v(138.68, -16) * mm});
            skLineSegment(sketch, "E24.0.3.12", {"start": v(122.43, -21.08) * mm, "end": v(122.43, -16) * mm});
            skLineSegment(sketch, "E24.0.3.13", {"start": v(143.76, -21.08) * mm, "end": v(143.76, -16) * mm});
            skLineSegment(sketch, "E24.0.3.14", {"start": v(122.68, -21.08) * mm, "end": v(127.76, -21.08) * mm});
            skLineSegment(sketch, "E24.0.3.15", {"start": v(122.43, -16) * mm, "end": v(117.35, -16) * mm});
            skLineSegment(sketch, "E24.0.3.16", {"start": v(133.35, -21.08) * mm, "end": v(138.43, -21.08) * mm});
            skLineSegment(sketch, "E24.0.3.17", {"start": v(127.76, -16) * mm, "end": v(122.68, -16) * mm});
            skLineSegment(sketch, "E24.0.3.18", {"start": v(117.35, -16) * mm, "end": v(117.35, -21.08) * mm});
            skLineSegment(sketch, "E24.0.3.19", {"start": v(133.35, -16) * mm, "end": v(133.35, -21.08) * mm});
            skLineSegment(sketch, "E24.0.3.20", {"start": v(122.68, -16) * mm, "end": v(122.68, -21.08) * mm});
            skLineSegment(sketch, "E24.0.3.21", {"start": v(117.35, -21.08) * mm, "end": v(122.43, -21.08) * mm});
            skLineSegment(sketch, "E24.0.3.22", {"start": v(138.43, -16) * mm, "end": v(133.35, -16) * mm});
            skLineSegment(sketch, "E24.0.3.23", {"start": v(127.76, -21.08) * mm, "end": v(127.76, -16) * mm});
            skLineSegment(sketch, "E24.0.3.24", {"start": v(138.43, -21.08) * mm, "end": v(138.43, -16) * mm});
            skLineSegment(sketch, "E24.0.3.25", {"start": v(144.02, -16) * mm, "end": v(144.02, -21.08) * mm});
            skLineSegment(sketch, "E24.0.3.26", {"start": v(128.02, -21.08) * mm, "end": v(133.1, -21.08) * mm});
            skLineSegment(sketch, "E24.0.3.27", {"start": v(111.76, -21.08) * mm, "end": v(111.76, -16) * mm});
            skLineSegment(sketch, "E24.0.3.28", {"start": v(149.1, -16) * mm, "end": v(144.02, -16) * mm});
            skLineSegment(sketch, "E24.0.3.29", {"start": v(128.02, -16) * mm, "end": v(128.02, -21.08) * mm});
            skLineSegment(sketch, "E24.0.3.30", {"start": v(144.02, -21.08) * mm, "end": v(149.1, -21.08) * mm});
            skLineSegment(sketch, "E24.0.3.31", {"start": v(111.76, -16) * mm, "end": v(106.68, -16) * mm});
            skLineSegment(sketch, "E24.0.4.0", {"start": v(133.1, -21.34) * mm, "end": v(128.02, -21.34) * mm});
            skLineSegment(sketch, "E24.0.4.1", {"start": v(106.68, -21.34) * mm, "end": v(106.68, -26.42) * mm});
            skLineSegment(sketch, "E24.0.4.2", {"start": v(133.1, -26.42) * mm, "end": v(133.1, -21.34) * mm});
            skLineSegment(sketch, "E24.0.4.3", {"start": v(106.68, -26.42) * mm, "end": v(111.76, -26.42) * mm});
            skLineSegment(sketch, "E24.0.4.4", {"start": v(117.1, -26.42) * mm, "end": v(117.1, -21.34) * mm});
            skLineSegment(sketch, "E24.0.4.5", {"start": v(117.1, -21.34) * mm, "end": v(112.01, -21.34) * mm});
            skLineSegment(sketch, "E24.0.4.6", {"start": v(149.1, -26.42) * mm, "end": v(149.1, -21.34) * mm});
            skLineSegment(sketch, "E24.0.4.7", {"start": v(138.68, -26.42) * mm, "end": v(143.76, -26.42) * mm});
            skLineSegment(sketch, "E24.0.4.8", {"start": v(112.01, -21.34) * mm, "end": v(112.01, -26.42) * mm});
            skLineSegment(sketch, "E24.0.4.9", {"start": v(138.68, -21.34) * mm, "end": v(138.68, -26.42) * mm});
            skLineSegment(sketch, "E24.0.4.10", {"start": v(112.01, -26.42) * mm, "end": v(117.1, -26.42) * mm});
            skLineSegment(sketch, "E24.0.4.11", {"start": v(143.76, -21.34) * mm, "end": v(138.68, -21.34) * mm});
            skLineSegment(sketch, "E24.0.4.12", {"start": v(122.43, -26.42) * mm, "end": v(122.43, -21.34) * mm});
            skLineSegment(sketch, "E24.0.4.13", {"start": v(143.76, -26.42) * mm, "end": v(143.76, -21.34) * mm});
            skLineSegment(sketch, "E24.0.4.14", {"start": v(122.68, -26.42) * mm, "end": v(127.76, -26.42) * mm});
            skLineSegment(sketch, "E24.0.4.15", {"start": v(122.43, -21.34) * mm, "end": v(117.35, -21.34) * mm});
            skLineSegment(sketch, "E24.0.4.16", {"start": v(133.35, -26.42) * mm, "end": v(138.43, -26.42) * mm});
            skLineSegment(sketch, "E24.0.4.17", {"start": v(127.76, -21.34) * mm, "end": v(122.68, -21.34) * mm});
            skLineSegment(sketch, "E24.0.4.18", {"start": v(117.35, -21.34) * mm, "end": v(117.35, -26.42) * mm});
            skLineSegment(sketch, "E24.0.4.19", {"start": v(133.35, -21.34) * mm, "end": v(133.35, -26.42) * mm});
            skLineSegment(sketch, "E24.0.4.20", {"start": v(122.68, -21.34) * mm, "end": v(122.68, -26.42) * mm});
            skLineSegment(sketch, "E24.0.4.21", {"start": v(117.35, -26.42) * mm, "end": v(122.43, -26.42) * mm});
            skLineSegment(sketch, "E24.0.4.22", {"start": v(138.43, -21.34) * mm, "end": v(133.35, -21.34) * mm});
            skLineSegment(sketch, "E24.0.4.23", {"start": v(127.76, -26.42) * mm, "end": v(127.76, -21.34) * mm});
            skLineSegment(sketch, "E24.0.4.24", {"start": v(138.43, -26.42) * mm, "end": v(138.43, -21.34) * mm});
            skLineSegment(sketch, "E24.0.4.25", {"start": v(144.02, -21.34) * mm, "end": v(144.02, -26.42) * mm});
            skLineSegment(sketch, "E24.0.4.26", {"start": v(128.02, -26.42) * mm, "end": v(133.1, -26.42) * mm});
            skLineSegment(sketch, "E24.0.4.27", {"start": v(111.76, -26.42) * mm, "end": v(111.76, -21.34) * mm});
            skLineSegment(sketch, "E24.0.4.28", {"start": v(149.1, -21.34) * mm, "end": v(144.02, -21.34) * mm});
            skLineSegment(sketch, "E24.0.4.29", {"start": v(128.02, -21.34) * mm, "end": v(128.02, -26.42) * mm});
            skLineSegment(sketch, "E24.0.4.30", {"start": v(144.02, -26.42) * mm, "end": v(149.1, -26.42) * mm});
            skLineSegment(sketch, "E24.0.4.31", {"start": v(111.76, -21.34) * mm, "end": v(106.68, -21.34) * mm});
            skLineSegment(sketch, "E24.0.5.0", {"start": v(133.1, -26.67) * mm, "end": v(128.02, -26.67) * mm});
            skLineSegment(sketch, "E24.0.5.1", {"start": v(106.68, -26.67) * mm, "end": v(106.68, -31.75) * mm});
            skLineSegment(sketch, "E24.0.5.2", {"start": v(133.1, -31.75) * mm, "end": v(133.1, -26.67) * mm});
            skLineSegment(sketch, "E24.0.5.3", {"start": v(106.68, -31.75) * mm, "end": v(111.76, -31.75) * mm});
            skLineSegment(sketch, "E24.0.5.4", {"start": v(117.1, -31.75) * mm, "end": v(117.1, -26.67) * mm});
            skLineSegment(sketch, "E24.0.5.5", {"start": v(117.1, -26.67) * mm, "end": v(112.01, -26.67) * mm});
            skLineSegment(sketch, "E24.0.5.6", {"start": v(149.1, -31.75) * mm, "end": v(149.1, -26.67) * mm});
            skLineSegment(sketch, "E24.0.5.7", {"start": v(138.68, -31.75) * mm, "end": v(143.76, -31.75) * mm});
            skLineSegment(sketch, "E24.0.5.8", {"start": v(112.01, -26.67) * mm, "end": v(112.01, -31.75) * mm});
            skLineSegment(sketch, "E24.0.5.9", {"start": v(138.68, -26.67) * mm, "end": v(138.68, -31.75) * mm});
            skLineSegment(sketch, "E24.0.5.10", {"start": v(112.01, -31.75) * mm, "end": v(117.1, -31.75) * mm});
            skLineSegment(sketch, "E24.0.5.11", {"start": v(143.76, -26.67) * mm, "end": v(138.68, -26.67) * mm});
            skLineSegment(sketch, "E24.0.5.12", {"start": v(122.43, -31.75) * mm, "end": v(122.43, -26.67) * mm});
            skLineSegment(sketch, "E24.0.5.13", {"start": v(143.76, -31.75) * mm, "end": v(143.76, -26.67) * mm});
            skLineSegment(sketch, "E24.0.5.14", {"start": v(122.68, -31.75) * mm, "end": v(127.76, -31.75) * mm});
            skLineSegment(sketch, "E24.0.5.15", {"start": v(122.43, -26.67) * mm, "end": v(117.35, -26.67) * mm});
            skLineSegment(sketch, "E24.0.5.16", {"start": v(133.35, -31.75) * mm, "end": v(138.43, -31.75) * mm});
            skLineSegment(sketch, "E24.0.5.17", {"start": v(127.76, -26.67) * mm, "end": v(122.68, -26.67) * mm});
            skLineSegment(sketch, "E24.0.5.18", {"start": v(117.35, -26.67) * mm, "end": v(117.35, -31.75) * mm});
            skLineSegment(sketch, "E24.0.5.19", {"start": v(133.35, -26.67) * mm, "end": v(133.35, -31.75) * mm});
            skLineSegment(sketch, "E24.0.5.20", {"start": v(122.68, -26.67) * mm, "end": v(122.68, -31.75) * mm});
            skLineSegment(sketch, "E24.0.5.21", {"start": v(117.35, -31.75) * mm, "end": v(122.43, -31.75) * mm});
            skLineSegment(sketch, "E24.0.5.22", {"start": v(138.43, -26.67) * mm, "end": v(133.35, -26.67) * mm});
            skLineSegment(sketch, "E24.0.5.23", {"start": v(127.76, -31.75) * mm, "end": v(127.76, -26.67) * mm});
            skLineSegment(sketch, "E24.0.5.24", {"start": v(138.43, -31.75) * mm, "end": v(138.43, -26.67) * mm});
            skLineSegment(sketch, "E24.0.5.25", {"start": v(144.02, -26.67) * mm, "end": v(144.02, -31.75) * mm});
            skLineSegment(sketch, "E24.0.5.26", {"start": v(128.02, -31.75) * mm, "end": v(133.1, -31.75) * mm});
            skLineSegment(sketch, "E24.0.5.27", {"start": v(111.76, -31.75) * mm, "end": v(111.76, -26.67) * mm});
            skLineSegment(sketch, "E24.0.5.28", {"start": v(149.1, -26.67) * mm, "end": v(144.02, -26.67) * mm});
            skLineSegment(sketch, "E24.0.5.29", {"start": v(128.02, -26.67) * mm, "end": v(128.02, -31.75) * mm});
            skLineSegment(sketch, "E24.0.5.30", {"start": v(144.02, -31.75) * mm, "end": v(149.1, -31.75) * mm});
            skLineSegment(sketch, "E24.0.5.31", {"start": v(111.76, -26.67) * mm, "end": v(106.68, -26.67) * mm});
            skLineSegment(sketch, "E24.0.6.0", {"start": v(133.1, -32) * mm, "end": v(128.02, -32) * mm});
            skLineSegment(sketch, "E24.0.6.1", {"start": v(106.68, -32) * mm, "end": v(106.68, -37.08) * mm});
            skLineSegment(sketch, "E24.0.6.2", {"start": v(133.1, -37.08) * mm, "end": v(133.1, -32) * mm});
            skLineSegment(sketch, "E24.0.6.3", {"start": v(106.68, -37.08) * mm, "end": v(111.76, -37.08) * mm});
            skLineSegment(sketch, "E24.0.6.4", {"start": v(117.1, -37.08) * mm, "end": v(117.1, -32) * mm});
            skLineSegment(sketch, "E24.0.6.5", {"start": v(117.1, -32) * mm, "end": v(112.01, -32) * mm});
            skLineSegment(sketch, "E24.0.6.6", {"start": v(149.1, -37.08) * mm, "end": v(149.1, -32) * mm});
            skLineSegment(sketch, "E24.0.6.7", {"start": v(138.68, -37.08) * mm, "end": v(143.76, -37.08) * mm});
            skLineSegment(sketch, "E24.0.6.8", {"start": v(112.01, -32) * mm, "end": v(112.01, -37.08) * mm});
            skLineSegment(sketch, "E24.0.6.9", {"start": v(138.68, -32) * mm, "end": v(138.68, -37.08) * mm});
            skLineSegment(sketch, "E24.0.6.10", {"start": v(112.01, -37.08) * mm, "end": v(117.1, -37.08) * mm});
            skLineSegment(sketch, "E24.0.6.11", {"start": v(143.76, -32) * mm, "end": v(138.68, -32) * mm});
            skLineSegment(sketch, "E24.0.6.12", {"start": v(122.43, -37.08) * mm, "end": v(122.43, -32) * mm});
            skLineSegment(sketch, "E24.0.6.13", {"start": v(143.76, -37.08) * mm, "end": v(143.76, -32) * mm});
            skLineSegment(sketch, "E24.0.6.14", {"start": v(122.68, -37.08) * mm, "end": v(127.76, -37.08) * mm});
            skLineSegment(sketch, "E24.0.6.15", {"start": v(122.43, -32) * mm, "end": v(117.35, -32) * mm});
            skLineSegment(sketch, "E24.0.6.16", {"start": v(133.35, -37.08) * mm, "end": v(138.43, -37.08) * mm});
            skLineSegment(sketch, "E24.0.6.17", {"start": v(127.76, -32) * mm, "end": v(122.68, -32) * mm});
            skLineSegment(sketch, "E24.0.6.18", {"start": v(117.35, -32) * mm, "end": v(117.35, -37.08) * mm});
            skLineSegment(sketch, "E24.0.6.19", {"start": v(133.35, -32) * mm, "end": v(133.35, -37.08) * mm});
            skLineSegment(sketch, "E24.0.6.20", {"start": v(122.68, -32) * mm, "end": v(122.68, -37.08) * mm});
            skLineSegment(sketch, "E24.0.6.21", {"start": v(117.35, -37.08) * mm, "end": v(122.43, -37.08) * mm});
            skLineSegment(sketch, "E24.0.6.22", {"start": v(138.43, -32) * mm, "end": v(133.35, -32) * mm});
            skLineSegment(sketch, "E24.0.6.23", {"start": v(127.76, -37.08) * mm, "end": v(127.76, -32) * mm});
            skLineSegment(sketch, "E24.0.6.24", {"start": v(138.43, -37.08) * mm, "end": v(138.43, -32) * mm});
            skLineSegment(sketch, "E24.0.6.25", {"start": v(144.02, -32) * mm, "end": v(144.02, -37.08) * mm});
            skLineSegment(sketch, "E24.0.6.26", {"start": v(128.02, -37.08) * mm, "end": v(133.1, -37.08) * mm});
            skLineSegment(sketch, "E24.0.6.27", {"start": v(111.76, -37.08) * mm, "end": v(111.76, -32) * mm});
            skLineSegment(sketch, "E24.0.6.28", {"start": v(149.1, -32) * mm, "end": v(144.02, -32) * mm});
            skLineSegment(sketch, "E24.0.6.29", {"start": v(128.02, -32) * mm, "end": v(128.02, -37.08) * mm});
            skLineSegment(sketch, "E24.0.6.30", {"start": v(144.02, -37.08) * mm, "end": v(149.1, -37.08) * mm});
            skLineSegment(sketch, "E24.0.6.31", {"start": v(111.76, -32) * mm, "end": v(106.68, -32) * mm});
            skLineSegment(sketch, "E24.0.7.0", {"start": v(133.1, -37.34) * mm, "end": v(128.02, -37.34) * mm});
            skLineSegment(sketch, "E24.0.7.1", {"start": v(106.68, -37.34) * mm, "end": v(106.68, -42.42) * mm});
            skLineSegment(sketch, "E24.0.7.2", {"start": v(133.1, -42.42) * mm, "end": v(133.1, -37.34) * mm});
            skLineSegment(sketch, "E24.0.7.3", {"start": v(106.68, -42.42) * mm, "end": v(111.76, -42.42) * mm});
            skLineSegment(sketch, "E24.0.7.4", {"start": v(117.1, -42.42) * mm, "end": v(117.1, -37.34) * mm});
            skLineSegment(sketch, "E24.0.7.5", {"start": v(117.1, -37.34) * mm, "end": v(112.01, -37.34) * mm});
            skLineSegment(sketch, "E24.0.7.6", {"start": v(149.1, -42.42) * mm, "end": v(149.1, -37.34) * mm});
            skLineSegment(sketch, "E24.0.7.7", {"start": v(138.68, -42.42) * mm, "end": v(143.76, -42.42) * mm});
            skLineSegment(sketch, "E24.0.7.8", {"start": v(112.01, -37.34) * mm, "end": v(112.01, -42.42) * mm});
            skLineSegment(sketch, "E24.0.7.9", {"start": v(138.68, -37.34) * mm, "end": v(138.68, -42.42) * mm});
            skLineSegment(sketch, "E24.0.7.10", {"start": v(112.01, -42.42) * mm, "end": v(117.1, -42.42) * mm});
            skLineSegment(sketch, "E24.0.7.11", {"start": v(143.76, -37.34) * mm, "end": v(138.68, -37.34) * mm});
            skLineSegment(sketch, "E24.0.7.12", {"start": v(122.43, -42.42) * mm, "end": v(122.43, -37.34) * mm});
            skLineSegment(sketch, "E24.0.7.13", {"start": v(143.76, -42.42) * mm, "end": v(143.76, -37.34) * mm});
            skLineSegment(sketch, "E24.0.7.14", {"start": v(122.68, -42.42) * mm, "end": v(127.76, -42.42) * mm});
            skLineSegment(sketch, "E24.0.7.15", {"start": v(122.43, -37.34) * mm, "end": v(117.35, -37.34) * mm});
            skLineSegment(sketch, "E24.0.7.16", {"start": v(133.35, -42.42) * mm, "end": v(138.43, -42.42) * mm});
            skLineSegment(sketch, "E24.0.7.17", {"start": v(127.76, -37.34) * mm, "end": v(122.68, -37.34) * mm});
            skLineSegment(sketch, "E24.0.7.18", {"start": v(117.35, -37.34) * mm, "end": v(117.35, -42.42) * mm});
            skLineSegment(sketch, "E24.0.7.19", {"start": v(133.35, -37.34) * mm, "end": v(133.35, -42.42) * mm});
            skLineSegment(sketch, "E24.0.7.20", {"start": v(122.68, -37.34) * mm, "end": v(122.68, -42.42) * mm});
            skLineSegment(sketch, "E24.0.7.21", {"start": v(117.35, -42.42) * mm, "end": v(122.43, -42.42) * mm});
            skLineSegment(sketch, "E24.0.7.22", {"start": v(138.43, -37.34) * mm, "end": v(133.35, -37.34) * mm});
            skLineSegment(sketch, "E24.0.7.23", {"start": v(127.76, -42.42) * mm, "end": v(127.76, -37.34) * mm});
            skLineSegment(sketch, "E24.0.7.24", {"start": v(138.43, -42.42) * mm, "end": v(138.43, -37.34) * mm});
            skLineSegment(sketch, "E24.0.7.25", {"start": v(144.02, -37.34) * mm, "end": v(144.02, -42.42) * mm});
            skLineSegment(sketch, "E24.0.7.26", {"start": v(128.02, -42.42) * mm, "end": v(133.1, -42.42) * mm});
            skLineSegment(sketch, "E24.0.7.27", {"start": v(111.76, -42.42) * mm, "end": v(111.76, -37.34) * mm});
            skLineSegment(sketch, "E24.0.7.28", {"start": v(149.1, -37.34) * mm, "end": v(144.02, -37.34) * mm});
            skLineSegment(sketch, "E24.0.7.29", {"start": v(128.02, -37.34) * mm, "end": v(128.02, -42.42) * mm});
            skLineSegment(sketch, "E24.0.7.30", {"start": v(144.02, -42.42) * mm, "end": v(149.1, -42.42) * mm});
            skLineSegment(sketch, "E24.0.7.31", {"start": v(111.76, -37.34) * mm, "end": v(106.68, -37.34) * mm});
            skLineSegment(sketch, "E24.0.8.0", {"start": v(133.1, -42.67) * mm, "end": v(128.02, -42.67) * mm});
            skLineSegment(sketch, "E24.0.8.1", {"start": v(106.68, -42.67) * mm, "end": v(106.68, -47.75) * mm});
            skLineSegment(sketch, "E24.0.8.2", {"start": v(133.1, -47.75) * mm, "end": v(133.1, -42.67) * mm});
            skLineSegment(sketch, "E24.0.8.3", {"start": v(106.68, -47.75) * mm, "end": v(111.76, -47.75) * mm});
            skLineSegment(sketch, "E24.0.8.4", {"start": v(117.1, -47.75) * mm, "end": v(117.1, -42.67) * mm});
            skLineSegment(sketch, "E24.0.8.5", {"start": v(117.1, -42.67) * mm, "end": v(112.01, -42.67) * mm});
            skLineSegment(sketch, "E24.0.8.6", {"start": v(149.1, -47.75) * mm, "end": v(149.1, -42.67) * mm});
            skLineSegment(sketch, "E24.0.8.7", {"start": v(138.68, -47.75) * mm, "end": v(143.76, -47.75) * mm});
            skLineSegment(sketch, "E24.0.8.8", {"start": v(112.01, -42.67) * mm, "end": v(112.01, -47.75) * mm});
            skLineSegment(sketch, "E24.0.8.9", {"start": v(138.68, -42.67) * mm, "end": v(138.68, -47.75) * mm});
            skLineSegment(sketch, "E24.0.8.10", {"start": v(112.01, -47.75) * mm, "end": v(117.1, -47.75) * mm});
            skLineSegment(sketch, "E24.0.8.11", {"start": v(143.76, -42.67) * mm, "end": v(138.68, -42.67) * mm});
            skLineSegment(sketch, "E24.0.8.12", {"start": v(122.43, -47.75) * mm, "end": v(122.43, -42.67) * mm});
            skLineSegment(sketch, "E24.0.8.13", {"start": v(143.76, -47.75) * mm, "end": v(143.76, -42.67) * mm});
            skLineSegment(sketch, "E24.0.8.14", {"start": v(122.68, -47.75) * mm, "end": v(127.76, -47.75) * mm});
            skLineSegment(sketch, "E24.0.8.15", {"start": v(122.43, -42.67) * mm, "end": v(117.35, -42.67) * mm});
            skLineSegment(sketch, "E24.0.8.16", {"start": v(133.35, -47.75) * mm, "end": v(138.43, -47.75) * mm});
            skLineSegment(sketch, "E24.0.8.17", {"start": v(127.76, -42.67) * mm, "end": v(122.68, -42.67) * mm});
            skLineSegment(sketch, "E24.0.8.18", {"start": v(117.35, -42.67) * mm, "end": v(117.35, -47.75) * mm});
            skLineSegment(sketch, "E24.0.8.19", {"start": v(133.35, -42.67) * mm, "end": v(133.35, -47.75) * mm});
            skLineSegment(sketch, "E24.0.8.20", {"start": v(122.68, -42.67) * mm, "end": v(122.68, -47.75) * mm});
            skLineSegment(sketch, "E24.0.8.21", {"start": v(117.35, -47.75) * mm, "end": v(122.43, -47.75) * mm});
            skLineSegment(sketch, "E24.0.8.22", {"start": v(138.43, -42.67) * mm, "end": v(133.35, -42.67) * mm});
            skLineSegment(sketch, "E24.0.8.23", {"start": v(127.76, -47.75) * mm, "end": v(127.76, -42.67) * mm});
            skLineSegment(sketch, "E24.0.8.24", {"start": v(138.43, -47.75) * mm, "end": v(138.43, -42.67) * mm});
            skLineSegment(sketch, "E24.0.8.25", {"start": v(144.02, -42.67) * mm, "end": v(144.02, -47.75) * mm});
            skLineSegment(sketch, "E24.0.8.26", {"start": v(128.02, -47.75) * mm, "end": v(133.1, -47.75) * mm});
            skLineSegment(sketch, "E24.0.8.27", {"start": v(111.76, -47.75) * mm, "end": v(111.76, -42.67) * mm});
            skLineSegment(sketch, "E24.0.8.28", {"start": v(149.1, -42.67) * mm, "end": v(144.02, -42.67) * mm});
            skLineSegment(sketch, "E24.0.8.29", {"start": v(128.02, -42.67) * mm, "end": v(128.02, -47.75) * mm});
            skLineSegment(sketch, "E24.0.8.30", {"start": v(144.02, -47.75) * mm, "end": v(149.1, -47.75) * mm});
            skLineSegment(sketch, "E24.0.8.31", {"start": v(111.76, -42.67) * mm, "end": v(106.68, -42.67) * mm});
            skLineSegment(sketch, "E24.0.9.0", {"start": v(133.1, -48) * mm, "end": v(128.02, -48) * mm});
            skLineSegment(sketch, "E24.0.9.1", {"start": v(106.68, -48) * mm, "end": v(106.68, -53.09) * mm});
            skLineSegment(sketch, "E24.0.9.2", {"start": v(133.1, -53.09) * mm, "end": v(133.1, -48) * mm});
            skLineSegment(sketch, "E24.0.9.3", {"start": v(106.68, -53.09) * mm, "end": v(111.76, -53.09) * mm});
            skLineSegment(sketch, "E24.0.9.4", {"start": v(117.1, -53.09) * mm, "end": v(117.1, -48) * mm});
            skLineSegment(sketch, "E24.0.9.5", {"start": v(117.1, -48) * mm, "end": v(112.01, -48) * mm});
            skLineSegment(sketch, "E24.0.9.6", {"start": v(149.1, -53.09) * mm, "end": v(149.1, -48) * mm});
            skLineSegment(sketch, "E24.0.9.7", {"start": v(138.68, -53.09) * mm, "end": v(143.76, -53.09) * mm});
            skLineSegment(sketch, "E24.0.9.8", {"start": v(112.01, -48) * mm, "end": v(112.01, -53.09) * mm});
            skLineSegment(sketch, "E24.0.9.9", {"start": v(138.68, -48) * mm, "end": v(138.68, -53.09) * mm});
            skLineSegment(sketch, "E24.0.9.10", {"start": v(112.01, -53.09) * mm, "end": v(117.1, -53.09) * mm});
            skLineSegment(sketch, "E24.0.9.11", {"start": v(143.76, -48) * mm, "end": v(138.68, -48) * mm});
            skLineSegment(sketch, "E24.0.9.12", {"start": v(122.43, -53.09) * mm, "end": v(122.43, -48) * mm});
            skLineSegment(sketch, "E24.0.9.13", {"start": v(143.76, -53.09) * mm, "end": v(143.76, -48) * mm});
            skLineSegment(sketch, "E24.0.9.14", {"start": v(122.68, -53.09) * mm, "end": v(127.76, -53.09) * mm});
            skLineSegment(sketch, "E24.0.9.15", {"start": v(122.43, -48) * mm, "end": v(117.35, -48) * mm});
            skLineSegment(sketch, "E24.0.9.16", {"start": v(133.35, -53.09) * mm, "end": v(138.43, -53.09) * mm});
            skLineSegment(sketch, "E24.0.9.17", {"start": v(127.76, -48) * mm, "end": v(122.68, -48) * mm});
            skLineSegment(sketch, "E24.0.9.18", {"start": v(117.35, -48) * mm, "end": v(117.35, -53.09) * mm});
            skLineSegment(sketch, "E24.0.9.19", {"start": v(133.35, -48) * mm, "end": v(133.35, -53.09) * mm});
            skLineSegment(sketch, "E24.0.9.20", {"start": v(122.68, -48) * mm, "end": v(122.68, -53.09) * mm});
            skLineSegment(sketch, "E24.0.9.21", {"start": v(117.35, -53.09) * mm, "end": v(122.43, -53.09) * mm});
            skLineSegment(sketch, "E24.0.9.22", {"start": v(138.43, -48) * mm, "end": v(133.35, -48) * mm});
            skLineSegment(sketch, "E24.0.9.23", {"start": v(127.76, -53.09) * mm, "end": v(127.76, -48) * mm});
            skLineSegment(sketch, "E24.0.9.24", {"start": v(138.43, -53.09) * mm, "end": v(138.43, -48) * mm});
            skLineSegment(sketch, "E24.0.9.25", {"start": v(144.02, -48) * mm, "end": v(144.02, -53.09) * mm});
            skLineSegment(sketch, "E24.0.9.26", {"start": v(128.02, -53.09) * mm, "end": v(133.1, -53.09) * mm});
            skLineSegment(sketch, "E24.0.9.27", {"start": v(111.76, -53.09) * mm, "end": v(111.76, -48) * mm});
            skLineSegment(sketch, "E24.0.9.28", {"start": v(149.1, -48) * mm, "end": v(144.02, -48) * mm});
            skLineSegment(sketch, "E24.0.9.29", {"start": v(128.02, -48) * mm, "end": v(128.02, -53.09) * mm});
            skLineSegment(sketch, "E24.0.9.30", {"start": v(144.02, -53.09) * mm, "end": v(149.1, -53.09) * mm});
            skLineSegment(sketch, "E24.0.9.31", {"start": v(111.76, -48) * mm, "end": v(106.68, -48) * mm});
            skLineSegment(sketch, "E24.0.10.0", {"start": v(133.1, -53.34) * mm, "end": v(128.02, -53.34) * mm});
            skLineSegment(sketch, "E24.0.10.1", {"start": v(106.68, -53.34) * mm, "end": v(106.68, -58.42) * mm});
            skLineSegment(sketch, "E24.0.10.2", {"start": v(133.1, -58.42) * mm, "end": v(133.1, -53.34) * mm});
            skLineSegment(sketch, "E24.0.10.3", {"start": v(106.68, -58.42) * mm, "end": v(111.76, -58.42) * mm});
            skLineSegment(sketch, "E24.0.10.4", {"start": v(117.1, -58.42) * mm, "end": v(117.1, -53.34) * mm});
            skLineSegment(sketch, "E24.0.10.5", {"start": v(117.1, -53.34) * mm, "end": v(112.01, -53.34) * mm});
            skLineSegment(sketch, "E24.0.10.6", {"start": v(149.1, -58.42) * mm, "end": v(149.1, -53.34) * mm});
            skLineSegment(sketch, "E24.0.10.7", {"start": v(138.68, -58.42) * mm, "end": v(143.76, -58.42) * mm});
            skLineSegment(sketch, "E24.0.10.8", {"start": v(112.01, -53.34) * mm, "end": v(112.01, -58.42) * mm});
            skLineSegment(sketch, "E24.0.10.9", {"start": v(138.68, -53.34) * mm, "end": v(138.68, -58.42) * mm});
            skLineSegment(sketch, "E24.0.10.10", {"start": v(112.01, -58.42) * mm, "end": v(117.1, -58.42) * mm});
            skLineSegment(sketch, "E24.0.10.11", {"start": v(143.76, -53.34) * mm, "end": v(138.68, -53.34) * mm});
            skLineSegment(sketch, "E24.0.10.12", {"start": v(122.43, -58.42) * mm, "end": v(122.43, -53.34) * mm});
            skLineSegment(sketch, "E24.0.10.13", {"start": v(143.76, -58.42) * mm, "end": v(143.76, -53.34) * mm});
            skLineSegment(sketch, "E24.0.10.14", {"start": v(122.68, -58.42) * mm, "end": v(127.76, -58.42) * mm});
            skLineSegment(sketch, "E24.0.10.15", {"start": v(122.43, -53.34) * mm, "end": v(117.35, -53.34) * mm});
            skLineSegment(sketch, "E24.0.10.16", {"start": v(133.35, -58.42) * mm, "end": v(138.43, -58.42) * mm});
            skLineSegment(sketch, "E24.0.10.17", {"start": v(127.76, -53.34) * mm, "end": v(122.68, -53.34) * mm});
            skLineSegment(sketch, "E24.0.10.18", {"start": v(117.35, -53.34) * mm, "end": v(117.35, -58.42) * mm});
            skLineSegment(sketch, "E24.0.10.19", {"start": v(133.35, -53.34) * mm, "end": v(133.35, -58.42) * mm});
            skLineSegment(sketch, "E24.0.10.20", {"start": v(122.68, -53.34) * mm, "end": v(122.68, -58.42) * mm});
            skLineSegment(sketch, "E24.0.10.21", {"start": v(117.35, -58.42) * mm, "end": v(122.43, -58.42) * mm});
            skLineSegment(sketch, "E24.0.10.22", {"start": v(138.43, -53.34) * mm, "end": v(133.35, -53.34) * mm});
            skLineSegment(sketch, "E24.0.10.23", {"start": v(127.76, -58.42) * mm, "end": v(127.76, -53.34) * mm});
            skLineSegment(sketch, "E24.0.10.24", {"start": v(138.43, -58.42) * mm, "end": v(138.43, -53.34) * mm});
            skLineSegment(sketch, "E24.0.10.25", {"start": v(144.02, -53.34) * mm, "end": v(144.02, -58.42) * mm});
            skLineSegment(sketch, "E24.0.10.26", {"start": v(128.02, -58.42) * mm, "end": v(133.1, -58.42) * mm});
            skLineSegment(sketch, "E24.0.10.27", {"start": v(111.76, -58.42) * mm, "end": v(111.76, -53.34) * mm});
            skLineSegment(sketch, "E24.0.10.28", {"start": v(149.1, -53.34) * mm, "end": v(144.02, -53.34) * mm});
            skLineSegment(sketch, "E24.0.10.29", {"start": v(128.02, -53.34) * mm, "end": v(128.02, -58.42) * mm});
            skLineSegment(sketch, "E24.0.10.30", {"start": v(144.02, -58.42) * mm, "end": v(149.1, -58.42) * mm});
            skLineSegment(sketch, "E24.0.10.31", {"start": v(111.76, -53.34) * mm, "end": v(106.68, -53.34) * mm});
            skLineSegment(sketch, "E24.0.11.0", {"start": v(133.1, -58.67) * mm, "end": v(128.02, -58.67) * mm});
            skLineSegment(sketch, "E24.0.11.1", {"start": v(106.68, -58.67) * mm, "end": v(106.68, -63.75) * mm});
            skLineSegment(sketch, "E24.0.11.2", {"start": v(133.1, -63.75) * mm, "end": v(133.1, -58.67) * mm});
            skLineSegment(sketch, "E24.0.11.3", {"start": v(106.68, -63.75) * mm, "end": v(111.76, -63.75) * mm});
            skLineSegment(sketch, "E24.0.11.4", {"start": v(117.1, -63.75) * mm, "end": v(117.1, -58.67) * mm});
            skLineSegment(sketch, "E24.0.11.5", {"start": v(117.1, -58.67) * mm, "end": v(112.01, -58.67) * mm});
            skLineSegment(sketch, "E24.0.11.6", {"start": v(149.1, -63.75) * mm, "end": v(149.1, -58.67) * mm});
            skLineSegment(sketch, "E24.0.11.7", {"start": v(138.68, -63.75) * mm, "end": v(143.76, -63.75) * mm});
            skLineSegment(sketch, "E24.0.11.8", {"start": v(112.01, -58.67) * mm, "end": v(112.01, -63.75) * mm});
            skLineSegment(sketch, "E24.0.11.9", {"start": v(138.68, -58.67) * mm, "end": v(138.68, -63.75) * mm});
            skLineSegment(sketch, "E24.0.11.10", {"start": v(112.01, -63.75) * mm, "end": v(117.1, -63.75) * mm});
            skLineSegment(sketch, "E24.0.11.11", {"start": v(143.76, -58.67) * mm, "end": v(138.68, -58.67) * mm});
            skLineSegment(sketch, "E24.0.11.12", {"start": v(122.43, -63.75) * mm, "end": v(122.43, -58.67) * mm});
            skLineSegment(sketch, "E24.0.11.13", {"start": v(143.76, -63.75) * mm, "end": v(143.76, -58.67) * mm});
            skLineSegment(sketch, "E24.0.11.14", {"start": v(122.68, -63.75) * mm, "end": v(127.76, -63.75) * mm});
            skLineSegment(sketch, "E24.0.11.15", {"start": v(122.43, -58.67) * mm, "end": v(117.35, -58.67) * mm});
            skLineSegment(sketch, "E24.0.11.16", {"start": v(133.35, -63.75) * mm, "end": v(138.43, -63.75) * mm});
            skLineSegment(sketch, "E24.0.11.17", {"start": v(127.76, -58.67) * mm, "end": v(122.68, -58.67) * mm});
            skLineSegment(sketch, "E24.0.11.18", {"start": v(117.35, -58.67) * mm, "end": v(117.35, -63.75) * mm});
            skLineSegment(sketch, "E24.0.11.19", {"start": v(133.35, -58.67) * mm, "end": v(133.35, -63.75) * mm});
            skLineSegment(sketch, "E24.0.11.20", {"start": v(122.68, -58.67) * mm, "end": v(122.68, -63.75) * mm});
            skLineSegment(sketch, "E24.0.11.21", {"start": v(117.35, -63.75) * mm, "end": v(122.43, -63.75) * mm});
            skLineSegment(sketch, "E24.0.11.22", {"start": v(138.43, -58.67) * mm, "end": v(133.35, -58.67) * mm});
            skLineSegment(sketch, "E24.0.11.23", {"start": v(127.76, -63.75) * mm, "end": v(127.76, -58.67) * mm});
            skLineSegment(sketch, "E24.0.11.24", {"start": v(138.43, -63.75) * mm, "end": v(138.43, -58.67) * mm});
            skLineSegment(sketch, "E24.0.11.25", {"start": v(144.02, -58.67) * mm, "end": v(144.02, -63.75) * mm});
            skLineSegment(sketch, "E24.0.11.26", {"start": v(128.02, -63.75) * mm, "end": v(133.1, -63.75) * mm});
            skLineSegment(sketch, "E24.0.11.27", {"start": v(111.76, -63.75) * mm, "end": v(111.76, -58.67) * mm});
            skLineSegment(sketch, "E24.0.11.28", {"start": v(149.1, -58.67) * mm, "end": v(144.02, -58.67) * mm});
            skLineSegment(sketch, "E24.0.11.29", {"start": v(128.02, -58.67) * mm, "end": v(128.02, -63.75) * mm});
            skLineSegment(sketch, "E24.0.11.30", {"start": v(144.02, -63.75) * mm, "end": v(149.1, -63.75) * mm});
            skLineSegment(sketch, "E24.0.11.31", {"start": v(111.76, -58.67) * mm, "end": v(106.68, -58.67) * mm});
            skLineSegment(sketch, "E24.0.12.0", {"start": v(133.1, -64) * mm, "end": v(128.02, -64) * mm});
            skLineSegment(sketch, "E24.0.12.1", {"start": v(106.68, -64) * mm, "end": v(106.68, -69.09) * mm});
            skLineSegment(sketch, "E24.0.12.2", {"start": v(133.1, -69.09) * mm, "end": v(133.1, -64) * mm});
            skLineSegment(sketch, "E24.0.12.3", {"start": v(106.68, -69.09) * mm, "end": v(111.76, -69.09) * mm});
            skLineSegment(sketch, "E24.0.12.4", {"start": v(117.1, -69.09) * mm, "end": v(117.1, -64) * mm});
            skLineSegment(sketch, "E24.0.12.5", {"start": v(117.1, -64) * mm, "end": v(112.01, -64) * mm});
            skLineSegment(sketch, "E24.0.12.6", {"start": v(149.1, -69.09) * mm, "end": v(149.1, -64) * mm});
            skLineSegment(sketch, "E24.0.12.7", {"start": v(138.68, -69.09) * mm, "end": v(143.76, -69.09) * mm});
            skLineSegment(sketch, "E24.0.12.8", {"start": v(112.01, -64) * mm, "end": v(112.01, -69.09) * mm});
            skLineSegment(sketch, "E24.0.12.9", {"start": v(138.68, -64) * mm, "end": v(138.68, -69.09) * mm});
            skLineSegment(sketch, "E24.0.12.10", {"start": v(112.01, -69.09) * mm, "end": v(117.1, -69.09) * mm});
            skLineSegment(sketch, "E24.0.12.11", {"start": v(143.76, -64) * mm, "end": v(138.68, -64) * mm});
            skLineSegment(sketch, "E24.0.12.12", {"start": v(122.43, -69.09) * mm, "end": v(122.43, -64) * mm});
            skLineSegment(sketch, "E24.0.12.13", {"start": v(143.76, -69.09) * mm, "end": v(143.76, -64) * mm});
            skLineSegment(sketch, "E24.0.12.14", {"start": v(122.68, -69.09) * mm, "end": v(127.76, -69.09) * mm});
            skLineSegment(sketch, "E24.0.12.15", {"start": v(122.43, -64) * mm, "end": v(117.35, -64) * mm});
            skLineSegment(sketch, "E24.0.12.16", {"start": v(133.35, -69.09) * mm, "end": v(138.43, -69.09) * mm});
            skLineSegment(sketch, "E24.0.12.17", {"start": v(127.76, -64) * mm, "end": v(122.68, -64) * mm});
            skLineSegment(sketch, "E24.0.12.18", {"start": v(117.35, -64) * mm, "end": v(117.35, -69.09) * mm});
            skLineSegment(sketch, "E24.0.12.19", {"start": v(133.35, -64) * mm, "end": v(133.35, -69.09) * mm});
            skLineSegment(sketch, "E24.0.12.20", {"start": v(122.68, -64) * mm, "end": v(122.68, -69.09) * mm});
            skLineSegment(sketch, "E24.0.12.21", {"start": v(117.35, -69.09) * mm, "end": v(122.43, -69.09) * mm});
            skLineSegment(sketch, "E24.0.12.22", {"start": v(138.43, -64) * mm, "end": v(133.35, -64) * mm});
            skLineSegment(sketch, "E24.0.12.23", {"start": v(127.76, -69.09) * mm, "end": v(127.76, -64) * mm});
            skLineSegment(sketch, "E24.0.12.24", {"start": v(138.43, -69.09) * mm, "end": v(138.43, -64) * mm});
            skLineSegment(sketch, "E24.0.12.25", {"start": v(144.02, -64) * mm, "end": v(144.02, -69.09) * mm});
            skLineSegment(sketch, "E24.0.12.26", {"start": v(128.02, -69.09) * mm, "end": v(133.1, -69.09) * mm});
            skLineSegment(sketch, "E24.0.12.27", {"start": v(111.76, -69.09) * mm, "end": v(111.76, -64) * mm});
            skLineSegment(sketch, "E24.0.12.28", {"start": v(149.1, -64) * mm, "end": v(144.02, -64) * mm});
            skLineSegment(sketch, "E24.0.12.29", {"start": v(128.02, -64) * mm, "end": v(128.02, -69.09) * mm});
            skLineSegment(sketch, "E24.0.12.30", {"start": v(144.02, -69.09) * mm, "end": v(149.1, -69.09) * mm});
            skLineSegment(sketch, "E24.0.12.31", {"start": v(111.76, -64) * mm, "end": v(106.68, -64) * mm});
            skLineSegment(sketch, "E24.0.13.0", {"start": v(133.1, -69.34) * mm, "end": v(128.02, -69.34) * mm});
            skLineSegment(sketch, "E24.0.13.1", {"start": v(106.68, -69.34) * mm, "end": v(106.68, -74.42) * mm});
            skLineSegment(sketch, "E24.0.13.2", {"start": v(133.1, -74.42) * mm, "end": v(133.1, -69.34) * mm});
            skLineSegment(sketch, "E24.0.13.3", {"start": v(106.68, -74.42) * mm, "end": v(111.76, -74.42) * mm});
            skLineSegment(sketch, "E24.0.13.4", {"start": v(117.1, -74.42) * mm, "end": v(117.1, -69.34) * mm});
            skLineSegment(sketch, "E24.0.13.5", {"start": v(117.1, -69.34) * mm, "end": v(112.01, -69.34) * mm});
            skLineSegment(sketch, "E24.0.13.6", {"start": v(149.1, -74.42) * mm, "end": v(149.1, -69.34) * mm});
            skLineSegment(sketch, "E24.0.13.7", {"start": v(138.68, -74.42) * mm, "end": v(143.76, -74.42) * mm});
            skLineSegment(sketch, "E24.0.13.8", {"start": v(112.01, -69.34) * mm, "end": v(112.01, -74.42) * mm});
            skLineSegment(sketch, "E24.0.13.9", {"start": v(138.68, -69.34) * mm, "end": v(138.68, -74.42) * mm});
            skLineSegment(sketch, "E24.0.13.10", {"start": v(112.01, -74.42) * mm, "end": v(117.1, -74.42) * mm});
            skLineSegment(sketch, "E24.0.13.11", {"start": v(143.76, -69.34) * mm, "end": v(138.68, -69.34) * mm});
            skLineSegment(sketch, "E24.0.13.12", {"start": v(122.43, -74.42) * mm, "end": v(122.43, -69.34) * mm});
            skLineSegment(sketch, "E24.0.13.13", {"start": v(143.76, -74.42) * mm, "end": v(143.76, -69.34) * mm});
            skLineSegment(sketch, "E24.0.13.14", {"start": v(122.68, -74.42) * mm, "end": v(127.76, -74.42) * mm});
            skLineSegment(sketch, "E24.0.13.15", {"start": v(122.43, -69.34) * mm, "end": v(117.35, -69.34) * mm});
            skLineSegment(sketch, "E24.0.13.16", {"start": v(133.35, -74.42) * mm, "end": v(138.43, -74.42) * mm});
            skLineSegment(sketch, "E24.0.13.17", {"start": v(127.76, -69.34) * mm, "end": v(122.68, -69.34) * mm});
            skLineSegment(sketch, "E24.0.13.18", {"start": v(117.35, -69.34) * mm, "end": v(117.35, -74.42) * mm});
            skLineSegment(sketch, "E24.0.13.19", {"start": v(133.35, -69.34) * mm, "end": v(133.35, -74.42) * mm});
            skLineSegment(sketch, "E24.0.13.20", {"start": v(122.68, -69.34) * mm, "end": v(122.68, -74.42) * mm});
            skLineSegment(sketch, "E24.0.13.21", {"start": v(117.35, -74.42) * mm, "end": v(122.43, -74.42) * mm});
            skLineSegment(sketch, "E24.0.13.22", {"start": v(138.43, -69.34) * mm, "end": v(133.35, -69.34) * mm});
            skLineSegment(sketch, "E24.0.13.23", {"start": v(127.76, -74.42) * mm, "end": v(127.76, -69.34) * mm});
            skLineSegment(sketch, "E24.0.13.24", {"start": v(138.43, -74.42) * mm, "end": v(138.43, -69.34) * mm});
            skLineSegment(sketch, "E24.0.13.25", {"start": v(144.02, -69.34) * mm, "end": v(144.02, -74.42) * mm});
            skLineSegment(sketch, "E24.0.13.26", {"start": v(128.02, -74.42) * mm, "end": v(133.1, -74.42) * mm});
            skLineSegment(sketch, "E24.0.13.27", {"start": v(111.76, -74.42) * mm, "end": v(111.76, -69.34) * mm});
            skLineSegment(sketch, "E24.0.13.28", {"start": v(149.1, -69.34) * mm, "end": v(144.02, -69.34) * mm});
            skLineSegment(sketch, "E24.0.13.29", {"start": v(128.02, -69.34) * mm, "end": v(128.02, -74.42) * mm});
            skLineSegment(sketch, "E24.0.13.30", {"start": v(144.02, -74.42) * mm, "end": v(149.1, -74.42) * mm});
            skLineSegment(sketch, "E24.0.13.31", {"start": v(111.76, -69.34) * mm, "end": v(106.68, -69.34) * mm});
            skLineSegment(sketch, "E24.0.14.0", {"start": v(133.1, -74.68) * mm, "end": v(128.02, -74.68) * mm});
            skLineSegment(sketch, "E24.0.14.1", {"start": v(106.68, -74.68) * mm, "end": v(106.68, -79.76) * mm});
            skLineSegment(sketch, "E24.0.14.2", {"start": v(133.1, -79.76) * mm, "end": v(133.1, -74.68) * mm});
            skLineSegment(sketch, "E24.0.14.3", {"start": v(106.68, -79.76) * mm, "end": v(111.76, -79.76) * mm});
            skLineSegment(sketch, "E24.0.14.4", {"start": v(117.1, -79.76) * mm, "end": v(117.1, -74.68) * mm});
            skLineSegment(sketch, "E24.0.14.5", {"start": v(117.1, -74.68) * mm, "end": v(112.01, -74.68) * mm});
            skLineSegment(sketch, "E24.0.14.6", {"start": v(149.1, -79.76) * mm, "end": v(149.1, -74.68) * mm});
            skLineSegment(sketch, "E24.0.14.7", {"start": v(138.68, -79.76) * mm, "end": v(143.76, -79.76) * mm});
            skLineSegment(sketch, "E24.0.14.8", {"start": v(112.01, -74.68) * mm, "end": v(112.01, -79.76) * mm});
            skLineSegment(sketch, "E24.0.14.9", {"start": v(138.68, -74.68) * mm, "end": v(138.68, -79.76) * mm});
            skLineSegment(sketch, "E24.0.14.10", {"start": v(112.01, -79.76) * mm, "end": v(117.1, -79.76) * mm});
            skLineSegment(sketch, "E24.0.14.11", {"start": v(143.76, -74.68) * mm, "end": v(138.68, -74.68) * mm});
            skLineSegment(sketch, "E24.0.14.12", {"start": v(122.43, -79.76) * mm, "end": v(122.43, -74.68) * mm});
            skLineSegment(sketch, "E24.0.14.13", {"start": v(143.76, -79.76) * mm, "end": v(143.76, -74.68) * mm});
            skLineSegment(sketch, "E24.0.14.14", {"start": v(122.68, -79.76) * mm, "end": v(127.76, -79.76) * mm});
            skLineSegment(sketch, "E24.0.14.15", {"start": v(122.43, -74.68) * mm, "end": v(117.35, -74.68) * mm});
            skLineSegment(sketch, "E24.0.14.16", {"start": v(133.35, -79.76) * mm, "end": v(138.43, -79.76) * mm});
            skLineSegment(sketch, "E24.0.14.17", {"start": v(127.76, -74.68) * mm, "end": v(122.68, -74.68) * mm});
            skLineSegment(sketch, "E24.0.14.18", {"start": v(117.35, -74.68) * mm, "end": v(117.35, -79.76) * mm});
            skLineSegment(sketch, "E24.0.14.19", {"start": v(133.35, -74.68) * mm, "end": v(133.35, -79.76) * mm});
            skLineSegment(sketch, "E24.0.14.20", {"start": v(122.68, -74.68) * mm, "end": v(122.68, -79.76) * mm});
            skLineSegment(sketch, "E24.0.14.21", {"start": v(117.35, -79.76) * mm, "end": v(122.43, -79.76) * mm});
            skLineSegment(sketch, "E24.0.14.22", {"start": v(138.43, -74.68) * mm, "end": v(133.35, -74.68) * mm});
            skLineSegment(sketch, "E24.0.14.23", {"start": v(127.76, -79.76) * mm, "end": v(127.76, -74.68) * mm});
            skLineSegment(sketch, "E24.0.14.24", {"start": v(138.43, -79.76) * mm, "end": v(138.43, -74.68) * mm});
            skLineSegment(sketch, "E24.0.14.25", {"start": v(144.02, -74.68) * mm, "end": v(144.02, -79.76) * mm});
            skLineSegment(sketch, "E24.0.14.26", {"start": v(128.02, -79.76) * mm, "end": v(133.1, -79.76) * mm});
            skLineSegment(sketch, "E24.0.14.27", {"start": v(111.76, -79.76) * mm, "end": v(111.76, -74.68) * mm});
            skLineSegment(sketch, "E24.0.14.28", {"start": v(149.1, -74.68) * mm, "end": v(144.02, -74.68) * mm});
            skLineSegment(sketch, "E24.0.14.29", {"start": v(128.02, -74.68) * mm, "end": v(128.02, -79.76) * mm});
            skLineSegment(sketch, "E24.0.14.30", {"start": v(144.02, -79.76) * mm, "end": v(149.1, -79.76) * mm});
            skLineSegment(sketch, "E24.0.14.31", {"start": v(111.76, -74.68) * mm, "end": v(106.68, -74.68) * mm});
            skLineSegment(sketch, "E24.0.15.0", {"start": v(133.1, -80.01) * mm, "end": v(128.02, -80.01) * mm});
            skLineSegment(sketch, "E24.0.15.1", {"start": v(106.68, -80.01) * mm, "end": v(106.68, -85.1) * mm});
            skLineSegment(sketch, "E24.0.15.2", {"start": v(133.1, -85.1) * mm, "end": v(133.1, -80.01) * mm});
            skLineSegment(sketch, "E24.0.15.3", {"start": v(106.68, -85.1) * mm, "end": v(111.76, -85.1) * mm});
            skLineSegment(sketch, "E24.0.15.4", {"start": v(117.1, -85.1) * mm, "end": v(117.1, -80.01) * mm});
            skLineSegment(sketch, "E24.0.15.5", {"start": v(117.1, -80.01) * mm, "end": v(112.01, -80.01) * mm});
            skLineSegment(sketch, "E24.0.15.6", {"start": v(149.1, -85.1) * mm, "end": v(149.1, -80.01) * mm});
            skLineSegment(sketch, "E24.0.15.7", {"start": v(138.68, -85.1) * mm, "end": v(143.76, -85.1) * mm});
            skLineSegment(sketch, "E24.0.15.8", {"start": v(112.01, -80.01) * mm, "end": v(112.01, -85.1) * mm});
            skLineSegment(sketch, "E24.0.15.9", {"start": v(138.68, -80.01) * mm, "end": v(138.68, -85.1) * mm});
            skLineSegment(sketch, "E24.0.15.10", {"start": v(112.01, -85.1) * mm, "end": v(117.1, -85.1) * mm});
            skLineSegment(sketch, "E24.0.15.11", {"start": v(143.76, -80.01) * mm, "end": v(138.68, -80.01) * mm});
            skLineSegment(sketch, "E24.0.15.12", {"start": v(122.43, -85.1) * mm, "end": v(122.43, -80.01) * mm});
            skLineSegment(sketch, "E24.0.15.13", {"start": v(143.76, -85.1) * mm, "end": v(143.76, -80.01) * mm});
            skLineSegment(sketch, "E24.0.15.14", {"start": v(122.68, -85.1) * mm, "end": v(127.76, -85.1) * mm});
            skLineSegment(sketch, "E24.0.15.15", {"start": v(122.43, -80.01) * mm, "end": v(117.35, -80.01) * mm});
            skLineSegment(sketch, "E24.0.15.16", {"start": v(133.35, -85.1) * mm, "end": v(138.43, -85.1) * mm});
            skLineSegment(sketch, "E24.0.15.17", {"start": v(127.76, -80.01) * mm, "end": v(122.68, -80.01) * mm});
            skLineSegment(sketch, "E24.0.15.18", {"start": v(117.35, -80.01) * mm, "end": v(117.35, -85.1) * mm});
            skLineSegment(sketch, "E24.0.15.19", {"start": v(133.35, -80.01) * mm, "end": v(133.35, -85.1) * mm});
            skLineSegment(sketch, "E24.0.15.20", {"start": v(122.68, -80.01) * mm, "end": v(122.68, -85.1) * mm});
            skLineSegment(sketch, "E24.0.15.21", {"start": v(117.35, -85.1) * mm, "end": v(122.43, -85.1) * mm});
            skLineSegment(sketch, "E24.0.15.22", {"start": v(138.43, -80.01) * mm, "end": v(133.35, -80.01) * mm});
            skLineSegment(sketch, "E24.0.15.23", {"start": v(127.76, -85.1) * mm, "end": v(127.76, -80.01) * mm});
            skLineSegment(sketch, "E24.0.15.24", {"start": v(138.43, -85.1) * mm, "end": v(138.43, -80.01) * mm});
            skLineSegment(sketch, "E24.0.15.25", {"start": v(144.02, -80.01) * mm, "end": v(144.02, -85.1) * mm});
            skLineSegment(sketch, "E24.0.15.26", {"start": v(128.02, -85.1) * mm, "end": v(133.1, -85.1) * mm});
            skLineSegment(sketch, "E24.0.15.27", {"start": v(111.76, -85.1) * mm, "end": v(111.76, -80.01) * mm});
            skLineSegment(sketch, "E24.0.15.28", {"start": v(149.1, -80.01) * mm, "end": v(144.02, -80.01) * mm});
            skLineSegment(sketch, "E24.0.15.29", {"start": v(128.02, -80.01) * mm, "end": v(128.02, -85.1) * mm});
            skLineSegment(sketch, "E24.0.15.30", {"start": v(144.02, -85.1) * mm, "end": v(149.1, -85.1) * mm});
            skLineSegment(sketch, "E24.0.15.31", {"start": v(111.76, -80.01) * mm, "end": v(106.68, -80.01) * mm});
            skLineSegment(sketch, "E24.0.16.0", {"start": v(133.1, -85.34) * mm, "end": v(128.02, -85.34) * mm});
            skLineSegment(sketch, "E24.0.16.1", {"start": v(106.68, -85.34) * mm, "end": v(106.68, -90.42) * mm});
            skLineSegment(sketch, "E24.0.16.2", {"start": v(133.1, -90.42) * mm, "end": v(133.1, -85.34) * mm});
            skLineSegment(sketch, "E24.0.16.3", {"start": v(106.68, -90.42) * mm, "end": v(111.76, -90.42) * mm});
            skLineSegment(sketch, "E24.0.16.4", {"start": v(117.1, -90.42) * mm, "end": v(117.1, -85.34) * mm});
            skLineSegment(sketch, "E24.0.16.5", {"start": v(117.1, -85.34) * mm, "end": v(112.01, -85.34) * mm});
            skLineSegment(sketch, "E24.0.16.6", {"start": v(149.1, -90.42) * mm, "end": v(149.1, -85.34) * mm});
            skLineSegment(sketch, "E24.0.16.7", {"start": v(138.68, -90.42) * mm, "end": v(143.76, -90.42) * mm});
            skLineSegment(sketch, "E24.0.16.8", {"start": v(112.01, -85.34) * mm, "end": v(112.01, -90.42) * mm});
            skLineSegment(sketch, "E24.0.16.9", {"start": v(138.68, -85.34) * mm, "end": v(138.68, -90.42) * mm});
            skLineSegment(sketch, "E24.0.16.10", {"start": v(112.01, -90.42) * mm, "end": v(117.1, -90.42) * mm});
            skLineSegment(sketch, "E24.0.16.11", {"start": v(143.76, -85.34) * mm, "end": v(138.68, -85.34) * mm});
            skLineSegment(sketch, "E24.0.16.12", {"start": v(122.43, -90.42) * mm, "end": v(122.43, -85.34) * mm});
            skLineSegment(sketch, "E24.0.16.13", {"start": v(143.76, -90.42) * mm, "end": v(143.76, -85.34) * mm});
            skLineSegment(sketch, "E24.0.16.14", {"start": v(122.68, -90.42) * mm, "end": v(127.76, -90.42) * mm});
            skLineSegment(sketch, "E24.0.16.15", {"start": v(122.43, -85.34) * mm, "end": v(117.35, -85.34) * mm});
            skLineSegment(sketch, "E24.0.16.16", {"start": v(133.35, -90.42) * mm, "end": v(138.43, -90.42) * mm});
            skLineSegment(sketch, "E24.0.16.17", {"start": v(127.76, -85.34) * mm, "end": v(122.68, -85.34) * mm});
            skLineSegment(sketch, "E24.0.16.18", {"start": v(117.35, -85.34) * mm, "end": v(117.35, -90.42) * mm});
            skLineSegment(sketch, "E24.0.16.19", {"start": v(133.35, -85.34) * mm, "end": v(133.35, -90.42) * mm});
            skLineSegment(sketch, "E24.0.16.20", {"start": v(122.68, -85.34) * mm, "end": v(122.68, -90.42) * mm});
            skLineSegment(sketch, "E24.0.16.21", {"start": v(117.35, -90.42) * mm, "end": v(122.43, -90.42) * mm});
            skLineSegment(sketch, "E24.0.16.22", {"start": v(138.43, -85.34) * mm, "end": v(133.35, -85.34) * mm});
            skLineSegment(sketch, "E24.0.16.23", {"start": v(127.76, -90.42) * mm, "end": v(127.76, -85.34) * mm});
            skLineSegment(sketch, "E24.0.16.24", {"start": v(138.43, -90.42) * mm, "end": v(138.43, -85.34) * mm});
            skLineSegment(sketch, "E24.0.16.25", {"start": v(144.02, -85.34) * mm, "end": v(144.02, -90.42) * mm});
            skLineSegment(sketch, "E24.0.16.26", {"start": v(128.02, -90.42) * mm, "end": v(133.1, -90.42) * mm});
            skLineSegment(sketch, "E24.0.16.27", {"start": v(111.76, -90.42) * mm, "end": v(111.76, -85.34) * mm});
            skLineSegment(sketch, "E24.0.16.28", {"start": v(149.1, -85.34) * mm, "end": v(144.02, -85.34) * mm});
            skLineSegment(sketch, "E24.0.16.29", {"start": v(128.02, -85.34) * mm, "end": v(128.02, -90.42) * mm});
            skLineSegment(sketch, "E24.0.16.30", {"start": v(144.02, -90.42) * mm, "end": v(149.1, -90.42) * mm});
            skLineSegment(sketch, "E24.0.16.31", {"start": v(111.76, -85.34) * mm, "end": v(106.68, -85.34) * mm});
            skLineSegment(sketch, "E24.0.17.0", {"start": v(133.1, -90.68) * mm, "end": v(128.02, -90.68) * mm});
            skLineSegment(sketch, "E24.0.17.1", {"start": v(106.68, -90.68) * mm, "end": v(106.68, -95.76) * mm});
            skLineSegment(sketch, "E24.0.17.2", {"start": v(133.1, -95.76) * mm, "end": v(133.1, -90.68) * mm});
            skLineSegment(sketch, "E24.0.17.3", {"start": v(106.68, -95.76) * mm, "end": v(111.76, -95.76) * mm});
            skLineSegment(sketch, "E24.0.17.4", {"start": v(117.1, -95.76) * mm, "end": v(117.1, -90.68) * mm});
            skLineSegment(sketch, "E24.0.17.5", {"start": v(117.1, -90.68) * mm, "end": v(112.01, -90.68) * mm});
            skLineSegment(sketch, "E24.0.17.6", {"start": v(149.1, -95.76) * mm, "end": v(149.1, -90.68) * mm});
            skLineSegment(sketch, "E24.0.17.7", {"start": v(138.68, -95.76) * mm, "end": v(143.76, -95.76) * mm});
            skLineSegment(sketch, "E24.0.17.8", {"start": v(112.01, -90.68) * mm, "end": v(112.01, -95.76) * mm});
            skLineSegment(sketch, "E24.0.17.9", {"start": v(138.68, -90.68) * mm, "end": v(138.68, -95.76) * mm});
            skLineSegment(sketch, "E24.0.17.10", {"start": v(112.01, -95.76) * mm, "end": v(117.1, -95.76) * mm});
            skLineSegment(sketch, "E24.0.17.11", {"start": v(143.76, -90.68) * mm, "end": v(138.68, -90.68) * mm});
            skLineSegment(sketch, "E24.0.17.12", {"start": v(122.43, -95.76) * mm, "end": v(122.43, -90.68) * mm});
            skLineSegment(sketch, "E24.0.17.13", {"start": v(143.76, -95.76) * mm, "end": v(143.76, -90.68) * mm});
            skLineSegment(sketch, "E24.0.17.14", {"start": v(122.68, -95.76) * mm, "end": v(127.76, -95.76) * mm});
            skLineSegment(sketch, "E24.0.17.15", {"start": v(122.43, -90.68) * mm, "end": v(117.35, -90.68) * mm});
            skLineSegment(sketch, "E24.0.17.16", {"start": v(133.35, -95.76) * mm, "end": v(138.43, -95.76) * mm});
            skLineSegment(sketch, "E24.0.17.17", {"start": v(127.76, -90.68) * mm, "end": v(122.68, -90.68) * mm});
            skLineSegment(sketch, "E24.0.17.18", {"start": v(117.35, -90.68) * mm, "end": v(117.35, -95.76) * mm});
            skLineSegment(sketch, "E24.0.17.19", {"start": v(133.35, -90.68) * mm, "end": v(133.35, -95.76) * mm});
            skLineSegment(sketch, "E24.0.17.20", {"start": v(122.68, -90.68) * mm, "end": v(122.68, -95.76) * mm});
            skLineSegment(sketch, "E24.0.17.21", {"start": v(117.35, -95.76) * mm, "end": v(122.43, -95.76) * mm});
            skLineSegment(sketch, "E24.0.17.22", {"start": v(138.43, -90.68) * mm, "end": v(133.35, -90.68) * mm});
            skLineSegment(sketch, "E24.0.17.23", {"start": v(127.76, -95.76) * mm, "end": v(127.76, -90.68) * mm});
            skLineSegment(sketch, "E24.0.17.24", {"start": v(138.43, -95.76) * mm, "end": v(138.43, -90.68) * mm});
            skLineSegment(sketch, "E24.0.17.25", {"start": v(144.02, -90.68) * mm, "end": v(144.02, -95.76) * mm});
            skLineSegment(sketch, "E24.0.17.26", {"start": v(128.02, -95.76) * mm, "end": v(133.1, -95.76) * mm});
            skLineSegment(sketch, "E24.0.17.27", {"start": v(111.76, -95.76) * mm, "end": v(111.76, -90.68) * mm});
            skLineSegment(sketch, "E24.0.17.28", {"start": v(149.1, -90.68) * mm, "end": v(144.02, -90.68) * mm});
            skLineSegment(sketch, "E24.0.17.29", {"start": v(128.02, -90.68) * mm, "end": v(128.02, -95.76) * mm});
            skLineSegment(sketch, "E24.0.17.30", {"start": v(144.02, -95.76) * mm, "end": v(149.1, -95.76) * mm});
            skLineSegment(sketch, "E24.0.17.31", {"start": v(111.76, -90.68) * mm, "end": v(106.68, -90.68) * mm});
            skLineSegment(sketch, "E24.0.18.0", {"start": v(133.1, -96.01) * mm, "end": v(128.02, -96.01) * mm});
            skLineSegment(sketch, "E24.0.18.1", {"start": v(106.68, -96.01) * mm, "end": v(106.68, -101.1) * mm});
            skLineSegment(sketch, "E24.0.18.2", {"start": v(133.1, -101.1) * mm, "end": v(133.1, -96.01) * mm});
            skLineSegment(sketch, "E24.0.18.3", {"start": v(106.68, -101.1) * mm, "end": v(111.76, -101.1) * mm});
            skLineSegment(sketch, "E24.0.18.4", {"start": v(117.1, -101.1) * mm, "end": v(117.1, -96.01) * mm});
            skLineSegment(sketch, "E24.0.18.5", {"start": v(117.1, -96.01) * mm, "end": v(112.01, -96.01) * mm});
            skLineSegment(sketch, "E24.0.18.6", {"start": v(149.1, -101.1) * mm, "end": v(149.1, -96.01) * mm});
            skLineSegment(sketch, "E24.0.18.7", {"start": v(138.68, -101.1) * mm, "end": v(143.76, -101.1) * mm});
            skLineSegment(sketch, "E24.0.18.8", {"start": v(112.01, -96.01) * mm, "end": v(112.01, -101.1) * mm});
            skLineSegment(sketch, "E24.0.18.9", {"start": v(138.68, -96.01) * mm, "end": v(138.68, -101.1) * mm});
            skLineSegment(sketch, "E24.0.18.10", {"start": v(112.01, -101.1) * mm, "end": v(117.1, -101.1) * mm});
            skLineSegment(sketch, "E24.0.18.11", {"start": v(143.76, -96.01) * mm, "end": v(138.68, -96.01) * mm});
            skLineSegment(sketch, "E24.0.18.12", {"start": v(122.43, -101.1) * mm, "end": v(122.43, -96.01) * mm});
            skLineSegment(sketch, "E24.0.18.13", {"start": v(143.76, -101.1) * mm, "end": v(143.76, -96.01) * mm});
            skLineSegment(sketch, "E24.0.18.14", {"start": v(122.68, -101.1) * mm, "end": v(127.76, -101.1) * mm});
            skLineSegment(sketch, "E24.0.18.15", {"start": v(122.43, -96.01) * mm, "end": v(117.35, -96.01) * mm});
            skLineSegment(sketch, "E24.0.18.16", {"start": v(133.35, -101.1) * mm, "end": v(138.43, -101.1) * mm});
            skLineSegment(sketch, "E24.0.18.17", {"start": v(127.76, -96.01) * mm, "end": v(122.68, -96.01) * mm});
            skLineSegment(sketch, "E24.0.18.18", {"start": v(117.35, -96.01) * mm, "end": v(117.35, -101.1) * mm});
            skLineSegment(sketch, "E24.0.18.19", {"start": v(133.35, -96.01) * mm, "end": v(133.35, -101.1) * mm});
            skLineSegment(sketch, "E24.0.18.20", {"start": v(122.68, -96.01) * mm, "end": v(122.68, -101.1) * mm});
            skLineSegment(sketch, "E24.0.18.21", {"start": v(117.35, -101.1) * mm, "end": v(122.43, -101.1) * mm});
            skLineSegment(sketch, "E24.0.18.22", {"start": v(138.43, -96.01) * mm, "end": v(133.35, -96.01) * mm});
            skLineSegment(sketch, "E24.0.18.23", {"start": v(127.76, -101.1) * mm, "end": v(127.76, -96.01) * mm});
            skLineSegment(sketch, "E24.0.18.24", {"start": v(138.43, -101.1) * mm, "end": v(138.43, -96.01) * mm});
            skLineSegment(sketch, "E24.0.18.25", {"start": v(144.02, -96.01) * mm, "end": v(144.02, -101.1) * mm});
            skLineSegment(sketch, "E24.0.18.26", {"start": v(128.02, -101.1) * mm, "end": v(133.1, -101.1) * mm});
            skLineSegment(sketch, "E24.0.18.27", {"start": v(111.76, -101.1) * mm, "end": v(111.76, -96.01) * mm});
            skLineSegment(sketch, "E24.0.18.28", {"start": v(149.1, -96.01) * mm, "end": v(144.02, -96.01) * mm});
            skLineSegment(sketch, "E24.0.18.29", {"start": v(128.02, -96.01) * mm, "end": v(128.02, -101.1) * mm});
            skLineSegment(sketch, "E24.0.18.30", {"start": v(144.02, -101.1) * mm, "end": v(149.1, -101.1) * mm});
            skLineSegment(sketch, "E24.0.18.31", {"start": v(111.76, -96.01) * mm, "end": v(106.68, -96.01) * mm});
            skLineSegment(sketch, "E24.0.19.0", {"start": v(133.1, -101.35) * mm, "end": v(128.02, -101.35) * mm});
            skLineSegment(sketch, "E24.0.19.1", {"start": v(106.68, -101.35) * mm, "end": v(106.68, -106.43) * mm});
            skLineSegment(sketch, "E24.0.19.2", {"start": v(133.1, -106.43) * mm, "end": v(133.1, -101.35) * mm});
            skLineSegment(sketch, "E24.0.19.3", {"start": v(106.68, -106.43) * mm, "end": v(111.76, -106.43) * mm});
            skLineSegment(sketch, "E24.0.19.4", {"start": v(117.1, -106.43) * mm, "end": v(117.1, -101.35) * mm});
            skLineSegment(sketch, "E24.0.19.5", {"start": v(117.1, -101.35) * mm, "end": v(112.01, -101.35) * mm});
            skLineSegment(sketch, "E24.0.19.6", {"start": v(149.1, -106.43) * mm, "end": v(149.1, -101.35) * mm});
            skLineSegment(sketch, "E24.0.19.7", {"start": v(138.68, -106.43) * mm, "end": v(143.76, -106.43) * mm});
            skLineSegment(sketch, "E24.0.19.8", {"start": v(112.01, -101.35) * mm, "end": v(112.01, -106.43) * mm});
            skLineSegment(sketch, "E24.0.19.9", {"start": v(138.68, -101.35) * mm, "end": v(138.68, -106.43) * mm});
            skLineSegment(sketch, "E24.0.19.10", {"start": v(112.01, -106.43) * mm, "end": v(117.1, -106.43) * mm});
            skLineSegment(sketch, "E24.0.19.11", {"start": v(143.76, -101.35) * mm, "end": v(138.68, -101.35) * mm});
            skLineSegment(sketch, "E24.0.19.12", {"start": v(122.43, -106.43) * mm, "end": v(122.43, -101.35) * mm});
            skLineSegment(sketch, "E24.0.19.13", {"start": v(143.76, -106.43) * mm, "end": v(143.76, -101.35) * mm});
            skLineSegment(sketch, "E24.0.19.14", {"start": v(122.68, -106.43) * mm, "end": v(127.76, -106.43) * mm});
            skLineSegment(sketch, "E24.0.19.15", {"start": v(122.43, -101.35) * mm, "end": v(117.35, -101.35) * mm});
            skLineSegment(sketch, "E24.0.19.16", {"start": v(133.35, -106.43) * mm, "end": v(138.43, -106.43) * mm});
            skLineSegment(sketch, "E24.0.19.17", {"start": v(127.76, -101.35) * mm, "end": v(122.68, -101.35) * mm});
            skLineSegment(sketch, "E24.0.19.18", {"start": v(117.35, -101.35) * mm, "end": v(117.35, -106.43) * mm});
            skLineSegment(sketch, "E24.0.19.19", {"start": v(133.35, -101.35) * mm, "end": v(133.35, -106.43) * mm});
            skLineSegment(sketch, "E24.0.19.20", {"start": v(122.68, -101.35) * mm, "end": v(122.68, -106.43) * mm});
            skLineSegment(sketch, "E24.0.19.21", {"start": v(117.35, -106.43) * mm, "end": v(122.43, -106.43) * mm});
            skLineSegment(sketch, "E24.0.19.22", {"start": v(138.43, -101.35) * mm, "end": v(133.35, -101.35) * mm});
            skLineSegment(sketch, "E24.0.19.23", {"start": v(127.76, -106.43) * mm, "end": v(127.76, -101.35) * mm});
            skLineSegment(sketch, "E24.0.19.24", {"start": v(138.43, -106.43) * mm, "end": v(138.43, -101.35) * mm});
            skLineSegment(sketch, "E24.0.19.25", {"start": v(144.02, -101.35) * mm, "end": v(144.02, -106.43) * mm});
            skLineSegment(sketch, "E24.0.19.26", {"start": v(128.02, -106.43) * mm, "end": v(133.1, -106.43) * mm});
            skLineSegment(sketch, "E24.0.19.27", {"start": v(111.76, -106.43) * mm, "end": v(111.76, -101.35) * mm});
            skLineSegment(sketch, "E24.0.19.28", {"start": v(149.1, -101.35) * mm, "end": v(144.02, -101.35) * mm});
            skLineSegment(sketch, "E24.0.19.29", {"start": v(128.02, -101.35) * mm, "end": v(128.02, -106.43) * mm});
            skLineSegment(sketch, "E24.0.19.30", {"start": v(144.02, -106.43) * mm, "end": v(149.1, -106.43) * mm});
            skLineSegment(sketch, "E24.0.19.31", {"start": v(111.76, -101.35) * mm, "end": v(106.68, -101.35) * mm});
            skLineSegment(sketch, "E24.0.20.0", {"start": v(133.1, -106.68) * mm, "end": v(128.02, -106.68) * mm});
            skLineSegment(sketch, "E24.0.20.1", {"start": v(106.68, -106.68) * mm, "end": v(106.68, -111.76) * mm});
            skLineSegment(sketch, "E24.0.20.2", {"start": v(133.1, -111.76) * mm, "end": v(133.1, -106.68) * mm});
            skLineSegment(sketch, "E24.0.20.3", {"start": v(106.68, -111.76) * mm, "end": v(111.76, -111.76) * mm});
            skLineSegment(sketch, "E24.0.20.4", {"start": v(117.1, -111.76) * mm, "end": v(117.1, -106.68) * mm});
            skLineSegment(sketch, "E24.0.20.5", {"start": v(117.1, -106.68) * mm, "end": v(112.01, -106.68) * mm});
            skLineSegment(sketch, "E24.0.20.6", {"start": v(149.1, -111.76) * mm, "end": v(149.1, -106.68) * mm});
            skLineSegment(sketch, "E24.0.20.7", {"start": v(138.68, -111.76) * mm, "end": v(143.76, -111.76) * mm});
            skLineSegment(sketch, "E24.0.20.8", {"start": v(112.01, -106.68) * mm, "end": v(112.01, -111.76) * mm});
            skLineSegment(sketch, "E24.0.20.9", {"start": v(138.68, -106.68) * mm, "end": v(138.68, -111.76) * mm});
            skLineSegment(sketch, "E24.0.20.10", {"start": v(112.01, -111.76) * mm, "end": v(117.1, -111.76) * mm});
            skLineSegment(sketch, "E24.0.20.11", {"start": v(143.76, -106.68) * mm, "end": v(138.68, -106.68) * mm});
            skLineSegment(sketch, "E24.0.20.12", {"start": v(122.43, -111.76) * mm, "end": v(122.43, -106.68) * mm});
            skLineSegment(sketch, "E24.0.20.13", {"start": v(143.76, -111.76) * mm, "end": v(143.76, -106.68) * mm});
            skLineSegment(sketch, "E24.0.20.14", {"start": v(122.68, -111.76) * mm, "end": v(127.76, -111.76) * mm});
            skLineSegment(sketch, "E24.0.20.15", {"start": v(122.43, -106.68) * mm, "end": v(117.35, -106.68) * mm});
            skLineSegment(sketch, "E24.0.20.16", {"start": v(133.35, -111.76) * mm, "end": v(138.43, -111.76) * mm});
            skLineSegment(sketch, "E24.0.20.17", {"start": v(127.76, -106.68) * mm, "end": v(122.68, -106.68) * mm});
            skLineSegment(sketch, "E24.0.20.18", {"start": v(117.35, -106.68) * mm, "end": v(117.35, -111.76) * mm});
            skLineSegment(sketch, "E24.0.20.19", {"start": v(133.35, -106.68) * mm, "end": v(133.35, -111.76) * mm});
            skLineSegment(sketch, "E24.0.20.20", {"start": v(122.68, -106.68) * mm, "end": v(122.68, -111.76) * mm});
            skLineSegment(sketch, "E24.0.20.21", {"start": v(117.35, -111.76) * mm, "end": v(122.43, -111.76) * mm});
            skLineSegment(sketch, "E24.0.20.22", {"start": v(138.43, -106.68) * mm, "end": v(133.35, -106.68) * mm});
            skLineSegment(sketch, "E24.0.20.23", {"start": v(127.76, -111.76) * mm, "end": v(127.76, -106.68) * mm});
            skLineSegment(sketch, "E24.0.20.24", {"start": v(138.43, -111.76) * mm, "end": v(138.43, -106.68) * mm});
            skLineSegment(sketch, "E24.0.20.25", {"start": v(144.02, -106.68) * mm, "end": v(144.02, -111.76) * mm});
            skLineSegment(sketch, "E24.0.20.26", {"start": v(128.02, -111.76) * mm, "end": v(133.1, -111.76) * mm});
            skLineSegment(sketch, "E24.0.20.27", {"start": v(111.76, -111.76) * mm, "end": v(111.76, -106.68) * mm});
            skLineSegment(sketch, "E24.0.20.28", {"start": v(149.1, -106.68) * mm, "end": v(144.02, -106.68) * mm});
            skLineSegment(sketch, "E24.0.20.29", {"start": v(128.02, -106.68) * mm, "end": v(128.02, -111.76) * mm});
            skLineSegment(sketch, "E24.0.20.30", {"start": v(144.02, -111.76) * mm, "end": v(149.1, -111.76) * mm});
            skLineSegment(sketch, "E24.0.20.31", {"start": v(111.76, -106.68) * mm, "end": v(106.68, -106.68) * mm});
            skLineSegment(sketch, "E24.0.21.0", {"start": v(133.1, -112.01) * mm, "end": v(128.02, -112.01) * mm});
            skLineSegment(sketch, "E24.0.21.1", {"start": v(106.68, -112.01) * mm, "end": v(106.68, -117.1) * mm});
            skLineSegment(sketch, "E24.0.21.2", {"start": v(133.1, -117.1) * mm, "end": v(133.1, -112.01) * mm});
            skLineSegment(sketch, "E24.0.21.3", {"start": v(106.68, -117.1) * mm, "end": v(111.76, -117.1) * mm});
            skLineSegment(sketch, "E24.0.21.4", {"start": v(117.1, -117.1) * mm, "end": v(117.1, -112.01) * mm});
            skLineSegment(sketch, "E24.0.21.5", {"start": v(117.1, -112.01) * mm, "end": v(112.01, -112.01) * mm});
            skLineSegment(sketch, "E24.0.21.6", {"start": v(149.1, -117.1) * mm, "end": v(149.1, -112.01) * mm});
            skLineSegment(sketch, "E24.0.21.7", {"start": v(138.68, -117.1) * mm, "end": v(143.76, -117.1) * mm});
            skLineSegment(sketch, "E24.0.21.8", {"start": v(112.01, -112.01) * mm, "end": v(112.01, -117.1) * mm});
            skLineSegment(sketch, "E24.0.21.9", {"start": v(138.68, -112.01) * mm, "end": v(138.68, -117.1) * mm});
            skLineSegment(sketch, "E24.0.21.10", {"start": v(112.01, -117.1) * mm, "end": v(117.1, -117.1) * mm});
            skLineSegment(sketch, "E24.0.21.11", {"start": v(143.76, -112.01) * mm, "end": v(138.68, -112.01) * mm});
            skLineSegment(sketch, "E24.0.21.12", {"start": v(122.43, -117.1) * mm, "end": v(122.43, -112.01) * mm});
            skLineSegment(sketch, "E24.0.21.13", {"start": v(143.76, -117.1) * mm, "end": v(143.76, -112.01) * mm});
            skLineSegment(sketch, "E24.0.21.14", {"start": v(122.68, -117.1) * mm, "end": v(127.76, -117.1) * mm});
            skLineSegment(sketch, "E24.0.21.15", {"start": v(122.43, -112.01) * mm, "end": v(117.35, -112.01) * mm});
            skLineSegment(sketch, "E24.0.21.16", {"start": v(133.35, -117.1) * mm, "end": v(138.43, -117.1) * mm});
            skLineSegment(sketch, "E24.0.21.17", {"start": v(127.76, -112.01) * mm, "end": v(122.68, -112.01) * mm});
            skLineSegment(sketch, "E24.0.21.18", {"start": v(117.35, -112.01) * mm, "end": v(117.35, -117.1) * mm});
            skLineSegment(sketch, "E24.0.21.19", {"start": v(133.35, -112.01) * mm, "end": v(133.35, -117.1) * mm});
            skLineSegment(sketch, "E24.0.21.20", {"start": v(122.68, -112.01) * mm, "end": v(122.68, -117.1) * mm});
            skLineSegment(sketch, "E24.0.21.21", {"start": v(117.35, -117.1) * mm, "end": v(122.43, -117.1) * mm});
            skLineSegment(sketch, "E24.0.21.22", {"start": v(138.43, -112.01) * mm, "end": v(133.35, -112.01) * mm});
            skLineSegment(sketch, "E24.0.21.23", {"start": v(127.76, -117.1) * mm, "end": v(127.76, -112.01) * mm});
            skLineSegment(sketch, "E24.0.21.24", {"start": v(138.43, -117.1) * mm, "end": v(138.43, -112.01) * mm});
            skLineSegment(sketch, "E24.0.21.25", {"start": v(144.02, -112.01) * mm, "end": v(144.02, -117.1) * mm});
            skLineSegment(sketch, "E24.0.21.26", {"start": v(128.02, -117.1) * mm, "end": v(133.1, -117.1) * mm});
            skLineSegment(sketch, "E24.0.21.27", {"start": v(111.76, -117.1) * mm, "end": v(111.76, -112.01) * mm});
            skLineSegment(sketch, "E24.0.21.28", {"start": v(149.1, -112.01) * mm, "end": v(144.02, -112.01) * mm});
            skLineSegment(sketch, "E24.0.21.29", {"start": v(128.02, -112.01) * mm, "end": v(128.02, -117.1) * mm});
            skLineSegment(sketch, "E24.0.21.30", {"start": v(144.02, -117.1) * mm, "end": v(149.1, -117.1) * mm});
            skLineSegment(sketch, "E24.0.21.31", {"start": v(111.76, -112.01) * mm, "end": v(106.68, -112.01) * mm});
            skLineSegment(sketch, "E24.0.22.0", {"start": v(133.1, -117.35) * mm, "end": v(128.02, -117.35) * mm});
            skLineSegment(sketch, "E24.0.22.1", {"start": v(106.68, -117.35) * mm, "end": v(106.68, -122.43) * mm});
            skLineSegment(sketch, "E24.0.22.2", {"start": v(133.1, -122.43) * mm, "end": v(133.1, -117.35) * mm});
            skLineSegment(sketch, "E24.0.22.3", {"start": v(106.68, -122.43) * mm, "end": v(111.76, -122.43) * mm});
            skLineSegment(sketch, "E24.0.22.4", {"start": v(117.1, -122.43) * mm, "end": v(117.1, -117.35) * mm});
            skLineSegment(sketch, "E24.0.22.5", {"start": v(117.1, -117.35) * mm, "end": v(112.01, -117.35) * mm});
            skLineSegment(sketch, "E24.0.22.6", {"start": v(149.1, -122.43) * mm, "end": v(149.1, -117.35) * mm});
            skLineSegment(sketch, "E24.0.22.7", {"start": v(138.68, -122.43) * mm, "end": v(143.76, -122.43) * mm});
            skLineSegment(sketch, "E24.0.22.8", {"start": v(112.01, -117.35) * mm, "end": v(112.01, -122.43) * mm});
            skLineSegment(sketch, "E24.0.22.9", {"start": v(138.68, -117.35) * mm, "end": v(138.68, -122.43) * mm});
            skLineSegment(sketch, "E24.0.22.10", {"start": v(112.01, -122.43) * mm, "end": v(117.1, -122.43) * mm});
            skLineSegment(sketch, "E24.0.22.11", {"start": v(143.76, -117.35) * mm, "end": v(138.68, -117.35) * mm});
            skLineSegment(sketch, "E24.0.22.12", {"start": v(122.43, -122.43) * mm, "end": v(122.43, -117.35) * mm});
            skLineSegment(sketch, "E24.0.22.13", {"start": v(143.76, -122.43) * mm, "end": v(143.76, -117.35) * mm});
            skLineSegment(sketch, "E24.0.22.14", {"start": v(122.68, -122.43) * mm, "end": v(127.76, -122.43) * mm});
            skLineSegment(sketch, "E24.0.22.15", {"start": v(122.43, -117.35) * mm, "end": v(117.35, -117.35) * mm});
            skLineSegment(sketch, "E24.0.22.16", {"start": v(133.35, -122.43) * mm, "end": v(138.43, -122.43) * mm});
            skLineSegment(sketch, "E24.0.22.17", {"start": v(127.76, -117.35) * mm, "end": v(122.68, -117.35) * mm});
            skLineSegment(sketch, "E24.0.22.18", {"start": v(117.35, -117.35) * mm, "end": v(117.35, -122.43) * mm});
            skLineSegment(sketch, "E24.0.22.19", {"start": v(133.35, -117.35) * mm, "end": v(133.35, -122.43) * mm});
            skLineSegment(sketch, "E24.0.22.20", {"start": v(122.68, -117.35) * mm, "end": v(122.68, -122.43) * mm});
            skLineSegment(sketch, "E24.0.22.21", {"start": v(117.35, -122.43) * mm, "end": v(122.43, -122.43) * mm});
            skLineSegment(sketch, "E24.0.22.22", {"start": v(138.43, -117.35) * mm, "end": v(133.35, -117.35) * mm});
            skLineSegment(sketch, "E24.0.22.23", {"start": v(127.76, -122.43) * mm, "end": v(127.76, -117.35) * mm});
            skLineSegment(sketch, "E24.0.22.24", {"start": v(138.43, -122.43) * mm, "end": v(138.43, -117.35) * mm});
            skLineSegment(sketch, "E24.0.22.25", {"start": v(144.02, -117.35) * mm, "end": v(144.02, -122.43) * mm});
            skLineSegment(sketch, "E24.0.22.26", {"start": v(128.02, -122.43) * mm, "end": v(133.1, -122.43) * mm});
            skLineSegment(sketch, "E24.0.22.27", {"start": v(111.76, -122.43) * mm, "end": v(111.76, -117.35) * mm});
            skLineSegment(sketch, "E24.0.22.28", {"start": v(149.1, -117.35) * mm, "end": v(144.02, -117.35) * mm});
            skLineSegment(sketch, "E24.0.22.29", {"start": v(128.02, -117.35) * mm, "end": v(128.02, -122.43) * mm});
            skLineSegment(sketch, "E24.0.22.30", {"start": v(144.02, -122.43) * mm, "end": v(149.1, -122.43) * mm});
            skLineSegment(sketch, "E24.0.22.31", {"start": v(111.76, -117.35) * mm, "end": v(106.68, -117.35) * mm});
            skLineSegment(sketch, "E24.0.23.0", {"start": v(133.1, -122.68) * mm, "end": v(128.02, -122.68) * mm});
            skLineSegment(sketch, "E24.0.23.1", {"start": v(106.68, -122.68) * mm, "end": v(106.68, -127.76) * mm});
            skLineSegment(sketch, "E24.0.23.2", {"start": v(133.1, -127.76) * mm, "end": v(133.1, -122.68) * mm});
            skLineSegment(sketch, "E24.0.23.3", {"start": v(106.68, -127.76) * mm, "end": v(111.76, -127.76) * mm});
            skLineSegment(sketch, "E24.0.23.4", {"start": v(117.1, -127.76) * mm, "end": v(117.1, -122.68) * mm});
            skLineSegment(sketch, "E24.0.23.5", {"start": v(117.1, -122.68) * mm, "end": v(112.01, -122.68) * mm});
            skLineSegment(sketch, "E24.0.23.6", {"start": v(149.1, -127.76) * mm, "end": v(149.1, -122.68) * mm});
            skLineSegment(sketch, "E24.0.23.7", {"start": v(138.68, -127.76) * mm, "end": v(143.76, -127.76) * mm});
            skLineSegment(sketch, "E24.0.23.8", {"start": v(112.01, -122.68) * mm, "end": v(112.01, -127.76) * mm});
            skLineSegment(sketch, "E24.0.23.9", {"start": v(138.68, -122.68) * mm, "end": v(138.68, -127.76) * mm});
            skLineSegment(sketch, "E24.0.23.10", {"start": v(112.01, -127.76) * mm, "end": v(117.1, -127.76) * mm});
            skLineSegment(sketch, "E24.0.23.11", {"start": v(143.76, -122.68) * mm, "end": v(138.68, -122.68) * mm});
            skLineSegment(sketch, "E24.0.23.12", {"start": v(122.43, -127.76) * mm, "end": v(122.43, -122.68) * mm});
            skLineSegment(sketch, "E24.0.23.13", {"start": v(143.76, -127.76) * mm, "end": v(143.76, -122.68) * mm});
            skLineSegment(sketch, "E24.0.23.14", {"start": v(122.68, -127.76) * mm, "end": v(127.76, -127.76) * mm});
            skLineSegment(sketch, "E24.0.23.15", {"start": v(122.43, -122.68) * mm, "end": v(117.35, -122.68) * mm});
            skLineSegment(sketch, "E24.0.23.16", {"start": v(133.35, -127.76) * mm, "end": v(138.43, -127.76) * mm});
            skLineSegment(sketch, "E24.0.23.17", {"start": v(127.76, -122.68) * mm, "end": v(122.68, -122.68) * mm});
            skLineSegment(sketch, "E24.0.23.18", {"start": v(117.35, -122.68) * mm, "end": v(117.35, -127.76) * mm});
            skLineSegment(sketch, "E24.0.23.19", {"start": v(133.35, -122.68) * mm, "end": v(133.35, -127.76) * mm});
            skLineSegment(sketch, "E24.0.23.20", {"start": v(122.68, -122.68) * mm, "end": v(122.68, -127.76) * mm});
            skLineSegment(sketch, "E24.0.23.21", {"start": v(117.35, -127.76) * mm, "end": v(122.43, -127.76) * mm});
            skLineSegment(sketch, "E24.0.23.22", {"start": v(138.43, -122.68) * mm, "end": v(133.35, -122.68) * mm});
            skLineSegment(sketch, "E24.0.23.23", {"start": v(127.76, -127.76) * mm, "end": v(127.76, -122.68) * mm});
            skLineSegment(sketch, "E24.0.23.24", {"start": v(138.43, -127.76) * mm, "end": v(138.43, -122.68) * mm});
            skLineSegment(sketch, "E24.0.23.25", {"start": v(144.02, -122.68) * mm, "end": v(144.02, -127.76) * mm});
            skLineSegment(sketch, "E24.0.23.26", {"start": v(128.02, -127.76) * mm, "end": v(133.1, -127.76) * mm});
            skLineSegment(sketch, "E24.0.23.27", {"start": v(111.76, -127.76) * mm, "end": v(111.76, -122.68) * mm});
            skLineSegment(sketch, "E24.0.23.28", {"start": v(149.1, -122.68) * mm, "end": v(144.02, -122.68) * mm});
            skLineSegment(sketch, "E24.0.23.29", {"start": v(128.02, -122.68) * mm, "end": v(128.02, -127.76) * mm});
            skLineSegment(sketch, "E24.0.23.30", {"start": v(144.02, -127.76) * mm, "end": v(149.1, -127.76) * mm});
            skLineSegment(sketch, "E24.0.23.31", {"start": v(111.76, -122.68) * mm, "end": v(106.68, -122.68) * mm});
            skLineSegment(sketch, "E24.0.24.0", {"start": v(133.1, -128.02) * mm, "end": v(128.02, -128.02) * mm});
            skLineSegment(sketch, "E24.0.24.1", {"start": v(106.68, -128.02) * mm, "end": v(106.68, -133.1) * mm});
            skLineSegment(sketch, "E24.0.24.2", {"start": v(133.1, -133.1) * mm, "end": v(133.1, -128.02) * mm});
            skLineSegment(sketch, "E24.0.24.3", {"start": v(106.68, -133.1) * mm, "end": v(111.76, -133.1) * mm});
            skLineSegment(sketch, "E24.0.24.4", {"start": v(117.1, -133.1) * mm, "end": v(117.1, -128.02) * mm});
            skLineSegment(sketch, "E24.0.24.5", {"start": v(117.1, -128.02) * mm, "end": v(112.01, -128.02) * mm});
            skLineSegment(sketch, "E24.0.24.6", {"start": v(149.1, -133.1) * mm, "end": v(149.1, -128.02) * mm});
            skLineSegment(sketch, "E24.0.24.7", {"start": v(138.68, -133.1) * mm, "end": v(143.76, -133.1) * mm});
            skLineSegment(sketch, "E24.0.24.8", {"start": v(112.01, -128.02) * mm, "end": v(112.01, -133.1) * mm});
            skLineSegment(sketch, "E24.0.24.9", {"start": v(138.68, -128.02) * mm, "end": v(138.68, -133.1) * mm});
            skLineSegment(sketch, "E24.0.24.10", {"start": v(112.01, -133.1) * mm, "end": v(117.1, -133.1) * mm});
            skLineSegment(sketch, "E24.0.24.11", {"start": v(143.76, -128.02) * mm, "end": v(138.68, -128.02) * mm});
            skLineSegment(sketch, "E24.0.24.12", {"start": v(122.43, -133.1) * mm, "end": v(122.43, -128.02) * mm});
            skLineSegment(sketch, "E24.0.24.13", {"start": v(143.76, -133.1) * mm, "end": v(143.76, -128.02) * mm});
            skLineSegment(sketch, "E24.0.24.14", {"start": v(122.68, -133.1) * mm, "end": v(127.76, -133.1) * mm});
            skLineSegment(sketch, "E24.0.24.15", {"start": v(122.43, -128.02) * mm, "end": v(117.35, -128.02) * mm});
            skLineSegment(sketch, "E24.0.24.16", {"start": v(133.35, -133.1) * mm, "end": v(138.43, -133.1) * mm});
            skLineSegment(sketch, "E24.0.24.17", {"start": v(127.76, -128.02) * mm, "end": v(122.68, -128.02) * mm});
            skLineSegment(sketch, "E24.0.24.18", {"start": v(117.35, -128.02) * mm, "end": v(117.35, -133.1) * mm});
            skLineSegment(sketch, "E24.0.24.19", {"start": v(133.35, -128.02) * mm, "end": v(133.35, -133.1) * mm});
            skLineSegment(sketch, "E24.0.24.20", {"start": v(122.68, -128.02) * mm, "end": v(122.68, -133.1) * mm});
            skLineSegment(sketch, "E24.0.24.21", {"start": v(117.35, -133.1) * mm, "end": v(122.43, -133.1) * mm});
            skLineSegment(sketch, "E24.0.24.22", {"start": v(138.43, -128.02) * mm, "end": v(133.35, -128.02) * mm});
            skLineSegment(sketch, "E24.0.24.23", {"start": v(127.76, -133.1) * mm, "end": v(127.76, -128.02) * mm});
            skLineSegment(sketch, "E24.0.24.24", {"start": v(138.43, -133.1) * mm, "end": v(138.43, -128.02) * mm});
            skLineSegment(sketch, "E24.0.24.25", {"start": v(144.02, -128.02) * mm, "end": v(144.02, -133.1) * mm});
            skLineSegment(sketch, "E24.0.24.26", {"start": v(128.02, -133.1) * mm, "end": v(133.1, -133.1) * mm});
            skLineSegment(sketch, "E24.0.24.27", {"start": v(111.76, -133.1) * mm, "end": v(111.76, -128.02) * mm});
            skLineSegment(sketch, "E24.0.24.28", {"start": v(149.1, -128.02) * mm, "end": v(144.02, -128.02) * mm});
            skLineSegment(sketch, "E24.0.24.29", {"start": v(128.02, -128.02) * mm, "end": v(128.02, -133.1) * mm});
            skLineSegment(sketch, "E24.0.24.30", {"start": v(144.02, -133.1) * mm, "end": v(149.1, -133.1) * mm});
            skLineSegment(sketch, "E24.0.24.31", {"start": v(111.76, -128.02) * mm, "end": v(106.68, -128.02) * mm});
            skLineSegment(sketch, "E24.0.25.0", {"start": v(133.1, -133.35) * mm, "end": v(128.02, -133.35) * mm});
            skLineSegment(sketch, "E24.0.25.1", {"start": v(106.68, -133.35) * mm, "end": v(106.68, -138.43) * mm});
            skLineSegment(sketch, "E24.0.25.2", {"start": v(133.1, -138.43) * mm, "end": v(133.1, -133.35) * mm});
            skLineSegment(sketch, "E24.0.25.3", {"start": v(106.68, -138.43) * mm, "end": v(111.76, -138.43) * mm});
            skLineSegment(sketch, "E24.0.25.4", {"start": v(117.1, -138.43) * mm, "end": v(117.1, -133.35) * mm});
            skLineSegment(sketch, "E24.0.25.5", {"start": v(117.1, -133.35) * mm, "end": v(112.01, -133.35) * mm});
            skLineSegment(sketch, "E24.0.25.6", {"start": v(149.1, -138.43) * mm, "end": v(149.1, -133.35) * mm});
            skLineSegment(sketch, "E24.0.25.7", {"start": v(138.68, -138.43) * mm, "end": v(143.76, -138.43) * mm});
            skLineSegment(sketch, "E24.0.25.8", {"start": v(112.01, -133.35) * mm, "end": v(112.01, -138.43) * mm});
            skLineSegment(sketch, "E24.0.25.9", {"start": v(138.68, -133.35) * mm, "end": v(138.68, -138.43) * mm});
            skLineSegment(sketch, "E24.0.25.10", {"start": v(112.01, -138.43) * mm, "end": v(117.1, -138.43) * mm});
            skLineSegment(sketch, "E24.0.25.11", {"start": v(143.76, -133.35) * mm, "end": v(138.68, -133.35) * mm});
            skLineSegment(sketch, "E24.0.25.12", {"start": v(122.43, -138.43) * mm, "end": v(122.43, -133.35) * mm});
            skLineSegment(sketch, "E24.0.25.13", {"start": v(143.76, -138.43) * mm, "end": v(143.76, -133.35) * mm});
            skLineSegment(sketch, "E24.0.25.14", {"start": v(122.68, -138.43) * mm, "end": v(127.76, -138.43) * mm});
            skLineSegment(sketch, "E24.0.25.15", {"start": v(122.43, -133.35) * mm, "end": v(117.35, -133.35) * mm});
            skLineSegment(sketch, "E24.0.25.16", {"start": v(133.35, -138.43) * mm, "end": v(138.43, -138.43) * mm});
            skLineSegment(sketch, "E24.0.25.17", {"start": v(127.76, -133.35) * mm, "end": v(122.68, -133.35) * mm});
            skLineSegment(sketch, "E24.0.25.18", {"start": v(117.35, -133.35) * mm, "end": v(117.35, -138.43) * mm});
            skLineSegment(sketch, "E24.0.25.19", {"start": v(133.35, -133.35) * mm, "end": v(133.35, -138.43) * mm});
            skLineSegment(sketch, "E24.0.25.20", {"start": v(122.68, -133.35) * mm, "end": v(122.68, -138.43) * mm});
            skLineSegment(sketch, "E24.0.25.21", {"start": v(117.35, -138.43) * mm, "end": v(122.43, -138.43) * mm});
            skLineSegment(sketch, "E24.0.25.22", {"start": v(138.43, -133.35) * mm, "end": v(133.35, -133.35) * mm});
            skLineSegment(sketch, "E24.0.25.23", {"start": v(127.76, -138.43) * mm, "end": v(127.76, -133.35) * mm});
            skLineSegment(sketch, "E24.0.25.24", {"start": v(138.43, -138.43) * mm, "end": v(138.43, -133.35) * mm});
            skLineSegment(sketch, "E24.0.25.25", {"start": v(144.02, -133.35) * mm, "end": v(144.02, -138.43) * mm});
            skLineSegment(sketch, "E24.0.25.26", {"start": v(128.02, -138.43) * mm, "end": v(133.1, -138.43) * mm});
            skLineSegment(sketch, "E24.0.25.27", {"start": v(111.76, -138.43) * mm, "end": v(111.76, -133.35) * mm});
            skLineSegment(sketch, "E24.0.25.28", {"start": v(149.1, -133.35) * mm, "end": v(144.02, -133.35) * mm});
            skLineSegment(sketch, "E24.0.25.29", {"start": v(128.02, -133.35) * mm, "end": v(128.02, -138.43) * mm});
            skLineSegment(sketch, "E24.0.25.30", {"start": v(144.02, -138.43) * mm, "end": v(149.1, -138.43) * mm});
            skLineSegment(sketch, "E24.0.25.31", {"start": v(111.76, -133.35) * mm, "end": v(106.68, -133.35) * mm});
            skLineSegment(sketch, "E24.0.26.0", {"start": v(133.1, -138.68) * mm, "end": v(128.02, -138.68) * mm});
            skLineSegment(sketch, "E24.0.26.1", {"start": v(106.68, -138.68) * mm, "end": v(106.68, -143.76) * mm});
            skLineSegment(sketch, "E24.0.26.2", {"start": v(133.1, -143.76) * mm, "end": v(133.1, -138.68) * mm});
            skLineSegment(sketch, "E24.0.26.3", {"start": v(106.68, -143.76) * mm, "end": v(111.76, -143.76) * mm});
            skLineSegment(sketch, "E24.0.26.4", {"start": v(117.1, -143.76) * mm, "end": v(117.1, -138.68) * mm});
            skLineSegment(sketch, "E24.0.26.5", {"start": v(117.1, -138.68) * mm, "end": v(112.01, -138.68) * mm});
            skLineSegment(sketch, "E24.0.26.6", {"start": v(149.1, -143.76) * mm, "end": v(149.1, -138.68) * mm});
            skLineSegment(sketch, "E24.0.26.7", {"start": v(138.68, -143.76) * mm, "end": v(143.76, -143.76) * mm});
            skLineSegment(sketch, "E24.0.26.8", {"start": v(112.01, -138.68) * mm, "end": v(112.01, -143.76) * mm});
            skLineSegment(sketch, "E24.0.26.9", {"start": v(138.68, -138.68) * mm, "end": v(138.68, -143.76) * mm});
            skLineSegment(sketch, "E24.0.26.10", {"start": v(112.01, -143.76) * mm, "end": v(117.1, -143.76) * mm});
            skLineSegment(sketch, "E24.0.26.11", {"start": v(143.76, -138.68) * mm, "end": v(138.68, -138.68) * mm});
            skLineSegment(sketch, "E24.0.26.12", {"start": v(122.43, -143.76) * mm, "end": v(122.43, -138.68) * mm});
            skLineSegment(sketch, "E24.0.26.13", {"start": v(143.76, -143.76) * mm, "end": v(143.76, -138.68) * mm});
            skLineSegment(sketch, "E24.0.26.14", {"start": v(122.68, -143.76) * mm, "end": v(127.76, -143.76) * mm});
            skLineSegment(sketch, "E24.0.26.15", {"start": v(122.43, -138.68) * mm, "end": v(117.35, -138.68) * mm});
            skLineSegment(sketch, "E24.0.26.16", {"start": v(133.35, -143.76) * mm, "end": v(138.43, -143.76) * mm});
            skLineSegment(sketch, "E24.0.26.17", {"start": v(127.76, -138.68) * mm, "end": v(122.68, -138.68) * mm});
            skLineSegment(sketch, "E24.0.26.18", {"start": v(117.35, -138.68) * mm, "end": v(117.35, -143.76) * mm});
            skLineSegment(sketch, "E24.0.26.19", {"start": v(133.35, -138.68) * mm, "end": v(133.35, -143.76) * mm});
            skLineSegment(sketch, "E24.0.26.20", {"start": v(122.68, -138.68) * mm, "end": v(122.68, -143.76) * mm});
            skLineSegment(sketch, "E24.0.26.21", {"start": v(117.35, -143.76) * mm, "end": v(122.43, -143.76) * mm});
            skLineSegment(sketch, "E24.0.26.22", {"start": v(138.43, -138.68) * mm, "end": v(133.35, -138.68) * mm});
            skLineSegment(sketch, "E24.0.26.23", {"start": v(127.76, -143.76) * mm, "end": v(127.76, -138.68) * mm});
            skLineSegment(sketch, "E24.0.26.24", {"start": v(138.43, -143.76) * mm, "end": v(138.43, -138.68) * mm});
            skLineSegment(sketch, "E24.0.26.25", {"start": v(144.02, -138.68) * mm, "end": v(144.02, -143.76) * mm});
            skLineSegment(sketch, "E24.0.26.26", {"start": v(128.02, -143.76) * mm, "end": v(133.1, -143.76) * mm});
            skLineSegment(sketch, "E24.0.26.27", {"start": v(111.76, -143.76) * mm, "end": v(111.76, -138.68) * mm});
            skLineSegment(sketch, "E24.0.26.28", {"start": v(149.1, -138.68) * mm, "end": v(144.02, -138.68) * mm});
            skLineSegment(sketch, "E24.0.26.29", {"start": v(128.02, -138.68) * mm, "end": v(128.02, -143.76) * mm});
            skLineSegment(sketch, "E24.0.26.30", {"start": v(144.02, -143.76) * mm, "end": v(149.1, -143.76) * mm});
            skLineSegment(sketch, "E24.0.26.31", {"start": v(111.76, -138.68) * mm, "end": v(106.68, -138.68) * mm});
            skLineSegment(sketch, "E24.0.27.0", {"start": v(133.1, -144.02) * mm, "end": v(128.02, -144.02) * mm});
            skLineSegment(sketch, "E24.0.27.1", {"start": v(106.68, -144.02) * mm, "end": v(106.68, -149.1) * mm});
            skLineSegment(sketch, "E24.0.27.2", {"start": v(133.1, -149.1) * mm, "end": v(133.1, -144.02) * mm});
            skLineSegment(sketch, "E24.0.27.3", {"start": v(106.68, -149.1) * mm, "end": v(111.76, -149.1) * mm});
            skLineSegment(sketch, "E24.0.27.4", {"start": v(117.1, -149.1) * mm, "end": v(117.1, -144.02) * mm});
            skLineSegment(sketch, "E24.0.27.5", {"start": v(117.1, -144.02) * mm, "end": v(112.01, -144.02) * mm});
            skLineSegment(sketch, "E24.0.27.6", {"start": v(149.1, -149.1) * mm, "end": v(149.1, -144.02) * mm});
            skLineSegment(sketch, "E24.0.27.7", {"start": v(138.68, -149.1) * mm, "end": v(143.76, -149.1) * mm});
            skLineSegment(sketch, "E24.0.27.8", {"start": v(112.01, -144.02) * mm, "end": v(112.01, -149.1) * mm});
            skLineSegment(sketch, "E24.0.27.9", {"start": v(138.68, -144.02) * mm, "end": v(138.68, -149.1) * mm});
            skLineSegment(sketch, "E24.0.27.10", {"start": v(112.01, -149.1) * mm, "end": v(117.1, -149.1) * mm});
            skLineSegment(sketch, "E24.0.27.11", {"start": v(143.76, -144.02) * mm, "end": v(138.68, -144.02) * mm});
            skLineSegment(sketch, "E24.0.27.12", {"start": v(122.43, -149.1) * mm, "end": v(122.43, -144.02) * mm});
            skLineSegment(sketch, "E24.0.27.13", {"start": v(143.76, -149.1) * mm, "end": v(143.76, -144.02) * mm});
            skLineSegment(sketch, "E24.0.27.14", {"start": v(122.68, -149.1) * mm, "end": v(127.76, -149.1) * mm});
            skLineSegment(sketch, "E24.0.27.15", {"start": v(122.43, -144.02) * mm, "end": v(117.35, -144.02) * mm});
            skLineSegment(sketch, "E24.0.27.16", {"start": v(133.35, -149.1) * mm, "end": v(138.43, -149.1) * mm});
            skLineSegment(sketch, "E24.0.27.17", {"start": v(127.76, -144.02) * mm, "end": v(122.68, -144.02) * mm});
            skLineSegment(sketch, "E24.0.27.18", {"start": v(117.35, -144.02) * mm, "end": v(117.35, -149.1) * mm});
            skLineSegment(sketch, "E24.0.27.19", {"start": v(133.35, -144.02) * mm, "end": v(133.35, -149.1) * mm});
            skLineSegment(sketch, "E24.0.27.20", {"start": v(122.68, -144.02) * mm, "end": v(122.68, -149.1) * mm});
            skLineSegment(sketch, "E24.0.27.21", {"start": v(117.35, -149.1) * mm, "end": v(122.43, -149.1) * mm});
            skLineSegment(sketch, "E24.0.27.22", {"start": v(138.43, -144.02) * mm, "end": v(133.35, -144.02) * mm});
            skLineSegment(sketch, "E24.0.27.23", {"start": v(127.76, -149.1) * mm, "end": v(127.76, -144.02) * mm});
            skLineSegment(sketch, "E24.0.27.24", {"start": v(138.43, -149.1) * mm, "end": v(138.43, -144.02) * mm});
            skLineSegment(sketch, "E24.0.27.25", {"start": v(144.02, -144.02) * mm, "end": v(144.02, -149.1) * mm});
            skLineSegment(sketch, "E24.0.27.26", {"start": v(128.02, -149.1) * mm, "end": v(133.1, -149.1) * mm});
            skLineSegment(sketch, "E24.0.27.27", {"start": v(111.76, -149.1) * mm, "end": v(111.76, -144.02) * mm});
            skLineSegment(sketch, "E24.0.27.28", {"start": v(149.1, -144.02) * mm, "end": v(144.02, -144.02) * mm});
            skLineSegment(sketch, "E24.0.27.29", {"start": v(128.02, -144.02) * mm, "end": v(128.02, -149.1) * mm});
            skLineSegment(sketch, "E24.0.27.30", {"start": v(144.02, -149.1) * mm, "end": v(149.1, -149.1) * mm});
            skLineSegment(sketch, "E24.0.27.31", {"start": v(111.76, -144.02) * mm, "end": v(106.68, -144.02) * mm});
            skLineSegment(sketch, "E24.0.28.0", {"start": v(133.1, -149.35) * mm, "end": v(128.02, -149.35) * mm});
            skLineSegment(sketch, "E24.0.28.1", {"start": v(106.68, -149.35) * mm, "end": v(106.68, -154.43) * mm});
            skLineSegment(sketch, "E24.0.28.2", {"start": v(133.1, -154.43) * mm, "end": v(133.1, -149.35) * mm});
            skLineSegment(sketch, "E24.0.28.3", {"start": v(106.68, -154.43) * mm, "end": v(111.76, -154.43) * mm});
            skLineSegment(sketch, "E24.0.28.4", {"start": v(117.1, -154.43) * mm, "end": v(117.1, -149.35) * mm});
            skLineSegment(sketch, "E24.0.28.5", {"start": v(117.1, -149.35) * mm, "end": v(112.01, -149.35) * mm});
            skLineSegment(sketch, "E24.0.28.6", {"start": v(149.1, -154.43) * mm, "end": v(149.1, -149.35) * mm});
            skLineSegment(sketch, "E24.0.28.7", {"start": v(138.68, -154.43) * mm, "end": v(143.76, -154.43) * mm});
            skLineSegment(sketch, "E24.0.28.8", {"start": v(112.01, -149.35) * mm, "end": v(112.01, -154.43) * mm});
            skLineSegment(sketch, "E24.0.28.9", {"start": v(138.68, -149.35) * mm, "end": v(138.68, -154.43) * mm});
            skLineSegment(sketch, "E24.0.28.10", {"start": v(112.01, -154.43) * mm, "end": v(117.1, -154.43) * mm});
            skLineSegment(sketch, "E24.0.28.11", {"start": v(143.76, -149.35) * mm, "end": v(138.68, -149.35) * mm});
            skLineSegment(sketch, "E24.0.28.12", {"start": v(122.43, -154.43) * mm, "end": v(122.43, -149.35) * mm});
            skLineSegment(sketch, "E24.0.28.13", {"start": v(143.76, -154.43) * mm, "end": v(143.76, -149.35) * mm});
            skLineSegment(sketch, "E24.0.28.14", {"start": v(122.68, -154.43) * mm, "end": v(127.76, -154.43) * mm});
            skLineSegment(sketch, "E24.0.28.15", {"start": v(122.43, -149.35) * mm, "end": v(117.35, -149.35) * mm});
            skLineSegment(sketch, "E24.0.28.16", {"start": v(133.35, -154.43) * mm, "end": v(138.43, -154.43) * mm});
            skLineSegment(sketch, "E24.0.28.17", {"start": v(127.76, -149.35) * mm, "end": v(122.68, -149.35) * mm});
            skLineSegment(sketch, "E24.0.28.18", {"start": v(117.35, -149.35) * mm, "end": v(117.35, -154.43) * mm});
            skLineSegment(sketch, "E24.0.28.19", {"start": v(133.35, -149.35) * mm, "end": v(133.35, -154.43) * mm});
            skLineSegment(sketch, "E24.0.28.20", {"start": v(122.68, -149.35) * mm, "end": v(122.68, -154.43) * mm});
            skLineSegment(sketch, "E24.0.28.21", {"start": v(117.35, -154.43) * mm, "end": v(122.43, -154.43) * mm});
            skLineSegment(sketch, "E24.0.28.22", {"start": v(138.43, -149.35) * mm, "end": v(133.35, -149.35) * mm});
            skLineSegment(sketch, "E24.0.28.23", {"start": v(127.76, -154.43) * mm, "end": v(127.76, -149.35) * mm});
            skLineSegment(sketch, "E24.0.28.24", {"start": v(138.43, -154.43) * mm, "end": v(138.43, -149.35) * mm});
            skLineSegment(sketch, "E24.0.28.25", {"start": v(144.02, -149.35) * mm, "end": v(144.02, -154.43) * mm});
            skLineSegment(sketch, "E24.0.28.26", {"start": v(128.02, -154.43) * mm, "end": v(133.1, -154.43) * mm});
            skLineSegment(sketch, "E24.0.28.27", {"start": v(111.76, -154.43) * mm, "end": v(111.76, -149.35) * mm});
            skLineSegment(sketch, "E24.0.28.28", {"start": v(149.1, -149.35) * mm, "end": v(144.02, -149.35) * mm});
            skLineSegment(sketch, "E24.0.28.29", {"start": v(128.02, -149.35) * mm, "end": v(128.02, -154.43) * mm});
            skLineSegment(sketch, "E24.0.28.30", {"start": v(144.02, -154.43) * mm, "end": v(149.1, -154.43) * mm});
            skLineSegment(sketch, "E24.0.28.31", {"start": v(111.76, -149.35) * mm, "end": v(106.68, -149.35) * mm});
            skLineSegment(sketch, "E24.0.29.0", {"start": v(133.1, -154.69) * mm, "end": v(128.02, -154.69) * mm});
            skLineSegment(sketch, "E24.0.29.1", {"start": v(106.68, -154.69) * mm, "end": v(106.68, -159.77) * mm});
            skLineSegment(sketch, "E24.0.29.2", {"start": v(133.1, -159.77) * mm, "end": v(133.1, -154.69) * mm});
            skLineSegment(sketch, "E24.0.29.3", {"start": v(106.68, -159.77) * mm, "end": v(111.76, -159.77) * mm});
            skLineSegment(sketch, "E24.0.29.4", {"start": v(117.1, -159.77) * mm, "end": v(117.1, -154.69) * mm});
            skLineSegment(sketch, "E24.0.29.5", {"start": v(117.1, -154.69) * mm, "end": v(112.01, -154.69) * mm});
            skLineSegment(sketch, "E24.0.29.6", {"start": v(149.1, -159.77) * mm, "end": v(149.1, -154.69) * mm});
            skLineSegment(sketch, "E24.0.29.7", {"start": v(138.68, -159.77) * mm, "end": v(143.76, -159.77) * mm});
            skLineSegment(sketch, "E24.0.29.8", {"start": v(112.01, -154.69) * mm, "end": v(112.01, -159.77) * mm});
            skLineSegment(sketch, "E24.0.29.9", {"start": v(138.68, -154.69) * mm, "end": v(138.68, -159.77) * mm});
            skLineSegment(sketch, "E24.0.29.10", {"start": v(112.01, -159.77) * mm, "end": v(117.1, -159.77) * mm});
            skLineSegment(sketch, "E24.0.29.11", {"start": v(143.76, -154.69) * mm, "end": v(138.68, -154.69) * mm});
            skLineSegment(sketch, "E24.0.29.12", {"start": v(122.43, -159.77) * mm, "end": v(122.43, -154.69) * mm});
            skLineSegment(sketch, "E24.0.29.13", {"start": v(143.76, -159.77) * mm, "end": v(143.76, -154.69) * mm});
            skLineSegment(sketch, "E24.0.29.14", {"start": v(122.68, -159.77) * mm, "end": v(127.76, -159.77) * mm});
            skLineSegment(sketch, "E24.0.29.15", {"start": v(122.43, -154.69) * mm, "end": v(117.35, -154.69) * mm});
            skLineSegment(sketch, "E24.0.29.16", {"start": v(133.35, -159.77) * mm, "end": v(138.43, -159.77) * mm});
            skLineSegment(sketch, "E24.0.29.17", {"start": v(127.76, -154.69) * mm, "end": v(122.68, -154.69) * mm});
            skLineSegment(sketch, "E24.0.29.18", {"start": v(117.35, -154.69) * mm, "end": v(117.35, -159.77) * mm});
            skLineSegment(sketch, "E24.0.29.19", {"start": v(133.35, -154.69) * mm, "end": v(133.35, -159.77) * mm});
            skLineSegment(sketch, "E24.0.29.20", {"start": v(122.68, -154.69) * mm, "end": v(122.68, -159.77) * mm});
            skLineSegment(sketch, "E24.0.29.21", {"start": v(117.35, -159.77) * mm, "end": v(122.43, -159.77) * mm});
            skLineSegment(sketch, "E24.0.29.22", {"start": v(138.43, -154.69) * mm, "end": v(133.35, -154.69) * mm});
            skLineSegment(sketch, "E24.0.29.23", {"start": v(127.76, -159.77) * mm, "end": v(127.76, -154.69) * mm});
            skLineSegment(sketch, "E24.0.29.24", {"start": v(138.43, -159.77) * mm, "end": v(138.43, -154.69) * mm});
            skLineSegment(sketch, "E24.0.29.25", {"start": v(144.02, -154.69) * mm, "end": v(144.02, -159.77) * mm});
            skLineSegment(sketch, "E24.0.29.26", {"start": v(128.02, -159.77) * mm, "end": v(133.1, -159.77) * mm});
            skLineSegment(sketch, "E24.0.29.27", {"start": v(111.76, -159.77) * mm, "end": v(111.76, -154.69) * mm});
            skLineSegment(sketch, "E24.0.29.28", {"start": v(149.1, -154.69) * mm, "end": v(144.02, -154.69) * mm});
            skLineSegment(sketch, "E24.0.29.29", {"start": v(128.02, -154.69) * mm, "end": v(128.02, -159.77) * mm});
            skLineSegment(sketch, "E24.0.29.30", {"start": v(144.02, -159.77) * mm, "end": v(149.1, -159.77) * mm});
            skLineSegment(sketch, "E24.0.29.31", {"start": v(111.76, -154.69) * mm, "end": v(106.68, -154.69) * mm});
            skLineSegment(sketch, "E24.0.30.0", {"start": v(133.1, -160.02) * mm, "end": v(128.02, -160.02) * mm});
            skLineSegment(sketch, "E24.0.30.1", {"start": v(106.68, -160.02) * mm, "end": v(106.68, -165.1) * mm});
            skLineSegment(sketch, "E24.0.30.2", {"start": v(133.1, -165.1) * mm, "end": v(133.1, -160.02) * mm});
            skLineSegment(sketch, "E24.0.30.3", {"start": v(106.68, -165.1) * mm, "end": v(111.76, -165.1) * mm});
            skLineSegment(sketch, "E24.0.30.4", {"start": v(117.1, -165.1) * mm, "end": v(117.1, -160.02) * mm});
            skLineSegment(sketch, "E24.0.30.5", {"start": v(117.1, -160.02) * mm, "end": v(112.01, -160.02) * mm});
            skLineSegment(sketch, "E24.0.30.6", {"start": v(149.1, -165.1) * mm, "end": v(149.1, -160.02) * mm});
            skLineSegment(sketch, "E24.0.30.7", {"start": v(138.68, -165.1) * mm, "end": v(143.76, -165.1) * mm});
            skLineSegment(sketch, "E24.0.30.8", {"start": v(112.01, -160.02) * mm, "end": v(112.01, -165.1) * mm});
            skLineSegment(sketch, "E24.0.30.9", {"start": v(138.68, -160.02) * mm, "end": v(138.68, -165.1) * mm});
            skLineSegment(sketch, "E24.0.30.10", {"start": v(112.01, -165.1) * mm, "end": v(117.1, -165.1) * mm});
            skLineSegment(sketch, "E24.0.30.11", {"start": v(143.76, -160.02) * mm, "end": v(138.68, -160.02) * mm});
            skLineSegment(sketch, "E24.0.30.12", {"start": v(122.43, -165.1) * mm, "end": v(122.43, -160.02) * mm});
            skLineSegment(sketch, "E24.0.30.13", {"start": v(143.76, -165.1) * mm, "end": v(143.76, -160.02) * mm});
            skLineSegment(sketch, "E24.0.30.14", {"start": v(122.68, -165.1) * mm, "end": v(127.76, -165.1) * mm});
            skLineSegment(sketch, "E24.0.30.15", {"start": v(122.43, -160.02) * mm, "end": v(117.35, -160.02) * mm});
            skLineSegment(sketch, "E24.0.30.16", {"start": v(133.35, -165.1) * mm, "end": v(138.43, -165.1) * mm});
            skLineSegment(sketch, "E24.0.30.17", {"start": v(127.76, -160.02) * mm, "end": v(122.68, -160.02) * mm});
            skLineSegment(sketch, "E24.0.30.18", {"start": v(117.35, -160.02) * mm, "end": v(117.35, -165.1) * mm});
            skLineSegment(sketch, "E24.0.30.19", {"start": v(133.35, -160.02) * mm, "end": v(133.35, -165.1) * mm});
            skLineSegment(sketch, "E24.0.30.20", {"start": v(122.68, -160.02) * mm, "end": v(122.68, -165.1) * mm});
            skLineSegment(sketch, "E24.0.30.21", {"start": v(117.35, -165.1) * mm, "end": v(122.43, -165.1) * mm});
            skLineSegment(sketch, "E24.0.30.22", {"start": v(138.43, -160.02) * mm, "end": v(133.35, -160.02) * mm});
            skLineSegment(sketch, "E24.0.30.23", {"start": v(127.76, -165.1) * mm, "end": v(127.76, -160.02) * mm});
            skLineSegment(sketch, "E24.0.30.24", {"start": v(138.43, -165.1) * mm, "end": v(138.43, -160.02) * mm});
            skLineSegment(sketch, "E24.0.30.25", {"start": v(144.02, -160.02) * mm, "end": v(144.02, -165.1) * mm});
            skLineSegment(sketch, "E24.0.30.26", {"start": v(128.02, -165.1) * mm, "end": v(133.1, -165.1) * mm});
            skLineSegment(sketch, "E24.0.30.27", {"start": v(111.76, -165.1) * mm, "end": v(111.76, -160.02) * mm});
            skLineSegment(sketch, "E24.0.30.28", {"start": v(149.1, -160.02) * mm, "end": v(144.02, -160.02) * mm});
            skLineSegment(sketch, "E24.0.30.29", {"start": v(128.02, -160.02) * mm, "end": v(128.02, -165.1) * mm});
            skLineSegment(sketch, "E24.0.30.30", {"start": v(144.02, -165.1) * mm, "end": v(149.1, -165.1) * mm});
            skLineSegment(sketch, "E24.0.30.31", {"start": v(111.76, -160.02) * mm, "end": v(106.68, -160.02) * mm});
            skLineSegment(sketch, "E24.0.31.0", {"start": v(133.1, -165.35) * mm, "end": v(128.02, -165.35) * mm});
            skLineSegment(sketch, "E24.0.31.1", {"start": v(106.68, -165.35) * mm, "end": v(106.68, -170.43) * mm});
            skLineSegment(sketch, "E24.0.31.2", {"start": v(133.1, -170.43) * mm, "end": v(133.1, -165.35) * mm});
            skLineSegment(sketch, "E24.0.31.3", {"start": v(106.68, -170.43) * mm, "end": v(111.76, -170.43) * mm});
            skLineSegment(sketch, "E24.0.31.4", {"start": v(117.1, -170.43) * mm, "end": v(117.1, -165.35) * mm});
            skLineSegment(sketch, "E24.0.31.5", {"start": v(117.1, -165.35) * mm, "end": v(112.01, -165.35) * mm});
            skLineSegment(sketch, "E24.0.31.6", {"start": v(149.1, -170.43) * mm, "end": v(149.1, -165.35) * mm});
            skLineSegment(sketch, "E24.0.31.7", {"start": v(138.68, -170.43) * mm, "end": v(143.76, -170.43) * mm});
            skLineSegment(sketch, "E24.0.31.8", {"start": v(112.01, -165.35) * mm, "end": v(112.01, -170.43) * mm});
            skLineSegment(sketch, "E24.0.31.9", {"start": v(138.68, -165.35) * mm, "end": v(138.68, -170.43) * mm});
            skLineSegment(sketch, "E24.0.31.10", {"start": v(112.01, -170.43) * mm, "end": v(117.1, -170.43) * mm});
            skLineSegment(sketch, "E24.0.31.11", {"start": v(143.76, -165.35) * mm, "end": v(138.68, -165.35) * mm});
            skLineSegment(sketch, "E24.0.31.12", {"start": v(122.43, -170.43) * mm, "end": v(122.43, -165.35) * mm});
            skLineSegment(sketch, "E24.0.31.13", {"start": v(143.76, -170.43) * mm, "end": v(143.76, -165.35) * mm});
            skLineSegment(sketch, "E24.0.31.14", {"start": v(122.68, -170.43) * mm, "end": v(127.76, -170.43) * mm});
            skLineSegment(sketch, "E24.0.31.15", {"start": v(122.43, -165.35) * mm, "end": v(117.35, -165.35) * mm});
            skLineSegment(sketch, "E24.0.31.16", {"start": v(133.35, -170.43) * mm, "end": v(138.43, -170.43) * mm});
            skLineSegment(sketch, "E24.0.31.17", {"start": v(127.76, -165.35) * mm, "end": v(122.68, -165.35) * mm});
            skLineSegment(sketch, "E24.0.31.18", {"start": v(117.35, -165.35) * mm, "end": v(117.35, -170.43) * mm});
            skLineSegment(sketch, "E24.0.31.19", {"start": v(133.35, -165.35) * mm, "end": v(133.35, -170.43) * mm});
            skLineSegment(sketch, "E24.0.31.20", {"start": v(122.68, -165.35) * mm, "end": v(122.68, -170.43) * mm});
            skLineSegment(sketch, "E24.0.31.21", {"start": v(117.35, -170.43) * mm, "end": v(122.43, -170.43) * mm});
            skLineSegment(sketch, "E24.0.31.22", {"start": v(138.43, -165.35) * mm, "end": v(133.35, -165.35) * mm});
            skLineSegment(sketch, "E24.0.31.23", {"start": v(127.76, -170.43) * mm, "end": v(127.76, -165.35) * mm});
            skLineSegment(sketch, "E24.0.31.24", {"start": v(138.43, -170.43) * mm, "end": v(138.43, -165.35) * mm});
            skLineSegment(sketch, "E24.0.31.25", {"start": v(144.02, -165.35) * mm, "end": v(144.02, -170.43) * mm});
            skLineSegment(sketch, "E24.0.31.26", {"start": v(128.02, -170.43) * mm, "end": v(133.1, -170.43) * mm});
            skLineSegment(sketch, "E24.0.31.27", {"start": v(111.76, -170.43) * mm, "end": v(111.76, -165.35) * mm});
            skLineSegment(sketch, "E24.0.31.28", {"start": v(149.1, -165.35) * mm, "end": v(144.02, -165.35) * mm});
            skLineSegment(sketch, "E24.0.31.29", {"start": v(128.02, -165.35) * mm, "end": v(128.02, -170.43) * mm});
            skLineSegment(sketch, "E24.0.31.30", {"start": v(144.02, -170.43) * mm, "end": v(149.1, -170.43) * mm});
            skLineSegment(sketch, "E24.0.31.31", {"start": v(111.76, -165.35) * mm, "end": v(106.68, -165.35) * mm});
            skLineSegment(sketch, "E24.0.32.0", {"start": v(133.1, -170.69) * mm, "end": v(128.02, -170.69) * mm});
            skLineSegment(sketch, "E24.0.32.1", {"start": v(106.68, -170.69) * mm, "end": v(106.68, -175.77) * mm});
            skLineSegment(sketch, "E24.0.32.2", {"start": v(133.1, -175.77) * mm, "end": v(133.1, -170.69) * mm});
            skLineSegment(sketch, "E24.0.32.3", {"start": v(106.68, -175.77) * mm, "end": v(111.76, -175.77) * mm});
            skLineSegment(sketch, "E24.0.32.4", {"start": v(117.1, -175.77) * mm, "end": v(117.1, -170.69) * mm});
            skLineSegment(sketch, "E24.0.32.5", {"start": v(117.1, -170.69) * mm, "end": v(112.01, -170.69) * mm});
            skLineSegment(sketch, "E24.0.32.6", {"start": v(149.1, -175.77) * mm, "end": v(149.1, -170.69) * mm});
            skLineSegment(sketch, "E24.0.32.7", {"start": v(138.68, -175.77) * mm, "end": v(143.76, -175.77) * mm});
            skLineSegment(sketch, "E24.0.32.8", {"start": v(112.01, -170.69) * mm, "end": v(112.01, -175.77) * mm});
            skLineSegment(sketch, "E24.0.32.9", {"start": v(138.68, -170.69) * mm, "end": v(138.68, -175.77) * mm});
            skLineSegment(sketch, "E24.0.32.10", {"start": v(112.01, -175.77) * mm, "end": v(117.1, -175.77) * mm});
            skLineSegment(sketch, "E24.0.32.11", {"start": v(143.76, -170.69) * mm, "end": v(138.68, -170.69) * mm});
            skLineSegment(sketch, "E24.0.32.12", {"start": v(122.43, -175.77) * mm, "end": v(122.43, -170.69) * mm});
            skLineSegment(sketch, "E24.0.32.13", {"start": v(143.76, -175.77) * mm, "end": v(143.76, -170.69) * mm});
            skLineSegment(sketch, "E24.0.32.14", {"start": v(122.68, -175.77) * mm, "end": v(127.76, -175.77) * mm});
            skLineSegment(sketch, "E24.0.32.15", {"start": v(122.43, -170.69) * mm, "end": v(117.35, -170.69) * mm});
            skLineSegment(sketch, "E24.0.32.16", {"start": v(133.35, -175.77) * mm, "end": v(138.43, -175.77) * mm});
            skLineSegment(sketch, "E24.0.32.17", {"start": v(127.76, -170.69) * mm, "end": v(122.68, -170.69) * mm});
            skLineSegment(sketch, "E24.0.32.18", {"start": v(117.35, -170.69) * mm, "end": v(117.35, -175.77) * mm});
            skLineSegment(sketch, "E24.0.32.19", {"start": v(133.35, -170.69) * mm, "end": v(133.35, -175.77) * mm});
            skLineSegment(sketch, "E24.0.32.20", {"start": v(122.68, -170.69) * mm, "end": v(122.68, -175.77) * mm});
            skLineSegment(sketch, "E24.0.32.21", {"start": v(117.35, -175.77) * mm, "end": v(122.43, -175.77) * mm});
            skLineSegment(sketch, "E24.0.32.22", {"start": v(138.43, -170.69) * mm, "end": v(133.35, -170.69) * mm});
            skLineSegment(sketch, "E24.0.32.23", {"start": v(127.76, -175.77) * mm, "end": v(127.76, -170.69) * mm});
            skLineSegment(sketch, "E24.0.32.24", {"start": v(138.43, -175.77) * mm, "end": v(138.43, -170.69) * mm});
            skLineSegment(sketch, "E24.0.32.25", {"start": v(144.02, -170.69) * mm, "end": v(144.02, -175.77) * mm});
            skLineSegment(sketch, "E24.0.32.26", {"start": v(128.02, -175.77) * mm, "end": v(133.1, -175.77) * mm});
            skLineSegment(sketch, "E24.0.32.27", {"start": v(111.76, -175.77) * mm, "end": v(111.76, -170.69) * mm});
            skLineSegment(sketch, "E24.0.32.28", {"start": v(149.1, -170.69) * mm, "end": v(144.02, -170.69) * mm});
            skLineSegment(sketch, "E24.0.32.29", {"start": v(128.02, -170.69) * mm, "end": v(128.02, -175.77) * mm});
            skLineSegment(sketch, "E24.0.32.30", {"start": v(144.02, -175.77) * mm, "end": v(149.1, -175.77) * mm});
            skLineSegment(sketch, "E24.0.32.31", {"start": v(111.76, -170.69) * mm, "end": v(106.68, -170.69) * mm});
            skLineSegment(sketch, "E24.0.33.0", {"start": v(133.1, -176.02) * mm, "end": v(128.02, -176.02) * mm});
            skLineSegment(sketch, "E24.0.33.1", {"start": v(106.68, -176.02) * mm, "end": v(106.68, -181.1) * mm});
            skLineSegment(sketch, "E24.0.33.2", {"start": v(133.1, -181.1) * mm, "end": v(133.1, -176.02) * mm});
            skLineSegment(sketch, "E24.0.33.3", {"start": v(106.68, -181.1) * mm, "end": v(111.76, -181.1) * mm});
            skLineSegment(sketch, "E24.0.33.4", {"start": v(117.1, -181.1) * mm, "end": v(117.1, -176.02) * mm});
            skLineSegment(sketch, "E24.0.33.5", {"start": v(117.1, -176.02) * mm, "end": v(112.01, -176.02) * mm});
            skLineSegment(sketch, "E24.0.33.6", {"start": v(149.1, -181.1) * mm, "end": v(149.1, -176.02) * mm});
            skLineSegment(sketch, "E24.0.33.7", {"start": v(138.68, -181.1) * mm, "end": v(143.76, -181.1) * mm});
            skLineSegment(sketch, "E24.0.33.8", {"start": v(112.01, -176.02) * mm, "end": v(112.01, -181.1) * mm});
            skLineSegment(sketch, "E24.0.33.9", {"start": v(138.68, -176.02) * mm, "end": v(138.68, -181.1) * mm});
            skLineSegment(sketch, "E24.0.33.10", {"start": v(112.01, -181.1) * mm, "end": v(117.1, -181.1) * mm});
            skLineSegment(sketch, "E24.0.33.11", {"start": v(143.76, -176.02) * mm, "end": v(138.68, -176.02) * mm});
            skLineSegment(sketch, "E24.0.33.12", {"start": v(122.43, -181.1) * mm, "end": v(122.43, -176.02) * mm});
            skLineSegment(sketch, "E24.0.33.13", {"start": v(143.76, -181.1) * mm, "end": v(143.76, -176.02) * mm});
            skLineSegment(sketch, "E24.0.33.14", {"start": v(122.68, -181.1) * mm, "end": v(127.76, -181.1) * mm});
            skLineSegment(sketch, "E24.0.33.15", {"start": v(122.43, -176.02) * mm, "end": v(117.35, -176.02) * mm});
            skLineSegment(sketch, "E24.0.33.16", {"start": v(133.35, -181.1) * mm, "end": v(138.43, -181.1) * mm});
            skLineSegment(sketch, "E24.0.33.17", {"start": v(127.76, -176.02) * mm, "end": v(122.68, -176.02) * mm});
            skLineSegment(sketch, "E24.0.33.18", {"start": v(117.35, -176.02) * mm, "end": v(117.35, -181.1) * mm});
            skLineSegment(sketch, "E24.0.33.19", {"start": v(133.35, -176.02) * mm, "end": v(133.35, -181.1) * mm});
            skLineSegment(sketch, "E24.0.33.20", {"start": v(122.68, -176.02) * mm, "end": v(122.68, -181.1) * mm});
            skLineSegment(sketch, "E24.0.33.21", {"start": v(117.35, -181.1) * mm, "end": v(122.43, -181.1) * mm});
            skLineSegment(sketch, "E24.0.33.22", {"start": v(138.43, -176.02) * mm, "end": v(133.35, -176.02) * mm});
            skLineSegment(sketch, "E24.0.33.23", {"start": v(127.76, -181.1) * mm, "end": v(127.76, -176.02) * mm});
            skLineSegment(sketch, "E24.0.33.24", {"start": v(138.43, -181.1) * mm, "end": v(138.43, -176.02) * mm});
            skLineSegment(sketch, "E24.0.33.25", {"start": v(144.02, -176.02) * mm, "end": v(144.02, -181.1) * mm});
            skLineSegment(sketch, "E24.0.33.26", {"start": v(128.02, -181.1) * mm, "end": v(133.1, -181.1) * mm});
            skLineSegment(sketch, "E24.0.33.27", {"start": v(111.76, -181.1) * mm, "end": v(111.76, -176.02) * mm});
            skLineSegment(sketch, "E24.0.33.28", {"start": v(149.1, -176.02) * mm, "end": v(144.02, -176.02) * mm});
            skLineSegment(sketch, "E24.0.33.29", {"start": v(128.02, -176.02) * mm, "end": v(128.02, -181.1) * mm});
            skLineSegment(sketch, "E24.0.33.30", {"start": v(144.02, -181.1) * mm, "end": v(149.1, -181.1) * mm});
            skLineSegment(sketch, "E24.0.33.31", {"start": v(111.76, -176.02) * mm, "end": v(106.68, -176.02) * mm});
            skLineSegment(sketch, "E24.0.34.0", {"start": v(133.1, -181.36) * mm, "end": v(128.02, -181.36) * mm});
            skLineSegment(sketch, "E24.0.34.1", {"start": v(106.68, -181.36) * mm, "end": v(106.68, -186.44) * mm});
            skLineSegment(sketch, "E24.0.34.2", {"start": v(133.1, -186.44) * mm, "end": v(133.1, -181.36) * mm});
            skLineSegment(sketch, "E24.0.34.3", {"start": v(106.68, -186.44) * mm, "end": v(111.76, -186.44) * mm});
            skLineSegment(sketch, "E24.0.34.4", {"start": v(117.1, -186.44) * mm, "end": v(117.1, -181.36) * mm});
            skLineSegment(sketch, "E24.0.34.5", {"start": v(117.1, -181.36) * mm, "end": v(112.01, -181.36) * mm});
            skLineSegment(sketch, "E24.0.34.6", {"start": v(149.1, -186.44) * mm, "end": v(149.1, -181.36) * mm});
            skLineSegment(sketch, "E24.0.34.7", {"start": v(138.68, -186.44) * mm, "end": v(143.76, -186.44) * mm});
            skLineSegment(sketch, "E24.0.34.8", {"start": v(112.01, -181.36) * mm, "end": v(112.01, -186.44) * mm});
            skLineSegment(sketch, "E24.0.34.9", {"start": v(138.68, -181.36) * mm, "end": v(138.68, -186.44) * mm});
            skLineSegment(sketch, "E24.0.34.10", {"start": v(112.01, -186.44) * mm, "end": v(117.1, -186.44) * mm});
            skLineSegment(sketch, "E24.0.34.11", {"start": v(143.76, -181.36) * mm, "end": v(138.68, -181.36) * mm});
            skLineSegment(sketch, "E24.0.34.12", {"start": v(122.43, -186.44) * mm, "end": v(122.43, -181.36) * mm});
            skLineSegment(sketch, "E24.0.34.13", {"start": v(143.76, -186.44) * mm, "end": v(143.76, -181.36) * mm});
            skLineSegment(sketch, "E24.0.34.14", {"start": v(122.68, -186.44) * mm, "end": v(127.76, -186.44) * mm});
            skLineSegment(sketch, "E24.0.34.15", {"start": v(122.43, -181.36) * mm, "end": v(117.35, -181.36) * mm});
            skLineSegment(sketch, "E24.0.34.16", {"start": v(133.35, -186.44) * mm, "end": v(138.43, -186.44) * mm});
            skLineSegment(sketch, "E24.0.34.17", {"start": v(127.76, -181.36) * mm, "end": v(122.68, -181.36) * mm});
            skLineSegment(sketch, "E24.0.34.18", {"start": v(117.35, -181.36) * mm, "end": v(117.35, -186.44) * mm});
            skLineSegment(sketch, "E24.0.34.19", {"start": v(133.35, -181.36) * mm, "end": v(133.35, -186.44) * mm});
            skLineSegment(sketch, "E24.0.34.20", {"start": v(122.68, -181.36) * mm, "end": v(122.68, -186.44) * mm});
            skLineSegment(sketch, "E24.0.34.21", {"start": v(117.35, -186.44) * mm, "end": v(122.43, -186.44) * mm});
            skLineSegment(sketch, "E24.0.34.22", {"start": v(138.43, -181.36) * mm, "end": v(133.35, -181.36) * mm});
            skLineSegment(sketch, "E24.0.34.23", {"start": v(127.76, -186.44) * mm, "end": v(127.76, -181.36) * mm});
            skLineSegment(sketch, "E24.0.34.24", {"start": v(138.43, -186.44) * mm, "end": v(138.43, -181.36) * mm});
            skLineSegment(sketch, "E24.0.34.25", {"start": v(144.02, -181.36) * mm, "end": v(144.02, -186.44) * mm});
            skLineSegment(sketch, "E24.0.34.26", {"start": v(128.02, -186.44) * mm, "end": v(133.1, -186.44) * mm});
            skLineSegment(sketch, "E24.0.34.27", {"start": v(111.76, -186.44) * mm, "end": v(111.76, -181.36) * mm});
            skLineSegment(sketch, "E24.0.34.28", {"start": v(149.1, -181.36) * mm, "end": v(144.02, -181.36) * mm});
            skLineSegment(sketch, "E24.0.34.29", {"start": v(128.02, -181.36) * mm, "end": v(128.02, -186.44) * mm});
            skLineSegment(sketch, "E24.0.34.30", {"start": v(144.02, -186.44) * mm, "end": v(149.1, -186.44) * mm});
            skLineSegment(sketch, "E24.0.34.31", {"start": v(111.76, -181.36) * mm, "end": v(106.68, -181.36) * mm});
            skLineSegment(sketch, "E24.0.35.0", {"start": v(133.1, -186.7) * mm, "end": v(128.02, -186.7) * mm});
            skLineSegment(sketch, "E24.0.35.1", {"start": v(106.68, -186.7) * mm, "end": v(106.68, -191.77) * mm});
            skLineSegment(sketch, "E24.0.35.2", {"start": v(133.1, -191.77) * mm, "end": v(133.1, -186.7) * mm});
            skLineSegment(sketch, "E24.0.35.3", {"start": v(106.68, -191.77) * mm, "end": v(111.76, -191.77) * mm});
            skLineSegment(sketch, "E24.0.35.4", {"start": v(117.1, -191.77) * mm, "end": v(117.1, -186.7) * mm});
            skLineSegment(sketch, "E24.0.35.5", {"start": v(117.1, -186.7) * mm, "end": v(112.01, -186.7) * mm});
            skLineSegment(sketch, "E24.0.35.6", {"start": v(149.1, -191.77) * mm, "end": v(149.1, -186.7) * mm});
            skLineSegment(sketch, "E24.0.35.7", {"start": v(138.68, -191.77) * mm, "end": v(143.76, -191.77) * mm});
            skLineSegment(sketch, "E24.0.35.8", {"start": v(112.01, -186.7) * mm, "end": v(112.01, -191.77) * mm});
            skLineSegment(sketch, "E24.0.35.9", {"start": v(138.68, -186.7) * mm, "end": v(138.68, -191.77) * mm});
            skLineSegment(sketch, "E24.0.35.10", {"start": v(112.01, -191.77) * mm, "end": v(117.1, -191.77) * mm});
            skLineSegment(sketch, "E24.0.35.11", {"start": v(143.76, -186.7) * mm, "end": v(138.68, -186.7) * mm});
            skLineSegment(sketch, "E24.0.35.12", {"start": v(122.43, -191.77) * mm, "end": v(122.43, -186.7) * mm});
            skLineSegment(sketch, "E24.0.35.13", {"start": v(143.76, -191.77) * mm, "end": v(143.76, -186.7) * mm});
            skLineSegment(sketch, "E24.0.35.14", {"start": v(122.68, -191.77) * mm, "end": v(127.76, -191.77) * mm});
            skLineSegment(sketch, "E24.0.35.15", {"start": v(122.43, -186.7) * mm, "end": v(117.35, -186.7) * mm});
            skLineSegment(sketch, "E24.0.35.16", {"start": v(133.35, -191.77) * mm, "end": v(138.43, -191.77) * mm});
            skLineSegment(sketch, "E24.0.35.17", {"start": v(127.76, -186.7) * mm, "end": v(122.68, -186.7) * mm});
            skLineSegment(sketch, "E24.0.35.18", {"start": v(117.35, -186.7) * mm, "end": v(117.35, -191.77) * mm});
            skLineSegment(sketch, "E24.0.35.19", {"start": v(133.35, -186.7) * mm, "end": v(133.35, -191.77) * mm});
            skLineSegment(sketch, "E24.0.35.20", {"start": v(122.68, -186.7) * mm, "end": v(122.68, -191.77) * mm});
            skLineSegment(sketch, "E24.0.35.21", {"start": v(117.35, -191.77) * mm, "end": v(122.43, -191.77) * mm});
            skLineSegment(sketch, "E24.0.35.22", {"start": v(138.43, -186.7) * mm, "end": v(133.35, -186.7) * mm});
            skLineSegment(sketch, "E24.0.35.23", {"start": v(127.76, -191.77) * mm, "end": v(127.76, -186.7) * mm});
            skLineSegment(sketch, "E24.0.35.24", {"start": v(138.43, -191.77) * mm, "end": v(138.43, -186.7) * mm});
            skLineSegment(sketch, "E24.0.35.25", {"start": v(144.02, -186.7) * mm, "end": v(144.02, -191.77) * mm});
            skLineSegment(sketch, "E24.0.35.26", {"start": v(128.02, -191.77) * mm, "end": v(133.1, -191.77) * mm});
            skLineSegment(sketch, "E24.0.35.27", {"start": v(111.76, -191.77) * mm, "end": v(111.76, -186.7) * mm});
            skLineSegment(sketch, "E24.0.35.28", {"start": v(149.1, -186.7) * mm, "end": v(144.02, -186.7) * mm});
            skLineSegment(sketch, "E24.0.35.29", {"start": v(128.02, -186.7) * mm, "end": v(128.02, -191.77) * mm});
            skLineSegment(sketch, "E24.0.35.30", {"start": v(144.02, -191.77) * mm, "end": v(149.1, -191.77) * mm});
            skLineSegment(sketch, "E24.0.35.31", {"start": v(111.76, -186.7) * mm, "end": v(106.68, -186.7) * mm});
            skLineSegment(sketch, "E24.0.36.0", {"start": v(133.1, -192.02) * mm, "end": v(128.02, -192.02) * mm});
            skLineSegment(sketch, "E24.0.36.1", {"start": v(106.68, -192.02) * mm, "end": v(106.68, -197.1) * mm});
            skLineSegment(sketch, "E24.0.36.2", {"start": v(133.1, -197.1) * mm, "end": v(133.1, -192.02) * mm});
            skLineSegment(sketch, "E24.0.36.3", {"start": v(106.68, -197.1) * mm, "end": v(111.76, -197.1) * mm});
            skLineSegment(sketch, "E24.0.36.4", {"start": v(117.1, -197.1) * mm, "end": v(117.1, -192.02) * mm});
            skLineSegment(sketch, "E24.0.36.5", {"start": v(117.1, -192.02) * mm, "end": v(112.01, -192.02) * mm});
            skLineSegment(sketch, "E24.0.36.6", {"start": v(149.1, -197.1) * mm, "end": v(149.1, -192.02) * mm});
            skLineSegment(sketch, "E24.0.36.7", {"start": v(138.68, -197.1) * mm, "end": v(143.76, -197.1) * mm});
            skLineSegment(sketch, "E24.0.36.8", {"start": v(112.01, -192.02) * mm, "end": v(112.01, -197.1) * mm});
            skLineSegment(sketch, "E24.0.36.9", {"start": v(138.68, -192.02) * mm, "end": v(138.68, -197.1) * mm});
            skLineSegment(sketch, "E24.0.36.10", {"start": v(112.01, -197.1) * mm, "end": v(117.1, -197.1) * mm});
            skLineSegment(sketch, "E24.0.36.11", {"start": v(143.76, -192.02) * mm, "end": v(138.68, -192.02) * mm});
            skLineSegment(sketch, "E24.0.36.12", {"start": v(122.43, -197.1) * mm, "end": v(122.43, -192.02) * mm});
            skLineSegment(sketch, "E24.0.36.13", {"start": v(143.76, -197.1) * mm, "end": v(143.76, -192.02) * mm});
            skLineSegment(sketch, "E24.0.36.14", {"start": v(122.68, -197.1) * mm, "end": v(127.76, -197.1) * mm});
            skLineSegment(sketch, "E24.0.36.15", {"start": v(122.43, -192.02) * mm, "end": v(117.35, -192.02) * mm});
            skLineSegment(sketch, "E24.0.36.16", {"start": v(133.35, -197.1) * mm, "end": v(138.43, -197.1) * mm});
            skLineSegment(sketch, "E24.0.36.17", {"start": v(127.76, -192.02) * mm, "end": v(122.68, -192.02) * mm});
            skLineSegment(sketch, "E24.0.36.18", {"start": v(117.35, -192.02) * mm, "end": v(117.35, -197.1) * mm});
            skLineSegment(sketch, "E24.0.36.19", {"start": v(133.35, -192.02) * mm, "end": v(133.35, -197.1) * mm});
            skLineSegment(sketch, "E24.0.36.20", {"start": v(122.68, -192.02) * mm, "end": v(122.68, -197.1) * mm});
            skLineSegment(sketch, "E24.0.36.21", {"start": v(117.35, -197.1) * mm, "end": v(122.43, -197.1) * mm});
            skLineSegment(sketch, "E24.0.36.22", {"start": v(138.43, -192.02) * mm, "end": v(133.35, -192.02) * mm});
            skLineSegment(sketch, "E24.0.36.23", {"start": v(127.76, -197.1) * mm, "end": v(127.76, -192.02) * mm});
            skLineSegment(sketch, "E24.0.36.24", {"start": v(138.43, -197.1) * mm, "end": v(138.43, -192.02) * mm});
            skLineSegment(sketch, "E24.0.36.25", {"start": v(144.02, -192.02) * mm, "end": v(144.02, -197.1) * mm});
            skLineSegment(sketch, "E24.0.36.26", {"start": v(128.02, -197.1) * mm, "end": v(133.1, -197.1) * mm});
            skLineSegment(sketch, "E24.0.36.27", {"start": v(111.76, -197.1) * mm, "end": v(111.76, -192.02) * mm});
            skLineSegment(sketch, "E24.0.36.28", {"start": v(149.1, -192.02) * mm, "end": v(144.02, -192.02) * mm});
            skLineSegment(sketch, "E24.0.36.29", {"start": v(128.02, -192.02) * mm, "end": v(128.02, -197.1) * mm});
            skLineSegment(sketch, "E24.0.36.30", {"start": v(144.02, -197.1) * mm, "end": v(149.1, -197.1) * mm});
            skLineSegment(sketch, "E24.0.36.31", {"start": v(111.76, -192.02) * mm, "end": v(106.68, -192.02) * mm});
            skLineSegment(sketch, "E24.direction1", {"start": v(106.68, -5.08) * mm, "end": v(132.08, -5.08) * mm, "construction": true});
            skLineSegment(sketch, "E24.direction2", {"start": v(106.68, -5.08) * mm, "end": v(106.68, -10.41) * mm, "construction": true});
            skSolve(sketch);
        }
        {
            var Q0;
            Q0=qCreatedBy(makeId("Top.planeOp"),FACE);
            var sketch = newSketch(context, id + "F8", { "sketchPlane" : qUnion([Q0])});
            skLineSegment(sketch, "E25.0.0", {"start": v(154.43, -5.08) * mm, "end": v(154.43, 0) * mm});
            skLineSegment(sketch, "E25.0.1", {"start": v(154.43, 0) * mm, "end": v(149.35, 0) * mm});
            skLineSegment(sketch, "E25.0.2", {"start": v(149.35, 0) * mm, "end": v(149.35, -5.08) * mm});
            skLineSegment(sketch, "E25.0.3", {"start": v(149.35, -5.08) * mm, "end": v(154.43, -5.08) * mm});
            skLineSegment(sketch, "E25.1.0", {"start": v(159.77, -5.08) * mm, "end": v(159.77, 0) * mm});
            skLineSegment(sketch, "E25.1.1", {"start": v(159.77, 0) * mm, "end": v(154.69, 0) * mm});
            skLineSegment(sketch, "E25.1.2", {"start": v(154.69, 0) * mm, "end": v(154.69, -5.08) * mm});
            skLineSegment(sketch, "E25.1.3", {"start": v(154.69, -5.08) * mm, "end": v(159.77, -5.08) * mm});
            skLineSegment(sketch, "E25.2.0", {"start": v(165.1, -5.08) * mm, "end": v(165.1, 0) * mm});
            skLineSegment(sketch, "E25.2.1", {"start": v(165.1, 0) * mm, "end": v(160.02, 0) * mm});
            skLineSegment(sketch, "E25.2.2", {"start": v(160.02, 0) * mm, "end": v(160.02, -5.08) * mm});
            skLineSegment(sketch, "E25.2.3", {"start": v(160.02, -5.08) * mm, "end": v(165.1, -5.08) * mm});
            skLineSegment(sketch, "E25.3.0", {"start": v(170.43, -5.08) * mm, "end": v(170.43, 0) * mm});
            skLineSegment(sketch, "E25.3.1", {"start": v(170.43, 0) * mm, "end": v(165.35, 0) * mm});
            skLineSegment(sketch, "E25.3.2", {"start": v(165.35, 0) * mm, "end": v(165.35, -5.08) * mm});
            skLineSegment(sketch, "E25.3.3", {"start": v(165.35, -5.08) * mm, "end": v(170.43, -5.08) * mm});
            skLineSegment(sketch, "E25.4.0", {"start": v(175.77, -5.08) * mm, "end": v(175.77, 0) * mm});
            skLineSegment(sketch, "E25.4.1", {"start": v(175.77, 0) * mm, "end": v(170.69, 0) * mm});
            skLineSegment(sketch, "E25.4.2", {"start": v(170.69, 0) * mm, "end": v(170.69, -5.08) * mm});
            skLineSegment(sketch, "E25.4.3", {"start": v(170.69, -5.08) * mm, "end": v(175.77, -5.08) * mm});
            skLineSegment(sketch, "E25.5.0", {"start": v(181.1, -5.08) * mm, "end": v(181.1, 0) * mm});
            skLineSegment(sketch, "E25.5.1", {"start": v(181.1, 0) * mm, "end": v(176.02, 0) * mm});
            skLineSegment(sketch, "E25.5.2", {"start": v(176.02, 0) * mm, "end": v(176.02, -5.08) * mm});
            skLineSegment(sketch, "E25.5.3", {"start": v(176.02, -5.08) * mm, "end": v(181.1, -5.08) * mm});
            skLineSegment(sketch, "E26.0.1.0", {"start": v(149.35, -5.33) * mm, "end": v(149.35, -10.41) * mm});
            skLineSegment(sketch, "E26.0.1.1", {"start": v(170.69, -5.33) * mm, "end": v(170.69, -10.41) * mm});
            skLineSegment(sketch, "E26.0.1.2", {"start": v(149.35, -10.41) * mm, "end": v(154.43, -10.41) * mm});
            skLineSegment(sketch, "E26.0.1.3", {"start": v(175.77, -5.33) * mm, "end": v(170.69, -5.33) * mm});
            skLineSegment(sketch, "E26.0.1.4", {"start": v(159.77, -10.41) * mm, "end": v(159.77, -5.33) * mm});
            skLineSegment(sketch, "E26.0.1.5", {"start": v(159.77, -5.33) * mm, "end": v(154.69, -5.33) * mm});
            skLineSegment(sketch, "E26.0.1.6", {"start": v(154.69, -5.33) * mm, "end": v(154.69, -10.41) * mm});
            skLineSegment(sketch, "E26.0.1.7", {"start": v(154.69, -10.41) * mm, "end": v(159.77, -10.41) * mm});
            skLineSegment(sketch, "E26.0.1.8", {"start": v(165.1, -10.41) * mm, "end": v(165.1, -5.33) * mm});
            skLineSegment(sketch, "E26.0.1.9", {"start": v(165.35, -10.41) * mm, "end": v(170.43, -10.41) * mm});
            skLineSegment(sketch, "E26.0.1.10", {"start": v(165.1, -5.33) * mm, "end": v(160.02, -5.33) * mm});
            skLineSegment(sketch, "E26.0.1.11", {"start": v(176.02, -10.41) * mm, "end": v(181.1, -10.41) * mm});
            skLineSegment(sketch, "E26.0.1.12", {"start": v(170.43, -5.33) * mm, "end": v(165.35, -5.33) * mm});
            skLineSegment(sketch, "E26.0.1.13", {"start": v(160.02, -5.33) * mm, "end": v(160.02, -10.41) * mm});
            skLineSegment(sketch, "E26.0.1.14", {"start": v(176.02, -5.33) * mm, "end": v(176.02, -10.41) * mm});
            skLineSegment(sketch, "E26.0.1.15", {"start": v(165.35, -5.33) * mm, "end": v(165.35, -10.41) * mm});
            skLineSegment(sketch, "E26.0.1.16", {"start": v(160.02, -10.41) * mm, "end": v(165.1, -10.41) * mm});
            skLineSegment(sketch, "E26.0.1.17", {"start": v(170.43, -10.41) * mm, "end": v(170.43, -5.33) * mm});
            skLineSegment(sketch, "E26.0.1.18", {"start": v(181.1, -5.33) * mm, "end": v(176.02, -5.33) * mm});
            skLineSegment(sketch, "E26.0.1.19", {"start": v(154.43, -10.41) * mm, "end": v(154.43, -5.33) * mm});
            skLineSegment(sketch, "E26.0.1.20", {"start": v(181.1, -10.41) * mm, "end": v(181.1, -5.33) * mm});
            skLineSegment(sketch, "E26.0.1.21", {"start": v(154.43, -5.33) * mm, "end": v(149.35, -5.33) * mm});
            skLineSegment(sketch, "E26.0.1.22", {"start": v(170.69, -10.41) * mm, "end": v(175.77, -10.41) * mm});
            skLineSegment(sketch, "E26.0.1.23", {"start": v(175.77, -10.41) * mm, "end": v(175.77, -5.33) * mm});
            skLineSegment(sketch, "E26.0.2.0", {"start": v(149.35, -10.67) * mm, "end": v(149.35, -15.75) * mm});
            skLineSegment(sketch, "E26.0.2.1", {"start": v(170.69, -10.67) * mm, "end": v(170.69, -15.75) * mm});
            skLineSegment(sketch, "E26.0.2.2", {"start": v(149.35, -15.75) * mm, "end": v(154.43, -15.75) * mm});
            skLineSegment(sketch, "E26.0.2.3", {"start": v(175.77, -10.67) * mm, "end": v(170.69, -10.67) * mm});
            skLineSegment(sketch, "E26.0.2.4", {"start": v(159.77, -15.75) * mm, "end": v(159.77, -10.67) * mm});
            skLineSegment(sketch, "E26.0.2.5", {"start": v(159.77, -10.67) * mm, "end": v(154.69, -10.67) * mm});
            skLineSegment(sketch, "E26.0.2.6", {"start": v(154.69, -10.67) * mm, "end": v(154.69, -15.75) * mm});
            skLineSegment(sketch, "E26.0.2.7", {"start": v(154.69, -15.75) * mm, "end": v(159.77, -15.75) * mm});
            skLineSegment(sketch, "E26.0.2.8", {"start": v(165.1, -15.75) * mm, "end": v(165.1, -10.67) * mm});
            skLineSegment(sketch, "E26.0.2.9", {"start": v(165.35, -15.75) * mm, "end": v(170.43, -15.75) * mm});
            skLineSegment(sketch, "E26.0.2.10", {"start": v(165.1, -10.67) * mm, "end": v(160.02, -10.67) * mm});
            skLineSegment(sketch, "E26.0.2.11", {"start": v(176.02, -15.75) * mm, "end": v(181.1, -15.75) * mm});
            skLineSegment(sketch, "E26.0.2.12", {"start": v(170.43, -10.67) * mm, "end": v(165.35, -10.67) * mm});
            skLineSegment(sketch, "E26.0.2.13", {"start": v(160.02, -10.67) * mm, "end": v(160.02, -15.75) * mm});
            skLineSegment(sketch, "E26.0.2.14", {"start": v(176.02, -10.67) * mm, "end": v(176.02, -15.75) * mm});
            skLineSegment(sketch, "E26.0.2.15", {"start": v(165.35, -10.67) * mm, "end": v(165.35, -15.75) * mm});
            skLineSegment(sketch, "E26.0.2.16", {"start": v(160.02, -15.75) * mm, "end": v(165.1, -15.75) * mm});
            skLineSegment(sketch, "E26.0.2.17", {"start": v(170.43, -15.75) * mm, "end": v(170.43, -10.67) * mm});
            skLineSegment(sketch, "E26.0.2.18", {"start": v(181.1, -10.67) * mm, "end": v(176.02, -10.67) * mm});
            skLineSegment(sketch, "E26.0.2.19", {"start": v(154.43, -15.75) * mm, "end": v(154.43, -10.67) * mm});
            skLineSegment(sketch, "E26.0.2.20", {"start": v(181.1, -15.75) * mm, "end": v(181.1, -10.67) * mm});
            skLineSegment(sketch, "E26.0.2.21", {"start": v(154.43, -10.67) * mm, "end": v(149.35, -10.67) * mm});
            skLineSegment(sketch, "E26.0.2.22", {"start": v(170.69, -15.75) * mm, "end": v(175.77, -15.75) * mm});
            skLineSegment(sketch, "E26.0.2.23", {"start": v(175.77, -15.75) * mm, "end": v(175.77, -10.67) * mm});
            skLineSegment(sketch, "E26.0.3.0", {"start": v(149.35, -16) * mm, "end": v(149.35, -21.08) * mm});
            skLineSegment(sketch, "E26.0.3.1", {"start": v(170.69, -16) * mm, "end": v(170.69, -21.08) * mm});
            skLineSegment(sketch, "E26.0.3.2", {"start": v(149.35, -21.08) * mm, "end": v(154.43, -21.08) * mm});
            skLineSegment(sketch, "E26.0.3.3", {"start": v(175.77, -16) * mm, "end": v(170.69, -16) * mm});
            skLineSegment(sketch, "E26.0.3.4", {"start": v(159.77, -21.08) * mm, "end": v(159.77, -16) * mm});
            skLineSegment(sketch, "E26.0.3.5", {"start": v(159.77, -16) * mm, "end": v(154.69, -16) * mm});
            skLineSegment(sketch, "E26.0.3.6", {"start": v(154.69, -16) * mm, "end": v(154.69, -21.08) * mm});
            skLineSegment(sketch, "E26.0.3.7", {"start": v(154.69, -21.08) * mm, "end": v(159.77, -21.08) * mm});
            skLineSegment(sketch, "E26.0.3.8", {"start": v(165.1, -21.08) * mm, "end": v(165.1, -16) * mm});
            skLineSegment(sketch, "E26.0.3.9", {"start": v(165.35, -21.08) * mm, "end": v(170.43, -21.08) * mm});
            skLineSegment(sketch, "E26.0.3.10", {"start": v(165.1, -16) * mm, "end": v(160.02, -16) * mm});
            skLineSegment(sketch, "E26.0.3.11", {"start": v(176.02, -21.08) * mm, "end": v(181.1, -21.08) * mm});
            skLineSegment(sketch, "E26.0.3.12", {"start": v(170.43, -16) * mm, "end": v(165.35, -16) * mm});
            skLineSegment(sketch, "E26.0.3.13", {"start": v(160.02, -16) * mm, "end": v(160.02, -21.08) * mm});
            skLineSegment(sketch, "E26.0.3.14", {"start": v(176.02, -16) * mm, "end": v(176.02, -21.08) * mm});
            skLineSegment(sketch, "E26.0.3.15", {"start": v(165.35, -16) * mm, "end": v(165.35, -21.08) * mm});
            skLineSegment(sketch, "E26.0.3.16", {"start": v(160.02, -21.08) * mm, "end": v(165.1, -21.08) * mm});
            skLineSegment(sketch, "E26.0.3.17", {"start": v(170.43, -21.08) * mm, "end": v(170.43, -16) * mm});
            skLineSegment(sketch, "E26.0.3.18", {"start": v(181.1, -16) * mm, "end": v(176.02, -16) * mm});
            skLineSegment(sketch, "E26.0.3.19", {"start": v(154.43, -21.08) * mm, "end": v(154.43, -16) * mm});
            skLineSegment(sketch, "E26.0.3.20", {"start": v(181.1, -21.08) * mm, "end": v(181.1, -16) * mm});
            skLineSegment(sketch, "E26.0.3.21", {"start": v(154.43, -16) * mm, "end": v(149.35, -16) * mm});
            skLineSegment(sketch, "E26.0.3.22", {"start": v(170.69, -21.08) * mm, "end": v(175.77, -21.08) * mm});
            skLineSegment(sketch, "E26.0.3.23", {"start": v(175.77, -21.08) * mm, "end": v(175.77, -16) * mm});
            skLineSegment(sketch, "E26.0.4.0", {"start": v(149.35, -21.34) * mm, "end": v(149.35, -26.42) * mm});
            skLineSegment(sketch, "E26.0.4.1", {"start": v(170.69, -21.34) * mm, "end": v(170.69, -26.42) * mm});
            skLineSegment(sketch, "E26.0.4.2", {"start": v(149.35, -26.42) * mm, "end": v(154.43, -26.42) * mm});
            skLineSegment(sketch, "E26.0.4.3", {"start": v(175.77, -21.34) * mm, "end": v(170.69, -21.34) * mm});
            skLineSegment(sketch, "E26.0.4.4", {"start": v(159.77, -26.42) * mm, "end": v(159.77, -21.34) * mm});
            skLineSegment(sketch, "E26.0.4.5", {"start": v(159.77, -21.34) * mm, "end": v(154.69, -21.34) * mm});
            skLineSegment(sketch, "E26.0.4.6", {"start": v(154.69, -21.34) * mm, "end": v(154.69, -26.42) * mm});
            skLineSegment(sketch, "E26.0.4.7", {"start": v(154.69, -26.42) * mm, "end": v(159.77, -26.42) * mm});
            skLineSegment(sketch, "E26.0.4.8", {"start": v(165.1, -26.42) * mm, "end": v(165.1, -21.34) * mm});
            skLineSegment(sketch, "E26.0.4.9", {"start": v(165.35, -26.42) * mm, "end": v(170.43, -26.42) * mm});
            skLineSegment(sketch, "E26.0.4.10", {"start": v(165.1, -21.34) * mm, "end": v(160.02, -21.34) * mm});
            skLineSegment(sketch, "E26.0.4.11", {"start": v(176.02, -26.42) * mm, "end": v(181.1, -26.42) * mm});
            skLineSegment(sketch, "E26.0.4.12", {"start": v(170.43, -21.34) * mm, "end": v(165.35, -21.34) * mm});
            skLineSegment(sketch, "E26.0.4.13", {"start": v(160.02, -21.34) * mm, "end": v(160.02, -26.42) * mm});
            skLineSegment(sketch, "E26.0.4.14", {"start": v(176.02, -21.34) * mm, "end": v(176.02, -26.42) * mm});
            skLineSegment(sketch, "E26.0.4.15", {"start": v(165.35, -21.34) * mm, "end": v(165.35, -26.42) * mm});
            skLineSegment(sketch, "E26.0.4.16", {"start": v(160.02, -26.42) * mm, "end": v(165.1, -26.42) * mm});
            skLineSegment(sketch, "E26.0.4.17", {"start": v(170.43, -26.42) * mm, "end": v(170.43, -21.34) * mm});
            skLineSegment(sketch, "E26.0.4.18", {"start": v(181.1, -21.34) * mm, "end": v(176.02, -21.34) * mm});
            skLineSegment(sketch, "E26.0.4.19", {"start": v(154.43, -26.42) * mm, "end": v(154.43, -21.34) * mm});
            skLineSegment(sketch, "E26.0.4.20", {"start": v(181.1, -26.42) * mm, "end": v(181.1, -21.34) * mm});
            skLineSegment(sketch, "E26.0.4.21", {"start": v(154.43, -21.34) * mm, "end": v(149.35, -21.34) * mm});
            skLineSegment(sketch, "E26.0.4.22", {"start": v(170.69, -26.42) * mm, "end": v(175.77, -26.42) * mm});
            skLineSegment(sketch, "E26.0.4.23", {"start": v(175.77, -26.42) * mm, "end": v(175.77, -21.34) * mm});
            skLineSegment(sketch, "E26.0.5.0", {"start": v(149.35, -26.67) * mm, "end": v(149.35, -31.75) * mm});
            skLineSegment(sketch, "E26.0.5.1", {"start": v(170.69, -26.67) * mm, "end": v(170.69, -31.75) * mm});
            skLineSegment(sketch, "E26.0.5.2", {"start": v(149.35, -31.75) * mm, "end": v(154.43, -31.75) * mm});
            skLineSegment(sketch, "E26.0.5.3", {"start": v(175.77, -26.67) * mm, "end": v(170.69, -26.67) * mm});
            skLineSegment(sketch, "E26.0.5.4", {"start": v(159.77, -31.75) * mm, "end": v(159.77, -26.67) * mm});
            skLineSegment(sketch, "E26.0.5.5", {"start": v(159.77, -26.67) * mm, "end": v(154.69, -26.67) * mm});
            skLineSegment(sketch, "E26.0.5.6", {"start": v(154.69, -26.67) * mm, "end": v(154.69, -31.75) * mm});
            skLineSegment(sketch, "E26.0.5.7", {"start": v(154.69, -31.75) * mm, "end": v(159.77, -31.75) * mm});
            skLineSegment(sketch, "E26.0.5.8", {"start": v(165.1, -31.75) * mm, "end": v(165.1, -26.67) * mm});
            skLineSegment(sketch, "E26.0.5.9", {"start": v(165.35, -31.75) * mm, "end": v(170.43, -31.75) * mm});
            skLineSegment(sketch, "E26.0.5.10", {"start": v(165.1, -26.67) * mm, "end": v(160.02, -26.67) * mm});
            skLineSegment(sketch, "E26.0.5.11", {"start": v(176.02, -31.75) * mm, "end": v(181.1, -31.75) * mm});
            skLineSegment(sketch, "E26.0.5.12", {"start": v(170.43, -26.67) * mm, "end": v(165.35, -26.67) * mm});
            skLineSegment(sketch, "E26.0.5.13", {"start": v(160.02, -26.67) * mm, "end": v(160.02, -31.75) * mm});
            skLineSegment(sketch, "E26.0.5.14", {"start": v(176.02, -26.67) * mm, "end": v(176.02, -31.75) * mm});
            skLineSegment(sketch, "E26.0.5.15", {"start": v(165.35, -26.67) * mm, "end": v(165.35, -31.75) * mm});
            skLineSegment(sketch, "E26.0.5.16", {"start": v(160.02, -31.75) * mm, "end": v(165.1, -31.75) * mm});
            skLineSegment(sketch, "E26.0.5.17", {"start": v(170.43, -31.75) * mm, "end": v(170.43, -26.67) * mm});
            skLineSegment(sketch, "E26.0.5.18", {"start": v(181.1, -26.67) * mm, "end": v(176.02, -26.67) * mm});
            skLineSegment(sketch, "E26.0.5.19", {"start": v(154.43, -31.75) * mm, "end": v(154.43, -26.67) * mm});
            skLineSegment(sketch, "E26.0.5.20", {"start": v(181.1, -31.75) * mm, "end": v(181.1, -26.67) * mm});
            skLineSegment(sketch, "E26.0.5.21", {"start": v(154.43, -26.67) * mm, "end": v(149.35, -26.67) * mm});
            skLineSegment(sketch, "E26.0.5.22", {"start": v(170.69, -31.75) * mm, "end": v(175.77, -31.75) * mm});
            skLineSegment(sketch, "E26.0.5.23", {"start": v(175.77, -31.75) * mm, "end": v(175.77, -26.67) * mm});
            skLineSegment(sketch, "E26.0.6.0", {"start": v(149.35, -32) * mm, "end": v(149.35, -37.08) * mm});
            skLineSegment(sketch, "E26.0.6.1", {"start": v(170.69, -32) * mm, "end": v(170.69, -37.08) * mm});
            skLineSegment(sketch, "E26.0.6.2", {"start": v(149.35, -37.08) * mm, "end": v(154.43, -37.08) * mm});
            skLineSegment(sketch, "E26.0.6.3", {"start": v(175.77, -32) * mm, "end": v(170.69, -32) * mm});
            skLineSegment(sketch, "E26.0.6.4", {"start": v(159.77, -37.08) * mm, "end": v(159.77, -32) * mm});
            skLineSegment(sketch, "E26.0.6.5", {"start": v(159.77, -32) * mm, "end": v(154.69, -32) * mm});
            skLineSegment(sketch, "E26.0.6.6", {"start": v(154.69, -32) * mm, "end": v(154.69, -37.08) * mm});
            skLineSegment(sketch, "E26.0.6.7", {"start": v(154.69, -37.08) * mm, "end": v(159.77, -37.08) * mm});
            skLineSegment(sketch, "E26.0.6.8", {"start": v(165.1, -37.08) * mm, "end": v(165.1, -32) * mm});
            skLineSegment(sketch, "E26.0.6.9", {"start": v(165.35, -37.08) * mm, "end": v(170.43, -37.08) * mm});
            skLineSegment(sketch, "E26.0.6.10", {"start": v(165.1, -32) * mm, "end": v(160.02, -32) * mm});
            skLineSegment(sketch, "E26.0.6.11", {"start": v(176.02, -37.08) * mm, "end": v(181.1, -37.08) * mm});
            skLineSegment(sketch, "E26.0.6.12", {"start": v(170.43, -32) * mm, "end": v(165.35, -32) * mm});
            skLineSegment(sketch, "E26.0.6.13", {"start": v(160.02, -32) * mm, "end": v(160.02, -37.08) * mm});
            skLineSegment(sketch, "E26.0.6.14", {"start": v(176.02, -32) * mm, "end": v(176.02, -37.08) * mm});
            skLineSegment(sketch, "E26.0.6.15", {"start": v(165.35, -32) * mm, "end": v(165.35, -37.08) * mm});
            skLineSegment(sketch, "E26.0.6.16", {"start": v(160.02, -37.08) * mm, "end": v(165.1, -37.08) * mm});
            skLineSegment(sketch, "E26.0.6.17", {"start": v(170.43, -37.08) * mm, "end": v(170.43, -32) * mm});
            skLineSegment(sketch, "E26.0.6.18", {"start": v(181.1, -32) * mm, "end": v(176.02, -32) * mm});
            skLineSegment(sketch, "E26.0.6.19", {"start": v(154.43, -37.08) * mm, "end": v(154.43, -32) * mm});
            skLineSegment(sketch, "E26.0.6.20", {"start": v(181.1, -37.08) * mm, "end": v(181.1, -32) * mm});
            skLineSegment(sketch, "E26.0.6.21", {"start": v(154.43, -32) * mm, "end": v(149.35, -32) * mm});
            skLineSegment(sketch, "E26.0.6.22", {"start": v(170.69, -37.08) * mm, "end": v(175.77, -37.08) * mm});
            skLineSegment(sketch, "E26.0.6.23", {"start": v(175.77, -37.08) * mm, "end": v(175.77, -32) * mm});
            skLineSegment(sketch, "E26.0.7.0", {"start": v(149.35, -37.34) * mm, "end": v(149.35, -42.42) * mm});
            skLineSegment(sketch, "E26.0.7.1", {"start": v(170.69, -37.34) * mm, "end": v(170.69, -42.42) * mm});
            skLineSegment(sketch, "E26.0.7.2", {"start": v(149.35, -42.42) * mm, "end": v(154.43, -42.42) * mm});
            skLineSegment(sketch, "E26.0.7.3", {"start": v(175.77, -37.34) * mm, "end": v(170.69, -37.34) * mm});
            skLineSegment(sketch, "E26.0.7.4", {"start": v(159.77, -42.42) * mm, "end": v(159.77, -37.34) * mm});
            skLineSegment(sketch, "E26.0.7.5", {"start": v(159.77, -37.34) * mm, "end": v(154.69, -37.34) * mm});
            skLineSegment(sketch, "E26.0.7.6", {"start": v(154.69, -37.34) * mm, "end": v(154.69, -42.42) * mm});
            skLineSegment(sketch, "E26.0.7.7", {"start": v(154.69, -42.42) * mm, "end": v(159.77, -42.42) * mm});
            skLineSegment(sketch, "E26.0.7.8", {"start": v(165.1, -42.42) * mm, "end": v(165.1, -37.34) * mm});
            skLineSegment(sketch, "E26.0.7.9", {"start": v(165.35, -42.42) * mm, "end": v(170.43, -42.42) * mm});
            skLineSegment(sketch, "E26.0.7.10", {"start": v(165.1, -37.34) * mm, "end": v(160.02, -37.34) * mm});
            skLineSegment(sketch, "E26.0.7.11", {"start": v(176.02, -42.42) * mm, "end": v(181.1, -42.42) * mm});
            skLineSegment(sketch, "E26.0.7.12", {"start": v(170.43, -37.34) * mm, "end": v(165.35, -37.34) * mm});
            skLineSegment(sketch, "E26.0.7.13", {"start": v(160.02, -37.34) * mm, "end": v(160.02, -42.42) * mm});
            skLineSegment(sketch, "E26.0.7.14", {"start": v(176.02, -37.34) * mm, "end": v(176.02, -42.42) * mm});
            skLineSegment(sketch, "E26.0.7.15", {"start": v(165.35, -37.34) * mm, "end": v(165.35, -42.42) * mm});
            skLineSegment(sketch, "E26.0.7.16", {"start": v(160.02, -42.42) * mm, "end": v(165.1, -42.42) * mm});
            skLineSegment(sketch, "E26.0.7.17", {"start": v(170.43, -42.42) * mm, "end": v(170.43, -37.34) * mm});
            skLineSegment(sketch, "E26.0.7.18", {"start": v(181.1, -37.34) * mm, "end": v(176.02, -37.34) * mm});
            skLineSegment(sketch, "E26.0.7.19", {"start": v(154.43, -42.42) * mm, "end": v(154.43, -37.34) * mm});
            skLineSegment(sketch, "E26.0.7.20", {"start": v(181.1, -42.42) * mm, "end": v(181.1, -37.34) * mm});
            skLineSegment(sketch, "E26.0.7.21", {"start": v(154.43, -37.34) * mm, "end": v(149.35, -37.34) * mm});
            skLineSegment(sketch, "E26.0.7.22", {"start": v(170.69, -42.42) * mm, "end": v(175.77, -42.42) * mm});
            skLineSegment(sketch, "E26.0.7.23", {"start": v(175.77, -42.42) * mm, "end": v(175.77, -37.34) * mm});
            skLineSegment(sketch, "E26.0.8.0", {"start": v(149.35, -42.67) * mm, "end": v(149.35, -47.75) * mm});
            skLineSegment(sketch, "E26.0.8.1", {"start": v(170.69, -42.67) * mm, "end": v(170.69, -47.75) * mm});
            skLineSegment(sketch, "E26.0.8.2", {"start": v(149.35, -47.75) * mm, "end": v(154.43, -47.75) * mm});
            skLineSegment(sketch, "E26.0.8.3", {"start": v(175.77, -42.67) * mm, "end": v(170.69, -42.67) * mm});
            skLineSegment(sketch, "E26.0.8.4", {"start": v(159.77, -47.75) * mm, "end": v(159.77, -42.67) * mm});
            skLineSegment(sketch, "E26.0.8.5", {"start": v(159.77, -42.67) * mm, "end": v(154.69, -42.67) * mm});
            skLineSegment(sketch, "E26.0.8.6", {"start": v(154.69, -42.67) * mm, "end": v(154.69, -47.75) * mm});
            skLineSegment(sketch, "E26.0.8.7", {"start": v(154.69, -47.75) * mm, "end": v(159.77, -47.75) * mm});
            skLineSegment(sketch, "E26.0.8.8", {"start": v(165.1, -47.75) * mm, "end": v(165.1, -42.67) * mm});
            skLineSegment(sketch, "E26.0.8.9", {"start": v(165.35, -47.75) * mm, "end": v(170.43, -47.75) * mm});
            skLineSegment(sketch, "E26.0.8.10", {"start": v(165.1, -42.67) * mm, "end": v(160.02, -42.67) * mm});
            skLineSegment(sketch, "E26.0.8.11", {"start": v(176.02, -47.75) * mm, "end": v(181.1, -47.75) * mm});
            skLineSegment(sketch, "E26.0.8.12", {"start": v(170.43, -42.67) * mm, "end": v(165.35, -42.67) * mm});
            skLineSegment(sketch, "E26.0.8.13", {"start": v(160.02, -42.67) * mm, "end": v(160.02, -47.75) * mm});
            skLineSegment(sketch, "E26.0.8.14", {"start": v(176.02, -42.67) * mm, "end": v(176.02, -47.75) * mm});
            skLineSegment(sketch, "E26.0.8.15", {"start": v(165.35, -42.67) * mm, "end": v(165.35, -47.75) * mm});
            skLineSegment(sketch, "E26.0.8.16", {"start": v(160.02, -47.75) * mm, "end": v(165.1, -47.75) * mm});
            skLineSegment(sketch, "E26.0.8.17", {"start": v(170.43, -47.75) * mm, "end": v(170.43, -42.67) * mm});
            skLineSegment(sketch, "E26.0.8.18", {"start": v(181.1, -42.67) * mm, "end": v(176.02, -42.67) * mm});
            skLineSegment(sketch, "E26.0.8.19", {"start": v(154.43, -47.75) * mm, "end": v(154.43, -42.67) * mm});
            skLineSegment(sketch, "E26.0.8.20", {"start": v(181.1, -47.75) * mm, "end": v(181.1, -42.67) * mm});
            skLineSegment(sketch, "E26.0.8.21", {"start": v(154.43, -42.67) * mm, "end": v(149.35, -42.67) * mm});
            skLineSegment(sketch, "E26.0.8.22", {"start": v(170.69, -47.75) * mm, "end": v(175.77, -47.75) * mm});
            skLineSegment(sketch, "E26.0.8.23", {"start": v(175.77, -47.75) * mm, "end": v(175.77, -42.67) * mm});
            skLineSegment(sketch, "E26.0.9.0", {"start": v(149.35, -48) * mm, "end": v(149.35, -53.09) * mm});
            skLineSegment(sketch, "E26.0.9.1", {"start": v(170.69, -48) * mm, "end": v(170.69, -53.09) * mm});
            skLineSegment(sketch, "E26.0.9.2", {"start": v(149.35, -53.09) * mm, "end": v(154.43, -53.09) * mm});
            skLineSegment(sketch, "E26.0.9.3", {"start": v(175.77, -48) * mm, "end": v(170.69, -48) * mm});
            skLineSegment(sketch, "E26.0.9.4", {"start": v(159.77, -53.09) * mm, "end": v(159.77, -48) * mm});
            skLineSegment(sketch, "E26.0.9.5", {"start": v(159.77, -48) * mm, "end": v(154.69, -48) * mm});
            skLineSegment(sketch, "E26.0.9.6", {"start": v(154.69, -48) * mm, "end": v(154.69, -53.09) * mm});
            skLineSegment(sketch, "E26.0.9.7", {"start": v(154.69, -53.09) * mm, "end": v(159.77, -53.09) * mm});
            skLineSegment(sketch, "E26.0.9.8", {"start": v(165.1, -53.09) * mm, "end": v(165.1, -48) * mm});
            skLineSegment(sketch, "E26.0.9.9", {"start": v(165.35, -53.09) * mm, "end": v(170.43, -53.09) * mm});
            skLineSegment(sketch, "E26.0.9.10", {"start": v(165.1, -48) * mm, "end": v(160.02, -48) * mm});
            skLineSegment(sketch, "E26.0.9.11", {"start": v(176.02, -53.09) * mm, "end": v(181.1, -53.09) * mm});
            skLineSegment(sketch, "E26.0.9.12", {"start": v(170.43, -48) * mm, "end": v(165.35, -48) * mm});
            skLineSegment(sketch, "E26.0.9.13", {"start": v(160.02, -48) * mm, "end": v(160.02, -53.09) * mm});
            skLineSegment(sketch, "E26.0.9.14", {"start": v(176.02, -48) * mm, "end": v(176.02, -53.09) * mm});
            skLineSegment(sketch, "E26.0.9.15", {"start": v(165.35, -48) * mm, "end": v(165.35, -53.09) * mm});
            skLineSegment(sketch, "E26.0.9.16", {"start": v(160.02, -53.09) * mm, "end": v(165.1, -53.09) * mm});
            skLineSegment(sketch, "E26.0.9.17", {"start": v(170.43, -53.09) * mm, "end": v(170.43, -48) * mm});
            skLineSegment(sketch, "E26.0.9.18", {"start": v(181.1, -48) * mm, "end": v(176.02, -48) * mm});
            skLineSegment(sketch, "E26.0.9.19", {"start": v(154.43, -53.09) * mm, "end": v(154.43, -48) * mm});
            skLineSegment(sketch, "E26.0.9.20", {"start": v(181.1, -53.09) * mm, "end": v(181.1, -48) * mm});
            skLineSegment(sketch, "E26.0.9.21", {"start": v(154.43, -48) * mm, "end": v(149.35, -48) * mm});
            skLineSegment(sketch, "E26.0.9.22", {"start": v(170.69, -53.09) * mm, "end": v(175.77, -53.09) * mm});
            skLineSegment(sketch, "E26.0.9.23", {"start": v(175.77, -53.09) * mm, "end": v(175.77, -48) * mm});
            skLineSegment(sketch, "E26.0.10.0", {"start": v(149.35, -53.34) * mm, "end": v(149.35, -58.42) * mm});
            skLineSegment(sketch, "E26.0.10.1", {"start": v(170.69, -53.34) * mm, "end": v(170.69, -58.42) * mm});
            skLineSegment(sketch, "E26.0.10.2", {"start": v(149.35, -58.42) * mm, "end": v(154.43, -58.42) * mm});
            skLineSegment(sketch, "E26.0.10.3", {"start": v(175.77, -53.34) * mm, "end": v(170.69, -53.34) * mm});
            skLineSegment(sketch, "E26.0.10.4", {"start": v(159.77, -58.42) * mm, "end": v(159.77, -53.34) * mm});
            skLineSegment(sketch, "E26.0.10.5", {"start": v(159.77, -53.34) * mm, "end": v(154.69, -53.34) * mm});
            skLineSegment(sketch, "E26.0.10.6", {"start": v(154.69, -53.34) * mm, "end": v(154.69, -58.42) * mm});
            skLineSegment(sketch, "E26.0.10.7", {"start": v(154.69, -58.42) * mm, "end": v(159.77, -58.42) * mm});
            skLineSegment(sketch, "E26.0.10.8", {"start": v(165.1, -58.42) * mm, "end": v(165.1, -53.34) * mm});
            skLineSegment(sketch, "E26.0.10.9", {"start": v(165.35, -58.42) * mm, "end": v(170.43, -58.42) * mm});
            skLineSegment(sketch, "E26.0.10.10", {"start": v(165.1, -53.34) * mm, "end": v(160.02, -53.34) * mm});
            skLineSegment(sketch, "E26.0.10.11", {"start": v(176.02, -58.42) * mm, "end": v(181.1, -58.42) * mm});
            skLineSegment(sketch, "E26.0.10.12", {"start": v(170.43, -53.34) * mm, "end": v(165.35, -53.34) * mm});
            skLineSegment(sketch, "E26.0.10.13", {"start": v(160.02, -53.34) * mm, "end": v(160.02, -58.42) * mm});
            skLineSegment(sketch, "E26.0.10.14", {"start": v(176.02, -53.34) * mm, "end": v(176.02, -58.42) * mm});
            skLineSegment(sketch, "E26.0.10.15", {"start": v(165.35, -53.34) * mm, "end": v(165.35, -58.42) * mm});
            skLineSegment(sketch, "E26.0.10.16", {"start": v(160.02, -58.42) * mm, "end": v(165.1, -58.42) * mm});
            skLineSegment(sketch, "E26.0.10.17", {"start": v(170.43, -58.42) * mm, "end": v(170.43, -53.34) * mm});
            skLineSegment(sketch, "E26.0.10.18", {"start": v(181.1, -53.34) * mm, "end": v(176.02, -53.34) * mm});
            skLineSegment(sketch, "E26.0.10.19", {"start": v(154.43, -58.42) * mm, "end": v(154.43, -53.34) * mm});
            skLineSegment(sketch, "E26.0.10.20", {"start": v(181.1, -58.42) * mm, "end": v(181.1, -53.34) * mm});
            skLineSegment(sketch, "E26.0.10.21", {"start": v(154.43, -53.34) * mm, "end": v(149.35, -53.34) * mm});
            skLineSegment(sketch, "E26.0.10.22", {"start": v(170.69, -58.42) * mm, "end": v(175.77, -58.42) * mm});
            skLineSegment(sketch, "E26.0.10.23", {"start": v(175.77, -58.42) * mm, "end": v(175.77, -53.34) * mm});
            skLineSegment(sketch, "E26.0.11.0", {"start": v(149.35, -58.67) * mm, "end": v(149.35, -63.75) * mm});
            skLineSegment(sketch, "E26.0.11.1", {"start": v(170.69, -58.67) * mm, "end": v(170.69, -63.75) * mm});
            skLineSegment(sketch, "E26.0.11.2", {"start": v(149.35, -63.75) * mm, "end": v(154.43, -63.75) * mm});
            skLineSegment(sketch, "E26.0.11.3", {"start": v(175.77, -58.67) * mm, "end": v(170.69, -58.67) * mm});
            skLineSegment(sketch, "E26.0.11.4", {"start": v(159.77, -63.75) * mm, "end": v(159.77, -58.67) * mm});
            skLineSegment(sketch, "E26.0.11.5", {"start": v(159.77, -58.67) * mm, "end": v(154.69, -58.67) * mm});
            skLineSegment(sketch, "E26.0.11.6", {"start": v(154.69, -58.67) * mm, "end": v(154.69, -63.75) * mm});
            skLineSegment(sketch, "E26.0.11.7", {"start": v(154.69, -63.75) * mm, "end": v(159.77, -63.75) * mm});
            skLineSegment(sketch, "E26.0.11.8", {"start": v(165.1, -63.75) * mm, "end": v(165.1, -58.67) * mm});
            skLineSegment(sketch, "E26.0.11.9", {"start": v(165.35, -63.75) * mm, "end": v(170.43, -63.75) * mm});
            skLineSegment(sketch, "E26.0.11.10", {"start": v(165.1, -58.67) * mm, "end": v(160.02, -58.67) * mm});
            skLineSegment(sketch, "E26.0.11.11", {"start": v(176.02, -63.75) * mm, "end": v(181.1, -63.75) * mm});
            skLineSegment(sketch, "E26.0.11.12", {"start": v(170.43, -58.67) * mm, "end": v(165.35, -58.67) * mm});
            skLineSegment(sketch, "E26.0.11.13", {"start": v(160.02, -58.67) * mm, "end": v(160.02, -63.75) * mm});
            skLineSegment(sketch, "E26.0.11.14", {"start": v(176.02, -58.67) * mm, "end": v(176.02, -63.75) * mm});
            skLineSegment(sketch, "E26.0.11.15", {"start": v(165.35, -58.67) * mm, "end": v(165.35, -63.75) * mm});
            skLineSegment(sketch, "E26.0.11.16", {"start": v(160.02, -63.75) * mm, "end": v(165.1, -63.75) * mm});
            skLineSegment(sketch, "E26.0.11.17", {"start": v(170.43, -63.75) * mm, "end": v(170.43, -58.67) * mm});
            skLineSegment(sketch, "E26.0.11.18", {"start": v(181.1, -58.67) * mm, "end": v(176.02, -58.67) * mm});
            skLineSegment(sketch, "E26.0.11.19", {"start": v(154.43, -63.75) * mm, "end": v(154.43, -58.67) * mm});
            skLineSegment(sketch, "E26.0.11.20", {"start": v(181.1, -63.75) * mm, "end": v(181.1, -58.67) * mm});
            skLineSegment(sketch, "E26.0.11.21", {"start": v(154.43, -58.67) * mm, "end": v(149.35, -58.67) * mm});
            skLineSegment(sketch, "E26.0.11.22", {"start": v(170.69, -63.75) * mm, "end": v(175.77, -63.75) * mm});
            skLineSegment(sketch, "E26.0.11.23", {"start": v(175.77, -63.75) * mm, "end": v(175.77, -58.67) * mm});
            skLineSegment(sketch, "E26.0.12.0", {"start": v(149.35, -64) * mm, "end": v(149.35, -69.09) * mm});
            skLineSegment(sketch, "E26.0.12.1", {"start": v(170.69, -64) * mm, "end": v(170.69, -69.09) * mm});
            skLineSegment(sketch, "E26.0.12.2", {"start": v(149.35, -69.09) * mm, "end": v(154.43, -69.09) * mm});
            skLineSegment(sketch, "E26.0.12.3", {"start": v(175.77, -64) * mm, "end": v(170.69, -64) * mm});
            skLineSegment(sketch, "E26.0.12.4", {"start": v(159.77, -69.09) * mm, "end": v(159.77, -64) * mm});
            skLineSegment(sketch, "E26.0.12.5", {"start": v(159.77, -64) * mm, "end": v(154.69, -64) * mm});
            skLineSegment(sketch, "E26.0.12.6", {"start": v(154.69, -64) * mm, "end": v(154.69, -69.09) * mm});
            skLineSegment(sketch, "E26.0.12.7", {"start": v(154.69, -69.09) * mm, "end": v(159.77, -69.09) * mm});
            skLineSegment(sketch, "E26.0.12.8", {"start": v(165.1, -69.09) * mm, "end": v(165.1, -64) * mm});
            skLineSegment(sketch, "E26.0.12.9", {"start": v(165.35, -69.09) * mm, "end": v(170.43, -69.09) * mm});
            skLineSegment(sketch, "E26.0.12.10", {"start": v(165.1, -64) * mm, "end": v(160.02, -64) * mm});
            skLineSegment(sketch, "E26.0.12.11", {"start": v(176.02, -69.09) * mm, "end": v(181.1, -69.09) * mm});
            skLineSegment(sketch, "E26.0.12.12", {"start": v(170.43, -64) * mm, "end": v(165.35, -64) * mm});
            skLineSegment(sketch, "E26.0.12.13", {"start": v(160.02, -64) * mm, "end": v(160.02, -69.09) * mm});
            skLineSegment(sketch, "E26.0.12.14", {"start": v(176.02, -64) * mm, "end": v(176.02, -69.09) * mm});
            skLineSegment(sketch, "E26.0.12.15", {"start": v(165.35, -64) * mm, "end": v(165.35, -69.09) * mm});
            skLineSegment(sketch, "E26.0.12.16", {"start": v(160.02, -69.09) * mm, "end": v(165.1, -69.09) * mm});
            skLineSegment(sketch, "E26.0.12.17", {"start": v(170.43, -69.09) * mm, "end": v(170.43, -64) * mm});
            skLineSegment(sketch, "E26.0.12.18", {"start": v(181.1, -64) * mm, "end": v(176.02, -64) * mm});
            skLineSegment(sketch, "E26.0.12.19", {"start": v(154.43, -69.09) * mm, "end": v(154.43, -64) * mm});
            skLineSegment(sketch, "E26.0.12.20", {"start": v(181.1, -69.09) * mm, "end": v(181.1, -64) * mm});
            skLineSegment(sketch, "E26.0.12.21", {"start": v(154.43, -64) * mm, "end": v(149.35, -64) * mm});
            skLineSegment(sketch, "E26.0.12.22", {"start": v(170.69, -69.09) * mm, "end": v(175.77, -69.09) * mm});
            skLineSegment(sketch, "E26.0.12.23", {"start": v(175.77, -69.09) * mm, "end": v(175.77, -64) * mm});
            skLineSegment(sketch, "E26.0.13.0", {"start": v(149.35, -69.34) * mm, "end": v(149.35, -74.42) * mm});
            skLineSegment(sketch, "E26.0.13.1", {"start": v(170.69, -69.34) * mm, "end": v(170.69, -74.42) * mm});
            skLineSegment(sketch, "E26.0.13.2", {"start": v(149.35, -74.42) * mm, "end": v(154.43, -74.42) * mm});
            skLineSegment(sketch, "E26.0.13.3", {"start": v(175.77, -69.34) * mm, "end": v(170.69, -69.34) * mm});
            skLineSegment(sketch, "E26.0.13.4", {"start": v(159.77, -74.42) * mm, "end": v(159.77, -69.34) * mm});
            skLineSegment(sketch, "E26.0.13.5", {"start": v(159.77, -69.34) * mm, "end": v(154.69, -69.34) * mm});
            skLineSegment(sketch, "E26.0.13.6", {"start": v(154.69, -69.34) * mm, "end": v(154.69, -74.42) * mm});
            skLineSegment(sketch, "E26.0.13.7", {"start": v(154.69, -74.42) * mm, "end": v(159.77, -74.42) * mm});
            skLineSegment(sketch, "E26.0.13.8", {"start": v(165.1, -74.42) * mm, "end": v(165.1, -69.34) * mm});
            skLineSegment(sketch, "E26.0.13.9", {"start": v(165.35, -74.42) * mm, "end": v(170.43, -74.42) * mm});
            skLineSegment(sketch, "E26.0.13.10", {"start": v(165.1, -69.34) * mm, "end": v(160.02, -69.34) * mm});
            skLineSegment(sketch, "E26.0.13.11", {"start": v(176.02, -74.42) * mm, "end": v(181.1, -74.42) * mm});
            skLineSegment(sketch, "E26.0.13.12", {"start": v(170.43, -69.34) * mm, "end": v(165.35, -69.34) * mm});
            skLineSegment(sketch, "E26.0.13.13", {"start": v(160.02, -69.34) * mm, "end": v(160.02, -74.42) * mm});
            skLineSegment(sketch, "E26.0.13.14", {"start": v(176.02, -69.34) * mm, "end": v(176.02, -74.42) * mm});
            skLineSegment(sketch, "E26.0.13.15", {"start": v(165.35, -69.34) * mm, "end": v(165.35, -74.42) * mm});
            skLineSegment(sketch, "E26.0.13.16", {"start": v(160.02, -74.42) * mm, "end": v(165.1, -74.42) * mm});
            skLineSegment(sketch, "E26.0.13.17", {"start": v(170.43, -74.42) * mm, "end": v(170.43, -69.34) * mm});
            skLineSegment(sketch, "E26.0.13.18", {"start": v(181.1, -69.34) * mm, "end": v(176.02, -69.34) * mm});
            skLineSegment(sketch, "E26.0.13.19", {"start": v(154.43, -74.42) * mm, "end": v(154.43, -69.34) * mm});
            skLineSegment(sketch, "E26.0.13.20", {"start": v(181.1, -74.42) * mm, "end": v(181.1, -69.34) * mm});
            skLineSegment(sketch, "E26.0.13.21", {"start": v(154.43, -69.34) * mm, "end": v(149.35, -69.34) * mm});
            skLineSegment(sketch, "E26.0.13.22", {"start": v(170.69, -74.42) * mm, "end": v(175.77, -74.42) * mm});
            skLineSegment(sketch, "E26.0.13.23", {"start": v(175.77, -74.42) * mm, "end": v(175.77, -69.34) * mm});
            skLineSegment(sketch, "E26.0.14.0", {"start": v(149.35, -74.68) * mm, "end": v(149.35, -79.76) * mm});
            skLineSegment(sketch, "E26.0.14.1", {"start": v(170.69, -74.68) * mm, "end": v(170.69, -79.76) * mm});
            skLineSegment(sketch, "E26.0.14.2", {"start": v(149.35, -79.76) * mm, "end": v(154.43, -79.76) * mm});
            skLineSegment(sketch, "E26.0.14.3", {"start": v(175.77, -74.68) * mm, "end": v(170.69, -74.68) * mm});
            skLineSegment(sketch, "E26.0.14.4", {"start": v(159.77, -79.76) * mm, "end": v(159.77, -74.68) * mm});
            skLineSegment(sketch, "E26.0.14.5", {"start": v(159.77, -74.68) * mm, "end": v(154.69, -74.68) * mm});
            skLineSegment(sketch, "E26.0.14.6", {"start": v(154.69, -74.68) * mm, "end": v(154.69, -79.76) * mm});
            skLineSegment(sketch, "E26.0.14.7", {"start": v(154.69, -79.76) * mm, "end": v(159.77, -79.76) * mm});
            skLineSegment(sketch, "E26.0.14.8", {"start": v(165.1, -79.76) * mm, "end": v(165.1, -74.68) * mm});
            skLineSegment(sketch, "E26.0.14.9", {"start": v(165.35, -79.76) * mm, "end": v(170.43, -79.76) * mm});
            skLineSegment(sketch, "E26.0.14.10", {"start": v(165.1, -74.68) * mm, "end": v(160.02, -74.68) * mm});
            skLineSegment(sketch, "E26.0.14.11", {"start": v(176.02, -79.76) * mm, "end": v(181.1, -79.76) * mm});
            skLineSegment(sketch, "E26.0.14.12", {"start": v(170.43, -74.68) * mm, "end": v(165.35, -74.68) * mm});
            skLineSegment(sketch, "E26.0.14.13", {"start": v(160.02, -74.68) * mm, "end": v(160.02, -79.76) * mm});
            skLineSegment(sketch, "E26.0.14.14", {"start": v(176.02, -74.68) * mm, "end": v(176.02, -79.76) * mm});
            skLineSegment(sketch, "E26.0.14.15", {"start": v(165.35, -74.68) * mm, "end": v(165.35, -79.76) * mm});
            skLineSegment(sketch, "E26.0.14.16", {"start": v(160.02, -79.76) * mm, "end": v(165.1, -79.76) * mm});
            skLineSegment(sketch, "E26.0.14.17", {"start": v(170.43, -79.76) * mm, "end": v(170.43, -74.68) * mm});
            skLineSegment(sketch, "E26.0.14.18", {"start": v(181.1, -74.68) * mm, "end": v(176.02, -74.68) * mm});
            skLineSegment(sketch, "E26.0.14.19", {"start": v(154.43, -79.76) * mm, "end": v(154.43, -74.68) * mm});
            skLineSegment(sketch, "E26.0.14.20", {"start": v(181.1, -79.76) * mm, "end": v(181.1, -74.68) * mm});
            skLineSegment(sketch, "E26.0.14.21", {"start": v(154.43, -74.68) * mm, "end": v(149.35, -74.68) * mm});
            skLineSegment(sketch, "E26.0.14.22", {"start": v(170.69, -79.76) * mm, "end": v(175.77, -79.76) * mm});
            skLineSegment(sketch, "E26.0.14.23", {"start": v(175.77, -79.76) * mm, "end": v(175.77, -74.68) * mm});
            skLineSegment(sketch, "E26.0.15.0", {"start": v(149.35, -80.01) * mm, "end": v(149.35, -85.1) * mm});
            skLineSegment(sketch, "E26.0.15.1", {"start": v(170.69, -80.01) * mm, "end": v(170.69, -85.1) * mm});
            skLineSegment(sketch, "E26.0.15.2", {"start": v(149.35, -85.1) * mm, "end": v(154.43, -85.1) * mm});
            skLineSegment(sketch, "E26.0.15.3", {"start": v(175.77, -80.01) * mm, "end": v(170.69, -80.01) * mm});
            skLineSegment(sketch, "E26.0.15.4", {"start": v(159.77, -85.1) * mm, "end": v(159.77, -80.01) * mm});
            skLineSegment(sketch, "E26.0.15.5", {"start": v(159.77, -80.01) * mm, "end": v(154.69, -80.01) * mm});
            skLineSegment(sketch, "E26.0.15.6", {"start": v(154.69, -80.01) * mm, "end": v(154.69, -85.1) * mm});
            skLineSegment(sketch, "E26.0.15.7", {"start": v(154.69, -85.1) * mm, "end": v(159.77, -85.1) * mm});
            skLineSegment(sketch, "E26.0.15.8", {"start": v(165.1, -85.1) * mm, "end": v(165.1, -80.01) * mm});
            skLineSegment(sketch, "E26.0.15.9", {"start": v(165.35, -85.1) * mm, "end": v(170.43, -85.1) * mm});
            skLineSegment(sketch, "E26.0.15.10", {"start": v(165.1, -80.01) * mm, "end": v(160.02, -80.01) * mm});
            skLineSegment(sketch, "E26.0.15.11", {"start": v(176.02, -85.1) * mm, "end": v(181.1, -85.1) * mm});
            skLineSegment(sketch, "E26.0.15.12", {"start": v(170.43, -80.01) * mm, "end": v(165.35, -80.01) * mm});
            skLineSegment(sketch, "E26.0.15.13", {"start": v(160.02, -80.01) * mm, "end": v(160.02, -85.1) * mm});
            skLineSegment(sketch, "E26.0.15.14", {"start": v(176.02, -80.01) * mm, "end": v(176.02, -85.1) * mm});
            skLineSegment(sketch, "E26.0.15.15", {"start": v(165.35, -80.01) * mm, "end": v(165.35, -85.1) * mm});
            skLineSegment(sketch, "E26.0.15.16", {"start": v(160.02, -85.1) * mm, "end": v(165.1, -85.1) * mm});
            skLineSegment(sketch, "E26.0.15.17", {"start": v(170.43, -85.1) * mm, "end": v(170.43, -80.01) * mm});
            skLineSegment(sketch, "E26.0.15.18", {"start": v(181.1, -80.01) * mm, "end": v(176.02, -80.01) * mm});
            skLineSegment(sketch, "E26.0.15.19", {"start": v(154.43, -85.1) * mm, "end": v(154.43, -80.01) * mm});
            skLineSegment(sketch, "E26.0.15.20", {"start": v(181.1, -85.1) * mm, "end": v(181.1, -80.01) * mm});
            skLineSegment(sketch, "E26.0.15.21", {"start": v(154.43, -80.01) * mm, "end": v(149.35, -80.01) * mm});
            skLineSegment(sketch, "E26.0.15.22", {"start": v(170.69, -85.1) * mm, "end": v(175.77, -85.1) * mm});
            skLineSegment(sketch, "E26.0.15.23", {"start": v(175.77, -85.1) * mm, "end": v(175.77, -80.01) * mm});
            skLineSegment(sketch, "E26.0.16.0", {"start": v(149.35, -85.34) * mm, "end": v(149.35, -90.42) * mm});
            skLineSegment(sketch, "E26.0.16.1", {"start": v(170.69, -85.34) * mm, "end": v(170.69, -90.42) * mm});
            skLineSegment(sketch, "E26.0.16.2", {"start": v(149.35, -90.42) * mm, "end": v(154.43, -90.42) * mm});
            skLineSegment(sketch, "E26.0.16.3", {"start": v(175.77, -85.34) * mm, "end": v(170.69, -85.34) * mm});
            skLineSegment(sketch, "E26.0.16.4", {"start": v(159.77, -90.42) * mm, "end": v(159.77, -85.34) * mm});
            skLineSegment(sketch, "E26.0.16.5", {"start": v(159.77, -85.34) * mm, "end": v(154.69, -85.34) * mm});
            skLineSegment(sketch, "E26.0.16.6", {"start": v(154.69, -85.34) * mm, "end": v(154.69, -90.42) * mm});
            skLineSegment(sketch, "E26.0.16.7", {"start": v(154.69, -90.42) * mm, "end": v(159.77, -90.42) * mm});
            skLineSegment(sketch, "E26.0.16.8", {"start": v(165.1, -90.42) * mm, "end": v(165.1, -85.34) * mm});
            skLineSegment(sketch, "E26.0.16.9", {"start": v(165.35, -90.42) * mm, "end": v(170.43, -90.42) * mm});
            skLineSegment(sketch, "E26.0.16.10", {"start": v(165.1, -85.34) * mm, "end": v(160.02, -85.34) * mm});
            skLineSegment(sketch, "E26.0.16.11", {"start": v(176.02, -90.42) * mm, "end": v(181.1, -90.42) * mm});
            skLineSegment(sketch, "E26.0.16.12", {"start": v(170.43, -85.34) * mm, "end": v(165.35, -85.34) * mm});
            skLineSegment(sketch, "E26.0.16.13", {"start": v(160.02, -85.34) * mm, "end": v(160.02, -90.42) * mm});
            skLineSegment(sketch, "E26.0.16.14", {"start": v(176.02, -85.34) * mm, "end": v(176.02, -90.42) * mm});
            skLineSegment(sketch, "E26.0.16.15", {"start": v(165.35, -85.34) * mm, "end": v(165.35, -90.42) * mm});
            skLineSegment(sketch, "E26.0.16.16", {"start": v(160.02, -90.42) * mm, "end": v(165.1, -90.42) * mm});
            skLineSegment(sketch, "E26.0.16.17", {"start": v(170.43, -90.42) * mm, "end": v(170.43, -85.34) * mm});
            skLineSegment(sketch, "E26.0.16.18", {"start": v(181.1, -85.34) * mm, "end": v(176.02, -85.34) * mm});
            skLineSegment(sketch, "E26.0.16.19", {"start": v(154.43, -90.42) * mm, "end": v(154.43, -85.34) * mm});
            skLineSegment(sketch, "E26.0.16.20", {"start": v(181.1, -90.42) * mm, "end": v(181.1, -85.34) * mm});
            skLineSegment(sketch, "E26.0.16.21", {"start": v(154.43, -85.34) * mm, "end": v(149.35, -85.34) * mm});
            skLineSegment(sketch, "E26.0.16.22", {"start": v(170.69, -90.42) * mm, "end": v(175.77, -90.42) * mm});
            skLineSegment(sketch, "E26.0.16.23", {"start": v(175.77, -90.42) * mm, "end": v(175.77, -85.34) * mm});
            skLineSegment(sketch, "E26.0.17.0", {"start": v(149.35, -90.68) * mm, "end": v(149.35, -95.76) * mm});
            skLineSegment(sketch, "E26.0.17.1", {"start": v(170.69, -90.68) * mm, "end": v(170.69, -95.76) * mm});
            skLineSegment(sketch, "E26.0.17.2", {"start": v(149.35, -95.76) * mm, "end": v(154.43, -95.76) * mm});
            skLineSegment(sketch, "E26.0.17.3", {"start": v(175.77, -90.68) * mm, "end": v(170.69, -90.68) * mm});
            skLineSegment(sketch, "E26.0.17.4", {"start": v(159.77, -95.76) * mm, "end": v(159.77, -90.68) * mm});
            skLineSegment(sketch, "E26.0.17.5", {"start": v(159.77, -90.68) * mm, "end": v(154.69, -90.68) * mm});
            skLineSegment(sketch, "E26.0.17.6", {"start": v(154.69, -90.68) * mm, "end": v(154.69, -95.76) * mm});
            skLineSegment(sketch, "E26.0.17.7", {"start": v(154.69, -95.76) * mm, "end": v(159.77, -95.76) * mm});
            skLineSegment(sketch, "E26.0.17.8", {"start": v(165.1, -95.76) * mm, "end": v(165.1, -90.68) * mm});
            skLineSegment(sketch, "E26.0.17.9", {"start": v(165.35, -95.76) * mm, "end": v(170.43, -95.76) * mm});
            skLineSegment(sketch, "E26.0.17.10", {"start": v(165.1, -90.68) * mm, "end": v(160.02, -90.68) * mm});
            skLineSegment(sketch, "E26.0.17.11", {"start": v(176.02, -95.76) * mm, "end": v(181.1, -95.76) * mm});
            skLineSegment(sketch, "E26.0.17.12", {"start": v(170.43, -90.68) * mm, "end": v(165.35, -90.68) * mm});
            skLineSegment(sketch, "E26.0.17.13", {"start": v(160.02, -90.68) * mm, "end": v(160.02, -95.76) * mm});
            skLineSegment(sketch, "E26.0.17.14", {"start": v(176.02, -90.68) * mm, "end": v(176.02, -95.76) * mm});
            skLineSegment(sketch, "E26.0.17.15", {"start": v(165.35, -90.68) * mm, "end": v(165.35, -95.76) * mm});
            skLineSegment(sketch, "E26.0.17.16", {"start": v(160.02, -95.76) * mm, "end": v(165.1, -95.76) * mm});
            skLineSegment(sketch, "E26.0.17.17", {"start": v(170.43, -95.76) * mm, "end": v(170.43, -90.68) * mm});
            skLineSegment(sketch, "E26.0.17.18", {"start": v(181.1, -90.68) * mm, "end": v(176.02, -90.68) * mm});
            skLineSegment(sketch, "E26.0.17.19", {"start": v(154.43, -95.76) * mm, "end": v(154.43, -90.68) * mm});
            skLineSegment(sketch, "E26.0.17.20", {"start": v(181.1, -95.76) * mm, "end": v(181.1, -90.68) * mm});
            skLineSegment(sketch, "E26.0.17.21", {"start": v(154.43, -90.68) * mm, "end": v(149.35, -90.68) * mm});
            skLineSegment(sketch, "E26.0.17.22", {"start": v(170.69, -95.76) * mm, "end": v(175.77, -95.76) * mm});
            skLineSegment(sketch, "E26.0.17.23", {"start": v(175.77, -95.76) * mm, "end": v(175.77, -90.68) * mm});
            skLineSegment(sketch, "E26.0.18.0", {"start": v(149.35, -96.01) * mm, "end": v(149.35, -101.1) * mm});
            skLineSegment(sketch, "E26.0.18.1", {"start": v(170.69, -96.01) * mm, "end": v(170.69, -101.1) * mm});
            skLineSegment(sketch, "E26.0.18.2", {"start": v(149.35, -101.1) * mm, "end": v(154.43, -101.1) * mm});
            skLineSegment(sketch, "E26.0.18.3", {"start": v(175.77, -96.01) * mm, "end": v(170.69, -96.01) * mm});
            skLineSegment(sketch, "E26.0.18.4", {"start": v(159.77, -101.1) * mm, "end": v(159.77, -96.01) * mm});
            skLineSegment(sketch, "E26.0.18.5", {"start": v(159.77, -96.01) * mm, "end": v(154.69, -96.01) * mm});
            skLineSegment(sketch, "E26.0.18.6", {"start": v(154.69, -96.01) * mm, "end": v(154.69, -101.1) * mm});
            skLineSegment(sketch, "E26.0.18.7", {"start": v(154.69, -101.1) * mm, "end": v(159.77, -101.1) * mm});
            skLineSegment(sketch, "E26.0.18.8", {"start": v(165.1, -101.1) * mm, "end": v(165.1, -96.01) * mm});
            skLineSegment(sketch, "E26.0.18.9", {"start": v(165.35, -101.1) * mm, "end": v(170.43, -101.1) * mm});
            skLineSegment(sketch, "E26.0.18.10", {"start": v(165.1, -96.01) * mm, "end": v(160.02, -96.01) * mm});
            skLineSegment(sketch, "E26.0.18.11", {"start": v(176.02, -101.1) * mm, "end": v(181.1, -101.1) * mm});
            skLineSegment(sketch, "E26.0.18.12", {"start": v(170.43, -96.01) * mm, "end": v(165.35, -96.01) * mm});
            skLineSegment(sketch, "E26.0.18.13", {"start": v(160.02, -96.01) * mm, "end": v(160.02, -101.1) * mm});
            skLineSegment(sketch, "E26.0.18.14", {"start": v(176.02, -96.01) * mm, "end": v(176.02, -101.1) * mm});
            skLineSegment(sketch, "E26.0.18.15", {"start": v(165.35, -96.01) * mm, "end": v(165.35, -101.1) * mm});
            skLineSegment(sketch, "E26.0.18.16", {"start": v(160.02, -101.1) * mm, "end": v(165.1, -101.1) * mm});
            skLineSegment(sketch, "E26.0.18.17", {"start": v(170.43, -101.1) * mm, "end": v(170.43, -96.01) * mm});
            skLineSegment(sketch, "E26.0.18.18", {"start": v(181.1, -96.01) * mm, "end": v(176.02, -96.01) * mm});
            skLineSegment(sketch, "E26.0.18.19", {"start": v(154.43, -101.1) * mm, "end": v(154.43, -96.01) * mm});
            skLineSegment(sketch, "E26.0.18.20", {"start": v(181.1, -101.1) * mm, "end": v(181.1, -96.01) * mm});
            skLineSegment(sketch, "E26.0.18.21", {"start": v(154.43, -96.01) * mm, "end": v(149.35, -96.01) * mm});
            skLineSegment(sketch, "E26.0.18.22", {"start": v(170.69, -101.1) * mm, "end": v(175.77, -101.1) * mm});
            skLineSegment(sketch, "E26.0.18.23", {"start": v(175.77, -101.1) * mm, "end": v(175.77, -96.01) * mm});
            skLineSegment(sketch, "E26.0.19.0", {"start": v(149.35, -101.35) * mm, "end": v(149.35, -106.43) * mm});
            skLineSegment(sketch, "E26.0.19.1", {"start": v(170.69, -101.35) * mm, "end": v(170.69, -106.43) * mm});
            skLineSegment(sketch, "E26.0.19.2", {"start": v(149.35, -106.43) * mm, "end": v(154.43, -106.43) * mm});
            skLineSegment(sketch, "E26.0.19.3", {"start": v(175.77, -101.35) * mm, "end": v(170.69, -101.35) * mm});
            skLineSegment(sketch, "E26.0.19.4", {"start": v(159.77, -106.43) * mm, "end": v(159.77, -101.35) * mm});
            skLineSegment(sketch, "E26.0.19.5", {"start": v(159.77, -101.35) * mm, "end": v(154.69, -101.35) * mm});
            skLineSegment(sketch, "E26.0.19.6", {"start": v(154.69, -101.35) * mm, "end": v(154.69, -106.43) * mm});
            skLineSegment(sketch, "E26.0.19.7", {"start": v(154.69, -106.43) * mm, "end": v(159.77, -106.43) * mm});
            skLineSegment(sketch, "E26.0.19.8", {"start": v(165.1, -106.43) * mm, "end": v(165.1, -101.35) * mm});
            skLineSegment(sketch, "E26.0.19.9", {"start": v(165.35, -106.43) * mm, "end": v(170.43, -106.43) * mm});
            skLineSegment(sketch, "E26.0.19.10", {"start": v(165.1, -101.35) * mm, "end": v(160.02, -101.35) * mm});
            skLineSegment(sketch, "E26.0.19.11", {"start": v(176.02, -106.43) * mm, "end": v(181.1, -106.43) * mm});
            skLineSegment(sketch, "E26.0.19.12", {"start": v(170.43, -101.35) * mm, "end": v(165.35, -101.35) * mm});
            skLineSegment(sketch, "E26.0.19.13", {"start": v(160.02, -101.35) * mm, "end": v(160.02, -106.43) * mm});
            skLineSegment(sketch, "E26.0.19.14", {"start": v(176.02, -101.35) * mm, "end": v(176.02, -106.43) * mm});
            skLineSegment(sketch, "E26.0.19.15", {"start": v(165.35, -101.35) * mm, "end": v(165.35, -106.43) * mm});
            skLineSegment(sketch, "E26.0.19.16", {"start": v(160.02, -106.43) * mm, "end": v(165.1, -106.43) * mm});
            skLineSegment(sketch, "E26.0.19.17", {"start": v(170.43, -106.43) * mm, "end": v(170.43, -101.35) * mm});
            skLineSegment(sketch, "E26.0.19.18", {"start": v(181.1, -101.35) * mm, "end": v(176.02, -101.35) * mm});
            skLineSegment(sketch, "E26.0.19.19", {"start": v(154.43, -106.43) * mm, "end": v(154.43, -101.35) * mm});
            skLineSegment(sketch, "E26.0.19.20", {"start": v(181.1, -106.43) * mm, "end": v(181.1, -101.35) * mm});
            skLineSegment(sketch, "E26.0.19.21", {"start": v(154.43, -101.35) * mm, "end": v(149.35, -101.35) * mm});
            skLineSegment(sketch, "E26.0.19.22", {"start": v(170.69, -106.43) * mm, "end": v(175.77, -106.43) * mm});
            skLineSegment(sketch, "E26.0.19.23", {"start": v(175.77, -106.43) * mm, "end": v(175.77, -101.35) * mm});
            skLineSegment(sketch, "E26.0.20.0", {"start": v(149.35, -106.68) * mm, "end": v(149.35, -111.76) * mm});
            skLineSegment(sketch, "E26.0.20.1", {"start": v(170.69, -106.68) * mm, "end": v(170.69, -111.76) * mm});
            skLineSegment(sketch, "E26.0.20.2", {"start": v(149.35, -111.76) * mm, "end": v(154.43, -111.76) * mm});
            skLineSegment(sketch, "E26.0.20.3", {"start": v(175.77, -106.68) * mm, "end": v(170.69, -106.68) * mm});
            skLineSegment(sketch, "E26.0.20.4", {"start": v(159.77, -111.76) * mm, "end": v(159.77, -106.68) * mm});
            skLineSegment(sketch, "E26.0.20.5", {"start": v(159.77, -106.68) * mm, "end": v(154.69, -106.68) * mm});
            skLineSegment(sketch, "E26.0.20.6", {"start": v(154.69, -106.68) * mm, "end": v(154.69, -111.76) * mm});
            skLineSegment(sketch, "E26.0.20.7", {"start": v(154.69, -111.76) * mm, "end": v(159.77, -111.76) * mm});
            skLineSegment(sketch, "E26.0.20.8", {"start": v(165.1, -111.76) * mm, "end": v(165.1, -106.68) * mm});
            skLineSegment(sketch, "E26.0.20.9", {"start": v(165.35, -111.76) * mm, "end": v(170.43, -111.76) * mm});
            skLineSegment(sketch, "E26.0.20.10", {"start": v(165.1, -106.68) * mm, "end": v(160.02, -106.68) * mm});
            skLineSegment(sketch, "E26.0.20.11", {"start": v(176.02, -111.76) * mm, "end": v(181.1, -111.76) * mm});
            skLineSegment(sketch, "E26.0.20.12", {"start": v(170.43, -106.68) * mm, "end": v(165.35, -106.68) * mm});
            skLineSegment(sketch, "E26.0.20.13", {"start": v(160.02, -106.68) * mm, "end": v(160.02, -111.76) * mm});
            skLineSegment(sketch, "E26.0.20.14", {"start": v(176.02, -106.68) * mm, "end": v(176.02, -111.76) * mm});
            skLineSegment(sketch, "E26.0.20.15", {"start": v(165.35, -106.68) * mm, "end": v(165.35, -111.76) * mm});
            skLineSegment(sketch, "E26.0.20.16", {"start": v(160.02, -111.76) * mm, "end": v(165.1, -111.76) * mm});
            skLineSegment(sketch, "E26.0.20.17", {"start": v(170.43, -111.76) * mm, "end": v(170.43, -106.68) * mm});
            skLineSegment(sketch, "E26.0.20.18", {"start": v(181.1, -106.68) * mm, "end": v(176.02, -106.68) * mm});
            skLineSegment(sketch, "E26.0.20.19", {"start": v(154.43, -111.76) * mm, "end": v(154.43, -106.68) * mm});
            skLineSegment(sketch, "E26.0.20.20", {"start": v(181.1, -111.76) * mm, "end": v(181.1, -106.68) * mm});
            skLineSegment(sketch, "E26.0.20.21", {"start": v(154.43, -106.68) * mm, "end": v(149.35, -106.68) * mm});
            skLineSegment(sketch, "E26.0.20.22", {"start": v(170.69, -111.76) * mm, "end": v(175.77, -111.76) * mm});
            skLineSegment(sketch, "E26.0.20.23", {"start": v(175.77, -111.76) * mm, "end": v(175.77, -106.68) * mm});
            skLineSegment(sketch, "E26.0.21.0", {"start": v(149.35, -112.01) * mm, "end": v(149.35, -117.1) * mm});
            skLineSegment(sketch, "E26.0.21.1", {"start": v(170.69, -112.01) * mm, "end": v(170.69, -117.1) * mm});
            skLineSegment(sketch, "E26.0.21.2", {"start": v(149.35, -117.1) * mm, "end": v(154.43, -117.1) * mm});
            skLineSegment(sketch, "E26.0.21.3", {"start": v(175.77, -112.01) * mm, "end": v(170.69, -112.01) * mm});
            skLineSegment(sketch, "E26.0.21.4", {"start": v(159.77, -117.1) * mm, "end": v(159.77, -112.01) * mm});
            skLineSegment(sketch, "E26.0.21.5", {"start": v(159.77, -112.01) * mm, "end": v(154.69, -112.01) * mm});
            skLineSegment(sketch, "E26.0.21.6", {"start": v(154.69, -112.01) * mm, "end": v(154.69, -117.1) * mm});
            skLineSegment(sketch, "E26.0.21.7", {"start": v(154.69, -117.1) * mm, "end": v(159.77, -117.1) * mm});
            skLineSegment(sketch, "E26.0.21.8", {"start": v(165.1, -117.1) * mm, "end": v(165.1, -112.01) * mm});
            skLineSegment(sketch, "E26.0.21.9", {"start": v(165.35, -117.1) * mm, "end": v(170.43, -117.1) * mm});
            skLineSegment(sketch, "E26.0.21.10", {"start": v(165.1, -112.01) * mm, "end": v(160.02, -112.01) * mm});
            skLineSegment(sketch, "E26.0.21.11", {"start": v(176.02, -117.1) * mm, "end": v(181.1, -117.1) * mm});
            skLineSegment(sketch, "E26.0.21.12", {"start": v(170.43, -112.01) * mm, "end": v(165.35, -112.01) * mm});
            skLineSegment(sketch, "E26.0.21.13", {"start": v(160.02, -112.01) * mm, "end": v(160.02, -117.1) * mm});
            skLineSegment(sketch, "E26.0.21.14", {"start": v(176.02, -112.01) * mm, "end": v(176.02, -117.1) * mm});
            skLineSegment(sketch, "E26.0.21.15", {"start": v(165.35, -112.01) * mm, "end": v(165.35, -117.1) * mm});
            skLineSegment(sketch, "E26.0.21.16", {"start": v(160.02, -117.1) * mm, "end": v(165.1, -117.1) * mm});
            skLineSegment(sketch, "E26.0.21.17", {"start": v(170.43, -117.1) * mm, "end": v(170.43, -112.01) * mm});
            skLineSegment(sketch, "E26.0.21.18", {"start": v(181.1, -112.01) * mm, "end": v(176.02, -112.01) * mm});
            skLineSegment(sketch, "E26.0.21.19", {"start": v(154.43, -117.1) * mm, "end": v(154.43, -112.01) * mm});
            skLineSegment(sketch, "E26.0.21.20", {"start": v(181.1, -117.1) * mm, "end": v(181.1, -112.01) * mm});
            skLineSegment(sketch, "E26.0.21.21", {"start": v(154.43, -112.01) * mm, "end": v(149.35, -112.01) * mm});
            skLineSegment(sketch, "E26.0.21.22", {"start": v(170.69, -117.1) * mm, "end": v(175.77, -117.1) * mm});
            skLineSegment(sketch, "E26.0.21.23", {"start": v(175.77, -117.1) * mm, "end": v(175.77, -112.01) * mm});
            skLineSegment(sketch, "E26.0.22.0", {"start": v(149.35, -117.35) * mm, "end": v(149.35, -122.43) * mm});
            skLineSegment(sketch, "E26.0.22.1", {"start": v(170.69, -117.35) * mm, "end": v(170.69, -122.43) * mm});
            skLineSegment(sketch, "E26.0.22.2", {"start": v(149.35, -122.43) * mm, "end": v(154.43, -122.43) * mm});
            skLineSegment(sketch, "E26.0.22.3", {"start": v(175.77, -117.35) * mm, "end": v(170.69, -117.35) * mm});
            skLineSegment(sketch, "E26.0.22.4", {"start": v(159.77, -122.43) * mm, "end": v(159.77, -117.35) * mm});
            skLineSegment(sketch, "E26.0.22.5", {"start": v(159.77, -117.35) * mm, "end": v(154.69, -117.35) * mm});
            skLineSegment(sketch, "E26.0.22.6", {"start": v(154.69, -117.35) * mm, "end": v(154.69, -122.43) * mm});
            skLineSegment(sketch, "E26.0.22.7", {"start": v(154.69, -122.43) * mm, "end": v(159.77, -122.43) * mm});
            skLineSegment(sketch, "E26.0.22.8", {"start": v(165.1, -122.43) * mm, "end": v(165.1, -117.35) * mm});
            skLineSegment(sketch, "E26.0.22.9", {"start": v(165.35, -122.43) * mm, "end": v(170.43, -122.43) * mm});
            skLineSegment(sketch, "E26.0.22.10", {"start": v(165.1, -117.35) * mm, "end": v(160.02, -117.35) * mm});
            skLineSegment(sketch, "E26.0.22.11", {"start": v(176.02, -122.43) * mm, "end": v(181.1, -122.43) * mm});
            skLineSegment(sketch, "E26.0.22.12", {"start": v(170.43, -117.35) * mm, "end": v(165.35, -117.35) * mm});
            skLineSegment(sketch, "E26.0.22.13", {"start": v(160.02, -117.35) * mm, "end": v(160.02, -122.43) * mm});
            skLineSegment(sketch, "E26.0.22.14", {"start": v(176.02, -117.35) * mm, "end": v(176.02, -122.43) * mm});
            skLineSegment(sketch, "E26.0.22.15", {"start": v(165.35, -117.35) * mm, "end": v(165.35, -122.43) * mm});
            skLineSegment(sketch, "E26.0.22.16", {"start": v(160.02, -122.43) * mm, "end": v(165.1, -122.43) * mm});
            skLineSegment(sketch, "E26.0.22.17", {"start": v(170.43, -122.43) * mm, "end": v(170.43, -117.35) * mm});
            skLineSegment(sketch, "E26.0.22.18", {"start": v(181.1, -117.35) * mm, "end": v(176.02, -117.35) * mm});
            skLineSegment(sketch, "E26.0.22.19", {"start": v(154.43, -122.43) * mm, "end": v(154.43, -117.35) * mm});
            skLineSegment(sketch, "E26.0.22.20", {"start": v(181.1, -122.43) * mm, "end": v(181.1, -117.35) * mm});
            skLineSegment(sketch, "E26.0.22.21", {"start": v(154.43, -117.35) * mm, "end": v(149.35, -117.35) * mm});
            skLineSegment(sketch, "E26.0.22.22", {"start": v(170.69, -122.43) * mm, "end": v(175.77, -122.43) * mm});
            skLineSegment(sketch, "E26.0.22.23", {"start": v(175.77, -122.43) * mm, "end": v(175.77, -117.35) * mm});
            skLineSegment(sketch, "E26.0.23.0", {"start": v(149.35, -122.68) * mm, "end": v(149.35, -127.76) * mm});
            skLineSegment(sketch, "E26.0.23.1", {"start": v(170.69, -122.68) * mm, "end": v(170.69, -127.76) * mm});
            skLineSegment(sketch, "E26.0.23.2", {"start": v(149.35, -127.76) * mm, "end": v(154.43, -127.76) * mm});
            skLineSegment(sketch, "E26.0.23.3", {"start": v(175.77, -122.68) * mm, "end": v(170.69, -122.68) * mm});
            skLineSegment(sketch, "E26.0.23.4", {"start": v(159.77, -127.76) * mm, "end": v(159.77, -122.68) * mm});
            skLineSegment(sketch, "E26.0.23.5", {"start": v(159.77, -122.68) * mm, "end": v(154.69, -122.68) * mm});
            skLineSegment(sketch, "E26.0.23.6", {"start": v(154.69, -122.68) * mm, "end": v(154.69, -127.76) * mm});
            skLineSegment(sketch, "E26.0.23.7", {"start": v(154.69, -127.76) * mm, "end": v(159.77, -127.76) * mm});
            skLineSegment(sketch, "E26.0.23.8", {"start": v(165.1, -127.76) * mm, "end": v(165.1, -122.68) * mm});
            skLineSegment(sketch, "E26.0.23.9", {"start": v(165.35, -127.76) * mm, "end": v(170.43, -127.76) * mm});
            skLineSegment(sketch, "E26.0.23.10", {"start": v(165.1, -122.68) * mm, "end": v(160.02, -122.68) * mm});
            skLineSegment(sketch, "E26.0.23.11", {"start": v(176.02, -127.76) * mm, "end": v(181.1, -127.76) * mm});
            skLineSegment(sketch, "E26.0.23.12", {"start": v(170.43, -122.68) * mm, "end": v(165.35, -122.68) * mm});
            skLineSegment(sketch, "E26.0.23.13", {"start": v(160.02, -122.68) * mm, "end": v(160.02, -127.76) * mm});
            skLineSegment(sketch, "E26.0.23.14", {"start": v(176.02, -122.68) * mm, "end": v(176.02, -127.76) * mm});
            skLineSegment(sketch, "E26.0.23.15", {"start": v(165.35, -122.68) * mm, "end": v(165.35, -127.76) * mm});
            skLineSegment(sketch, "E26.0.23.16", {"start": v(160.02, -127.76) * mm, "end": v(165.1, -127.76) * mm});
            skLineSegment(sketch, "E26.0.23.17", {"start": v(170.43, -127.76) * mm, "end": v(170.43, -122.68) * mm});
            skLineSegment(sketch, "E26.0.23.18", {"start": v(181.1, -122.68) * mm, "end": v(176.02, -122.68) * mm});
            skLineSegment(sketch, "E26.0.23.19", {"start": v(154.43, -127.76) * mm, "end": v(154.43, -122.68) * mm});
            skLineSegment(sketch, "E26.0.23.20", {"start": v(181.1, -127.76) * mm, "end": v(181.1, -122.68) * mm});
            skLineSegment(sketch, "E26.0.23.21", {"start": v(154.43, -122.68) * mm, "end": v(149.35, -122.68) * mm});
            skLineSegment(sketch, "E26.0.23.22", {"start": v(170.69, -127.76) * mm, "end": v(175.77, -127.76) * mm});
            skLineSegment(sketch, "E26.0.23.23", {"start": v(175.77, -127.76) * mm, "end": v(175.77, -122.68) * mm});
            skLineSegment(sketch, "E26.0.24.0", {"start": v(149.35, -128.02) * mm, "end": v(149.35, -133.1) * mm});
            skLineSegment(sketch, "E26.0.24.1", {"start": v(170.69, -128.02) * mm, "end": v(170.69, -133.1) * mm});
            skLineSegment(sketch, "E26.0.24.2", {"start": v(149.35, -133.1) * mm, "end": v(154.43, -133.1) * mm});
            skLineSegment(sketch, "E26.0.24.3", {"start": v(175.77, -128.02) * mm, "end": v(170.69, -128.02) * mm});
            skLineSegment(sketch, "E26.0.24.4", {"start": v(159.77, -133.1) * mm, "end": v(159.77, -128.02) * mm});
            skLineSegment(sketch, "E26.0.24.5", {"start": v(159.77, -128.02) * mm, "end": v(154.69, -128.02) * mm});
            skLineSegment(sketch, "E26.0.24.6", {"start": v(154.69, -128.02) * mm, "end": v(154.69, -133.1) * mm});
            skLineSegment(sketch, "E26.0.24.7", {"start": v(154.69, -133.1) * mm, "end": v(159.77, -133.1) * mm});
            skLineSegment(sketch, "E26.0.24.8", {"start": v(165.1, -133.1) * mm, "end": v(165.1, -128.02) * mm});
            skLineSegment(sketch, "E26.0.24.9", {"start": v(165.35, -133.1) * mm, "end": v(170.43, -133.1) * mm});
            skLineSegment(sketch, "E26.0.24.10", {"start": v(165.1, -128.02) * mm, "end": v(160.02, -128.02) * mm});
            skLineSegment(sketch, "E26.0.24.11", {"start": v(176.02, -133.1) * mm, "end": v(181.1, -133.1) * mm});
            skLineSegment(sketch, "E26.0.24.12", {"start": v(170.43, -128.02) * mm, "end": v(165.35, -128.02) * mm});
            skLineSegment(sketch, "E26.0.24.13", {"start": v(160.02, -128.02) * mm, "end": v(160.02, -133.1) * mm});
            skLineSegment(sketch, "E26.0.24.14", {"start": v(176.02, -128.02) * mm, "end": v(176.02, -133.1) * mm});
            skLineSegment(sketch, "E26.0.24.15", {"start": v(165.35, -128.02) * mm, "end": v(165.35, -133.1) * mm});
            skLineSegment(sketch, "E26.0.24.16", {"start": v(160.02, -133.1) * mm, "end": v(165.1, -133.1) * mm});
            skLineSegment(sketch, "E26.0.24.17", {"start": v(170.43, -133.1) * mm, "end": v(170.43, -128.02) * mm});
            skLineSegment(sketch, "E26.0.24.18", {"start": v(181.1, -128.02) * mm, "end": v(176.02, -128.02) * mm});
            skLineSegment(sketch, "E26.0.24.19", {"start": v(154.43, -133.1) * mm, "end": v(154.43, -128.02) * mm});
            skLineSegment(sketch, "E26.0.24.20", {"start": v(181.1, -133.1) * mm, "end": v(181.1, -128.02) * mm});
            skLineSegment(sketch, "E26.0.24.21", {"start": v(154.43, -128.02) * mm, "end": v(149.35, -128.02) * mm});
            skLineSegment(sketch, "E26.0.24.22", {"start": v(170.69, -133.1) * mm, "end": v(175.77, -133.1) * mm});
            skLineSegment(sketch, "E26.0.24.23", {"start": v(175.77, -133.1) * mm, "end": v(175.77, -128.02) * mm});
            skLineSegment(sketch, "E26.0.25.0", {"start": v(149.35, -133.35) * mm, "end": v(149.35, -138.43) * mm});
            skLineSegment(sketch, "E26.0.25.1", {"start": v(170.69, -133.35) * mm, "end": v(170.69, -138.43) * mm});
            skLineSegment(sketch, "E26.0.25.2", {"start": v(149.35, -138.43) * mm, "end": v(154.43, -138.43) * mm});
            skLineSegment(sketch, "E26.0.25.3", {"start": v(175.77, -133.35) * mm, "end": v(170.69, -133.35) * mm});
            skLineSegment(sketch, "E26.0.25.4", {"start": v(159.77, -138.43) * mm, "end": v(159.77, -133.35) * mm});
            skLineSegment(sketch, "E26.0.25.5", {"start": v(159.77, -133.35) * mm, "end": v(154.69, -133.35) * mm});
            skLineSegment(sketch, "E26.0.25.6", {"start": v(154.69, -133.35) * mm, "end": v(154.69, -138.43) * mm});
            skLineSegment(sketch, "E26.0.25.7", {"start": v(154.69, -138.43) * mm, "end": v(159.77, -138.43) * mm});
            skLineSegment(sketch, "E26.0.25.8", {"start": v(165.1, -138.43) * mm, "end": v(165.1, -133.35) * mm});
            skLineSegment(sketch, "E26.0.25.9", {"start": v(165.35, -138.43) * mm, "end": v(170.43, -138.43) * mm});
            skLineSegment(sketch, "E26.0.25.10", {"start": v(165.1, -133.35) * mm, "end": v(160.02, -133.35) * mm});
            skLineSegment(sketch, "E26.0.25.11", {"start": v(176.02, -138.43) * mm, "end": v(181.1, -138.43) * mm});
            skLineSegment(sketch, "E26.0.25.12", {"start": v(170.43, -133.35) * mm, "end": v(165.35, -133.35) * mm});
            skLineSegment(sketch, "E26.0.25.13", {"start": v(160.02, -133.35) * mm, "end": v(160.02, -138.43) * mm});
            skLineSegment(sketch, "E26.0.25.14", {"start": v(176.02, -133.35) * mm, "end": v(176.02, -138.43) * mm});
            skLineSegment(sketch, "E26.0.25.15", {"start": v(165.35, -133.35) * mm, "end": v(165.35, -138.43) * mm});
            skLineSegment(sketch, "E26.0.25.16", {"start": v(160.02, -138.43) * mm, "end": v(165.1, -138.43) * mm});
            skLineSegment(sketch, "E26.0.25.17", {"start": v(170.43, -138.43) * mm, "end": v(170.43, -133.35) * mm});
            skLineSegment(sketch, "E26.0.25.18", {"start": v(181.1, -133.35) * mm, "end": v(176.02, -133.35) * mm});
            skLineSegment(sketch, "E26.0.25.19", {"start": v(154.43, -138.43) * mm, "end": v(154.43, -133.35) * mm});
            skLineSegment(sketch, "E26.0.25.20", {"start": v(181.1, -138.43) * mm, "end": v(181.1, -133.35) * mm});
            skLineSegment(sketch, "E26.0.25.21", {"start": v(154.43, -133.35) * mm, "end": v(149.35, -133.35) * mm});
            skLineSegment(sketch, "E26.0.25.22", {"start": v(170.69, -138.43) * mm, "end": v(175.77, -138.43) * mm});
            skLineSegment(sketch, "E26.0.25.23", {"start": v(175.77, -138.43) * mm, "end": v(175.77, -133.35) * mm});
            skLineSegment(sketch, "E26.0.26.0", {"start": v(149.35, -138.68) * mm, "end": v(149.35, -143.76) * mm});
            skLineSegment(sketch, "E26.0.26.1", {"start": v(170.69, -138.68) * mm, "end": v(170.69, -143.76) * mm});
            skLineSegment(sketch, "E26.0.26.2", {"start": v(149.35, -143.76) * mm, "end": v(154.43, -143.76) * mm});
            skLineSegment(sketch, "E26.0.26.3", {"start": v(175.77, -138.68) * mm, "end": v(170.69, -138.68) * mm});
            skLineSegment(sketch, "E26.0.26.4", {"start": v(159.77, -143.76) * mm, "end": v(159.77, -138.68) * mm});
            skLineSegment(sketch, "E26.0.26.5", {"start": v(159.77, -138.68) * mm, "end": v(154.69, -138.68) * mm});
            skLineSegment(sketch, "E26.0.26.6", {"start": v(154.69, -138.68) * mm, "end": v(154.69, -143.76) * mm});
            skLineSegment(sketch, "E26.0.26.7", {"start": v(154.69, -143.76) * mm, "end": v(159.77, -143.76) * mm});
            skLineSegment(sketch, "E26.0.26.8", {"start": v(165.1, -143.76) * mm, "end": v(165.1, -138.68) * mm});
            skLineSegment(sketch, "E26.0.26.9", {"start": v(165.35, -143.76) * mm, "end": v(170.43, -143.76) * mm});
            skLineSegment(sketch, "E26.0.26.10", {"start": v(165.1, -138.68) * mm, "end": v(160.02, -138.68) * mm});
            skLineSegment(sketch, "E26.0.26.11", {"start": v(176.02, -143.76) * mm, "end": v(181.1, -143.76) * mm});
            skLineSegment(sketch, "E26.0.26.12", {"start": v(170.43, -138.68) * mm, "end": v(165.35, -138.68) * mm});
            skLineSegment(sketch, "E26.0.26.13", {"start": v(160.02, -138.68) * mm, "end": v(160.02, -143.76) * mm});
            skLineSegment(sketch, "E26.0.26.14", {"start": v(176.02, -138.68) * mm, "end": v(176.02, -143.76) * mm});
            skLineSegment(sketch, "E26.0.26.15", {"start": v(165.35, -138.68) * mm, "end": v(165.35, -143.76) * mm});
            skLineSegment(sketch, "E26.0.26.16", {"start": v(160.02, -143.76) * mm, "end": v(165.1, -143.76) * mm});
            skLineSegment(sketch, "E26.0.26.17", {"start": v(170.43, -143.76) * mm, "end": v(170.43, -138.68) * mm});
            skLineSegment(sketch, "E26.0.26.18", {"start": v(181.1, -138.68) * mm, "end": v(176.02, -138.68) * mm});
            skLineSegment(sketch, "E26.0.26.19", {"start": v(154.43, -143.76) * mm, "end": v(154.43, -138.68) * mm});
            skLineSegment(sketch, "E26.0.26.20", {"start": v(181.1, -143.76) * mm, "end": v(181.1, -138.68) * mm});
            skLineSegment(sketch, "E26.0.26.21", {"start": v(154.43, -138.68) * mm, "end": v(149.35, -138.68) * mm});
            skLineSegment(sketch, "E26.0.26.22", {"start": v(170.69, -143.76) * mm, "end": v(175.77, -143.76) * mm});
            skLineSegment(sketch, "E26.0.26.23", {"start": v(175.77, -143.76) * mm, "end": v(175.77, -138.68) * mm});
            skLineSegment(sketch, "E26.direction1", {"start": v(149.35, -5.08) * mm, "end": v(174.75, -5.08) * mm, "construction": true});
            skLineSegment(sketch, "E26.direction2", {"start": v(149.35, -5.08) * mm, "end": v(149.35, -10.41) * mm, "construction": true});
            skSolve(sketch);
        }
        {
            var Q0;
            Q0=qCreatedBy(makeId("Top.planeOp"),FACE);
            var sketch = newSketch(context, id + "F9", { "sketchPlane" : qUnion([Q0])});
            skLineSegment(sketch, "E27.0.0", {"start": v(186.44, -5.08) * mm, "end": v(186.44, 0) * mm});
            skLineSegment(sketch, "E27.0.1", {"start": v(186.44, 0) * mm, "end": v(181.36, 0) * mm});
            skLineSegment(sketch, "E27.0.2", {"start": v(181.36, 0) * mm, "end": v(181.36, -5.08) * mm});
            skLineSegment(sketch, "E27.0.3", {"start": v(181.36, -5.08) * mm, "end": v(186.44, -5.08) * mm});
            skLineSegment(sketch, "E27.1.0", {"start": v(191.77, -5.08) * mm, "end": v(191.77, 0) * mm});
            skLineSegment(sketch, "E27.1.1", {"start": v(191.77, 0) * mm, "end": v(186.7, 0) * mm});
            skLineSegment(sketch, "E27.1.2", {"start": v(186.7, 0) * mm, "end": v(186.7, -5.08) * mm});
            skLineSegment(sketch, "E27.1.3", {"start": v(186.7, -5.08) * mm, "end": v(191.77, -5.08) * mm});
            skLineSegment(sketch, "E27.2.0", {"start": v(197.1, -5.08) * mm, "end": v(197.1, 0) * mm});
            skLineSegment(sketch, "E27.2.1", {"start": v(197.1, 0) * mm, "end": v(192.02, 0) * mm});
            skLineSegment(sketch, "E27.2.2", {"start": v(192.02, 0) * mm, "end": v(192.02, -5.08) * mm});
            skLineSegment(sketch, "E27.2.3", {"start": v(192.02, -5.08) * mm, "end": v(197.1, -5.08) * mm});
            skLineSegment(sketch, "E27.3.0", {"start": v(202.44, -5.08) * mm, "end": v(202.44, 0) * mm});
            skLineSegment(sketch, "E27.3.1", {"start": v(202.44, 0) * mm, "end": v(197.36, 0) * mm});
            skLineSegment(sketch, "E27.3.2", {"start": v(197.36, 0) * mm, "end": v(197.36, -5.08) * mm});
            skLineSegment(sketch, "E27.3.3", {"start": v(197.36, -5.08) * mm, "end": v(202.44, -5.08) * mm});
            skLineSegment(sketch, "E28.0.1.0", {"start": v(197.36, -10.41) * mm, "end": v(202.44, -10.41) * mm});
            skLineSegment(sketch, "E28.0.1.1", {"start": v(197.1, -5.33) * mm, "end": v(192.02, -5.33) * mm});
            skLineSegment(sketch, "E28.0.1.2", {"start": v(181.36, -10.41) * mm, "end": v(186.44, -10.41) * mm});
            skLineSegment(sketch, "E28.0.1.3", {"start": v(202.44, -5.33) * mm, "end": v(197.36, -5.33) * mm});
            skLineSegment(sketch, "E28.0.1.4", {"start": v(192.02, -5.33) * mm, "end": v(192.02, -10.41) * mm});
            skLineSegment(sketch, "E28.0.1.5", {"start": v(191.77, -10.41) * mm, "end": v(191.77, -5.33) * mm});
            skLineSegment(sketch, "E28.0.1.6", {"start": v(197.36, -5.33) * mm, "end": v(197.36, -10.41) * mm});
            skLineSegment(sketch, "E28.0.1.7", {"start": v(192.02, -10.41) * mm, "end": v(197.1, -10.41) * mm});
            skLineSegment(sketch, "E28.0.1.8", {"start": v(191.77, -5.33) * mm, "end": v(186.7, -5.33) * mm});
            skLineSegment(sketch, "E28.0.1.9", {"start": v(202.44, -10.41) * mm, "end": v(202.44, -5.33) * mm});
            skLineSegment(sketch, "E28.0.1.10", {"start": v(186.44, -10.41) * mm, "end": v(186.44, -5.33) * mm});
            skLineSegment(sketch, "E28.0.1.11", {"start": v(186.7, -10.41) * mm, "end": v(191.77, -10.41) * mm});
            skLineSegment(sketch, "E28.0.1.12", {"start": v(186.44, -5.33) * mm, "end": v(181.36, -5.33) * mm});
            skLineSegment(sketch, "E28.0.1.13", {"start": v(197.1, -10.41) * mm, "end": v(197.1, -5.33) * mm});
            skLineSegment(sketch, "E28.0.1.14", {"start": v(181.36, -5.33) * mm, "end": v(181.36, -10.41) * mm});
            skLineSegment(sketch, "E28.0.1.15", {"start": v(186.7, -5.33) * mm, "end": v(186.7, -10.41) * mm});
            skLineSegment(sketch, "E28.0.2.0", {"start": v(197.36, -15.75) * mm, "end": v(202.44, -15.75) * mm});
            skLineSegment(sketch, "E28.0.2.1", {"start": v(197.1, -10.67) * mm, "end": v(192.02, -10.67) * mm});
            skLineSegment(sketch, "E28.0.2.2", {"start": v(181.36, -15.75) * mm, "end": v(186.44, -15.75) * mm});
            skLineSegment(sketch, "E28.0.2.3", {"start": v(202.44, -10.67) * mm, "end": v(197.36, -10.67) * mm});
            skLineSegment(sketch, "E28.0.2.4", {"start": v(192.02, -10.67) * mm, "end": v(192.02, -15.75) * mm});
            skLineSegment(sketch, "E28.0.2.5", {"start": v(191.77, -15.75) * mm, "end": v(191.77, -10.67) * mm});
            skLineSegment(sketch, "E28.0.2.6", {"start": v(197.36, -10.67) * mm, "end": v(197.36, -15.75) * mm});
            skLineSegment(sketch, "E28.0.2.7", {"start": v(192.02, -15.75) * mm, "end": v(197.1, -15.75) * mm});
            skLineSegment(sketch, "E28.0.2.8", {"start": v(191.77, -10.67) * mm, "end": v(186.7, -10.67) * mm});
            skLineSegment(sketch, "E28.0.2.9", {"start": v(202.44, -15.75) * mm, "end": v(202.44, -10.67) * mm});
            skLineSegment(sketch, "E28.0.2.10", {"start": v(186.44, -15.75) * mm, "end": v(186.44, -10.67) * mm});
            skLineSegment(sketch, "E28.0.2.11", {"start": v(186.7, -15.75) * mm, "end": v(191.77, -15.75) * mm});
            skLineSegment(sketch, "E28.0.2.12", {"start": v(186.44, -10.67) * mm, "end": v(181.36, -10.67) * mm});
            skLineSegment(sketch, "E28.0.2.13", {"start": v(197.1, -15.75) * mm, "end": v(197.1, -10.67) * mm});
            skLineSegment(sketch, "E28.0.2.14", {"start": v(181.36, -10.67) * mm, "end": v(181.36, -15.75) * mm});
            skLineSegment(sketch, "E28.0.2.15", {"start": v(186.7, -10.67) * mm, "end": v(186.7, -15.75) * mm});
            skLineSegment(sketch, "E28.0.3.0", {"start": v(197.36, -21.08) * mm, "end": v(202.44, -21.08) * mm});
            skLineSegment(sketch, "E28.0.3.1", {"start": v(197.1, -16) * mm, "end": v(192.02, -16) * mm});
            skLineSegment(sketch, "E28.0.3.2", {"start": v(181.36, -21.08) * mm, "end": v(186.44, -21.08) * mm});
            skLineSegment(sketch, "E28.0.3.3", {"start": v(202.44, -16) * mm, "end": v(197.36, -16) * mm});
            skLineSegment(sketch, "E28.0.3.4", {"start": v(192.02, -16) * mm, "end": v(192.02, -21.08) * mm});
            skLineSegment(sketch, "E28.0.3.5", {"start": v(191.77, -21.08) * mm, "end": v(191.77, -16) * mm});
            skLineSegment(sketch, "E28.0.3.6", {"start": v(197.36, -16) * mm, "end": v(197.36, -21.08) * mm});
            skLineSegment(sketch, "E28.0.3.7", {"start": v(192.02, -21.08) * mm, "end": v(197.1, -21.08) * mm});
            skLineSegment(sketch, "E28.0.3.8", {"start": v(191.77, -16) * mm, "end": v(186.7, -16) * mm});
            skLineSegment(sketch, "E28.0.3.9", {"start": v(202.44, -21.08) * mm, "end": v(202.44, -16) * mm});
            skLineSegment(sketch, "E28.0.3.10", {"start": v(186.44, -21.08) * mm, "end": v(186.44, -16) * mm});
            skLineSegment(sketch, "E28.0.3.11", {"start": v(186.7, -21.08) * mm, "end": v(191.77, -21.08) * mm});
            skLineSegment(sketch, "E28.0.3.12", {"start": v(186.44, -16) * mm, "end": v(181.36, -16) * mm});
            skLineSegment(sketch, "E28.0.3.13", {"start": v(197.1, -21.08) * mm, "end": v(197.1, -16) * mm});
            skLineSegment(sketch, "E28.0.3.14", {"start": v(181.36, -16) * mm, "end": v(181.36, -21.08) * mm});
            skLineSegment(sketch, "E28.0.3.15", {"start": v(186.7, -16) * mm, "end": v(186.7, -21.08) * mm});
            skLineSegment(sketch, "E28.0.4.0", {"start": v(197.36, -26.42) * mm, "end": v(202.44, -26.42) * mm});
            skLineSegment(sketch, "E28.0.4.1", {"start": v(197.1, -21.34) * mm, "end": v(192.02, -21.34) * mm});
            skLineSegment(sketch, "E28.0.4.2", {"start": v(181.36, -26.42) * mm, "end": v(186.44, -26.42) * mm});
            skLineSegment(sketch, "E28.0.4.3", {"start": v(202.44, -21.34) * mm, "end": v(197.36, -21.34) * mm});
            skLineSegment(sketch, "E28.0.4.4", {"start": v(192.02, -21.34) * mm, "end": v(192.02, -26.42) * mm});
            skLineSegment(sketch, "E28.0.4.5", {"start": v(191.77, -26.42) * mm, "end": v(191.77, -21.34) * mm});
            skLineSegment(sketch, "E28.0.4.6", {"start": v(197.36, -21.34) * mm, "end": v(197.36, -26.42) * mm});
            skLineSegment(sketch, "E28.0.4.7", {"start": v(192.02, -26.42) * mm, "end": v(197.1, -26.42) * mm});
            skLineSegment(sketch, "E28.0.4.8", {"start": v(191.77, -21.34) * mm, "end": v(186.7, -21.34) * mm});
            skLineSegment(sketch, "E28.0.4.9", {"start": v(202.44, -26.42) * mm, "end": v(202.44, -21.34) * mm});
            skLineSegment(sketch, "E28.0.4.10", {"start": v(186.44, -26.42) * mm, "end": v(186.44, -21.34) * mm});
            skLineSegment(sketch, "E28.0.4.11", {"start": v(186.7, -26.42) * mm, "end": v(191.77, -26.42) * mm});
            skLineSegment(sketch, "E28.0.4.12", {"start": v(186.44, -21.34) * mm, "end": v(181.36, -21.34) * mm});
            skLineSegment(sketch, "E28.0.4.13", {"start": v(197.1, -26.42) * mm, "end": v(197.1, -21.34) * mm});
            skLineSegment(sketch, "E28.0.4.14", {"start": v(181.36, -21.34) * mm, "end": v(181.36, -26.42) * mm});
            skLineSegment(sketch, "E28.0.4.15", {"start": v(186.7, -21.34) * mm, "end": v(186.7, -26.42) * mm});
            skLineSegment(sketch, "E28.0.5.0", {"start": v(197.36, -31.75) * mm, "end": v(202.44, -31.75) * mm});
            skLineSegment(sketch, "E28.0.5.1", {"start": v(197.1, -26.67) * mm, "end": v(192.02, -26.67) * mm});
            skLineSegment(sketch, "E28.0.5.2", {"start": v(181.36, -31.75) * mm, "end": v(186.44, -31.75) * mm});
            skLineSegment(sketch, "E28.0.5.3", {"start": v(202.44, -26.67) * mm, "end": v(197.36, -26.67) * mm});
            skLineSegment(sketch, "E28.0.5.4", {"start": v(192.02, -26.67) * mm, "end": v(192.02, -31.75) * mm});
            skLineSegment(sketch, "E28.0.5.5", {"start": v(191.77, -31.75) * mm, "end": v(191.77, -26.67) * mm});
            skLineSegment(sketch, "E28.0.5.6", {"start": v(197.36, -26.67) * mm, "end": v(197.36, -31.75) * mm});
            skLineSegment(sketch, "E28.0.5.7", {"start": v(192.02, -31.75) * mm, "end": v(197.1, -31.75) * mm});
            skLineSegment(sketch, "E28.0.5.8", {"start": v(191.77, -26.67) * mm, "end": v(186.7, -26.67) * mm});
            skLineSegment(sketch, "E28.0.5.9", {"start": v(202.44, -31.75) * mm, "end": v(202.44, -26.67) * mm});
            skLineSegment(sketch, "E28.0.5.10", {"start": v(186.44, -31.75) * mm, "end": v(186.44, -26.67) * mm});
            skLineSegment(sketch, "E28.0.5.11", {"start": v(186.7, -31.75) * mm, "end": v(191.77, -31.75) * mm});
            skLineSegment(sketch, "E28.0.5.12", {"start": v(186.44, -26.67) * mm, "end": v(181.36, -26.67) * mm});
            skLineSegment(sketch, "E28.0.5.13", {"start": v(197.1, -31.75) * mm, "end": v(197.1, -26.67) * mm});
            skLineSegment(sketch, "E28.0.5.14", {"start": v(181.36, -26.67) * mm, "end": v(181.36, -31.75) * mm});
            skLineSegment(sketch, "E28.0.5.15", {"start": v(186.7, -26.67) * mm, "end": v(186.7, -31.75) * mm});
            skLineSegment(sketch, "E28.0.6.0", {"start": v(197.36, -37.08) * mm, "end": v(202.44, -37.08) * mm});
            skLineSegment(sketch, "E28.0.6.1", {"start": v(197.1, -32) * mm, "end": v(192.02, -32) * mm});
            skLineSegment(sketch, "E28.0.6.2", {"start": v(181.36, -37.08) * mm, "end": v(186.44, -37.08) * mm});
            skLineSegment(sketch, "E28.0.6.3", {"start": v(202.44, -32) * mm, "end": v(197.36, -32) * mm});
            skLineSegment(sketch, "E28.0.6.4", {"start": v(192.02, -32) * mm, "end": v(192.02, -37.08) * mm});
            skLineSegment(sketch, "E28.0.6.5", {"start": v(191.77, -37.08) * mm, "end": v(191.77, -32) * mm});
            skLineSegment(sketch, "E28.0.6.6", {"start": v(197.36, -32) * mm, "end": v(197.36, -37.08) * mm});
            skLineSegment(sketch, "E28.0.6.7", {"start": v(192.02, -37.08) * mm, "end": v(197.1, -37.08) * mm});
            skLineSegment(sketch, "E28.0.6.8", {"start": v(191.77, -32) * mm, "end": v(186.7, -32) * mm});
            skLineSegment(sketch, "E28.0.6.9", {"start": v(202.44, -37.08) * mm, "end": v(202.44, -32) * mm});
            skLineSegment(sketch, "E28.0.6.10", {"start": v(186.44, -37.08) * mm, "end": v(186.44, -32) * mm});
            skLineSegment(sketch, "E28.0.6.11", {"start": v(186.7, -37.08) * mm, "end": v(191.77, -37.08) * mm});
            skLineSegment(sketch, "E28.0.6.12", {"start": v(186.44, -32) * mm, "end": v(181.36, -32) * mm});
            skLineSegment(sketch, "E28.0.6.13", {"start": v(197.1, -37.08) * mm, "end": v(197.1, -32) * mm});
            skLineSegment(sketch, "E28.0.6.14", {"start": v(181.36, -32) * mm, "end": v(181.36, -37.08) * mm});
            skLineSegment(sketch, "E28.0.6.15", {"start": v(186.7, -32) * mm, "end": v(186.7, -37.08) * mm});
            skLineSegment(sketch, "E28.0.7.0", {"start": v(197.36, -42.42) * mm, "end": v(202.44, -42.42) * mm});
            skLineSegment(sketch, "E28.0.7.1", {"start": v(197.1, -37.34) * mm, "end": v(192.02, -37.34) * mm});
            skLineSegment(sketch, "E28.0.7.2", {"start": v(181.36, -42.42) * mm, "end": v(186.44, -42.42) * mm});
            skLineSegment(sketch, "E28.0.7.3", {"start": v(202.44, -37.34) * mm, "end": v(197.36, -37.34) * mm});
            skLineSegment(sketch, "E28.0.7.4", {"start": v(192.02, -37.34) * mm, "end": v(192.02, -42.42) * mm});
            skLineSegment(sketch, "E28.0.7.5", {"start": v(191.77, -42.42) * mm, "end": v(191.77, -37.34) * mm});
            skLineSegment(sketch, "E28.0.7.6", {"start": v(197.36, -37.34) * mm, "end": v(197.36, -42.42) * mm});
            skLineSegment(sketch, "E28.0.7.7", {"start": v(192.02, -42.42) * mm, "end": v(197.1, -42.42) * mm});
            skLineSegment(sketch, "E28.0.7.8", {"start": v(191.77, -37.34) * mm, "end": v(186.7, -37.34) * mm});
            skLineSegment(sketch, "E28.0.7.9", {"start": v(202.44, -42.42) * mm, "end": v(202.44, -37.34) * mm});
            skLineSegment(sketch, "E28.0.7.10", {"start": v(186.44, -42.42) * mm, "end": v(186.44, -37.34) * mm});
            skLineSegment(sketch, "E28.0.7.11", {"start": v(186.7, -42.42) * mm, "end": v(191.77, -42.42) * mm});
            skLineSegment(sketch, "E28.0.7.12", {"start": v(186.44, -37.34) * mm, "end": v(181.36, -37.34) * mm});
            skLineSegment(sketch, "E28.0.7.13", {"start": v(197.1, -42.42) * mm, "end": v(197.1, -37.34) * mm});
            skLineSegment(sketch, "E28.0.7.14", {"start": v(181.36, -37.34) * mm, "end": v(181.36, -42.42) * mm});
            skLineSegment(sketch, "E28.0.7.15", {"start": v(186.7, -37.34) * mm, "end": v(186.7, -42.42) * mm});
            skLineSegment(sketch, "E28.0.8.0", {"start": v(197.36, -47.75) * mm, "end": v(202.44, -47.75) * mm});
            skLineSegment(sketch, "E28.0.8.1", {"start": v(197.1, -42.67) * mm, "end": v(192.02, -42.67) * mm});
            skLineSegment(sketch, "E28.0.8.2", {"start": v(181.36, -47.75) * mm, "end": v(186.44, -47.75) * mm});
            skLineSegment(sketch, "E28.0.8.3", {"start": v(202.44, -42.67) * mm, "end": v(197.36, -42.67) * mm});
            skLineSegment(sketch, "E28.0.8.4", {"start": v(192.02, -42.67) * mm, "end": v(192.02, -47.75) * mm});
            skLineSegment(sketch, "E28.0.8.5", {"start": v(191.77, -47.75) * mm, "end": v(191.77, -42.67) * mm});
            skLineSegment(sketch, "E28.0.8.6", {"start": v(197.36, -42.67) * mm, "end": v(197.36, -47.75) * mm});
            skLineSegment(sketch, "E28.0.8.7", {"start": v(192.02, -47.75) * mm, "end": v(197.1, -47.75) * mm});
            skLineSegment(sketch, "E28.0.8.8", {"start": v(191.77, -42.67) * mm, "end": v(186.7, -42.67) * mm});
            skLineSegment(sketch, "E28.0.8.9", {"start": v(202.44, -47.75) * mm, "end": v(202.44, -42.67) * mm});
            skLineSegment(sketch, "E28.0.8.10", {"start": v(186.44, -47.75) * mm, "end": v(186.44, -42.67) * mm});
            skLineSegment(sketch, "E28.0.8.11", {"start": v(186.7, -47.75) * mm, "end": v(191.77, -47.75) * mm});
            skLineSegment(sketch, "E28.0.8.12", {"start": v(186.44, -42.67) * mm, "end": v(181.36, -42.67) * mm});
            skLineSegment(sketch, "E28.0.8.13", {"start": v(197.1, -47.75) * mm, "end": v(197.1, -42.67) * mm});
            skLineSegment(sketch, "E28.0.8.14", {"start": v(181.36, -42.67) * mm, "end": v(181.36, -47.75) * mm});
            skLineSegment(sketch, "E28.0.8.15", {"start": v(186.7, -42.67) * mm, "end": v(186.7, -47.75) * mm});
            skLineSegment(sketch, "E28.0.9.0", {"start": v(197.36, -53.09) * mm, "end": v(202.44, -53.09) * mm});
            skLineSegment(sketch, "E28.0.9.1", {"start": v(197.1, -48) * mm, "end": v(192.02, -48) * mm});
            skLineSegment(sketch, "E28.0.9.2", {"start": v(181.36, -53.09) * mm, "end": v(186.44, -53.09) * mm});
            skLineSegment(sketch, "E28.0.9.3", {"start": v(202.44, -48) * mm, "end": v(197.36, -48) * mm});
            skLineSegment(sketch, "E28.0.9.4", {"start": v(192.02, -48) * mm, "end": v(192.02, -53.09) * mm});
            skLineSegment(sketch, "E28.0.9.5", {"start": v(191.77, -53.09) * mm, "end": v(191.77, -48) * mm});
            skLineSegment(sketch, "E28.0.9.6", {"start": v(197.36, -48) * mm, "end": v(197.36, -53.09) * mm});
            skLineSegment(sketch, "E28.0.9.7", {"start": v(192.02, -53.09) * mm, "end": v(197.1, -53.09) * mm});
            skLineSegment(sketch, "E28.0.9.8", {"start": v(191.77, -48) * mm, "end": v(186.7, -48) * mm});
            skLineSegment(sketch, "E28.0.9.9", {"start": v(202.44, -53.09) * mm, "end": v(202.44, -48) * mm});
            skLineSegment(sketch, "E28.0.9.10", {"start": v(186.44, -53.09) * mm, "end": v(186.44, -48) * mm});
            skLineSegment(sketch, "E28.0.9.11", {"start": v(186.7, -53.09) * mm, "end": v(191.77, -53.09) * mm});
            skLineSegment(sketch, "E28.0.9.12", {"start": v(186.44, -48) * mm, "end": v(181.36, -48) * mm});
            skLineSegment(sketch, "E28.0.9.13", {"start": v(197.1, -53.09) * mm, "end": v(197.1, -48) * mm});
            skLineSegment(sketch, "E28.0.9.14", {"start": v(181.36, -48) * mm, "end": v(181.36, -53.09) * mm});
            skLineSegment(sketch, "E28.0.9.15", {"start": v(186.7, -48) * mm, "end": v(186.7, -53.09) * mm});
            skLineSegment(sketch, "E28.0.10.0", {"start": v(197.36, -58.42) * mm, "end": v(202.44, -58.42) * mm});
            skLineSegment(sketch, "E28.0.10.1", {"start": v(197.1, -53.34) * mm, "end": v(192.02, -53.34) * mm});
            skLineSegment(sketch, "E28.0.10.2", {"start": v(181.36, -58.42) * mm, "end": v(186.44, -58.42) * mm});
            skLineSegment(sketch, "E28.0.10.3", {"start": v(202.44, -53.34) * mm, "end": v(197.36, -53.34) * mm});
            skLineSegment(sketch, "E28.0.10.4", {"start": v(192.02, -53.34) * mm, "end": v(192.02, -58.42) * mm});
            skLineSegment(sketch, "E28.0.10.5", {"start": v(191.77, -58.42) * mm, "end": v(191.77, -53.34) * mm});
            skLineSegment(sketch, "E28.0.10.6", {"start": v(197.36, -53.34) * mm, "end": v(197.36, -58.42) * mm});
            skLineSegment(sketch, "E28.0.10.7", {"start": v(192.02, -58.42) * mm, "end": v(197.1, -58.42) * mm});
            skLineSegment(sketch, "E28.0.10.8", {"start": v(191.77, -53.34) * mm, "end": v(186.7, -53.34) * mm});
            skLineSegment(sketch, "E28.0.10.9", {"start": v(202.44, -58.42) * mm, "end": v(202.44, -53.34) * mm});
            skLineSegment(sketch, "E28.0.10.10", {"start": v(186.44, -58.42) * mm, "end": v(186.44, -53.34) * mm});
            skLineSegment(sketch, "E28.0.10.11", {"start": v(186.7, -58.42) * mm, "end": v(191.77, -58.42) * mm});
            skLineSegment(sketch, "E28.0.10.12", {"start": v(186.44, -53.34) * mm, "end": v(181.36, -53.34) * mm});
            skLineSegment(sketch, "E28.0.10.13", {"start": v(197.1, -58.42) * mm, "end": v(197.1, -53.34) * mm});
            skLineSegment(sketch, "E28.0.10.14", {"start": v(181.36, -53.34) * mm, "end": v(181.36, -58.42) * mm});
            skLineSegment(sketch, "E28.0.10.15", {"start": v(186.7, -53.34) * mm, "end": v(186.7, -58.42) * mm});
            skLineSegment(sketch, "E28.0.11.0", {"start": v(197.36, -63.75) * mm, "end": v(202.44, -63.75) * mm});
            skLineSegment(sketch, "E28.0.11.1", {"start": v(197.1, -58.67) * mm, "end": v(192.02, -58.67) * mm});
            skLineSegment(sketch, "E28.0.11.2", {"start": v(181.36, -63.75) * mm, "end": v(186.44, -63.75) * mm});
            skLineSegment(sketch, "E28.0.11.3", {"start": v(202.44, -58.67) * mm, "end": v(197.36, -58.67) * mm});
            skLineSegment(sketch, "E28.0.11.4", {"start": v(192.02, -58.67) * mm, "end": v(192.02, -63.75) * mm});
            skLineSegment(sketch, "E28.0.11.5", {"start": v(191.77, -63.75) * mm, "end": v(191.77, -58.67) * mm});
            skLineSegment(sketch, "E28.0.11.6", {"start": v(197.36, -58.67) * mm, "end": v(197.36, -63.75) * mm});
            skLineSegment(sketch, "E28.0.11.7", {"start": v(192.02, -63.75) * mm, "end": v(197.1, -63.75) * mm});
            skLineSegment(sketch, "E28.0.11.8", {"start": v(191.77, -58.67) * mm, "end": v(186.7, -58.67) * mm});
            skLineSegment(sketch, "E28.0.11.9", {"start": v(202.44, -63.75) * mm, "end": v(202.44, -58.67) * mm});
            skLineSegment(sketch, "E28.0.11.10", {"start": v(186.44, -63.75) * mm, "end": v(186.44, -58.67) * mm});
            skLineSegment(sketch, "E28.0.11.11", {"start": v(186.7, -63.75) * mm, "end": v(191.77, -63.75) * mm});
            skLineSegment(sketch, "E28.0.11.12", {"start": v(186.44, -58.67) * mm, "end": v(181.36, -58.67) * mm});
            skLineSegment(sketch, "E28.0.11.13", {"start": v(197.1, -63.75) * mm, "end": v(197.1, -58.67) * mm});
            skLineSegment(sketch, "E28.0.11.14", {"start": v(181.36, -58.67) * mm, "end": v(181.36, -63.75) * mm});
            skLineSegment(sketch, "E28.0.11.15", {"start": v(186.7, -58.67) * mm, "end": v(186.7, -63.75) * mm});
            skLineSegment(sketch, "E28.0.12.0", {"start": v(197.36, -69.09) * mm, "end": v(202.44, -69.09) * mm});
            skLineSegment(sketch, "E28.0.12.1", {"start": v(197.1, -64) * mm, "end": v(192.02, -64) * mm});
            skLineSegment(sketch, "E28.0.12.2", {"start": v(181.36, -69.09) * mm, "end": v(186.44, -69.09) * mm});
            skLineSegment(sketch, "E28.0.12.3", {"start": v(202.44, -64) * mm, "end": v(197.36, -64) * mm});
            skLineSegment(sketch, "E28.0.12.4", {"start": v(192.02, -64) * mm, "end": v(192.02, -69.09) * mm});
            skLineSegment(sketch, "E28.0.12.5", {"start": v(191.77, -69.09) * mm, "end": v(191.77, -64) * mm});
            skLineSegment(sketch, "E28.0.12.6", {"start": v(197.36, -64) * mm, "end": v(197.36, -69.09) * mm});
            skLineSegment(sketch, "E28.0.12.7", {"start": v(192.02, -69.09) * mm, "end": v(197.1, -69.09) * mm});
            skLineSegment(sketch, "E28.0.12.8", {"start": v(191.77, -64) * mm, "end": v(186.7, -64) * mm});
            skLineSegment(sketch, "E28.0.12.9", {"start": v(202.44, -69.09) * mm, "end": v(202.44, -64) * mm});
            skLineSegment(sketch, "E28.0.12.10", {"start": v(186.44, -69.09) * mm, "end": v(186.44, -64) * mm});
            skLineSegment(sketch, "E28.0.12.11", {"start": v(186.7, -69.09) * mm, "end": v(191.77, -69.09) * mm});
            skLineSegment(sketch, "E28.0.12.12", {"start": v(186.44, -64) * mm, "end": v(181.36, -64) * mm});
            skLineSegment(sketch, "E28.0.12.13", {"start": v(197.1, -69.09) * mm, "end": v(197.1, -64) * mm});
            skLineSegment(sketch, "E28.0.12.14", {"start": v(181.36, -64) * mm, "end": v(181.36, -69.09) * mm});
            skLineSegment(sketch, "E28.0.12.15", {"start": v(186.7, -64) * mm, "end": v(186.7, -69.09) * mm});
            skLineSegment(sketch, "E28.0.13.0", {"start": v(197.36, -74.42) * mm, "end": v(202.44, -74.42) * mm});
            skLineSegment(sketch, "E28.0.13.1", {"start": v(197.1, -69.34) * mm, "end": v(192.02, -69.34) * mm});
            skLineSegment(sketch, "E28.0.13.2", {"start": v(181.36, -74.42) * mm, "end": v(186.44, -74.42) * mm});
            skLineSegment(sketch, "E28.0.13.3", {"start": v(202.44, -69.34) * mm, "end": v(197.36, -69.34) * mm});
            skLineSegment(sketch, "E28.0.13.4", {"start": v(192.02, -69.34) * mm, "end": v(192.02, -74.42) * mm});
            skLineSegment(sketch, "E28.0.13.5", {"start": v(191.77, -74.42) * mm, "end": v(191.77, -69.34) * mm});
            skLineSegment(sketch, "E28.0.13.6", {"start": v(197.36, -69.34) * mm, "end": v(197.36, -74.42) * mm});
            skLineSegment(sketch, "E28.0.13.7", {"start": v(192.02, -74.42) * mm, "end": v(197.1, -74.42) * mm});
            skLineSegment(sketch, "E28.0.13.8", {"start": v(191.77, -69.34) * mm, "end": v(186.7, -69.34) * mm});
            skLineSegment(sketch, "E28.0.13.9", {"start": v(202.44, -74.42) * mm, "end": v(202.44, -69.34) * mm});
            skLineSegment(sketch, "E28.0.13.10", {"start": v(186.44, -74.42) * mm, "end": v(186.44, -69.34) * mm});
            skLineSegment(sketch, "E28.0.13.11", {"start": v(186.7, -74.42) * mm, "end": v(191.77, -74.42) * mm});
            skLineSegment(sketch, "E28.0.13.12", {"start": v(186.44, -69.34) * mm, "end": v(181.36, -69.34) * mm});
            skLineSegment(sketch, "E28.0.13.13", {"start": v(197.1, -74.42) * mm, "end": v(197.1, -69.34) * mm});
            skLineSegment(sketch, "E28.0.13.14", {"start": v(181.36, -69.34) * mm, "end": v(181.36, -74.42) * mm});
            skLineSegment(sketch, "E28.0.13.15", {"start": v(186.7, -69.34) * mm, "end": v(186.7, -74.42) * mm});
            skLineSegment(sketch, "E28.0.14.0", {"start": v(197.36, -79.76) * mm, "end": v(202.44, -79.76) * mm});
            skLineSegment(sketch, "E28.0.14.1", {"start": v(197.1, -74.68) * mm, "end": v(192.02, -74.68) * mm});
            skLineSegment(sketch, "E28.0.14.2", {"start": v(181.36, -79.76) * mm, "end": v(186.44, -79.76) * mm});
            skLineSegment(sketch, "E28.0.14.3", {"start": v(202.44, -74.68) * mm, "end": v(197.36, -74.68) * mm});
            skLineSegment(sketch, "E28.0.14.4", {"start": v(192.02, -74.68) * mm, "end": v(192.02, -79.76) * mm});
            skLineSegment(sketch, "E28.0.14.5", {"start": v(191.77, -79.76) * mm, "end": v(191.77, -74.68) * mm});
            skLineSegment(sketch, "E28.0.14.6", {"start": v(197.36, -74.68) * mm, "end": v(197.36, -79.76) * mm});
            skLineSegment(sketch, "E28.0.14.7", {"start": v(192.02, -79.76) * mm, "end": v(197.1, -79.76) * mm});
            skLineSegment(sketch, "E28.0.14.8", {"start": v(191.77, -74.68) * mm, "end": v(186.7, -74.68) * mm});
            skLineSegment(sketch, "E28.0.14.9", {"start": v(202.44, -79.76) * mm, "end": v(202.44, -74.68) * mm});
            skLineSegment(sketch, "E28.0.14.10", {"start": v(186.44, -79.76) * mm, "end": v(186.44, -74.68) * mm});
            skLineSegment(sketch, "E28.0.14.11", {"start": v(186.7, -79.76) * mm, "end": v(191.77, -79.76) * mm});
            skLineSegment(sketch, "E28.0.14.12", {"start": v(186.44, -74.68) * mm, "end": v(181.36, -74.68) * mm});
            skLineSegment(sketch, "E28.0.14.13", {"start": v(197.1, -79.76) * mm, "end": v(197.1, -74.68) * mm});
            skLineSegment(sketch, "E28.0.14.14", {"start": v(181.36, -74.68) * mm, "end": v(181.36, -79.76) * mm});
            skLineSegment(sketch, "E28.0.14.15", {"start": v(186.7, -74.68) * mm, "end": v(186.7, -79.76) * mm});
            skLineSegment(sketch, "E28.0.15.0", {"start": v(197.36, -85.1) * mm, "end": v(202.44, -85.1) * mm});
            skLineSegment(sketch, "E28.0.15.1", {"start": v(197.1, -80.01) * mm, "end": v(192.02, -80.01) * mm});
            skLineSegment(sketch, "E28.0.15.2", {"start": v(181.36, -85.1) * mm, "end": v(186.44, -85.1) * mm});
            skLineSegment(sketch, "E28.0.15.3", {"start": v(202.44, -80.01) * mm, "end": v(197.36, -80.01) * mm});
            skLineSegment(sketch, "E28.0.15.4", {"start": v(192.02, -80.01) * mm, "end": v(192.02, -85.1) * mm});
            skLineSegment(sketch, "E28.0.15.5", {"start": v(191.77, -85.1) * mm, "end": v(191.77, -80.01) * mm});
            skLineSegment(sketch, "E28.0.15.6", {"start": v(197.36, -80.01) * mm, "end": v(197.36, -85.1) * mm});
            skLineSegment(sketch, "E28.0.15.7", {"start": v(192.02, -85.1) * mm, "end": v(197.1, -85.1) * mm});
            skLineSegment(sketch, "E28.0.15.8", {"start": v(191.77, -80.01) * mm, "end": v(186.7, -80.01) * mm});
            skLineSegment(sketch, "E28.0.15.9", {"start": v(202.44, -85.1) * mm, "end": v(202.44, -80.01) * mm});
            skLineSegment(sketch, "E28.0.15.10", {"start": v(186.44, -85.1) * mm, "end": v(186.44, -80.01) * mm});
            skLineSegment(sketch, "E28.0.15.11", {"start": v(186.7, -85.1) * mm, "end": v(191.77, -85.1) * mm});
            skLineSegment(sketch, "E28.0.15.12", {"start": v(186.44, -80.01) * mm, "end": v(181.36, -80.01) * mm});
            skLineSegment(sketch, "E28.0.15.13", {"start": v(197.1, -85.1) * mm, "end": v(197.1, -80.01) * mm});
            skLineSegment(sketch, "E28.0.15.14", {"start": v(181.36, -80.01) * mm, "end": v(181.36, -85.1) * mm});
            skLineSegment(sketch, "E28.0.15.15", {"start": v(186.7, -80.01) * mm, "end": v(186.7, -85.1) * mm});
            skLineSegment(sketch, "E28.0.16.0", {"start": v(197.36, -90.42) * mm, "end": v(202.44, -90.42) * mm});
            skLineSegment(sketch, "E28.0.16.1", {"start": v(197.1, -85.34) * mm, "end": v(192.02, -85.34) * mm});
            skLineSegment(sketch, "E28.0.16.2", {"start": v(181.36, -90.42) * mm, "end": v(186.44, -90.42) * mm});
            skLineSegment(sketch, "E28.0.16.3", {"start": v(202.44, -85.34) * mm, "end": v(197.36, -85.34) * mm});
            skLineSegment(sketch, "E28.0.16.4", {"start": v(192.02, -85.34) * mm, "end": v(192.02, -90.42) * mm});
            skLineSegment(sketch, "E28.0.16.5", {"start": v(191.77, -90.42) * mm, "end": v(191.77, -85.34) * mm});
            skLineSegment(sketch, "E28.0.16.6", {"start": v(197.36, -85.34) * mm, "end": v(197.36, -90.42) * mm});
            skLineSegment(sketch, "E28.0.16.7", {"start": v(192.02, -90.42) * mm, "end": v(197.1, -90.42) * mm});
            skLineSegment(sketch, "E28.0.16.8", {"start": v(191.77, -85.34) * mm, "end": v(186.7, -85.34) * mm});
            skLineSegment(sketch, "E28.0.16.9", {"start": v(202.44, -90.42) * mm, "end": v(202.44, -85.34) * mm});
            skLineSegment(sketch, "E28.0.16.10", {"start": v(186.44, -90.42) * mm, "end": v(186.44, -85.34) * mm});
            skLineSegment(sketch, "E28.0.16.11", {"start": v(186.7, -90.42) * mm, "end": v(191.77, -90.42) * mm});
            skLineSegment(sketch, "E28.0.16.12", {"start": v(186.44, -85.34) * mm, "end": v(181.36, -85.34) * mm});
            skLineSegment(sketch, "E28.0.16.13", {"start": v(197.1, -90.42) * mm, "end": v(197.1, -85.34) * mm});
            skLineSegment(sketch, "E28.0.16.14", {"start": v(181.36, -85.34) * mm, "end": v(181.36, -90.42) * mm});
            skLineSegment(sketch, "E28.0.16.15", {"start": v(186.7, -85.34) * mm, "end": v(186.7, -90.42) * mm});
            skLineSegment(sketch, "E28.0.17.0", {"start": v(197.36, -95.76) * mm, "end": v(202.44, -95.76) * mm});
            skLineSegment(sketch, "E28.0.17.1", {"start": v(197.1, -90.68) * mm, "end": v(192.02, -90.68) * mm});
            skLineSegment(sketch, "E28.0.17.2", {"start": v(181.36, -95.76) * mm, "end": v(186.44, -95.76) * mm});
            skLineSegment(sketch, "E28.0.17.3", {"start": v(202.44, -90.68) * mm, "end": v(197.36, -90.68) * mm});
            skLineSegment(sketch, "E28.0.17.4", {"start": v(192.02, -90.68) * mm, "end": v(192.02, -95.76) * mm});
            skLineSegment(sketch, "E28.0.17.5", {"start": v(191.77, -95.76) * mm, "end": v(191.77, -90.68) * mm});
            skLineSegment(sketch, "E28.0.17.6", {"start": v(197.36, -90.68) * mm, "end": v(197.36, -95.76) * mm});
            skLineSegment(sketch, "E28.0.17.7", {"start": v(192.02, -95.76) * mm, "end": v(197.1, -95.76) * mm});
            skLineSegment(sketch, "E28.0.17.8", {"start": v(191.77, -90.68) * mm, "end": v(186.7, -90.68) * mm});
            skLineSegment(sketch, "E28.0.17.9", {"start": v(202.44, -95.76) * mm, "end": v(202.44, -90.68) * mm});
            skLineSegment(sketch, "E28.0.17.10", {"start": v(186.44, -95.76) * mm, "end": v(186.44, -90.68) * mm});
            skLineSegment(sketch, "E28.0.17.11", {"start": v(186.7, -95.76) * mm, "end": v(191.77, -95.76) * mm});
            skLineSegment(sketch, "E28.0.17.12", {"start": v(186.44, -90.68) * mm, "end": v(181.36, -90.68) * mm});
            skLineSegment(sketch, "E28.0.17.13", {"start": v(197.1, -95.76) * mm, "end": v(197.1, -90.68) * mm});
            skLineSegment(sketch, "E28.0.17.14", {"start": v(181.36, -90.68) * mm, "end": v(181.36, -95.76) * mm});
            skLineSegment(sketch, "E28.0.17.15", {"start": v(186.7, -90.68) * mm, "end": v(186.7, -95.76) * mm});
            skLineSegment(sketch, "E28.0.18.0", {"start": v(197.36, -101.1) * mm, "end": v(202.44, -101.1) * mm});
            skLineSegment(sketch, "E28.0.18.1", {"start": v(197.1, -96.01) * mm, "end": v(192.02, -96.01) * mm});
            skLineSegment(sketch, "E28.0.18.2", {"start": v(181.36, -101.1) * mm, "end": v(186.44, -101.1) * mm});
            skLineSegment(sketch, "E28.0.18.3", {"start": v(202.44, -96.01) * mm, "end": v(197.36, -96.01) * mm});
            skLineSegment(sketch, "E28.0.18.4", {"start": v(192.02, -96.01) * mm, "end": v(192.02, -101.1) * mm});
            skLineSegment(sketch, "E28.0.18.5", {"start": v(191.77, -101.1) * mm, "end": v(191.77, -96.01) * mm});
            skLineSegment(sketch, "E28.0.18.6", {"start": v(197.36, -96.01) * mm, "end": v(197.36, -101.1) * mm});
            skLineSegment(sketch, "E28.0.18.7", {"start": v(192.02, -101.1) * mm, "end": v(197.1, -101.1) * mm});
            skLineSegment(sketch, "E28.0.18.8", {"start": v(191.77, -96.01) * mm, "end": v(186.7, -96.01) * mm});
            skLineSegment(sketch, "E28.0.18.9", {"start": v(202.44, -101.1) * mm, "end": v(202.44, -96.01) * mm});
            skLineSegment(sketch, "E28.0.18.10", {"start": v(186.44, -101.1) * mm, "end": v(186.44, -96.01) * mm});
            skLineSegment(sketch, "E28.0.18.11", {"start": v(186.7, -101.1) * mm, "end": v(191.77, -101.1) * mm});
            skLineSegment(sketch, "E28.0.18.12", {"start": v(186.44, -96.01) * mm, "end": v(181.36, -96.01) * mm});
            skLineSegment(sketch, "E28.0.18.13", {"start": v(197.1, -101.1) * mm, "end": v(197.1, -96.01) * mm});
            skLineSegment(sketch, "E28.0.18.14", {"start": v(181.36, -96.01) * mm, "end": v(181.36, -101.1) * mm});
            skLineSegment(sketch, "E28.0.18.15", {"start": v(186.7, -96.01) * mm, "end": v(186.7, -101.1) * mm});
            skLineSegment(sketch, "E28.0.19.0", {"start": v(197.36, -106.43) * mm, "end": v(202.44, -106.43) * mm});
            skLineSegment(sketch, "E28.0.19.1", {"start": v(197.1, -101.35) * mm, "end": v(192.02, -101.35) * mm});
            skLineSegment(sketch, "E28.0.19.2", {"start": v(181.36, -106.43) * mm, "end": v(186.44, -106.43) * mm});
            skLineSegment(sketch, "E28.0.19.3", {"start": v(202.44, -101.35) * mm, "end": v(197.36, -101.35) * mm});
            skLineSegment(sketch, "E28.0.19.4", {"start": v(192.02, -101.35) * mm, "end": v(192.02, -106.43) * mm});
            skLineSegment(sketch, "E28.0.19.5", {"start": v(191.77, -106.43) * mm, "end": v(191.77, -101.35) * mm});
            skLineSegment(sketch, "E28.0.19.6", {"start": v(197.36, -101.35) * mm, "end": v(197.36, -106.43) * mm});
            skLineSegment(sketch, "E28.0.19.7", {"start": v(192.02, -106.43) * mm, "end": v(197.1, -106.43) * mm});
            skLineSegment(sketch, "E28.0.19.8", {"start": v(191.77, -101.35) * mm, "end": v(186.7, -101.35) * mm});
            skLineSegment(sketch, "E28.0.19.9", {"start": v(202.44, -106.43) * mm, "end": v(202.44, -101.35) * mm});
            skLineSegment(sketch, "E28.0.19.10", {"start": v(186.44, -106.43) * mm, "end": v(186.44, -101.35) * mm});
            skLineSegment(sketch, "E28.0.19.11", {"start": v(186.7, -106.43) * mm, "end": v(191.77, -106.43) * mm});
            skLineSegment(sketch, "E28.0.19.12", {"start": v(186.44, -101.35) * mm, "end": v(181.36, -101.35) * mm});
            skLineSegment(sketch, "E28.0.19.13", {"start": v(197.1, -106.43) * mm, "end": v(197.1, -101.35) * mm});
            skLineSegment(sketch, "E28.0.19.14", {"start": v(181.36, -101.35) * mm, "end": v(181.36, -106.43) * mm});
            skLineSegment(sketch, "E28.0.19.15", {"start": v(186.7, -101.35) * mm, "end": v(186.7, -106.43) * mm});
            skLineSegment(sketch, "E28.0.20.0", {"start": v(197.36, -111.76) * mm, "end": v(202.44, -111.76) * mm});
            skLineSegment(sketch, "E28.0.20.1", {"start": v(197.1, -106.68) * mm, "end": v(192.02, -106.68) * mm});
            skLineSegment(sketch, "E28.0.20.2", {"start": v(181.36, -111.76) * mm, "end": v(186.44, -111.76) * mm});
            skLineSegment(sketch, "E28.0.20.3", {"start": v(202.44, -106.68) * mm, "end": v(197.36, -106.68) * mm});
            skLineSegment(sketch, "E28.0.20.4", {"start": v(192.02, -106.68) * mm, "end": v(192.02, -111.76) * mm});
            skLineSegment(sketch, "E28.0.20.5", {"start": v(191.77, -111.76) * mm, "end": v(191.77, -106.68) * mm});
            skLineSegment(sketch, "E28.0.20.6", {"start": v(197.36, -106.68) * mm, "end": v(197.36, -111.76) * mm});
            skLineSegment(sketch, "E28.0.20.7", {"start": v(192.02, -111.76) * mm, "end": v(197.1, -111.76) * mm});
            skLineSegment(sketch, "E28.0.20.8", {"start": v(191.77, -106.68) * mm, "end": v(186.7, -106.68) * mm});
            skLineSegment(sketch, "E28.0.20.9", {"start": v(202.44, -111.76) * mm, "end": v(202.44, -106.68) * mm});
            skLineSegment(sketch, "E28.0.20.10", {"start": v(186.44, -111.76) * mm, "end": v(186.44, -106.68) * mm});
            skLineSegment(sketch, "E28.0.20.11", {"start": v(186.7, -111.76) * mm, "end": v(191.77, -111.76) * mm});
            skLineSegment(sketch, "E28.0.20.12", {"start": v(186.44, -106.68) * mm, "end": v(181.36, -106.68) * mm});
            skLineSegment(sketch, "E28.0.20.13", {"start": v(197.1, -111.76) * mm, "end": v(197.1, -106.68) * mm});
            skLineSegment(sketch, "E28.0.20.14", {"start": v(181.36, -106.68) * mm, "end": v(181.36, -111.76) * mm});
            skLineSegment(sketch, "E28.0.20.15", {"start": v(186.7, -106.68) * mm, "end": v(186.7, -111.76) * mm});
            skLineSegment(sketch, "E28.0.21.0", {"start": v(197.36, -117.1) * mm, "end": v(202.44, -117.1) * mm});
            skLineSegment(sketch, "E28.0.21.1", {"start": v(197.1, -112.01) * mm, "end": v(192.02, -112.01) * mm});
            skLineSegment(sketch, "E28.0.21.2", {"start": v(181.36, -117.1) * mm, "end": v(186.44, -117.1) * mm});
            skLineSegment(sketch, "E28.0.21.3", {"start": v(202.44, -112.01) * mm, "end": v(197.36, -112.01) * mm});
            skLineSegment(sketch, "E28.0.21.4", {"start": v(192.02, -112.01) * mm, "end": v(192.02, -117.1) * mm});
            skLineSegment(sketch, "E28.0.21.5", {"start": v(191.77, -117.1) * mm, "end": v(191.77, -112.01) * mm});
            skLineSegment(sketch, "E28.0.21.6", {"start": v(197.36, -112.01) * mm, "end": v(197.36, -117.1) * mm});
            skLineSegment(sketch, "E28.0.21.7", {"start": v(192.02, -117.1) * mm, "end": v(197.1, -117.1) * mm});
            skLineSegment(sketch, "E28.0.21.8", {"start": v(191.77, -112.01) * mm, "end": v(186.7, -112.01) * mm});
            skLineSegment(sketch, "E28.0.21.9", {"start": v(202.44, -117.1) * mm, "end": v(202.44, -112.01) * mm});
            skLineSegment(sketch, "E28.0.21.10", {"start": v(186.44, -117.1) * mm, "end": v(186.44, -112.01) * mm});
            skLineSegment(sketch, "E28.0.21.11", {"start": v(186.7, -117.1) * mm, "end": v(191.77, -117.1) * mm});
            skLineSegment(sketch, "E28.0.21.12", {"start": v(186.44, -112.01) * mm, "end": v(181.36, -112.01) * mm});
            skLineSegment(sketch, "E28.0.21.13", {"start": v(197.1, -117.1) * mm, "end": v(197.1, -112.01) * mm});
            skLineSegment(sketch, "E28.0.21.14", {"start": v(181.36, -112.01) * mm, "end": v(181.36, -117.1) * mm});
            skLineSegment(sketch, "E28.0.21.15", {"start": v(186.7, -112.01) * mm, "end": v(186.7, -117.1) * mm});
            skLineSegment(sketch, "E28.direction1", {"start": v(181.36, -5.08) * mm, "end": v(206.76, -5.08) * mm, "construction": true});
            skLineSegment(sketch, "E28.direction2", {"start": v(181.36, -5.08) * mm, "end": v(181.36, -10.41) * mm, "construction": true});
            skSolve(sketch);
        }
        {
            var Q0;
            Q0=qCreatedBy(makeId("Top.planeOp"),FACE);
            var sketch = newSketch(context, id + "F10", { "sketchPlane" : qUnion([Q0])});
            skLineSegment(sketch, "E29.0.0", {"start": v(207.77, -5.08) * mm, "end": v(207.77, 0) * mm});
            skLineSegment(sketch, "E29.0.1", {"start": v(207.77, 0) * mm, "end": v(202.7, 0) * mm});
            skLineSegment(sketch, "E29.0.2", {"start": v(202.7, 0) * mm, "end": v(202.7, -5.08) * mm});
            skLineSegment(sketch, "E29.0.3", {"start": v(202.7, -5.08) * mm, "end": v(207.77, -5.08) * mm});
            skLineSegment(sketch, "E29.1.0", {"start": v(213.1, -5.08) * mm, "end": v(213.1, 0) * mm});
            skLineSegment(sketch, "E29.1.1", {"start": v(213.1, 0) * mm, "end": v(208.03, 0) * mm});
            skLineSegment(sketch, "E29.1.2", {"start": v(208.03, 0) * mm, "end": v(208.03, -5.08) * mm});
            skLineSegment(sketch, "E29.1.3", {"start": v(208.03, -5.08) * mm, "end": v(213.1, -5.08) * mm});
            skLineSegment(sketch, "E29.2.0", {"start": v(218.44, -5.08) * mm, "end": v(218.44, 0) * mm});
            skLineSegment(sketch, "E29.2.1", {"start": v(218.44, 0) * mm, "end": v(213.36, 0) * mm});
            skLineSegment(sketch, "E29.2.2", {"start": v(213.36, 0) * mm, "end": v(213.36, -5.08) * mm});
            skLineSegment(sketch, "E29.2.3", {"start": v(213.36, -5.08) * mm, "end": v(218.44, -5.08) * mm});
            skLineSegment(sketch, "E29.3.0", {"start": v(223.77, -5.08) * mm, "end": v(223.77, 0) * mm});
            skLineSegment(sketch, "E29.3.1", {"start": v(223.77, 0) * mm, "end": v(218.7, 0) * mm});
            skLineSegment(sketch, "E29.3.2", {"start": v(218.7, 0) * mm, "end": v(218.7, -5.08) * mm});
            skLineSegment(sketch, "E29.3.3", {"start": v(218.7, -5.08) * mm, "end": v(223.77, -5.08) * mm});
            skLineSegment(sketch, "E30.0.1.0", {"start": v(202.7, -10.41) * mm, "end": v(207.77, -10.41) * mm});
            skLineSegment(sketch, "E30.0.1.1", {"start": v(223.77, -5.33) * mm, "end": v(218.7, -5.33) * mm});
            skLineSegment(sketch, "E30.0.1.2", {"start": v(213.36, -5.33) * mm, "end": v(213.36, -10.41) * mm});
            skLineSegment(sketch, "E30.0.1.3", {"start": v(213.1, -10.41) * mm, "end": v(213.1, -5.33) * mm});
            skLineSegment(sketch, "E30.0.1.4", {"start": v(218.7, -5.33) * mm, "end": v(218.7, -10.41) * mm});
            skLineSegment(sketch, "E30.0.1.5", {"start": v(213.36, -10.41) * mm, "end": v(218.44, -10.41) * mm});
            skLineSegment(sketch, "E30.0.1.6", {"start": v(213.1, -5.33) * mm, "end": v(208.03, -5.33) * mm});
            skLineSegment(sketch, "E30.0.1.7", {"start": v(223.77, -10.41) * mm, "end": v(223.77, -5.33) * mm});
            skLineSegment(sketch, "E30.0.1.8", {"start": v(208.03, -5.33) * mm, "end": v(208.03, -10.41) * mm});
            skLineSegment(sketch, "E30.0.1.9", {"start": v(207.77, -10.41) * mm, "end": v(207.77, -5.33) * mm});
            skLineSegment(sketch, "E30.0.1.10", {"start": v(208.03, -10.41) * mm, "end": v(213.1, -10.41) * mm});
            skLineSegment(sketch, "E30.0.1.11", {"start": v(207.77, -5.33) * mm, "end": v(202.7, -5.33) * mm});
            skLineSegment(sketch, "E30.0.1.12", {"start": v(218.44, -10.41) * mm, "end": v(218.44, -5.33) * mm});
            skLineSegment(sketch, "E30.0.1.13", {"start": v(202.7, -5.33) * mm, "end": v(202.7, -10.41) * mm});
            skLineSegment(sketch, "E30.0.1.14", {"start": v(218.7, -10.41) * mm, "end": v(223.77, -10.41) * mm});
            skLineSegment(sketch, "E30.0.1.15", {"start": v(218.44, -5.33) * mm, "end": v(213.36, -5.33) * mm});
            skLineSegment(sketch, "E30.0.2.0", {"start": v(202.7, -15.75) * mm, "end": v(207.77, -15.75) * mm});
            skLineSegment(sketch, "E30.0.2.1", {"start": v(223.77, -10.67) * mm, "end": v(218.7, -10.67) * mm});
            skLineSegment(sketch, "E30.0.2.2", {"start": v(213.36, -10.67) * mm, "end": v(213.36, -15.75) * mm});
            skLineSegment(sketch, "E30.0.2.3", {"start": v(213.1, -15.75) * mm, "end": v(213.1, -10.67) * mm});
            skLineSegment(sketch, "E30.0.2.4", {"start": v(218.7, -10.67) * mm, "end": v(218.7, -15.75) * mm});
            skLineSegment(sketch, "E30.0.2.5", {"start": v(213.36, -15.75) * mm, "end": v(218.44, -15.75) * mm});
            skLineSegment(sketch, "E30.0.2.6", {"start": v(213.1, -10.67) * mm, "end": v(208.03, -10.67) * mm});
            skLineSegment(sketch, "E30.0.2.7", {"start": v(223.77, -15.75) * mm, "end": v(223.77, -10.67) * mm});
            skLineSegment(sketch, "E30.0.2.8", {"start": v(208.03, -10.67) * mm, "end": v(208.03, -15.75) * mm});
            skLineSegment(sketch, "E30.0.2.9", {"start": v(207.77, -15.75) * mm, "end": v(207.77, -10.67) * mm});
            skLineSegment(sketch, "E30.0.2.10", {"start": v(208.03, -15.75) * mm, "end": v(213.1, -15.75) * mm});
            skLineSegment(sketch, "E30.0.2.11", {"start": v(207.77, -10.67) * mm, "end": v(202.7, -10.67) * mm});
            skLineSegment(sketch, "E30.0.2.12", {"start": v(218.44, -15.75) * mm, "end": v(218.44, -10.67) * mm});
            skLineSegment(sketch, "E30.0.2.13", {"start": v(202.7, -10.67) * mm, "end": v(202.7, -15.75) * mm});
            skLineSegment(sketch, "E30.0.2.14", {"start": v(218.7, -15.75) * mm, "end": v(223.77, -15.75) * mm});
            skLineSegment(sketch, "E30.0.2.15", {"start": v(218.44, -10.67) * mm, "end": v(213.36, -10.67) * mm});
            skLineSegment(sketch, "E30.0.3.0", {"start": v(202.7, -21.08) * mm, "end": v(207.77, -21.08) * mm});
            skLineSegment(sketch, "E30.0.3.1", {"start": v(223.77, -16) * mm, "end": v(218.7, -16) * mm});
            skLineSegment(sketch, "E30.0.3.2", {"start": v(213.36, -16) * mm, "end": v(213.36, -21.08) * mm});
            skLineSegment(sketch, "E30.0.3.3", {"start": v(213.1, -21.08) * mm, "end": v(213.1, -16) * mm});
            skLineSegment(sketch, "E30.0.3.4", {"start": v(218.7, -16) * mm, "end": v(218.7, -21.08) * mm});
            skLineSegment(sketch, "E30.0.3.5", {"start": v(213.36, -21.08) * mm, "end": v(218.44, -21.08) * mm});
            skLineSegment(sketch, "E30.0.3.6", {"start": v(213.1, -16) * mm, "end": v(208.03, -16) * mm});
            skLineSegment(sketch, "E30.0.3.7", {"start": v(223.77, -21.08) * mm, "end": v(223.77, -16) * mm});
            skLineSegment(sketch, "E30.0.3.8", {"start": v(208.03, -16) * mm, "end": v(208.03, -21.08) * mm});
            skLineSegment(sketch, "E30.0.3.9", {"start": v(207.77, -21.08) * mm, "end": v(207.77, -16) * mm});
            skLineSegment(sketch, "E30.0.3.10", {"start": v(208.03, -21.08) * mm, "end": v(213.1, -21.08) * mm});
            skLineSegment(sketch, "E30.0.3.11", {"start": v(207.77, -16) * mm, "end": v(202.7, -16) * mm});
            skLineSegment(sketch, "E30.0.3.12", {"start": v(218.44, -21.08) * mm, "end": v(218.44, -16) * mm});
            skLineSegment(sketch, "E30.0.3.13", {"start": v(202.7, -16) * mm, "end": v(202.7, -21.08) * mm});
            skLineSegment(sketch, "E30.0.3.14", {"start": v(218.7, -21.08) * mm, "end": v(223.77, -21.08) * mm});
            skLineSegment(sketch, "E30.0.3.15", {"start": v(218.44, -16) * mm, "end": v(213.36, -16) * mm});
            skLineSegment(sketch, "E30.0.4.0", {"start": v(202.7, -26.42) * mm, "end": v(207.77, -26.42) * mm});
            skLineSegment(sketch, "E30.0.4.1", {"start": v(223.77, -21.34) * mm, "end": v(218.7, -21.34) * mm});
            skLineSegment(sketch, "E30.0.4.2", {"start": v(213.36, -21.34) * mm, "end": v(213.36, -26.42) * mm});
            skLineSegment(sketch, "E30.0.4.3", {"start": v(213.1, -26.42) * mm, "end": v(213.1, -21.34) * mm});
            skLineSegment(sketch, "E30.0.4.4", {"start": v(218.7, -21.34) * mm, "end": v(218.7, -26.42) * mm});
            skLineSegment(sketch, "E30.0.4.5", {"start": v(213.36, -26.42) * mm, "end": v(218.44, -26.42) * mm});
            skLineSegment(sketch, "E30.0.4.6", {"start": v(213.1, -21.34) * mm, "end": v(208.03, -21.34) * mm});
            skLineSegment(sketch, "E30.0.4.7", {"start": v(223.77, -26.42) * mm, "end": v(223.77, -21.34) * mm});
            skLineSegment(sketch, "E30.0.4.8", {"start": v(208.03, -21.34) * mm, "end": v(208.03, -26.42) * mm});
            skLineSegment(sketch, "E30.0.4.9", {"start": v(207.77, -26.42) * mm, "end": v(207.77, -21.34) * mm});
            skLineSegment(sketch, "E30.0.4.10", {"start": v(208.03, -26.42) * mm, "end": v(213.1, -26.42) * mm});
            skLineSegment(sketch, "E30.0.4.11", {"start": v(207.77, -21.34) * mm, "end": v(202.7, -21.34) * mm});
            skLineSegment(sketch, "E30.0.4.12", {"start": v(218.44, -26.42) * mm, "end": v(218.44, -21.34) * mm});
            skLineSegment(sketch, "E30.0.4.13", {"start": v(202.7, -21.34) * mm, "end": v(202.7, -26.42) * mm});
            skLineSegment(sketch, "E30.0.4.14", {"start": v(218.7, -26.42) * mm, "end": v(223.77, -26.42) * mm});
            skLineSegment(sketch, "E30.0.4.15", {"start": v(218.44, -21.34) * mm, "end": v(213.36, -21.34) * mm});
            skLineSegment(sketch, "E30.0.5.0", {"start": v(202.7, -31.75) * mm, "end": v(207.77, -31.75) * mm});
            skLineSegment(sketch, "E30.0.5.1", {"start": v(223.77, -26.67) * mm, "end": v(218.7, -26.67) * mm});
            skLineSegment(sketch, "E30.0.5.2", {"start": v(213.36, -26.67) * mm, "end": v(213.36, -31.75) * mm});
            skLineSegment(sketch, "E30.0.5.3", {"start": v(213.1, -31.75) * mm, "end": v(213.1, -26.67) * mm});
            skLineSegment(sketch, "E30.0.5.4", {"start": v(218.7, -26.67) * mm, "end": v(218.7, -31.75) * mm});
            skLineSegment(sketch, "E30.0.5.5", {"start": v(213.36, -31.75) * mm, "end": v(218.44, -31.75) * mm});
            skLineSegment(sketch, "E30.0.5.6", {"start": v(213.1, -26.67) * mm, "end": v(208.03, -26.67) * mm});
            skLineSegment(sketch, "E30.0.5.7", {"start": v(223.77, -31.75) * mm, "end": v(223.77, -26.67) * mm});
            skLineSegment(sketch, "E30.0.5.8", {"start": v(208.03, -26.67) * mm, "end": v(208.03, -31.75) * mm});
            skLineSegment(sketch, "E30.0.5.9", {"start": v(207.77, -31.75) * mm, "end": v(207.77, -26.67) * mm});
            skLineSegment(sketch, "E30.0.5.10", {"start": v(208.03, -31.75) * mm, "end": v(213.1, -31.75) * mm});
            skLineSegment(sketch, "E30.0.5.11", {"start": v(207.77, -26.67) * mm, "end": v(202.7, -26.67) * mm});
            skLineSegment(sketch, "E30.0.5.12", {"start": v(218.44, -31.75) * mm, "end": v(218.44, -26.67) * mm});
            skLineSegment(sketch, "E30.0.5.13", {"start": v(202.7, -26.67) * mm, "end": v(202.7, -31.75) * mm});
            skLineSegment(sketch, "E30.0.5.14", {"start": v(218.7, -31.75) * mm, "end": v(223.77, -31.75) * mm});
            skLineSegment(sketch, "E30.0.5.15", {"start": v(218.44, -26.67) * mm, "end": v(213.36, -26.67) * mm});
            skLineSegment(sketch, "E30.0.6.0", {"start": v(202.7, -37.08) * mm, "end": v(207.77, -37.08) * mm});
            skLineSegment(sketch, "E30.0.6.1", {"start": v(223.77, -32) * mm, "end": v(218.7, -32) * mm});
            skLineSegment(sketch, "E30.0.6.2", {"start": v(213.36, -32) * mm, "end": v(213.36, -37.08) * mm});
            skLineSegment(sketch, "E30.0.6.3", {"start": v(213.1, -37.08) * mm, "end": v(213.1, -32) * mm});
            skLineSegment(sketch, "E30.0.6.4", {"start": v(218.7, -32) * mm, "end": v(218.7, -37.08) * mm});
            skLineSegment(sketch, "E30.0.6.5", {"start": v(213.36, -37.08) * mm, "end": v(218.44, -37.08) * mm});
            skLineSegment(sketch, "E30.0.6.6", {"start": v(213.1, -32) * mm, "end": v(208.03, -32) * mm});
            skLineSegment(sketch, "E30.0.6.7", {"start": v(223.77, -37.08) * mm, "end": v(223.77, -32) * mm});
            skLineSegment(sketch, "E30.0.6.8", {"start": v(208.03, -32) * mm, "end": v(208.03, -37.08) * mm});
            skLineSegment(sketch, "E30.0.6.9", {"start": v(207.77, -37.08) * mm, "end": v(207.77, -32) * mm});
            skLineSegment(sketch, "E30.0.6.10", {"start": v(208.03, -37.08) * mm, "end": v(213.1, -37.08) * mm});
            skLineSegment(sketch, "E30.0.6.11", {"start": v(207.77, -32) * mm, "end": v(202.7, -32) * mm});
            skLineSegment(sketch, "E30.0.6.12", {"start": v(218.44, -37.08) * mm, "end": v(218.44, -32) * mm});
            skLineSegment(sketch, "E30.0.6.13", {"start": v(202.7, -32) * mm, "end": v(202.7, -37.08) * mm});
            skLineSegment(sketch, "E30.0.6.14", {"start": v(218.7, -37.08) * mm, "end": v(223.77, -37.08) * mm});
            skLineSegment(sketch, "E30.0.6.15", {"start": v(218.44, -32) * mm, "end": v(213.36, -32) * mm});
            skLineSegment(sketch, "E30.0.7.0", {"start": v(202.7, -42.42) * mm, "end": v(207.77, -42.42) * mm});
            skLineSegment(sketch, "E30.0.7.1", {"start": v(223.77, -37.34) * mm, "end": v(218.7, -37.34) * mm});
            skLineSegment(sketch, "E30.0.7.2", {"start": v(213.36, -37.34) * mm, "end": v(213.36, -42.42) * mm});
            skLineSegment(sketch, "E30.0.7.3", {"start": v(213.1, -42.42) * mm, "end": v(213.1, -37.34) * mm});
            skLineSegment(sketch, "E30.0.7.4", {"start": v(218.7, -37.34) * mm, "end": v(218.7, -42.42) * mm});
            skLineSegment(sketch, "E30.0.7.5", {"start": v(213.36, -42.42) * mm, "end": v(218.44, -42.42) * mm});
            skLineSegment(sketch, "E30.0.7.6", {"start": v(213.1, -37.34) * mm, "end": v(208.03, -37.34) * mm});
            skLineSegment(sketch, "E30.0.7.7", {"start": v(223.77, -42.42) * mm, "end": v(223.77, -37.34) * mm});
            skLineSegment(sketch, "E30.0.7.8", {"start": v(208.03, -37.34) * mm, "end": v(208.03, -42.42) * mm});
            skLineSegment(sketch, "E30.0.7.9", {"start": v(207.77, -42.42) * mm, "end": v(207.77, -37.34) * mm});
            skLineSegment(sketch, "E30.0.7.10", {"start": v(208.03, -42.42) * mm, "end": v(213.1, -42.42) * mm});
            skLineSegment(sketch, "E30.0.7.11", {"start": v(207.77, -37.34) * mm, "end": v(202.7, -37.34) * mm});
            skLineSegment(sketch, "E30.0.7.12", {"start": v(218.44, -42.42) * mm, "end": v(218.44, -37.34) * mm});
            skLineSegment(sketch, "E30.0.7.13", {"start": v(202.7, -37.34) * mm, "end": v(202.7, -42.42) * mm});
            skLineSegment(sketch, "E30.0.7.14", {"start": v(218.7, -42.42) * mm, "end": v(223.77, -42.42) * mm});
            skLineSegment(sketch, "E30.0.7.15", {"start": v(218.44, -37.34) * mm, "end": v(213.36, -37.34) * mm});
            skLineSegment(sketch, "E30.0.8.0", {"start": v(202.7, -47.75) * mm, "end": v(207.77, -47.75) * mm});
            skLineSegment(sketch, "E30.0.8.1", {"start": v(223.77, -42.67) * mm, "end": v(218.7, -42.67) * mm});
            skLineSegment(sketch, "E30.0.8.2", {"start": v(213.36, -42.67) * mm, "end": v(213.36, -47.75) * mm});
            skLineSegment(sketch, "E30.0.8.3", {"start": v(213.1, -47.75) * mm, "end": v(213.1, -42.67) * mm});
            skLineSegment(sketch, "E30.0.8.4", {"start": v(218.7, -42.67) * mm, "end": v(218.7, -47.75) * mm});
            skLineSegment(sketch, "E30.0.8.5", {"start": v(213.36, -47.75) * mm, "end": v(218.44, -47.75) * mm});
            skLineSegment(sketch, "E30.0.8.6", {"start": v(213.1, -42.67) * mm, "end": v(208.03, -42.67) * mm});
            skLineSegment(sketch, "E30.0.8.7", {"start": v(223.77, -47.75) * mm, "end": v(223.77, -42.67) * mm});
            skLineSegment(sketch, "E30.0.8.8", {"start": v(208.03, -42.67) * mm, "end": v(208.03, -47.75) * mm});
            skLineSegment(sketch, "E30.0.8.9", {"start": v(207.77, -47.75) * mm, "end": v(207.77, -42.67) * mm});
            skLineSegment(sketch, "E30.0.8.10", {"start": v(208.03, -47.75) * mm, "end": v(213.1, -47.75) * mm});
            skLineSegment(sketch, "E30.0.8.11", {"start": v(207.77, -42.67) * mm, "end": v(202.7, -42.67) * mm});
            skLineSegment(sketch, "E30.0.8.12", {"start": v(218.44, -47.75) * mm, "end": v(218.44, -42.67) * mm});
            skLineSegment(sketch, "E30.0.8.13", {"start": v(202.7, -42.67) * mm, "end": v(202.7, -47.75) * mm});
            skLineSegment(sketch, "E30.0.8.14", {"start": v(218.7, -47.75) * mm, "end": v(223.77, -47.75) * mm});
            skLineSegment(sketch, "E30.0.8.15", {"start": v(218.44, -42.67) * mm, "end": v(213.36, -42.67) * mm});
            skLineSegment(sketch, "E30.0.9.0", {"start": v(202.7, -53.09) * mm, "end": v(207.77, -53.09) * mm});
            skLineSegment(sketch, "E30.0.9.1", {"start": v(223.77, -48) * mm, "end": v(218.7, -48) * mm});
            skLineSegment(sketch, "E30.0.9.2", {"start": v(213.36, -48) * mm, "end": v(213.36, -53.09) * mm});
            skLineSegment(sketch, "E30.0.9.3", {"start": v(213.1, -53.09) * mm, "end": v(213.1, -48) * mm});
            skLineSegment(sketch, "E30.0.9.4", {"start": v(218.7, -48) * mm, "end": v(218.7, -53.09) * mm});
            skLineSegment(sketch, "E30.0.9.5", {"start": v(213.36, -53.09) * mm, "end": v(218.44, -53.09) * mm});
            skLineSegment(sketch, "E30.0.9.6", {"start": v(213.1, -48) * mm, "end": v(208.03, -48) * mm});
            skLineSegment(sketch, "E30.0.9.7", {"start": v(223.77, -53.09) * mm, "end": v(223.77, -48) * mm});
            skLineSegment(sketch, "E30.0.9.8", {"start": v(208.03, -48) * mm, "end": v(208.03, -53.09) * mm});
            skLineSegment(sketch, "E30.0.9.9", {"start": v(207.77, -53.09) * mm, "end": v(207.77, -48) * mm});
            skLineSegment(sketch, "E30.0.9.10", {"start": v(208.03, -53.09) * mm, "end": v(213.1, -53.09) * mm});
            skLineSegment(sketch, "E30.0.9.11", {"start": v(207.77, -48) * mm, "end": v(202.7, -48) * mm});
            skLineSegment(sketch, "E30.0.9.12", {"start": v(218.44, -53.09) * mm, "end": v(218.44, -48) * mm});
            skLineSegment(sketch, "E30.0.9.13", {"start": v(202.7, -48) * mm, "end": v(202.7, -53.09) * mm});
            skLineSegment(sketch, "E30.0.9.14", {"start": v(218.7, -53.09) * mm, "end": v(223.77, -53.09) * mm});
            skLineSegment(sketch, "E30.0.9.15", {"start": v(218.44, -48) * mm, "end": v(213.36, -48) * mm});
            skLineSegment(sketch, "E30.direction1", {"start": v(202.7, -5.08) * mm, "end": v(228.1, -5.08) * mm, "construction": true});
            skLineSegment(sketch, "E30.direction2", {"start": v(202.7, -5.08) * mm, "end": v(202.7, -10.41) * mm, "construction": true});
            skSolve(sketch);
        }
        {
            var Q0;
            Q0=qCreatedBy(makeId("Top.planeOp"),FACE);
            var sketch = newSketch(context, id + "F11", { "sketchPlane" : qUnion([Q0])});
            skLineSegment(sketch, "E31.0.0", {"start": v(229.1, -5.08) * mm, "end": v(229.1, 0) * mm});
            skLineSegment(sketch, "E31.0.1", {"start": v(229.1, 0) * mm, "end": v(224.03, 0) * mm});
            skLineSegment(sketch, "E31.0.2", {"start": v(224.03, 0) * mm, "end": v(224.03, -5.08) * mm});
            skLineSegment(sketch, "E31.0.3", {"start": v(224.03, -5.08) * mm, "end": v(229.1, -5.08) * mm});
            skLineSegment(sketch, "E31.1.0", {"start": v(234.44, -5.08) * mm, "end": v(234.44, 0) * mm});
            skLineSegment(sketch, "E31.1.1", {"start": v(234.44, 0) * mm, "end": v(229.36, 0) * mm});
            skLineSegment(sketch, "E31.1.2", {"start": v(229.36, 0) * mm, "end": v(229.36, -5.08) * mm});
            skLineSegment(sketch, "E31.1.3", {"start": v(229.36, -5.08) * mm, "end": v(234.44, -5.08) * mm});
            skLineSegment(sketch, "E31.2.0", {"start": v(239.78, -5.08) * mm, "end": v(239.78, 0) * mm});
            skLineSegment(sketch, "E31.2.1", {"start": v(239.78, 0) * mm, "end": v(234.7, 0) * mm});
            skLineSegment(sketch, "E31.2.2", {"start": v(234.7, 0) * mm, "end": v(234.7, -5.08) * mm});
            skLineSegment(sketch, "E31.2.3", {"start": v(234.7, -5.08) * mm, "end": v(239.78, -5.08) * mm});
            skLineSegment(sketch, "E31.3.0", {"start": v(245.11, -5.08) * mm, "end": v(245.11, 0) * mm});
            skLineSegment(sketch, "E31.3.1", {"start": v(245.11, 0) * mm, "end": v(240.03, 0) * mm});
            skLineSegment(sketch, "E31.3.2", {"start": v(240.03, 0) * mm, "end": v(240.03, -5.08) * mm});
            skLineSegment(sketch, "E31.3.3", {"start": v(240.03, -5.08) * mm, "end": v(245.11, -5.08) * mm});
            skLineSegment(sketch, "E31.4.0", {"start": v(250.44, -5.08) * mm, "end": v(250.44, 0) * mm});
            skLineSegment(sketch, "E31.4.1", {"start": v(250.44, 0) * mm, "end": v(245.36, 0) * mm});
            skLineSegment(sketch, "E31.4.2", {"start": v(245.36, 0) * mm, "end": v(245.36, -5.08) * mm});
            skLineSegment(sketch, "E31.4.3", {"start": v(245.36, -5.08) * mm, "end": v(250.44, -5.08) * mm});
            skLineSegment(sketch, "E31.5.0", {"start": v(255.78, -5.08) * mm, "end": v(255.78, 0) * mm});
            skLineSegment(sketch, "E31.5.1", {"start": v(255.78, 0) * mm, "end": v(250.7, 0) * mm});
            skLineSegment(sketch, "E31.5.2", {"start": v(250.7, 0) * mm, "end": v(250.7, -5.08) * mm});
            skLineSegment(sketch, "E31.5.3", {"start": v(250.7, -5.08) * mm, "end": v(255.78, -5.08) * mm});
            skLineSegment(sketch, "E32.0.1.0", {"start": v(234.44, -5.33) * mm, "end": v(229.36, -5.33) * mm});
            skLineSegment(sketch, "E32.0.1.1", {"start": v(255.78, -5.33) * mm, "end": v(250.7, -5.33) * mm});
            skLineSegment(sketch, "E32.0.1.2", {"start": v(255.78, -10.41) * mm, "end": v(255.78, -5.33) * mm});
            skLineSegment(sketch, "E32.0.1.3", {"start": v(245.36, -10.41) * mm, "end": v(250.44, -10.41) * mm});
            skLineSegment(sketch, "E32.0.1.4", {"start": v(245.36, -5.33) * mm, "end": v(245.36, -10.41) * mm});
            skLineSegment(sketch, "E32.0.1.5", {"start": v(229.36, -10.41) * mm, "end": v(234.44, -10.41) * mm});
            skLineSegment(sketch, "E32.0.1.6", {"start": v(250.44, -5.33) * mm, "end": v(245.36, -5.33) * mm});
            skLineSegment(sketch, "E32.0.1.7", {"start": v(239.78, -10.41) * mm, "end": v(239.78, -5.33) * mm});
            skLineSegment(sketch, "E32.0.1.8", {"start": v(240.03, -10.41) * mm, "end": v(245.11, -10.41) * mm});
            skLineSegment(sketch, "E32.0.1.9", {"start": v(250.44, -10.41) * mm, "end": v(250.44, -5.33) * mm});
            skLineSegment(sketch, "E32.0.1.10", {"start": v(239.78, -5.33) * mm, "end": v(234.7, -5.33) * mm});
            skLineSegment(sketch, "E32.0.1.11", {"start": v(245.11, -5.33) * mm, "end": v(240.03, -5.33) * mm});
            skLineSegment(sketch, "E32.0.1.12", {"start": v(240.03, -5.33) * mm, "end": v(240.03, -10.41) * mm});
            skLineSegment(sketch, "E32.0.1.13", {"start": v(234.7, -10.41) * mm, "end": v(239.78, -10.41) * mm});
            skLineSegment(sketch, "E32.0.1.14", {"start": v(245.11, -10.41) * mm, "end": v(245.11, -5.33) * mm});
            skLineSegment(sketch, "E32.0.1.15", {"start": v(229.1, -10.41) * mm, "end": v(229.1, -5.33) * mm});
            skLineSegment(sketch, "E32.0.1.16", {"start": v(250.7, -10.41) * mm, "end": v(255.78, -10.41) * mm});
            skLineSegment(sketch, "E32.0.1.17", {"start": v(229.1, -5.33) * mm, "end": v(224.03, -5.33) * mm});
            skLineSegment(sketch, "E32.0.1.18", {"start": v(250.7, -5.33) * mm, "end": v(250.7, -10.41) * mm});
            skLineSegment(sketch, "E32.0.1.19", {"start": v(224.03, -5.33) * mm, "end": v(224.03, -10.41) * mm});
            skLineSegment(sketch, "E32.0.1.20", {"start": v(224.03, -10.41) * mm, "end": v(229.1, -10.41) * mm});
            skLineSegment(sketch, "E32.0.1.21", {"start": v(234.44, -10.41) * mm, "end": v(234.44, -5.33) * mm});
            skLineSegment(sketch, "E32.0.1.22", {"start": v(229.36, -5.33) * mm, "end": v(229.36, -10.41) * mm});
            skLineSegment(sketch, "E32.0.1.23", {"start": v(234.7, -5.33) * mm, "end": v(234.7, -10.41) * mm});
            skLineSegment(sketch, "E32.0.2.0", {"start": v(234.44, -10.67) * mm, "end": v(229.36, -10.67) * mm});
            skLineSegment(sketch, "E32.0.2.1", {"start": v(255.78, -10.67) * mm, "end": v(250.7, -10.67) * mm});
            skLineSegment(sketch, "E32.0.2.2", {"start": v(255.78, -15.75) * mm, "end": v(255.78, -10.67) * mm});
            skLineSegment(sketch, "E32.0.2.3", {"start": v(245.36, -15.75) * mm, "end": v(250.44, -15.75) * mm});
            skLineSegment(sketch, "E32.0.2.4", {"start": v(245.36, -10.67) * mm, "end": v(245.36, -15.75) * mm});
            skLineSegment(sketch, "E32.0.2.5", {"start": v(229.36, -15.75) * mm, "end": v(234.44, -15.75) * mm});
            skLineSegment(sketch, "E32.0.2.6", {"start": v(250.44, -10.67) * mm, "end": v(245.36, -10.67) * mm});
            skLineSegment(sketch, "E32.0.2.7", {"start": v(239.78, -15.75) * mm, "end": v(239.78, -10.67) * mm});
            skLineSegment(sketch, "E32.0.2.8", {"start": v(240.03, -15.75) * mm, "end": v(245.11, -15.75) * mm});
            skLineSegment(sketch, "E32.0.2.9", {"start": v(250.44, -15.75) * mm, "end": v(250.44, -10.67) * mm});
            skLineSegment(sketch, "E32.0.2.10", {"start": v(239.78, -10.67) * mm, "end": v(234.7, -10.67) * mm});
            skLineSegment(sketch, "E32.0.2.11", {"start": v(245.11, -10.67) * mm, "end": v(240.03, -10.67) * mm});
            skLineSegment(sketch, "E32.0.2.12", {"start": v(240.03, -10.67) * mm, "end": v(240.03, -15.75) * mm});
            skLineSegment(sketch, "E32.0.2.13", {"start": v(234.7, -15.75) * mm, "end": v(239.78, -15.75) * mm});
            skLineSegment(sketch, "E32.0.2.14", {"start": v(245.11, -15.75) * mm, "end": v(245.11, -10.67) * mm});
            skLineSegment(sketch, "E32.0.2.15", {"start": v(229.1, -15.75) * mm, "end": v(229.1, -10.67) * mm});
            skLineSegment(sketch, "E32.0.2.16", {"start": v(250.7, -15.75) * mm, "end": v(255.78, -15.75) * mm});
            skLineSegment(sketch, "E32.0.2.17", {"start": v(229.1, -10.67) * mm, "end": v(224.03, -10.67) * mm});
            skLineSegment(sketch, "E32.0.2.18", {"start": v(250.7, -10.67) * mm, "end": v(250.7, -15.75) * mm});
            skLineSegment(sketch, "E32.0.2.19", {"start": v(224.03, -10.67) * mm, "end": v(224.03, -15.75) * mm});
            skLineSegment(sketch, "E32.0.2.20", {"start": v(224.03, -15.75) * mm, "end": v(229.1, -15.75) * mm});
            skLineSegment(sketch, "E32.0.2.21", {"start": v(234.44, -15.75) * mm, "end": v(234.44, -10.67) * mm});
            skLineSegment(sketch, "E32.0.2.22", {"start": v(229.36, -10.67) * mm, "end": v(229.36, -15.75) * mm});
            skLineSegment(sketch, "E32.0.2.23", {"start": v(234.7, -10.67) * mm, "end": v(234.7, -15.75) * mm});
            skLineSegment(sketch, "E32.0.3.0", {"start": v(234.44, -16) * mm, "end": v(229.36, -16) * mm});
            skLineSegment(sketch, "E32.0.3.1", {"start": v(255.78, -16) * mm, "end": v(250.7, -16) * mm});
            skLineSegment(sketch, "E32.0.3.2", {"start": v(255.78, -21.08) * mm, "end": v(255.78, -16) * mm});
            skLineSegment(sketch, "E32.0.3.3", {"start": v(245.36, -21.08) * mm, "end": v(250.44, -21.08) * mm});
            skLineSegment(sketch, "E32.0.3.4", {"start": v(245.36, -16) * mm, "end": v(245.36, -21.08) * mm});
            skLineSegment(sketch, "E32.0.3.5", {"start": v(229.36, -21.08) * mm, "end": v(234.44, -21.08) * mm});
            skLineSegment(sketch, "E32.0.3.6", {"start": v(250.44, -16) * mm, "end": v(245.36, -16) * mm});
            skLineSegment(sketch, "E32.0.3.7", {"start": v(239.78, -21.08) * mm, "end": v(239.78, -16) * mm});
            skLineSegment(sketch, "E32.0.3.8", {"start": v(240.03, -21.08) * mm, "end": v(245.11, -21.08) * mm});
            skLineSegment(sketch, "E32.0.3.9", {"start": v(250.44, -21.08) * mm, "end": v(250.44, -16) * mm});
            skLineSegment(sketch, "E32.0.3.10", {"start": v(239.78, -16) * mm, "end": v(234.7, -16) * mm});
            skLineSegment(sketch, "E32.0.3.11", {"start": v(245.11, -16) * mm, "end": v(240.03, -16) * mm});
            skLineSegment(sketch, "E32.0.3.12", {"start": v(240.03, -16) * mm, "end": v(240.03, -21.08) * mm});
            skLineSegment(sketch, "E32.0.3.13", {"start": v(234.7, -21.08) * mm, "end": v(239.78, -21.08) * mm});
            skLineSegment(sketch, "E32.0.3.14", {"start": v(245.11, -21.08) * mm, "end": v(245.11, -16) * mm});
            skLineSegment(sketch, "E32.0.3.15", {"start": v(229.1, -21.08) * mm, "end": v(229.1, -16) * mm});
            skLineSegment(sketch, "E32.0.3.16", {"start": v(250.7, -21.08) * mm, "end": v(255.78, -21.08) * mm});
            skLineSegment(sketch, "E32.0.3.17", {"start": v(229.1, -16) * mm, "end": v(224.03, -16) * mm});
            skLineSegment(sketch, "E32.0.3.18", {"start": v(250.7, -16) * mm, "end": v(250.7, -21.08) * mm});
            skLineSegment(sketch, "E32.0.3.19", {"start": v(224.03, -16) * mm, "end": v(224.03, -21.08) * mm});
            skLineSegment(sketch, "E32.0.3.20", {"start": v(224.03, -21.08) * mm, "end": v(229.1, -21.08) * mm});
            skLineSegment(sketch, "E32.0.3.21", {"start": v(234.44, -21.08) * mm, "end": v(234.44, -16) * mm});
            skLineSegment(sketch, "E32.0.3.22", {"start": v(229.36, -16) * mm, "end": v(229.36, -21.08) * mm});
            skLineSegment(sketch, "E32.0.3.23", {"start": v(234.7, -16) * mm, "end": v(234.7, -21.08) * mm});
            skLineSegment(sketch, "E32.0.4.0", {"start": v(234.44, -21.34) * mm, "end": v(229.36, -21.34) * mm});
            skLineSegment(sketch, "E32.0.4.1", {"start": v(255.78, -21.34) * mm, "end": v(250.7, -21.34) * mm});
            skLineSegment(sketch, "E32.0.4.2", {"start": v(255.78, -26.42) * mm, "end": v(255.78, -21.34) * mm});
            skLineSegment(sketch, "E32.0.4.3", {"start": v(245.36, -26.42) * mm, "end": v(250.44, -26.42) * mm});
            skLineSegment(sketch, "E32.0.4.4", {"start": v(245.36, -21.34) * mm, "end": v(245.36, -26.42) * mm});
            skLineSegment(sketch, "E32.0.4.5", {"start": v(229.36, -26.42) * mm, "end": v(234.44, -26.42) * mm});
            skLineSegment(sketch, "E32.0.4.6", {"start": v(250.44, -21.34) * mm, "end": v(245.36, -21.34) * mm});
            skLineSegment(sketch, "E32.0.4.7", {"start": v(239.78, -26.42) * mm, "end": v(239.78, -21.34) * mm});
            skLineSegment(sketch, "E32.0.4.8", {"start": v(240.03, -26.42) * mm, "end": v(245.11, -26.42) * mm});
            skLineSegment(sketch, "E32.0.4.9", {"start": v(250.44, -26.42) * mm, "end": v(250.44, -21.34) * mm});
            skLineSegment(sketch, "E32.0.4.10", {"start": v(239.78, -21.34) * mm, "end": v(234.7, -21.34) * mm});
            skLineSegment(sketch, "E32.0.4.11", {"start": v(245.11, -21.34) * mm, "end": v(240.03, -21.34) * mm});
            skLineSegment(sketch, "E32.0.4.12", {"start": v(240.03, -21.34) * mm, "end": v(240.03, -26.42) * mm});
            skLineSegment(sketch, "E32.0.4.13", {"start": v(234.7, -26.42) * mm, "end": v(239.78, -26.42) * mm});
            skLineSegment(sketch, "E32.0.4.14", {"start": v(245.11, -26.42) * mm, "end": v(245.11, -21.34) * mm});
            skLineSegment(sketch, "E32.0.4.15", {"start": v(229.1, -26.42) * mm, "end": v(229.1, -21.34) * mm});
            skLineSegment(sketch, "E32.0.4.16", {"start": v(250.7, -26.42) * mm, "end": v(255.78, -26.42) * mm});
            skLineSegment(sketch, "E32.0.4.17", {"start": v(229.1, -21.34) * mm, "end": v(224.03, -21.34) * mm});
            skLineSegment(sketch, "E32.0.4.18", {"start": v(250.7, -21.34) * mm, "end": v(250.7, -26.42) * mm});
            skLineSegment(sketch, "E32.0.4.19", {"start": v(224.03, -21.34) * mm, "end": v(224.03, -26.42) * mm});
            skLineSegment(sketch, "E32.0.4.20", {"start": v(224.03, -26.42) * mm, "end": v(229.1, -26.42) * mm});
            skLineSegment(sketch, "E32.0.4.21", {"start": v(234.44, -26.42) * mm, "end": v(234.44, -21.34) * mm});
            skLineSegment(sketch, "E32.0.4.22", {"start": v(229.36, -21.34) * mm, "end": v(229.36, -26.42) * mm});
            skLineSegment(sketch, "E32.0.4.23", {"start": v(234.7, -21.34) * mm, "end": v(234.7, -26.42) * mm});
            skLineSegment(sketch, "E32.direction1", {"start": v(224.03, -5.08) * mm, "end": v(249.43, -5.08) * mm, "construction": true});
            skLineSegment(sketch, "E32.direction2", {"start": v(224.03, -5.08) * mm, "end": v(224.03, -10.41) * mm, "construction": true});
            skSolve(sketch);
        }
        {
            var Q0;
            Q0=qCreatedBy(makeId("Front.planeOp"),FACE);
            var sketch = newSketch(context, id + "F12", { "sketchPlane" : qUnion([Q0])});
            skLineSegment(sketch, "E33", {"start": v(0, 59.59) * mm, "end": v(8.04, 69.07) * mm});
            skLineSegment(sketch, "E34", {"start": v(8.04, 69.07) * mm, "end": v(15.17, 63.03) * mm});
            skLineSegment(sketch, "E35", {"start": v(15.17, 63.03) * mm, "end": v(32.99, 93.67) * mm});
            skLineSegment(sketch, "E36", {"start": v(32.99, 93.67) * mm, "end": v(50.56, 121.44) * mm});
            skLineSegment(sketch, "E37", {"start": v(50.56, 121.44) * mm, "end": v(63.75, 113.09) * mm});
            skLineSegment(sketch, "E38", {"start": v(63.75, 113.09) * mm, "end": v(82.35, 142.49) * mm});
            skLineSegment(sketch, "E39", {"start": v(82.35, 142.49) * mm, "end": v(88.87, 146.04) * mm});
            skLineSegment(sketch, "E40", {"start": v(88.87, 146.04) * mm, "end": v(97.65, 151.66) * mm});
            skLineSegment(sketch, "E41", {"start": v(97.65, 151.66) * mm, "end": v(114.52, 154.82) * mm});
            skLineSegment(sketch, "E42", {"start": v(114.52, 154.82) * mm, "end": v(122.6, 149.55) * mm});
            skLineSegment(sketch, "E43", {"start": v(122.6, 149.55) * mm, "end": v(135.96, 159.74) * mm});
            skLineSegment(sketch, "E44", {"start": v(135.96, 159.74) * mm, "end": v(151.95, 138.78) * mm});
            skLineSegment(sketch, "E45", {"start": v(151.95, 138.78) * mm, "end": v(169.7, 142.87) * mm});
            skLineSegment(sketch, "E46", {"start": v(169.7, 142.87) * mm, "end": v(185.86, 119.33) * mm});
            skLineSegment(sketch, "E47", {"start": v(185.86, 119.33) * mm, "end": v(202.58, 130.81) * mm});
            skLineSegment(sketch, "E48", {"start": v(202.58, 130.81) * mm, "end": v(225.76, 97.05) * mm});
            skLineSegment(sketch, "E49", {"start": v(225.76, 97.05) * mm, "end": v(255.79, 164.08) * mm});
            skLineSegment(sketch, "E50", {"start": v(255.79, 164.08) * mm, "end": v(255.79, 0) * mm});
            skLineSegment(sketch, "E51", {"start": v(255.79, 0) * mm, "end": v(0, 0) * mm});
            skLineSegment(sketch, "E52", {"start": v(0, 0) * mm, "end": v(0, 59.59) * mm});
            skSolve(sketch);
        }
        {
            var Q0;
            Q0 = qSketchRegion(id + "F1", true);
            extrude(context, id + "F13", {"entities" : qUnion([Q0]), "depth" : 200.66 * mm, "offsetDistance" : 25.4 * mm});
        }
        {
            var Q0;
            Q0 = qSketchRegion(id + "F2", true);
            var Q1;
            Q1 = qSketchRegion(id + "F3", true);
            var Q2;
            Q2 = qSketchRegion(id + "F4", true);
            var Q3;
            Q3 = qSketchRegion(id + "F5", true);
            var Q4;
            Q4 = qSketchRegion(id + "F6", true);
            var Q5;
            Q5 = qSketchRegion(id + "F7", true);
            var Q6;
            Q6 = qSketchRegion(id + "F8", true);
            var Q7;
            Q7 = qSketchRegion(id + "F9", true);
            var Q8;
            Q8 = qSketchRegion(id + "F10", true);
            var Q9;
            Q9 = qSketchRegion(id + "F11", true);
            extrude(context, id + "F14", {"entities" : qUnion([Q0, Q1, Q2, Q3, Q4, Q5, Q6, Q7, Q8, Q9]), "depth" : 200.66 * mm, "offsetDistance" : 25.4 * mm});
        }
        {
            var Q0;
            Q0 = qSketchRegion(id + "F12", true);
            extrude(context, id + "F15", {"entities" : qUnion([Q0]), "operationType" : NewBodyOperationType.INTERSECT, "endBound" : BoundingType.THROUGH_ALL, "depth" : 216.66 * mm, "offsetDistance" : 25.4 * mm});
        }
    });
